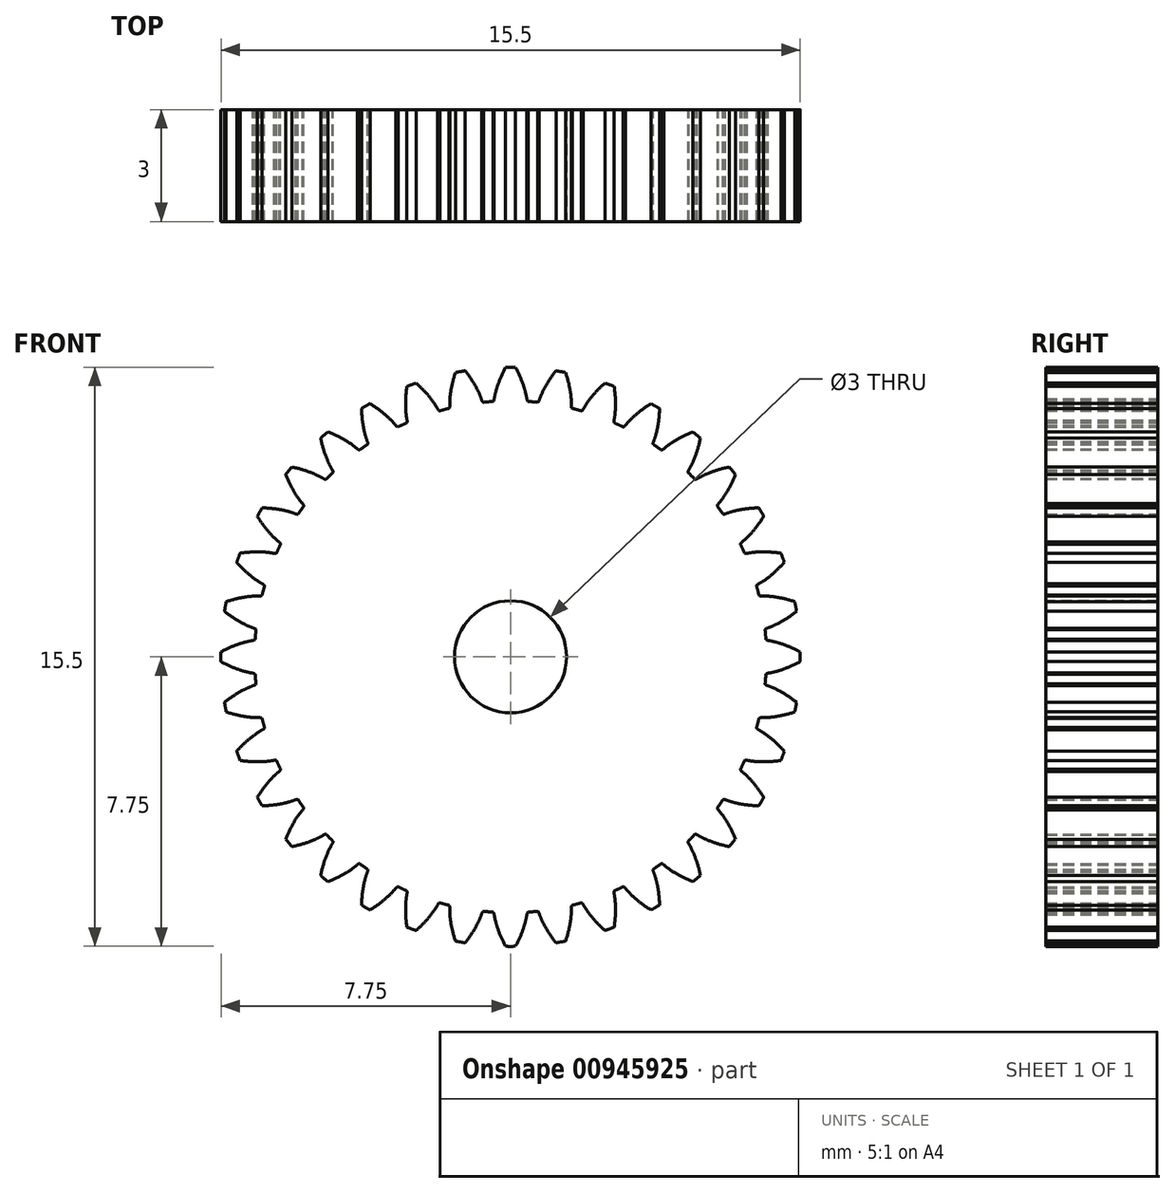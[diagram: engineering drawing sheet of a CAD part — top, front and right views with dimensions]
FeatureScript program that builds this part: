
annotation { "Feature Type Name" : "Feature", "Feature Type Description" : "" }
export const myFeature = defineFeature(function(context is Context, id is Id, definition is map)
    precondition{}
    {
        {
            var Q0;
            Q0=qCreatedBy(makeId("Front.planeOp"),FACE);
            var sketch = newSketch(context, id + "F0", { "sketchPlane" : qUnion([Q0])});
            skLineSegment(sketch, "E0", {"start": v(-0.47, 6.84) * mm, "end": v(-0.47, 6.84) * mm});
            skLineSegment(sketch, "E1", {"start": v(-0.47, 6.84) * mm, "end": v(-0.46, 6.84) * mm});
            skLineSegment(sketch, "E2", {"start": v(-0.46, 6.84) * mm, "end": v(-0.45, 6.85) * mm});
            skLineSegment(sketch, "E3", {"start": v(-0.45, 6.85) * mm, "end": v(-0.45, 6.86) * mm});
            skLineSegment(sketch, "E4", {"start": v(-0.45, 6.86) * mm, "end": v(-0.45, 6.87) * mm});
            skLineSegment(sketch, "E5", {"start": v(-0.45, 6.87) * mm, "end": v(-0.44, 6.88) * mm});
            skLineSegment(sketch, "E6", {"start": v(-0.44, 6.88) * mm, "end": v(-0.44, 6.9) * mm});
            skLineSegment(sketch, "E7", {"start": v(-0.44, 6.9) * mm, "end": v(-0.44, 6.9) * mm});
            skLineSegment(sketch, "E8", {"start": v(-0.44, 6.9) * mm, "end": v(-0.43, 6.92) * mm});
            skLineSegment(sketch, "E9", {"start": v(-0.43, 6.92) * mm, "end": v(-0.43, 6.93) * mm});
            skLineSegment(sketch, "E10", {"start": v(-0.43, 6.93) * mm, "end": v(-0.43, 6.94) * mm});
            skLineSegment(sketch, "E11", {"start": v(-0.43, 6.94) * mm, "end": v(-0.43, 6.96) * mm});
            skLineSegment(sketch, "E12", {"start": v(-0.43, 6.96) * mm, "end": v(-0.42, 6.97) * mm});
            skLineSegment(sketch, "E13", {"start": v(-0.42, 6.97) * mm, "end": v(-0.42, 6.99) * mm});
            skLineSegment(sketch, "E14", {"start": v(-0.42, 6.99) * mm, "end": v(-0.42, 7) * mm});
            skLineSegment(sketch, "E15", {"start": v(-0.42, 7) * mm, "end": v(-0.41, 7.02) * mm});
            skLineSegment(sketch, "E16", {"start": v(-0.41, 7.02) * mm, "end": v(-0.41, 7.04) * mm});
            skLineSegment(sketch, "E17", {"start": v(-0.41, 7.04) * mm, "end": v(-0.4, 7.06) * mm});
            skLineSegment(sketch, "E18", {"start": v(-0.4, 7.06) * mm, "end": v(-0.4, 7.07) * mm});
            skLineSegment(sketch, "E19", {"start": v(-0.4, 7.07) * mm, "end": v(-0.4, 7.1) * mm});
            skLineSegment(sketch, "E20", {"start": v(-0.4, 7.1) * mm, "end": v(-0.4, 7.11) * mm});
            skLineSegment(sketch, "E21", {"start": v(-0.4, 7.11) * mm, "end": v(-0.39, 7.13) * mm});
            skLineSegment(sketch, "E22", {"start": v(-0.39, 7.13) * mm, "end": v(-0.38, 7.15) * mm});
            skLineSegment(sketch, "E23", {"start": v(-0.38, 7.15) * mm, "end": v(-0.38, 7.17) * mm});
            skLineSegment(sketch, "E24", {"start": v(-0.38, 7.17) * mm, "end": v(-0.37, 7.2) * mm});
            skLineSegment(sketch, "E25", {"start": v(-0.37, 7.2) * mm, "end": v(-0.36, 7.21) * mm});
            skLineSegment(sketch, "E26", {"start": v(-0.36, 7.21) * mm, "end": v(-0.36, 7.23) * mm});
            skLineSegment(sketch, "E27", {"start": v(-0.36, 7.23) * mm, "end": v(-0.35, 7.26) * mm});
            skLineSegment(sketch, "E28", {"start": v(-0.35, 7.26) * mm, "end": v(-0.34, 7.28) * mm});
            skLineSegment(sketch, "E29", {"start": v(-0.34, 7.28) * mm, "end": v(-0.33, 7.3) * mm});
            skLineSegment(sketch, "E30", {"start": v(-0.33, 7.3) * mm, "end": v(-0.32, 7.32) * mm});
            skLineSegment(sketch, "E31", {"start": v(-0.32, 7.32) * mm, "end": v(-0.32, 7.35) * mm});
            skLineSegment(sketch, "E32", {"start": v(-0.32, 7.35) * mm, "end": v(-0.3, 7.37) * mm});
            skLineSegment(sketch, "E33", {"start": v(-0.3, 7.37) * mm, "end": v(-0.3, 7.4) * mm});
            skLineSegment(sketch, "E34", {"start": v(-0.3, 7.4) * mm, "end": v(-0.29, 7.42) * mm});
            skLineSegment(sketch, "E35", {"start": v(-0.29, 7.42) * mm, "end": v(-0.28, 7.45) * mm});
            skLineSegment(sketch, "E36", {"start": v(-0.28, 7.45) * mm, "end": v(-0.27, 7.47) * mm});
            skLineSegment(sketch, "E37", {"start": v(-0.27, 7.47) * mm, "end": v(-0.25, 7.5) * mm});
            skLineSegment(sketch, "E38", {"start": v(-0.25, 7.5) * mm, "end": v(-0.24, 7.53) * mm});
            skLineSegment(sketch, "E39", {"start": v(-0.24, 7.53) * mm, "end": v(-0.23, 7.55) * mm});
            skLineSegment(sketch, "E40", {"start": v(-0.23, 7.55) * mm, "end": v(-0.22, 7.58) * mm});
            skLineSegment(sketch, "E41", {"start": v(-0.22, 7.58) * mm, "end": v(-0.2, 7.6) * mm});
            skLineSegment(sketch, "E42", {"start": v(-0.2, 7.6) * mm, "end": v(-0.2, 7.64) * mm});
            skLineSegment(sketch, "E43", {"start": v(-0.2, 7.64) * mm, "end": v(-0.18, 7.66) * mm});
            skLineSegment(sketch, "E44", {"start": v(-0.18, 7.66) * mm, "end": v(-0.16, 7.7) * mm});
            skLineSegment(sketch, "E45", {"start": v(-0.16, 7.7) * mm, "end": v(-0.15, 7.72) * mm});
            skLineSegment(sketch, "E46", {"start": v(-0.15, 7.72) * mm, "end": v(-0.13, 7.75) * mm});
            skLineSegment(sketch, "E47", {"start": v(0.47, 6.84) * mm, "end": v(0.47, 6.84) * mm});
            skLineSegment(sketch, "E48", {"start": v(0.47, 6.84) * mm, "end": v(0.46, 6.84) * mm});
            skLineSegment(sketch, "E49", {"start": v(0.46, 6.84) * mm, "end": v(0.45, 6.85) * mm});
            skLineSegment(sketch, "E50", {"start": v(0.45, 6.85) * mm, "end": v(0.45, 6.86) * mm});
            skLineSegment(sketch, "E51", {"start": v(0.45, 6.86) * mm, "end": v(0.45, 6.87) * mm});
            skLineSegment(sketch, "E52", {"start": v(0.45, 6.87) * mm, "end": v(0.44, 6.88) * mm});
            skLineSegment(sketch, "E53", {"start": v(0.44, 6.88) * mm, "end": v(0.44, 6.9) * mm});
            skLineSegment(sketch, "E54", {"start": v(0.44, 6.9) * mm, "end": v(0.44, 6.9) * mm});
            skLineSegment(sketch, "E55", {"start": v(0.44, 6.9) * mm, "end": v(0.43, 6.92) * mm});
            skLineSegment(sketch, "E56", {"start": v(0.43, 6.92) * mm, "end": v(0.43, 6.93) * mm});
            skLineSegment(sketch, "E57", {"start": v(0.43, 6.93) * mm, "end": v(0.43, 6.94) * mm});
            skLineSegment(sketch, "E58", {"start": v(0.43, 6.94) * mm, "end": v(0.43, 6.96) * mm});
            skLineSegment(sketch, "E59", {"start": v(0.43, 6.96) * mm, "end": v(0.42, 6.97) * mm});
            skLineSegment(sketch, "E60", {"start": v(0.42, 6.97) * mm, "end": v(0.42, 6.99) * mm});
            skLineSegment(sketch, "E61", {"start": v(0.42, 6.99) * mm, "end": v(0.42, 7) * mm});
            skLineSegment(sketch, "E62", {"start": v(0.42, 7) * mm, "end": v(0.41, 7.02) * mm});
            skLineSegment(sketch, "E63", {"start": v(0.41, 7.02) * mm, "end": v(0.41, 7.04) * mm});
            skLineSegment(sketch, "E64", {"start": v(0.41, 7.04) * mm, "end": v(0.4, 7.06) * mm});
            skLineSegment(sketch, "E65", {"start": v(0.4, 7.06) * mm, "end": v(0.4, 7.07) * mm});
            skLineSegment(sketch, "E66", {"start": v(0.4, 7.07) * mm, "end": v(0.4, 7.1) * mm});
            skLineSegment(sketch, "E67", {"start": v(0.4, 7.1) * mm, "end": v(0.4, 7.11) * mm});
            skLineSegment(sketch, "E68", {"start": v(0.4, 7.11) * mm, "end": v(0.39, 7.13) * mm});
            skLineSegment(sketch, "E69", {"start": v(0.39, 7.13) * mm, "end": v(0.38, 7.15) * mm});
            skLineSegment(sketch, "E70", {"start": v(0.38, 7.15) * mm, "end": v(0.38, 7.17) * mm});
            skLineSegment(sketch, "E71", {"start": v(0.38, 7.17) * mm, "end": v(0.37, 7.2) * mm});
            skLineSegment(sketch, "E72", {"start": v(0.37, 7.2) * mm, "end": v(0.36, 7.21) * mm});
            skLineSegment(sketch, "E73", {"start": v(0.36, 7.21) * mm, "end": v(0.36, 7.23) * mm});
            skLineSegment(sketch, "E74", {"start": v(0.36, 7.23) * mm, "end": v(0.35, 7.26) * mm});
            skLineSegment(sketch, "E75", {"start": v(0.35, 7.26) * mm, "end": v(0.34, 7.28) * mm});
            skLineSegment(sketch, "E76", {"start": v(0.34, 7.28) * mm, "end": v(0.33, 7.3) * mm});
            skLineSegment(sketch, "E77", {"start": v(0.33, 7.3) * mm, "end": v(0.32, 7.32) * mm});
            skLineSegment(sketch, "E78", {"start": v(0.32, 7.32) * mm, "end": v(0.32, 7.35) * mm});
            skLineSegment(sketch, "E79", {"start": v(0.32, 7.35) * mm, "end": v(0.3, 7.37) * mm});
            skLineSegment(sketch, "E80", {"start": v(0.3, 7.37) * mm, "end": v(0.3, 7.4) * mm});
            skLineSegment(sketch, "E81", {"start": v(0.3, 7.4) * mm, "end": v(0.29, 7.42) * mm});
            skLineSegment(sketch, "E82", {"start": v(0.29, 7.42) * mm, "end": v(0.28, 7.45) * mm});
            skLineSegment(sketch, "E83", {"start": v(0.28, 7.45) * mm, "end": v(0.27, 7.47) * mm});
            skLineSegment(sketch, "E84", {"start": v(0.27, 7.47) * mm, "end": v(0.25, 7.5) * mm});
            skLineSegment(sketch, "E85", {"start": v(0.25, 7.5) * mm, "end": v(0.24, 7.53) * mm});
            skLineSegment(sketch, "E86", {"start": v(0.24, 7.53) * mm, "end": v(0.23, 7.55) * mm});
            skLineSegment(sketch, "E87", {"start": v(0.23, 7.55) * mm, "end": v(0.22, 7.58) * mm});
            skLineSegment(sketch, "E88", {"start": v(0.22, 7.58) * mm, "end": v(0.2, 7.6) * mm});
            skLineSegment(sketch, "E89", {"start": v(0.2, 7.6) * mm, "end": v(0.2, 7.64) * mm});
            skLineSegment(sketch, "E90", {"start": v(0.2, 7.64) * mm, "end": v(0.18, 7.66) * mm});
            skLineSegment(sketch, "E91", {"start": v(0.18, 7.66) * mm, "end": v(0.16, 7.7) * mm});
            skLineSegment(sketch, "E92", {"start": v(0.16, 7.7) * mm, "end": v(0.15, 7.72) * mm});
            skLineSegment(sketch, "E93", {"start": v(0.15, 7.72) * mm, "end": v(0.13, 7.75) * mm});
            skArc(sketch, "E94", {"start": v(0.13, 7.75) * mm, "mid": v(0, 7.75) * mm, "end": v(-0.13, 7.75) * mm});
            skLineSegment(sketch, "E95", {"start": v(0.72, 6.81) * mm, "end": v(0.73, 6.81) * mm});
            skLineSegment(sketch, "E96", {"start": v(0.73, 6.81) * mm, "end": v(0.73, 6.82) * mm});
            skLineSegment(sketch, "E97", {"start": v(0.73, 6.82) * mm, "end": v(0.74, 6.82) * mm});
            skLineSegment(sketch, "E98", {"start": v(0.74, 6.82) * mm, "end": v(0.75, 6.83) * mm});
            skLineSegment(sketch, "E99", {"start": v(0.75, 6.83) * mm, "end": v(0.75, 6.84) * mm});
            skLineSegment(sketch, "E100", {"start": v(0.75, 6.84) * mm, "end": v(0.76, 6.85) * mm});
            skLineSegment(sketch, "E101", {"start": v(0.76, 6.85) * mm, "end": v(0.77, 6.87) * mm});
            skLineSegment(sketch, "E102", {"start": v(0.77, 6.87) * mm, "end": v(0.77, 6.88) * mm});
            skLineSegment(sketch, "E103", {"start": v(0.77, 6.88) * mm, "end": v(0.77, 6.89) * mm});
            skLineSegment(sketch, "E104", {"start": v(0.77, 6.89) * mm, "end": v(0.78, 6.9) * mm});
            skLineSegment(sketch, "E105", {"start": v(0.78, 6.9) * mm, "end": v(0.78, 6.91) * mm});
            skLineSegment(sketch, "E106", {"start": v(0.78, 6.91) * mm, "end": v(0.79, 6.93) * mm});
            skLineSegment(sketch, "E107", {"start": v(0.79, 6.93) * mm, "end": v(0.8, 6.94) * mm});
            skLineSegment(sketch, "E108", {"start": v(0.8, 6.94) * mm, "end": v(0.8, 6.96) * mm});
            skLineSegment(sketch, "E109", {"start": v(0.8, 6.96) * mm, "end": v(0.8, 6.97) * mm});
            skLineSegment(sketch, "E110", {"start": v(0.8, 6.97) * mm, "end": v(0.81, 6.99) * mm});
            skLineSegment(sketch, "E111", {"start": v(0.81, 6.99) * mm, "end": v(0.82, 7) * mm});
            skLineSegment(sketch, "E112", {"start": v(0.82, 7) * mm, "end": v(0.83, 7.02) * mm});
            skLineSegment(sketch, "E113", {"start": v(0.83, 7.02) * mm, "end": v(0.83, 7.04) * mm});
            skLineSegment(sketch, "E114", {"start": v(0.83, 7.04) * mm, "end": v(0.84, 7.05) * mm});
            skLineSegment(sketch, "E115", {"start": v(0.84, 7.05) * mm, "end": v(0.85, 7.07) * mm});
            skLineSegment(sketch, "E116", {"start": v(0.85, 7.07) * mm, "end": v(0.86, 7.09) * mm});
            skLineSegment(sketch, "E117", {"start": v(0.86, 7.09) * mm, "end": v(0.87, 7.1) * mm});
            skLineSegment(sketch, "E118", {"start": v(0.87, 7.1) * mm, "end": v(0.88, 7.13) * mm});
            skLineSegment(sketch, "E119", {"start": v(0.88, 7.13) * mm, "end": v(0.89, 7.15) * mm});
            skLineSegment(sketch, "E120", {"start": v(0.89, 7.15) * mm, "end": v(0.9, 7.17) * mm});
            skLineSegment(sketch, "E121", {"start": v(0.9, 7.17) * mm, "end": v(0.9, 7.19) * mm});
            skLineSegment(sketch, "E122", {"start": v(0.9, 7.19) * mm, "end": v(0.92, 7.2) * mm});
            skLineSegment(sketch, "E123", {"start": v(0.92, 7.2) * mm, "end": v(0.93, 7.23) * mm});
            skLineSegment(sketch, "E124", {"start": v(0.93, 7.23) * mm, "end": v(0.94, 7.25) * mm});
            skLineSegment(sketch, "E125", {"start": v(0.94, 7.25) * mm, "end": v(0.95, 7.27) * mm});
            skLineSegment(sketch, "E126", {"start": v(0.95, 7.27) * mm, "end": v(0.97, 7.3) * mm});
            skLineSegment(sketch, "E127", {"start": v(0.97, 7.3) * mm, "end": v(0.98, 7.31) * mm});
            skLineSegment(sketch, "E128", {"start": v(0.98, 7.31) * mm, "end": v(1, 7.34) * mm});
            skLineSegment(sketch, "E129", {"start": v(1, 7.34) * mm, "end": v(1, 7.36) * mm});
            skLineSegment(sketch, "E130", {"start": v(1, 7.36) * mm, "end": v(1.02, 7.38) * mm});
            skLineSegment(sketch, "E131", {"start": v(1.02, 7.38) * mm, "end": v(1.04, 7.4) * mm});
            skLineSegment(sketch, "E132", {"start": v(1.04, 7.4) * mm, "end": v(1.05, 7.43) * mm});
            skLineSegment(sketch, "E133", {"start": v(1.05, 7.43) * mm, "end": v(1.07, 7.45) * mm});
            skLineSegment(sketch, "E134", {"start": v(1.07, 7.45) * mm, "end": v(1.09, 7.48) * mm});
            skLineSegment(sketch, "E135", {"start": v(1.09, 7.48) * mm, "end": v(1.1, 7.5) * mm});
            skLineSegment(sketch, "E136", {"start": v(1.1, 7.5) * mm, "end": v(1.12, 7.53) * mm});
            skLineSegment(sketch, "E137", {"start": v(1.12, 7.53) * mm, "end": v(1.14, 7.55) * mm});
            skLineSegment(sketch, "E138", {"start": v(1.14, 7.55) * mm, "end": v(1.16, 7.58) * mm});
            skLineSegment(sketch, "E139", {"start": v(1.16, 7.58) * mm, "end": v(1.18, 7.6) * mm});
            skLineSegment(sketch, "E140", {"start": v(1.18, 7.6) * mm, "end": v(1.2, 7.63) * mm});
            skLineSegment(sketch, "E141", {"start": v(1.2, 7.63) * mm, "end": v(1.22, 7.66) * mm});
            skLineSegment(sketch, "E142", {"start": v(1.65, 6.65) * mm, "end": v(1.65, 6.65) * mm});
            skLineSegment(sketch, "E143", {"start": v(1.65, 6.65) * mm, "end": v(1.64, 6.66) * mm});
            skLineSegment(sketch, "E144", {"start": v(1.64, 6.66) * mm, "end": v(1.64, 6.66) * mm});
            skLineSegment(sketch, "E145", {"start": v(1.64, 6.66) * mm, "end": v(1.63, 6.67) * mm});
            skLineSegment(sketch, "E146", {"start": v(1.63, 6.67) * mm, "end": v(1.63, 6.68) * mm});
            skLineSegment(sketch, "E147", {"start": v(1.63, 6.68) * mm, "end": v(1.63, 6.7) * mm});
            skLineSegment(sketch, "E148", {"start": v(1.63, 6.7) * mm, "end": v(1.63, 6.71) * mm});
            skLineSegment(sketch, "E149", {"start": v(1.63, 6.71) * mm, "end": v(1.63, 6.72) * mm});
            skLineSegment(sketch, "E150", {"start": v(1.63, 6.72) * mm, "end": v(1.63, 6.74) * mm});
            skLineSegment(sketch, "E151", {"start": v(1.63, 6.74) * mm, "end": v(1.63, 6.75) * mm});
            skLineSegment(sketch, "E152", {"start": v(1.63, 6.75) * mm, "end": v(1.63, 6.76) * mm});
            skLineSegment(sketch, "E153", {"start": v(1.63, 6.76) * mm, "end": v(1.63, 6.78) * mm});
            skLineSegment(sketch, "E154", {"start": v(1.63, 6.78) * mm, "end": v(1.63, 6.8) * mm});
            skLineSegment(sketch, "E155", {"start": v(1.63, 6.8) * mm, "end": v(1.63, 6.81) * mm});
            skLineSegment(sketch, "E156", {"start": v(1.63, 6.81) * mm, "end": v(1.63, 6.83) * mm});
            skLineSegment(sketch, "E157", {"start": v(1.63, 6.83) * mm, "end": v(1.63, 6.84) * mm});
            skLineSegment(sketch, "E158", {"start": v(1.63, 6.84) * mm, "end": v(1.63, 6.86) * mm});
            skLineSegment(sketch, "E159", {"start": v(1.63, 6.86) * mm, "end": v(1.63, 6.88) * mm});
            skLineSegment(sketch, "E160", {"start": v(1.63, 6.88) * mm, "end": v(1.62, 6.9) * mm});
            skLineSegment(sketch, "E161", {"start": v(1.62, 6.9) * mm, "end": v(1.62, 6.92) * mm});
            skLineSegment(sketch, "E162", {"start": v(1.62, 6.92) * mm, "end": v(1.62, 6.94) * mm});
            skLineSegment(sketch, "E163", {"start": v(1.62, 6.94) * mm, "end": v(1.62, 6.96) * mm});
            skLineSegment(sketch, "E164", {"start": v(1.62, 6.96) * mm, "end": v(1.62, 6.98) * mm});
            skLineSegment(sketch, "E165", {"start": v(1.62, 6.98) * mm, "end": v(1.61, 7) * mm});
            skLineSegment(sketch, "E166", {"start": v(1.61, 7) * mm, "end": v(1.61, 7.02) * mm});
            skLineSegment(sketch, "E167", {"start": v(1.61, 7.02) * mm, "end": v(1.6, 7.04) * mm});
            skLineSegment(sketch, "E168", {"start": v(1.6, 7.04) * mm, "end": v(1.6, 7.06) * mm});
            skLineSegment(sketch, "E169", {"start": v(1.6, 7.06) * mm, "end": v(1.6, 7.09) * mm});
            skLineSegment(sketch, "E170", {"start": v(1.6, 7.09) * mm, "end": v(1.6, 7.1) * mm});
            skLineSegment(sketch, "E171", {"start": v(1.6, 7.1) * mm, "end": v(1.6, 7.13) * mm});
            skLineSegment(sketch, "E172", {"start": v(1.6, 7.13) * mm, "end": v(1.6, 7.16) * mm});
            skLineSegment(sketch, "E173", {"start": v(1.6, 7.16) * mm, "end": v(1.59, 7.18) * mm});
            skLineSegment(sketch, "E174", {"start": v(1.59, 7.18) * mm, "end": v(1.58, 7.2) * mm});
            skLineSegment(sketch, "E175", {"start": v(1.58, 7.2) * mm, "end": v(1.58, 7.23) * mm});
            skLineSegment(sketch, "E176", {"start": v(1.58, 7.23) * mm, "end": v(1.57, 7.26) * mm});
            skLineSegment(sketch, "E177", {"start": v(1.57, 7.26) * mm, "end": v(1.57, 7.29) * mm});
            skLineSegment(sketch, "E178", {"start": v(1.57, 7.29) * mm, "end": v(1.56, 7.31) * mm});
            skLineSegment(sketch, "E179", {"start": v(1.56, 7.31) * mm, "end": v(1.55, 7.34) * mm});
            skLineSegment(sketch, "E180", {"start": v(1.55, 7.34) * mm, "end": v(1.55, 7.37) * mm});
            skLineSegment(sketch, "E181", {"start": v(1.55, 7.37) * mm, "end": v(1.54, 7.4) * mm});
            skLineSegment(sketch, "E182", {"start": v(1.54, 7.4) * mm, "end": v(1.53, 7.43) * mm});
            skLineSegment(sketch, "E183", {"start": v(1.53, 7.43) * mm, "end": v(1.52, 7.46) * mm});
            skLineSegment(sketch, "E184", {"start": v(1.52, 7.46) * mm, "end": v(1.51, 7.49) * mm});
            skLineSegment(sketch, "E185", {"start": v(1.51, 7.49) * mm, "end": v(1.5, 7.52) * mm});
            skLineSegment(sketch, "E186", {"start": v(1.5, 7.52) * mm, "end": v(1.5, 7.55) * mm});
            skLineSegment(sketch, "E187", {"start": v(1.5, 7.55) * mm, "end": v(1.49, 7.58) * mm});
            skLineSegment(sketch, "E188", {"start": v(1.49, 7.58) * mm, "end": v(1.47, 7.61) * mm});
            skArc(sketch, "E189", {"start": v(1.47, 7.61) * mm, "mid": v(1.35, 7.63) * mm, "end": v(1.22, 7.66) * mm});
            skLineSegment(sketch, "E190", {"start": v(1.9, 6.58) * mm, "end": v(1.9, 6.58) * mm});
            skLineSegment(sketch, "E191", {"start": v(1.9, 6.58) * mm, "end": v(1.9, 6.59) * mm});
            skLineSegment(sketch, "E192", {"start": v(1.9, 6.59) * mm, "end": v(1.91, 6.59) * mm});
            skLineSegment(sketch, "E193", {"start": v(1.91, 6.59) * mm, "end": v(1.92, 6.6) * mm});
            skLineSegment(sketch, "E194", {"start": v(1.92, 6.6) * mm, "end": v(1.93, 6.6) * mm});
            skLineSegment(sketch, "E195", {"start": v(1.93, 6.6) * mm, "end": v(1.94, 6.62) * mm});
            skLineSegment(sketch, "E196", {"start": v(1.94, 6.62) * mm, "end": v(1.95, 6.63) * mm});
            skLineSegment(sketch, "E197", {"start": v(1.95, 6.63) * mm, "end": v(1.95, 6.64) * mm});
            skLineSegment(sketch, "E198", {"start": v(1.95, 6.64) * mm, "end": v(1.96, 6.65) * mm});
            skLineSegment(sketch, "E199", {"start": v(1.96, 6.65) * mm, "end": v(1.96, 6.66) * mm});
            skLineSegment(sketch, "E200", {"start": v(1.96, 6.66) * mm, "end": v(1.97, 6.67) * mm});
            skLineSegment(sketch, "E201", {"start": v(1.97, 6.67) * mm, "end": v(1.98, 6.69) * mm});
            skLineSegment(sketch, "E202", {"start": v(1.98, 6.69) * mm, "end": v(1.99, 6.7) * mm});
            skLineSegment(sketch, "E203", {"start": v(1.99, 6.7) * mm, "end": v(2, 6.71) * mm});
            skLineSegment(sketch, "E204", {"start": v(2, 6.71) * mm, "end": v(2, 6.73) * mm});
            skLineSegment(sketch, "E205", {"start": v(2, 6.73) * mm, "end": v(2.01, 6.74) * mm});
            skLineSegment(sketch, "E206", {"start": v(2.01, 6.74) * mm, "end": v(2.02, 6.75) * mm});
            skLineSegment(sketch, "E207", {"start": v(2.02, 6.75) * mm, "end": v(2.03, 6.77) * mm});
            skLineSegment(sketch, "E208", {"start": v(2.03, 6.77) * mm, "end": v(2.04, 6.78) * mm});
            skLineSegment(sketch, "E209", {"start": v(2.04, 6.78) * mm, "end": v(2.05, 6.8) * mm});
            skLineSegment(sketch, "E210", {"start": v(2.05, 6.8) * mm, "end": v(2.06, 6.82) * mm});
            skLineSegment(sketch, "E211", {"start": v(2.06, 6.82) * mm, "end": v(2.08, 6.83) * mm});
            skLineSegment(sketch, "E212", {"start": v(2.08, 6.83) * mm, "end": v(2.09, 6.85) * mm});
            skLineSegment(sketch, "E213", {"start": v(2.09, 6.85) * mm, "end": v(2.1, 6.87) * mm});
            skLineSegment(sketch, "E214", {"start": v(2.1, 6.87) * mm, "end": v(2.11, 6.88) * mm});
            skLineSegment(sketch, "E215", {"start": v(2.11, 6.88) * mm, "end": v(2.13, 6.9) * mm});
            skLineSegment(sketch, "E216", {"start": v(2.13, 6.9) * mm, "end": v(2.14, 6.92) * mm});
            skLineSegment(sketch, "E217", {"start": v(2.14, 6.92) * mm, "end": v(2.15, 6.94) * mm});
            skLineSegment(sketch, "E218", {"start": v(2.15, 6.94) * mm, "end": v(2.17, 6.96) * mm});
            skLineSegment(sketch, "E219", {"start": v(2.17, 6.96) * mm, "end": v(2.18, 6.97) * mm});
            skLineSegment(sketch, "E220", {"start": v(2.18, 6.97) * mm, "end": v(2.2, 7) * mm});
            skLineSegment(sketch, "E221", {"start": v(2.2, 7) * mm, "end": v(2.22, 7.01) * mm});
            skLineSegment(sketch, "E222", {"start": v(2.22, 7.01) * mm, "end": v(2.23, 7.03) * mm});
            skLineSegment(sketch, "E223", {"start": v(2.23, 7.03) * mm, "end": v(2.25, 7.05) * mm});
            skLineSegment(sketch, "E224", {"start": v(2.25, 7.05) * mm, "end": v(2.27, 7.07) * mm});
            skLineSegment(sketch, "E225", {"start": v(2.27, 7.07) * mm, "end": v(2.29, 7.1) * mm});
            skLineSegment(sketch, "E226", {"start": v(2.29, 7.1) * mm, "end": v(2.3, 7.11) * mm});
            skLineSegment(sketch, "E227", {"start": v(2.3, 7.11) * mm, "end": v(2.33, 7.13) * mm});
            skLineSegment(sketch, "E228", {"start": v(2.33, 7.13) * mm, "end": v(2.35, 7.15) * mm});
            skLineSegment(sketch, "E229", {"start": v(2.35, 7.15) * mm, "end": v(2.37, 7.18) * mm});
            skLineSegment(sketch, "E230", {"start": v(2.37, 7.18) * mm, "end": v(2.39, 7.2) * mm});
            skLineSegment(sketch, "E231", {"start": v(2.39, 7.2) * mm, "end": v(2.41, 7.22) * mm});
            skLineSegment(sketch, "E232", {"start": v(2.41, 7.22) * mm, "end": v(2.43, 7.24) * mm});
            skLineSegment(sketch, "E233", {"start": v(2.43, 7.24) * mm, "end": v(2.46, 7.26) * mm});
            skLineSegment(sketch, "E234", {"start": v(2.46, 7.26) * mm, "end": v(2.48, 7.28) * mm});
            skLineSegment(sketch, "E235", {"start": v(2.48, 7.28) * mm, "end": v(2.5, 7.3) * mm});
            skLineSegment(sketch, "E236", {"start": v(2.5, 7.3) * mm, "end": v(2.53, 7.33) * mm});
            skLineSegment(sketch, "E237", {"start": v(2.78, 6.26) * mm, "end": v(2.78, 6.27) * mm});
            skLineSegment(sketch, "E238", {"start": v(2.78, 6.27) * mm, "end": v(2.77, 6.27) * mm});
            skLineSegment(sketch, "E239", {"start": v(2.77, 6.27) * mm, "end": v(2.77, 6.28) * mm});
            skLineSegment(sketch, "E240", {"start": v(2.77, 6.28) * mm, "end": v(2.77, 6.29) * mm});
            skLineSegment(sketch, "E241", {"start": v(2.77, 6.29) * mm, "end": v(2.77, 6.3) * mm});
            skLineSegment(sketch, "E242", {"start": v(2.77, 6.3) * mm, "end": v(2.77, 6.31) * mm});
            skLineSegment(sketch, "E243", {"start": v(2.77, 6.31) * mm, "end": v(2.77, 6.33) * mm});
            skLineSegment(sketch, "E244", {"start": v(2.77, 6.33) * mm, "end": v(2.77, 6.34) * mm});
            skLineSegment(sketch, "E245", {"start": v(2.77, 6.34) * mm, "end": v(2.77, 6.35) * mm});
            skLineSegment(sketch, "E246", {"start": v(2.77, 6.35) * mm, "end": v(2.78, 6.37) * mm});
            skLineSegment(sketch, "E247", {"start": v(2.78, 6.37) * mm, "end": v(2.78, 6.38) * mm});
            skLineSegment(sketch, "E248", {"start": v(2.78, 6.38) * mm, "end": v(2.78, 6.4) * mm});
            skLineSegment(sketch, "E249", {"start": v(2.78, 6.4) * mm, "end": v(2.78, 6.4) * mm});
            skLineSegment(sketch, "E250", {"start": v(2.78, 6.4) * mm, "end": v(2.79, 6.42) * mm});
            skLineSegment(sketch, "E251", {"start": v(2.79, 6.42) * mm, "end": v(2.79, 6.44) * mm});
            skLineSegment(sketch, "E252", {"start": v(2.79, 6.44) * mm, "end": v(2.8, 6.46) * mm});
            skLineSegment(sketch, "E253", {"start": v(2.8, 6.46) * mm, "end": v(2.8, 6.47) * mm});
            skLineSegment(sketch, "E254", {"start": v(2.8, 6.47) * mm, "end": v(2.8, 6.5) * mm});
            skLineSegment(sketch, "E255", {"start": v(2.8, 6.5) * mm, "end": v(2.8, 6.51) * mm});
            skLineSegment(sketch, "E256", {"start": v(2.8, 6.51) * mm, "end": v(2.8, 6.53) * mm});
            skLineSegment(sketch, "E257", {"start": v(2.8, 6.53) * mm, "end": v(2.8, 6.55) * mm});
            skLineSegment(sketch, "E258", {"start": v(2.8, 6.55) * mm, "end": v(2.8, 6.57) * mm});
            skLineSegment(sketch, "E259", {"start": v(2.8, 6.57) * mm, "end": v(2.8, 6.59) * mm});
            skLineSegment(sketch, "E260", {"start": v(2.8, 6.59) * mm, "end": v(2.8, 6.6) * mm});
            skLineSegment(sketch, "E261", {"start": v(2.8, 6.6) * mm, "end": v(2.8, 6.63) * mm});
            skLineSegment(sketch, "E262", {"start": v(2.8, 6.63) * mm, "end": v(2.8, 6.65) * mm});
            skLineSegment(sketch, "E263", {"start": v(2.8, 6.65) * mm, "end": v(2.8, 6.68) * mm});
            skLineSegment(sketch, "E264", {"start": v(2.8, 6.68) * mm, "end": v(2.8, 6.7) * mm});
            skLineSegment(sketch, "E265", {"start": v(2.8, 6.7) * mm, "end": v(2.8, 6.72) * mm});
            skLineSegment(sketch, "E266", {"start": v(2.8, 6.72) * mm, "end": v(2.8, 6.75) * mm});
            skLineSegment(sketch, "E267", {"start": v(2.8, 6.75) * mm, "end": v(2.8, 6.77) * mm});
            skLineSegment(sketch, "E268", {"start": v(2.8, 6.77) * mm, "end": v(2.8, 6.8) * mm});
            skLineSegment(sketch, "E269", {"start": v(2.8, 6.8) * mm, "end": v(2.8, 6.82) * mm});
            skLineSegment(sketch, "E270", {"start": v(2.8, 6.82) * mm, "end": v(2.8, 6.85) * mm});
            skLineSegment(sketch, "E271", {"start": v(2.8, 6.85) * mm, "end": v(2.8, 6.88) * mm});
            skLineSegment(sketch, "E272", {"start": v(2.8, 6.88) * mm, "end": v(2.8, 6.9) * mm});
            skLineSegment(sketch, "E273", {"start": v(2.8, 6.9) * mm, "end": v(2.8, 6.93) * mm});
            skLineSegment(sketch, "E274", {"start": v(2.8, 6.93) * mm, "end": v(2.8, 6.96) * mm});
            skLineSegment(sketch, "E275", {"start": v(2.8, 6.96) * mm, "end": v(2.8, 6.99) * mm});
            skLineSegment(sketch, "E276", {"start": v(2.8, 6.99) * mm, "end": v(2.8, 7.02) * mm});
            skLineSegment(sketch, "E277", {"start": v(2.8, 7.02) * mm, "end": v(2.8, 7.05) * mm});
            skLineSegment(sketch, "E278", {"start": v(2.8, 7.05) * mm, "end": v(2.8, 7.08) * mm});
            skLineSegment(sketch, "E279", {"start": v(2.8, 7.08) * mm, "end": v(2.8, 7.1) * mm});
            skLineSegment(sketch, "E280", {"start": v(2.8, 7.1) * mm, "end": v(2.79, 7.14) * mm});
            skLineSegment(sketch, "E281", {"start": v(2.79, 7.14) * mm, "end": v(2.78, 7.17) * mm});
            skLineSegment(sketch, "E282", {"start": v(2.78, 7.17) * mm, "end": v(2.78, 7.2) * mm});
            skLineSegment(sketch, "E283", {"start": v(2.78, 7.2) * mm, "end": v(2.77, 7.24) * mm});
            skArc(sketch, "E284", {"start": v(2.77, 7.24) * mm, "mid": v(2.65, 7.28) * mm, "end": v(2.53, 7.33) * mm});
            skLineSegment(sketch, "E285", {"start": v(3, 6.16) * mm, "end": v(3.02, 6.15) * mm});
            skLineSegment(sketch, "E286", {"start": v(3.02, 6.15) * mm, "end": v(3.02, 6.15) * mm});
            skLineSegment(sketch, "E287", {"start": v(3.02, 6.15) * mm, "end": v(3.03, 6.16) * mm});
            skLineSegment(sketch, "E288", {"start": v(3.03, 6.16) * mm, "end": v(3.04, 6.16) * mm});
            skLineSegment(sketch, "E289", {"start": v(3.04, 6.16) * mm, "end": v(3.05, 6.17) * mm});
            skLineSegment(sketch, "E290", {"start": v(3.05, 6.17) * mm, "end": v(3.06, 6.18) * mm});
            skLineSegment(sketch, "E291", {"start": v(3.06, 6.18) * mm, "end": v(3.07, 6.19) * mm});
            skLineSegment(sketch, "E292", {"start": v(3.07, 6.19) * mm, "end": v(3.07, 6.2) * mm});
            skLineSegment(sketch, "E293", {"start": v(3.07, 6.2) * mm, "end": v(3.08, 6.2) * mm});
            skLineSegment(sketch, "E294", {"start": v(3.08, 6.2) * mm, "end": v(3.1, 6.22) * mm});
            skLineSegment(sketch, "E295", {"start": v(3.1, 6.22) * mm, "end": v(3.1, 6.23) * mm});
            skLineSegment(sketch, "E296", {"start": v(3.1, 6.23) * mm, "end": v(3.11, 6.24) * mm});
            skLineSegment(sketch, "E297", {"start": v(3.11, 6.24) * mm, "end": v(3.12, 6.25) * mm});
            skLineSegment(sketch, "E298", {"start": v(3.12, 6.25) * mm, "end": v(3.13, 6.26) * mm});
            skLineSegment(sketch, "E299", {"start": v(3.13, 6.26) * mm, "end": v(3.14, 6.28) * mm});
            skLineSegment(sketch, "E300", {"start": v(3.14, 6.28) * mm, "end": v(3.15, 6.29) * mm});
            skLineSegment(sketch, "E301", {"start": v(3.15, 6.29) * mm, "end": v(3.16, 6.3) * mm});
            skLineSegment(sketch, "E302", {"start": v(3.16, 6.3) * mm, "end": v(3.18, 6.31) * mm});
            skLineSegment(sketch, "E303", {"start": v(3.18, 6.31) * mm, "end": v(3.19, 6.33) * mm});
            skLineSegment(sketch, "E304", {"start": v(3.19, 6.33) * mm, "end": v(3.2, 6.34) * mm});
            skLineSegment(sketch, "E305", {"start": v(3.2, 6.34) * mm, "end": v(3.22, 6.35) * mm});
            skLineSegment(sketch, "E306", {"start": v(3.22, 6.35) * mm, "end": v(3.23, 6.37) * mm});
            skLineSegment(sketch, "E307", {"start": v(3.23, 6.37) * mm, "end": v(3.24, 6.38) * mm});
            skLineSegment(sketch, "E308", {"start": v(3.24, 6.38) * mm, "end": v(3.26, 6.4) * mm});
            skLineSegment(sketch, "E309", {"start": v(3.26, 6.4) * mm, "end": v(3.28, 6.41) * mm});
            skLineSegment(sketch, "E310", {"start": v(3.28, 6.41) * mm, "end": v(3.3, 6.43) * mm});
            skLineSegment(sketch, "E311", {"start": v(3.3, 6.43) * mm, "end": v(3.3, 6.44) * mm});
            skLineSegment(sketch, "E312", {"start": v(3.3, 6.44) * mm, "end": v(3.33, 6.46) * mm});
            skLineSegment(sketch, "E313", {"start": v(3.33, 6.46) * mm, "end": v(3.34, 6.47) * mm});
            skLineSegment(sketch, "E314", {"start": v(3.34, 6.47) * mm, "end": v(3.36, 6.49) * mm});
            skLineSegment(sketch, "E315", {"start": v(3.36, 6.49) * mm, "end": v(3.38, 6.5) * mm});
            skLineSegment(sketch, "E316", {"start": v(3.38, 6.5) * mm, "end": v(3.4, 6.52) * mm});
            skLineSegment(sketch, "E317", {"start": v(3.4, 6.52) * mm, "end": v(3.42, 6.54) * mm});
            skLineSegment(sketch, "E318", {"start": v(3.42, 6.54) * mm, "end": v(3.44, 6.55) * mm});
            skLineSegment(sketch, "E319", {"start": v(3.44, 6.55) * mm, "end": v(3.46, 6.57) * mm});
            skLineSegment(sketch, "E320", {"start": v(3.46, 6.57) * mm, "end": v(3.48, 6.59) * mm});
            skLineSegment(sketch, "E321", {"start": v(3.48, 6.59) * mm, "end": v(3.5, 6.6) * mm});
            skLineSegment(sketch, "E322", {"start": v(3.5, 6.6) * mm, "end": v(3.53, 6.62) * mm});
            skLineSegment(sketch, "E323", {"start": v(3.53, 6.62) * mm, "end": v(3.55, 6.64) * mm});
            skLineSegment(sketch, "E324", {"start": v(3.55, 6.64) * mm, "end": v(3.58, 6.66) * mm});
            skLineSegment(sketch, "E325", {"start": v(3.58, 6.66) * mm, "end": v(3.6, 6.67) * mm});
            skLineSegment(sketch, "E326", {"start": v(3.6, 6.67) * mm, "end": v(3.63, 6.7) * mm});
            skLineSegment(sketch, "E327", {"start": v(3.63, 6.7) * mm, "end": v(3.65, 6.7) * mm});
            skLineSegment(sketch, "E328", {"start": v(3.65, 6.7) * mm, "end": v(3.68, 6.73) * mm});
            skLineSegment(sketch, "E329", {"start": v(3.68, 6.73) * mm, "end": v(3.7, 6.74) * mm});
            skLineSegment(sketch, "E330", {"start": v(3.7, 6.74) * mm, "end": v(3.73, 6.76) * mm});
            skLineSegment(sketch, "E331", {"start": v(3.73, 6.76) * mm, "end": v(3.76, 6.78) * mm});
            skLineSegment(sketch, "E332", {"start": v(3.83, 5.68) * mm, "end": v(3.82, 5.69) * mm});
            skLineSegment(sketch, "E333", {"start": v(3.82, 5.69) * mm, "end": v(3.82, 5.7) * mm});
            skLineSegment(sketch, "E334", {"start": v(3.82, 5.7) * mm, "end": v(3.82, 5.7) * mm});
            skLineSegment(sketch, "E335", {"start": v(3.82, 5.7) * mm, "end": v(3.82, 5.71) * mm});
            skLineSegment(sketch, "E336", {"start": v(3.82, 5.71) * mm, "end": v(3.82, 5.72) * mm});
            skLineSegment(sketch, "E337", {"start": v(3.82, 5.72) * mm, "end": v(3.82, 5.74) * mm});
            skLineSegment(sketch, "E338", {"start": v(3.82, 5.74) * mm, "end": v(3.83, 5.75) * mm});
            skLineSegment(sketch, "E339", {"start": v(3.83, 5.75) * mm, "end": v(3.83, 5.76) * mm});
            skLineSegment(sketch, "E340", {"start": v(3.83, 5.76) * mm, "end": v(3.83, 5.77) * mm});
            skLineSegment(sketch, "E341", {"start": v(3.83, 5.77) * mm, "end": v(3.84, 5.79) * mm});
            skLineSegment(sketch, "E342", {"start": v(3.84, 5.79) * mm, "end": v(3.84, 5.8) * mm});
            skLineSegment(sketch, "E343", {"start": v(3.84, 5.8) * mm, "end": v(3.85, 5.81) * mm});
            skLineSegment(sketch, "E344", {"start": v(3.85, 5.81) * mm, "end": v(3.85, 5.83) * mm});
            skLineSegment(sketch, "E345", {"start": v(3.85, 5.83) * mm, "end": v(3.86, 5.84) * mm});
            skLineSegment(sketch, "E346", {"start": v(3.86, 5.84) * mm, "end": v(3.86, 5.86) * mm});
            skLineSegment(sketch, "E347", {"start": v(3.86, 5.86) * mm, "end": v(3.87, 5.87) * mm});
            skLineSegment(sketch, "E348", {"start": v(3.87, 5.87) * mm, "end": v(3.87, 5.9) * mm});
            skLineSegment(sketch, "E349", {"start": v(3.87, 5.9) * mm, "end": v(3.88, 5.9) * mm});
            skLineSegment(sketch, "E350", {"start": v(3.88, 5.9) * mm, "end": v(3.89, 5.93) * mm});
            skLineSegment(sketch, "E351", {"start": v(3.89, 5.93) * mm, "end": v(3.9, 5.94) * mm});
            skLineSegment(sketch, "E352", {"start": v(3.9, 5.94) * mm, "end": v(3.9, 5.96) * mm});
            skLineSegment(sketch, "E353", {"start": v(3.9, 5.96) * mm, "end": v(3.9, 5.98) * mm});
            skLineSegment(sketch, "E354", {"start": v(3.9, 5.98) * mm, "end": v(3.9, 6) * mm});
            skLineSegment(sketch, "E355", {"start": v(3.9, 6) * mm, "end": v(3.91, 6.02) * mm});
            skLineSegment(sketch, "E356", {"start": v(3.91, 6.02) * mm, "end": v(3.92, 6.04) * mm});
            skLineSegment(sketch, "E357", {"start": v(3.92, 6.04) * mm, "end": v(3.92, 6.06) * mm});
            skLineSegment(sketch, "E358", {"start": v(3.92, 6.06) * mm, "end": v(3.92, 6.09) * mm});
            skLineSegment(sketch, "E359", {"start": v(3.92, 6.09) * mm, "end": v(3.93, 6.1) * mm});
            skLineSegment(sketch, "E360", {"start": v(3.93, 6.1) * mm, "end": v(3.93, 6.13) * mm});
            skLineSegment(sketch, "E361", {"start": v(3.93, 6.13) * mm, "end": v(3.94, 6.16) * mm});
            skLineSegment(sketch, "E362", {"start": v(3.94, 6.16) * mm, "end": v(3.94, 6.18) * mm});
            skLineSegment(sketch, "E363", {"start": v(3.94, 6.18) * mm, "end": v(3.95, 6.2) * mm});
            skLineSegment(sketch, "E364", {"start": v(3.95, 6.2) * mm, "end": v(3.95, 6.23) * mm});
            skLineSegment(sketch, "E365", {"start": v(3.95, 6.23) * mm, "end": v(3.96, 6.26) * mm});
            skLineSegment(sketch, "E366", {"start": v(3.96, 6.26) * mm, "end": v(3.96, 6.28) * mm});
            skLineSegment(sketch, "E367", {"start": v(3.96, 6.28) * mm, "end": v(3.96, 6.31) * mm});
            skLineSegment(sketch, "E368", {"start": v(3.96, 6.31) * mm, "end": v(3.97, 6.34) * mm});
            skLineSegment(sketch, "E369", {"start": v(3.97, 6.34) * mm, "end": v(3.97, 6.37) * mm});
            skLineSegment(sketch, "E370", {"start": v(3.97, 6.37) * mm, "end": v(3.97, 6.4) * mm});
            skLineSegment(sketch, "E371", {"start": v(3.97, 6.4) * mm, "end": v(3.98, 6.43) * mm});
            skLineSegment(sketch, "E372", {"start": v(3.98, 6.43) * mm, "end": v(3.98, 6.46) * mm});
            skLineSegment(sketch, "E373", {"start": v(3.98, 6.46) * mm, "end": v(3.98, 6.49) * mm});
            skLineSegment(sketch, "E374", {"start": v(3.98, 6.49) * mm, "end": v(3.98, 6.52) * mm});
            skLineSegment(sketch, "E375", {"start": v(3.98, 6.52) * mm, "end": v(3.98, 6.55) * mm});
            skLineSegment(sketch, "E376", {"start": v(3.98, 6.55) * mm, "end": v(3.99, 6.58) * mm});
            skLineSegment(sketch, "E377", {"start": v(3.99, 6.58) * mm, "end": v(3.99, 6.61) * mm});
            skLineSegment(sketch, "E378", {"start": v(3.99, 6.61) * mm, "end": v(3.99, 6.65) * mm});
            skArc(sketch, "E379", {"start": v(3.99, 6.65) * mm, "mid": v(3.88, 6.71) * mm, "end": v(3.76, 6.78) * mm});
            skLineSegment(sketch, "E380", {"start": v(4.03, 5.54) * mm, "end": v(4.04, 5.54) * mm});
            skLineSegment(sketch, "E381", {"start": v(4.04, 5.54) * mm, "end": v(4.04, 5.54) * mm});
            skLineSegment(sketch, "E382", {"start": v(4.04, 5.54) * mm, "end": v(4.05, 5.54) * mm});
            skLineSegment(sketch, "E383", {"start": v(4.05, 5.54) * mm, "end": v(4.06, 5.54) * mm});
            skLineSegment(sketch, "E384", {"start": v(4.06, 5.54) * mm, "end": v(4.07, 5.55) * mm});
            skLineSegment(sketch, "E385", {"start": v(4.07, 5.55) * mm, "end": v(4.08, 5.55) * mm});
            skLineSegment(sketch, "E386", {"start": v(4.08, 5.55) * mm, "end": v(4.1, 5.56) * mm});
            skLineSegment(sketch, "E387", {"start": v(4.1, 5.56) * mm, "end": v(4.1, 5.57) * mm});
            skLineSegment(sketch, "E388", {"start": v(4.1, 5.57) * mm, "end": v(4.11, 5.58) * mm});
            skLineSegment(sketch, "E389", {"start": v(4.11, 5.58) * mm, "end": v(4.12, 5.59) * mm});
            skLineSegment(sketch, "E390", {"start": v(4.12, 5.59) * mm, "end": v(4.14, 5.6) * mm});
            skLineSegment(sketch, "E391", {"start": v(4.14, 5.6) * mm, "end": v(4.15, 5.6) * mm});
            skLineSegment(sketch, "E392", {"start": v(4.15, 5.6) * mm, "end": v(4.16, 5.62) * mm});
            skLineSegment(sketch, "E393", {"start": v(4.16, 5.62) * mm, "end": v(4.17, 5.63) * mm});
            skLineSegment(sketch, "E394", {"start": v(4.17, 5.63) * mm, "end": v(4.18, 5.64) * mm});
            skLineSegment(sketch, "E395", {"start": v(4.18, 5.64) * mm, "end": v(4.2, 5.65) * mm});
            skLineSegment(sketch, "E396", {"start": v(4.2, 5.65) * mm, "end": v(4.21, 5.66) * mm});
            skLineSegment(sketch, "E397", {"start": v(4.21, 5.66) * mm, "end": v(4.22, 5.67) * mm});
            skLineSegment(sketch, "E398", {"start": v(4.22, 5.67) * mm, "end": v(4.24, 5.68) * mm});
            skLineSegment(sketch, "E399", {"start": v(4.24, 5.68) * mm, "end": v(4.25, 5.69) * mm});
            skLineSegment(sketch, "E400", {"start": v(4.25, 5.69) * mm, "end": v(4.27, 5.7) * mm});
            skLineSegment(sketch, "E401", {"start": v(4.27, 5.7) * mm, "end": v(4.29, 5.71) * mm});
            skLineSegment(sketch, "E402", {"start": v(4.29, 5.71) * mm, "end": v(4.3, 5.72) * mm});
            skLineSegment(sketch, "E403", {"start": v(4.3, 5.72) * mm, "end": v(4.32, 5.73) * mm});
            skLineSegment(sketch, "E404", {"start": v(4.32, 5.73) * mm, "end": v(4.34, 5.75) * mm});
            skLineSegment(sketch, "E405", {"start": v(4.34, 5.75) * mm, "end": v(4.36, 5.76) * mm});
            skLineSegment(sketch, "E406", {"start": v(4.36, 5.76) * mm, "end": v(4.38, 5.77) * mm});
            skLineSegment(sketch, "E407", {"start": v(4.38, 5.77) * mm, "end": v(4.4, 5.78) * mm});
            skLineSegment(sketch, "E408", {"start": v(4.4, 5.78) * mm, "end": v(4.42, 5.8) * mm});
            skLineSegment(sketch, "E409", {"start": v(4.42, 5.8) * mm, "end": v(4.44, 5.8) * mm});
            skLineSegment(sketch, "E410", {"start": v(4.44, 5.8) * mm, "end": v(4.46, 5.82) * mm});
            skLineSegment(sketch, "E411", {"start": v(4.46, 5.82) * mm, "end": v(4.48, 5.83) * mm});
            skLineSegment(sketch, "E412", {"start": v(4.48, 5.83) * mm, "end": v(4.5, 5.84) * mm});
            skLineSegment(sketch, "E413", {"start": v(4.5, 5.84) * mm, "end": v(4.53, 5.86) * mm});
            skLineSegment(sketch, "E414", {"start": v(4.53, 5.86) * mm, "end": v(4.55, 5.87) * mm});
            skLineSegment(sketch, "E415", {"start": v(4.55, 5.87) * mm, "end": v(4.58, 5.88) * mm});
            skLineSegment(sketch, "E416", {"start": v(4.58, 5.88) * mm, "end": v(4.6, 5.9) * mm});
            skLineSegment(sketch, "E417", {"start": v(4.6, 5.9) * mm, "end": v(4.63, 5.9) * mm});
            skLineSegment(sketch, "E418", {"start": v(4.63, 5.9) * mm, "end": v(4.65, 5.92) * mm});
            skLineSegment(sketch, "E419", {"start": v(4.65, 5.92) * mm, "end": v(4.68, 5.93) * mm});
            skLineSegment(sketch, "E420", {"start": v(4.68, 5.93) * mm, "end": v(4.7, 5.95) * mm});
            skLineSegment(sketch, "E421", {"start": v(4.7, 5.95) * mm, "end": v(4.73, 5.96) * mm});
            skLineSegment(sketch, "E422", {"start": v(4.73, 5.96) * mm, "end": v(4.76, 5.97) * mm});
            skLineSegment(sketch, "E423", {"start": v(4.76, 5.97) * mm, "end": v(4.8, 5.98) * mm});
            skLineSegment(sketch, "E424", {"start": v(4.8, 5.98) * mm, "end": v(4.82, 6) * mm});
            skLineSegment(sketch, "E425", {"start": v(4.82, 6) * mm, "end": v(4.85, 6) * mm});
            skLineSegment(sketch, "E426", {"start": v(4.85, 6) * mm, "end": v(4.88, 6.02) * mm});
            skLineSegment(sketch, "E427", {"start": v(4.76, 4.93) * mm, "end": v(4.75, 4.94) * mm});
            skLineSegment(sketch, "E428", {"start": v(4.75, 4.94) * mm, "end": v(4.75, 4.94) * mm});
            skLineSegment(sketch, "E429", {"start": v(4.75, 4.94) * mm, "end": v(4.75, 4.95) * mm});
            skLineSegment(sketch, "E430", {"start": v(4.75, 4.95) * mm, "end": v(4.75, 4.96) * mm});
            skLineSegment(sketch, "E431", {"start": v(4.75, 4.96) * mm, "end": v(4.75, 4.97) * mm});
            skLineSegment(sketch, "E432", {"start": v(4.75, 4.97) * mm, "end": v(4.76, 4.99) * mm});
            skLineSegment(sketch, "E433", {"start": v(4.76, 4.99) * mm, "end": v(4.77, 5) * mm});
            skLineSegment(sketch, "E434", {"start": v(4.77, 5) * mm, "end": v(4.77, 5) * mm});
            skLineSegment(sketch, "E435", {"start": v(4.77, 5) * mm, "end": v(4.78, 5.02) * mm});
            skLineSegment(sketch, "E436", {"start": v(4.78, 5.02) * mm, "end": v(4.79, 5.03) * mm});
            skLineSegment(sketch, "E437", {"start": v(4.79, 5.03) * mm, "end": v(4.8, 5.04) * mm});
            skLineSegment(sketch, "E438", {"start": v(4.8, 5.04) * mm, "end": v(4.8, 5.06) * mm});
            skLineSegment(sketch, "E439", {"start": v(4.8, 5.06) * mm, "end": v(4.8, 5.07) * mm});
            skLineSegment(sketch, "E440", {"start": v(4.8, 5.07) * mm, "end": v(4.82, 5.08) * mm});
            skLineSegment(sketch, "E441", {"start": v(4.82, 5.08) * mm, "end": v(4.82, 5.1) * mm});
            skLineSegment(sketch, "E442", {"start": v(4.82, 5.1) * mm, "end": v(4.83, 5.11) * mm});
            skLineSegment(sketch, "E443", {"start": v(4.83, 5.11) * mm, "end": v(4.84, 5.13) * mm});
            skLineSegment(sketch, "E444", {"start": v(4.84, 5.13) * mm, "end": v(4.85, 5.14) * mm});
            skLineSegment(sketch, "E445", {"start": v(4.85, 5.14) * mm, "end": v(4.85, 5.16) * mm});
            skLineSegment(sketch, "E446", {"start": v(4.85, 5.16) * mm, "end": v(4.86, 5.18) * mm});
            skLineSegment(sketch, "E447", {"start": v(4.86, 5.18) * mm, "end": v(4.87, 5.2) * mm});
            skLineSegment(sketch, "E448", {"start": v(4.87, 5.2) * mm, "end": v(4.88, 5.21) * mm});
            skLineSegment(sketch, "E449", {"start": v(4.88, 5.21) * mm, "end": v(4.89, 5.23) * mm});
            skLineSegment(sketch, "E450", {"start": v(4.89, 5.23) * mm, "end": v(4.9, 5.25) * mm});
            skLineSegment(sketch, "E451", {"start": v(4.9, 5.25) * mm, "end": v(4.9, 5.27) * mm});
            skLineSegment(sketch, "E452", {"start": v(4.9, 5.27) * mm, "end": v(4.91, 5.3) * mm});
            skLineSegment(sketch, "E453", {"start": v(4.91, 5.3) * mm, "end": v(4.92, 5.31) * mm});
            skLineSegment(sketch, "E454", {"start": v(4.92, 5.31) * mm, "end": v(4.93, 5.33) * mm});
            skLineSegment(sketch, "E455", {"start": v(4.93, 5.33) * mm, "end": v(4.94, 5.36) * mm});
            skLineSegment(sketch, "E456", {"start": v(4.94, 5.36) * mm, "end": v(4.95, 5.38) * mm});
            skLineSegment(sketch, "E457", {"start": v(4.95, 5.38) * mm, "end": v(4.96, 5.4) * mm});
            skLineSegment(sketch, "E458", {"start": v(4.96, 5.4) * mm, "end": v(4.96, 5.43) * mm});
            skLineSegment(sketch, "E459", {"start": v(4.96, 5.43) * mm, "end": v(4.97, 5.45) * mm});
            skLineSegment(sketch, "E460", {"start": v(4.97, 5.45) * mm, "end": v(4.98, 5.48) * mm});
            skLineSegment(sketch, "E461", {"start": v(4.98, 5.48) * mm, "end": v(5, 5.5) * mm});
            skLineSegment(sketch, "E462", {"start": v(5, 5.5) * mm, "end": v(5, 5.53) * mm});
            skLineSegment(sketch, "E463", {"start": v(5, 5.53) * mm, "end": v(5, 5.55) * mm});
            skLineSegment(sketch, "E464", {"start": v(5, 5.55) * mm, "end": v(5.01, 5.58) * mm});
            skLineSegment(sketch, "E465", {"start": v(5.01, 5.58) * mm, "end": v(5.02, 5.6) * mm});
            skLineSegment(sketch, "E466", {"start": v(5.02, 5.6) * mm, "end": v(5.03, 5.64) * mm});
            skLineSegment(sketch, "E467", {"start": v(5.03, 5.64) * mm, "end": v(5.04, 5.67) * mm});
            skLineSegment(sketch, "E468", {"start": v(5.04, 5.67) * mm, "end": v(5.05, 5.7) * mm});
            skLineSegment(sketch, "E469", {"start": v(5.05, 5.7) * mm, "end": v(5.05, 5.73) * mm});
            skLineSegment(sketch, "E470", {"start": v(5.05, 5.73) * mm, "end": v(5.06, 5.76) * mm});
            skLineSegment(sketch, "E471", {"start": v(5.06, 5.76) * mm, "end": v(5.07, 5.79) * mm});
            skLineSegment(sketch, "E472", {"start": v(5.07, 5.79) * mm, "end": v(5.08, 5.82) * mm});
            skLineSegment(sketch, "E473", {"start": v(5.08, 5.82) * mm, "end": v(5.08, 5.85) * mm});
            skArc(sketch, "E474", {"start": v(5.08, 5.85) * mm, "mid": v(4.98, 5.94) * mm, "end": v(4.88, 6.02) * mm});
            skLineSegment(sketch, "E475", {"start": v(4.93, 4.76) * mm, "end": v(4.94, 4.75) * mm});
            skLineSegment(sketch, "E476", {"start": v(4.94, 4.75) * mm, "end": v(4.94, 4.75) * mm});
            skLineSegment(sketch, "E477", {"start": v(4.94, 4.75) * mm, "end": v(4.95, 4.75) * mm});
            skLineSegment(sketch, "E478", {"start": v(4.95, 4.75) * mm, "end": v(4.96, 4.75) * mm});
            skLineSegment(sketch, "E479", {"start": v(4.96, 4.75) * mm, "end": v(4.97, 4.75) * mm});
            skLineSegment(sketch, "E480", {"start": v(4.97, 4.75) * mm, "end": v(4.99, 4.76) * mm});
            skLineSegment(sketch, "E481", {"start": v(4.99, 4.76) * mm, "end": v(5, 4.77) * mm});
            skLineSegment(sketch, "E482", {"start": v(5, 4.77) * mm, "end": v(5, 4.77) * mm});
            skLineSegment(sketch, "E483", {"start": v(5, 4.77) * mm, "end": v(5.02, 4.78) * mm});
            skLineSegment(sketch, "E484", {"start": v(5.02, 4.78) * mm, "end": v(5.03, 4.79) * mm});
            skLineSegment(sketch, "E485", {"start": v(5.03, 4.79) * mm, "end": v(5.04, 4.8) * mm});
            skLineSegment(sketch, "E486", {"start": v(5.04, 4.8) * mm, "end": v(5.06, 4.8) * mm});
            skLineSegment(sketch, "E487", {"start": v(5.06, 4.8) * mm, "end": v(5.07, 4.8) * mm});
            skLineSegment(sketch, "E488", {"start": v(5.07, 4.8) * mm, "end": v(5.08, 4.82) * mm});
            skLineSegment(sketch, "E489", {"start": v(5.08, 4.82) * mm, "end": v(5.1, 4.82) * mm});
            skLineSegment(sketch, "E490", {"start": v(5.1, 4.82) * mm, "end": v(5.11, 4.83) * mm});
            skLineSegment(sketch, "E491", {"start": v(5.11, 4.83) * mm, "end": v(5.13, 4.84) * mm});
            skLineSegment(sketch, "E492", {"start": v(5.13, 4.84) * mm, "end": v(5.14, 4.85) * mm});
            skLineSegment(sketch, "E493", {"start": v(5.14, 4.85) * mm, "end": v(5.16, 4.85) * mm});
            skLineSegment(sketch, "E494", {"start": v(5.16, 4.85) * mm, "end": v(5.18, 4.86) * mm});
            skLineSegment(sketch, "E495", {"start": v(5.18, 4.86) * mm, "end": v(5.2, 4.87) * mm});
            skLineSegment(sketch, "E496", {"start": v(5.2, 4.87) * mm, "end": v(5.21, 4.88) * mm});
            skLineSegment(sketch, "E497", {"start": v(5.21, 4.88) * mm, "end": v(5.23, 4.89) * mm});
            skLineSegment(sketch, "E498", {"start": v(5.23, 4.89) * mm, "end": v(5.25, 4.9) * mm});
            skLineSegment(sketch, "E499", {"start": v(5.25, 4.9) * mm, "end": v(5.27, 4.9) * mm});
            skLineSegment(sketch, "E500", {"start": v(5.27, 4.9) * mm, "end": v(5.3, 4.91) * mm});
            skLineSegment(sketch, "E501", {"start": v(5.3, 4.91) * mm, "end": v(5.31, 4.92) * mm});
            skLineSegment(sketch, "E502", {"start": v(5.31, 4.92) * mm, "end": v(5.33, 4.93) * mm});
            skLineSegment(sketch, "E503", {"start": v(5.33, 4.93) * mm, "end": v(5.36, 4.94) * mm});
            skLineSegment(sketch, "E504", {"start": v(5.36, 4.94) * mm, "end": v(5.38, 4.95) * mm});
            skLineSegment(sketch, "E505", {"start": v(5.38, 4.95) * mm, "end": v(5.4, 4.96) * mm});
            skLineSegment(sketch, "E506", {"start": v(5.4, 4.96) * mm, "end": v(5.43, 4.96) * mm});
            skLineSegment(sketch, "E507", {"start": v(5.43, 4.96) * mm, "end": v(5.45, 4.97) * mm});
            skLineSegment(sketch, "E508", {"start": v(5.45, 4.97) * mm, "end": v(5.48, 4.98) * mm});
            skLineSegment(sketch, "E509", {"start": v(5.48, 4.98) * mm, "end": v(5.5, 5) * mm});
            skLineSegment(sketch, "E510", {"start": v(5.5, 5) * mm, "end": v(5.53, 5) * mm});
            skLineSegment(sketch, "E511", {"start": v(5.53, 5) * mm, "end": v(5.55, 5) * mm});
            skLineSegment(sketch, "E512", {"start": v(5.55, 5) * mm, "end": v(5.58, 5.01) * mm});
            skLineSegment(sketch, "E513", {"start": v(5.58, 5.01) * mm, "end": v(5.6, 5.02) * mm});
            skLineSegment(sketch, "E514", {"start": v(5.6, 5.02) * mm, "end": v(5.64, 5.03) * mm});
            skLineSegment(sketch, "E515", {"start": v(5.64, 5.03) * mm, "end": v(5.67, 5.04) * mm});
            skLineSegment(sketch, "E516", {"start": v(5.67, 5.04) * mm, "end": v(5.7, 5.05) * mm});
            skLineSegment(sketch, "E517", {"start": v(5.7, 5.05) * mm, "end": v(5.73, 5.05) * mm});
            skLineSegment(sketch, "E518", {"start": v(5.73, 5.05) * mm, "end": v(5.76, 5.06) * mm});
            skLineSegment(sketch, "E519", {"start": v(5.76, 5.06) * mm, "end": v(5.79, 5.07) * mm});
            skLineSegment(sketch, "E520", {"start": v(5.79, 5.07) * mm, "end": v(5.82, 5.08) * mm});
            skLineSegment(sketch, "E521", {"start": v(5.82, 5.08) * mm, "end": v(5.85, 5.08) * mm});
            skLineSegment(sketch, "E522", {"start": v(5.54, 4.03) * mm, "end": v(5.54, 4.04) * mm});
            skLineSegment(sketch, "E523", {"start": v(5.54, 4.04) * mm, "end": v(5.54, 4.04) * mm});
            skLineSegment(sketch, "E524", {"start": v(5.54, 4.04) * mm, "end": v(5.54, 4.05) * mm});
            skLineSegment(sketch, "E525", {"start": v(5.54, 4.05) * mm, "end": v(5.54, 4.06) * mm});
            skLineSegment(sketch, "E526", {"start": v(5.54, 4.06) * mm, "end": v(5.55, 4.07) * mm});
            skLineSegment(sketch, "E527", {"start": v(5.55, 4.07) * mm, "end": v(5.55, 4.08) * mm});
            skLineSegment(sketch, "E528", {"start": v(5.55, 4.08) * mm, "end": v(5.56, 4.1) * mm});
            skLineSegment(sketch, "E529", {"start": v(5.56, 4.1) * mm, "end": v(5.57, 4.1) * mm});
            skLineSegment(sketch, "E530", {"start": v(5.57, 4.1) * mm, "end": v(5.58, 4.11) * mm});
            skLineSegment(sketch, "E531", {"start": v(5.58, 4.11) * mm, "end": v(5.59, 4.12) * mm});
            skLineSegment(sketch, "E532", {"start": v(5.59, 4.12) * mm, "end": v(5.6, 4.14) * mm});
            skLineSegment(sketch, "E533", {"start": v(5.6, 4.14) * mm, "end": v(5.6, 4.15) * mm});
            skLineSegment(sketch, "E534", {"start": v(5.6, 4.15) * mm, "end": v(5.62, 4.16) * mm});
            skLineSegment(sketch, "E535", {"start": v(5.62, 4.16) * mm, "end": v(5.63, 4.17) * mm});
            skLineSegment(sketch, "E536", {"start": v(5.63, 4.17) * mm, "end": v(5.64, 4.18) * mm});
            skLineSegment(sketch, "E537", {"start": v(5.64, 4.18) * mm, "end": v(5.65, 4.2) * mm});
            skLineSegment(sketch, "E538", {"start": v(5.65, 4.2) * mm, "end": v(5.66, 4.21) * mm});
            skLineSegment(sketch, "E539", {"start": v(5.66, 4.21) * mm, "end": v(5.67, 4.22) * mm});
            skLineSegment(sketch, "E540", {"start": v(5.67, 4.22) * mm, "end": v(5.68, 4.24) * mm});
            skLineSegment(sketch, "E541", {"start": v(5.68, 4.24) * mm, "end": v(5.69, 4.25) * mm});
            skLineSegment(sketch, "E542", {"start": v(5.69, 4.25) * mm, "end": v(5.7, 4.27) * mm});
            skLineSegment(sketch, "E543", {"start": v(5.7, 4.27) * mm, "end": v(5.71, 4.29) * mm});
            skLineSegment(sketch, "E544", {"start": v(5.71, 4.29) * mm, "end": v(5.72, 4.3) * mm});
            skLineSegment(sketch, "E545", {"start": v(5.72, 4.3) * mm, "end": v(5.73, 4.32) * mm});
            skLineSegment(sketch, "E546", {"start": v(5.73, 4.32) * mm, "end": v(5.75, 4.34) * mm});
            skLineSegment(sketch, "E547", {"start": v(5.75, 4.34) * mm, "end": v(5.76, 4.36) * mm});
            skLineSegment(sketch, "E548", {"start": v(5.76, 4.36) * mm, "end": v(5.77, 4.38) * mm});
            skLineSegment(sketch, "E549", {"start": v(5.77, 4.38) * mm, "end": v(5.78, 4.4) * mm});
            skLineSegment(sketch, "E550", {"start": v(5.78, 4.4) * mm, "end": v(5.8, 4.42) * mm});
            skLineSegment(sketch, "E551", {"start": v(5.8, 4.42) * mm, "end": v(5.8, 4.44) * mm});
            skLineSegment(sketch, "E552", {"start": v(5.8, 4.44) * mm, "end": v(5.82, 4.46) * mm});
            skLineSegment(sketch, "E553", {"start": v(5.82, 4.46) * mm, "end": v(5.83, 4.48) * mm});
            skLineSegment(sketch, "E554", {"start": v(5.83, 4.48) * mm, "end": v(5.84, 4.5) * mm});
            skLineSegment(sketch, "E555", {"start": v(5.84, 4.5) * mm, "end": v(5.86, 4.53) * mm});
            skLineSegment(sketch, "E556", {"start": v(5.86, 4.53) * mm, "end": v(5.87, 4.55) * mm});
            skLineSegment(sketch, "E557", {"start": v(5.87, 4.55) * mm, "end": v(5.88, 4.58) * mm});
            skLineSegment(sketch, "E558", {"start": v(5.88, 4.58) * mm, "end": v(5.9, 4.6) * mm});
            skLineSegment(sketch, "E559", {"start": v(5.9, 4.6) * mm, "end": v(5.9, 4.63) * mm});
            skLineSegment(sketch, "E560", {"start": v(5.9, 4.63) * mm, "end": v(5.92, 4.65) * mm});
            skLineSegment(sketch, "E561", {"start": v(5.92, 4.65) * mm, "end": v(5.93, 4.68) * mm});
            skLineSegment(sketch, "E562", {"start": v(5.93, 4.68) * mm, "end": v(5.95, 4.7) * mm});
            skLineSegment(sketch, "E563", {"start": v(5.95, 4.7) * mm, "end": v(5.96, 4.73) * mm});
            skLineSegment(sketch, "E564", {"start": v(5.96, 4.73) * mm, "end": v(5.97, 4.76) * mm});
            skLineSegment(sketch, "E565", {"start": v(5.97, 4.76) * mm, "end": v(5.98, 4.8) * mm});
            skLineSegment(sketch, "E566", {"start": v(5.98, 4.8) * mm, "end": v(6, 4.82) * mm});
            skLineSegment(sketch, "E567", {"start": v(6, 4.82) * mm, "end": v(6, 4.85) * mm});
            skLineSegment(sketch, "E568", {"start": v(6, 4.85) * mm, "end": v(6.02, 4.88) * mm});
            skArc(sketch, "E569", {"start": v(6.02, 4.88) * mm, "mid": v(5.94, 4.98) * mm, "end": v(5.85, 5.08) * mm});
            skLineSegment(sketch, "E570", {"start": v(5.68, 3.83) * mm, "end": v(5.69, 3.82) * mm});
            skLineSegment(sketch, "E571", {"start": v(5.69, 3.82) * mm, "end": v(5.7, 3.82) * mm});
            skLineSegment(sketch, "E572", {"start": v(5.7, 3.82) * mm, "end": v(5.7, 3.82) * mm});
            skLineSegment(sketch, "E573", {"start": v(5.7, 3.82) * mm, "end": v(5.71, 3.82) * mm});
            skLineSegment(sketch, "E574", {"start": v(5.71, 3.82) * mm, "end": v(5.72, 3.82) * mm});
            skLineSegment(sketch, "E575", {"start": v(5.72, 3.82) * mm, "end": v(5.74, 3.82) * mm});
            skLineSegment(sketch, "E576", {"start": v(5.74, 3.82) * mm, "end": v(5.75, 3.83) * mm});
            skLineSegment(sketch, "E577", {"start": v(5.75, 3.83) * mm, "end": v(5.76, 3.83) * mm});
            skLineSegment(sketch, "E578", {"start": v(5.76, 3.83) * mm, "end": v(5.77, 3.83) * mm});
            skLineSegment(sketch, "E579", {"start": v(5.77, 3.83) * mm, "end": v(5.79, 3.84) * mm});
            skLineSegment(sketch, "E580", {"start": v(5.79, 3.84) * mm, "end": v(5.8, 3.84) * mm});
            skLineSegment(sketch, "E581", {"start": v(5.8, 3.84) * mm, "end": v(5.81, 3.85) * mm});
            skLineSegment(sketch, "E582", {"start": v(5.81, 3.85) * mm, "end": v(5.83, 3.85) * mm});
            skLineSegment(sketch, "E583", {"start": v(5.83, 3.85) * mm, "end": v(5.84, 3.86) * mm});
            skLineSegment(sketch, "E584", {"start": v(5.84, 3.86) * mm, "end": v(5.86, 3.86) * mm});
            skLineSegment(sketch, "E585", {"start": v(5.86, 3.86) * mm, "end": v(5.87, 3.87) * mm});
            skLineSegment(sketch, "E586", {"start": v(5.87, 3.87) * mm, "end": v(5.9, 3.87) * mm});
            skLineSegment(sketch, "E587", {"start": v(5.9, 3.87) * mm, "end": v(5.9, 3.88) * mm});
            skLineSegment(sketch, "E588", {"start": v(5.9, 3.88) * mm, "end": v(5.93, 3.89) * mm});
            skLineSegment(sketch, "E589", {"start": v(5.93, 3.89) * mm, "end": v(5.94, 3.9) * mm});
            skLineSegment(sketch, "E590", {"start": v(5.94, 3.9) * mm, "end": v(5.96, 3.9) * mm});
            skLineSegment(sketch, "E591", {"start": v(5.96, 3.9) * mm, "end": v(5.98, 3.9) * mm});
            skLineSegment(sketch, "E592", {"start": v(5.98, 3.9) * mm, "end": v(6, 3.9) * mm});
            skLineSegment(sketch, "E593", {"start": v(6, 3.9) * mm, "end": v(6.02, 3.91) * mm});
            skLineSegment(sketch, "E594", {"start": v(6.02, 3.91) * mm, "end": v(6.04, 3.92) * mm});
            skLineSegment(sketch, "E595", {"start": v(6.04, 3.92) * mm, "end": v(6.06, 3.92) * mm});
            skLineSegment(sketch, "E596", {"start": v(6.06, 3.92) * mm, "end": v(6.09, 3.92) * mm});
            skLineSegment(sketch, "E597", {"start": v(6.09, 3.92) * mm, "end": v(6.1, 3.93) * mm});
            skLineSegment(sketch, "E598", {"start": v(6.1, 3.93) * mm, "end": v(6.13, 3.93) * mm});
            skLineSegment(sketch, "E599", {"start": v(6.13, 3.93) * mm, "end": v(6.16, 3.94) * mm});
            skLineSegment(sketch, "E600", {"start": v(6.16, 3.94) * mm, "end": v(6.18, 3.94) * mm});
            skLineSegment(sketch, "E601", {"start": v(6.18, 3.94) * mm, "end": v(6.2, 3.95) * mm});
            skLineSegment(sketch, "E602", {"start": v(6.2, 3.95) * mm, "end": v(6.23, 3.95) * mm});
            skLineSegment(sketch, "E603", {"start": v(6.23, 3.95) * mm, "end": v(6.26, 3.96) * mm});
            skLineSegment(sketch, "E604", {"start": v(6.26, 3.96) * mm, "end": v(6.28, 3.96) * mm});
            skLineSegment(sketch, "E605", {"start": v(6.28, 3.96) * mm, "end": v(6.31, 3.96) * mm});
            skLineSegment(sketch, "E606", {"start": v(6.31, 3.96) * mm, "end": v(6.34, 3.97) * mm});
            skLineSegment(sketch, "E607", {"start": v(6.34, 3.97) * mm, "end": v(6.37, 3.97) * mm});
            skLineSegment(sketch, "E608", {"start": v(6.37, 3.97) * mm, "end": v(6.4, 3.97) * mm});
            skLineSegment(sketch, "E609", {"start": v(6.4, 3.97) * mm, "end": v(6.43, 3.98) * mm});
            skLineSegment(sketch, "E610", {"start": v(6.43, 3.98) * mm, "end": v(6.46, 3.98) * mm});
            skLineSegment(sketch, "E611", {"start": v(6.46, 3.98) * mm, "end": v(6.49, 3.98) * mm});
            skLineSegment(sketch, "E612", {"start": v(6.49, 3.98) * mm, "end": v(6.52, 3.98) * mm});
            skLineSegment(sketch, "E613", {"start": v(6.52, 3.98) * mm, "end": v(6.55, 3.98) * mm});
            skLineSegment(sketch, "E614", {"start": v(6.55, 3.98) * mm, "end": v(6.58, 3.99) * mm});
            skLineSegment(sketch, "E615", {"start": v(6.58, 3.99) * mm, "end": v(6.61, 3.99) * mm});
            skLineSegment(sketch, "E616", {"start": v(6.61, 3.99) * mm, "end": v(6.65, 3.99) * mm});
            skLineSegment(sketch, "E617", {"start": v(6.16, 3) * mm, "end": v(6.15, 3.02) * mm});
            skLineSegment(sketch, "E618", {"start": v(6.15, 3.02) * mm, "end": v(6.15, 3.02) * mm});
            skLineSegment(sketch, "E619", {"start": v(6.15, 3.02) * mm, "end": v(6.16, 3.03) * mm});
            skLineSegment(sketch, "E620", {"start": v(6.16, 3.03) * mm, "end": v(6.16, 3.04) * mm});
            skLineSegment(sketch, "E621", {"start": v(6.16, 3.04) * mm, "end": v(6.17, 3.05) * mm});
            skLineSegment(sketch, "E622", {"start": v(6.17, 3.05) * mm, "end": v(6.18, 3.06) * mm});
            skLineSegment(sketch, "E623", {"start": v(6.18, 3.06) * mm, "end": v(6.19, 3.07) * mm});
            skLineSegment(sketch, "E624", {"start": v(6.19, 3.07) * mm, "end": v(6.2, 3.07) * mm});
            skLineSegment(sketch, "E625", {"start": v(6.2, 3.07) * mm, "end": v(6.2, 3.08) * mm});
            skLineSegment(sketch, "E626", {"start": v(6.2, 3.08) * mm, "end": v(6.22, 3.1) * mm});
            skLineSegment(sketch, "E627", {"start": v(6.22, 3.1) * mm, "end": v(6.23, 3.1) * mm});
            skLineSegment(sketch, "E628", {"start": v(6.23, 3.1) * mm, "end": v(6.24, 3.11) * mm});
            skLineSegment(sketch, "E629", {"start": v(6.24, 3.11) * mm, "end": v(6.25, 3.12) * mm});
            skLineSegment(sketch, "E630", {"start": v(6.25, 3.12) * mm, "end": v(6.26, 3.13) * mm});
            skLineSegment(sketch, "E631", {"start": v(6.26, 3.13) * mm, "end": v(6.28, 3.14) * mm});
            skLineSegment(sketch, "E632", {"start": v(6.28, 3.14) * mm, "end": v(6.29, 3.15) * mm});
            skLineSegment(sketch, "E633", {"start": v(6.29, 3.15) * mm, "end": v(6.3, 3.16) * mm});
            skLineSegment(sketch, "E634", {"start": v(6.3, 3.16) * mm, "end": v(6.31, 3.18) * mm});
            skLineSegment(sketch, "E635", {"start": v(6.31, 3.18) * mm, "end": v(6.33, 3.19) * mm});
            skLineSegment(sketch, "E636", {"start": v(6.33, 3.19) * mm, "end": v(6.34, 3.2) * mm});
            skLineSegment(sketch, "E637", {"start": v(6.34, 3.2) * mm, "end": v(6.35, 3.22) * mm});
            skLineSegment(sketch, "E638", {"start": v(6.35, 3.22) * mm, "end": v(6.37, 3.23) * mm});
            skLineSegment(sketch, "E639", {"start": v(6.37, 3.23) * mm, "end": v(6.38, 3.24) * mm});
            skLineSegment(sketch, "E640", {"start": v(6.38, 3.24) * mm, "end": v(6.4, 3.26) * mm});
            skLineSegment(sketch, "E641", {"start": v(6.4, 3.26) * mm, "end": v(6.41, 3.28) * mm});
            skLineSegment(sketch, "E642", {"start": v(6.41, 3.28) * mm, "end": v(6.43, 3.3) * mm});
            skLineSegment(sketch, "E643", {"start": v(6.43, 3.3) * mm, "end": v(6.44, 3.3) * mm});
            skLineSegment(sketch, "E644", {"start": v(6.44, 3.3) * mm, "end": v(6.46, 3.33) * mm});
            skLineSegment(sketch, "E645", {"start": v(6.46, 3.33) * mm, "end": v(6.47, 3.34) * mm});
            skLineSegment(sketch, "E646", {"start": v(6.47, 3.34) * mm, "end": v(6.49, 3.36) * mm});
            skLineSegment(sketch, "E647", {"start": v(6.49, 3.36) * mm, "end": v(6.5, 3.38) * mm});
            skLineSegment(sketch, "E648", {"start": v(6.5, 3.38) * mm, "end": v(6.52, 3.4) * mm});
            skLineSegment(sketch, "E649", {"start": v(6.52, 3.4) * mm, "end": v(6.54, 3.42) * mm});
            skLineSegment(sketch, "E650", {"start": v(6.54, 3.42) * mm, "end": v(6.55, 3.44) * mm});
            skLineSegment(sketch, "E651", {"start": v(6.55, 3.44) * mm, "end": v(6.57, 3.46) * mm});
            skLineSegment(sketch, "E652", {"start": v(6.57, 3.46) * mm, "end": v(6.59, 3.48) * mm});
            skLineSegment(sketch, "E653", {"start": v(6.59, 3.48) * mm, "end": v(6.6, 3.5) * mm});
            skLineSegment(sketch, "E654", {"start": v(6.6, 3.5) * mm, "end": v(6.62, 3.53) * mm});
            skLineSegment(sketch, "E655", {"start": v(6.62, 3.53) * mm, "end": v(6.64, 3.55) * mm});
            skLineSegment(sketch, "E656", {"start": v(6.64, 3.55) * mm, "end": v(6.66, 3.58) * mm});
            skLineSegment(sketch, "E657", {"start": v(6.66, 3.58) * mm, "end": v(6.67, 3.6) * mm});
            skLineSegment(sketch, "E658", {"start": v(6.67, 3.6) * mm, "end": v(6.7, 3.63) * mm});
            skLineSegment(sketch, "E659", {"start": v(6.7, 3.63) * mm, "end": v(6.7, 3.65) * mm});
            skLineSegment(sketch, "E660", {"start": v(6.7, 3.65) * mm, "end": v(6.73, 3.68) * mm});
            skLineSegment(sketch, "E661", {"start": v(6.73, 3.68) * mm, "end": v(6.74, 3.7) * mm});
            skLineSegment(sketch, "E662", {"start": v(6.74, 3.7) * mm, "end": v(6.76, 3.73) * mm});
            skLineSegment(sketch, "E663", {"start": v(6.76, 3.73) * mm, "end": v(6.78, 3.76) * mm});
            skArc(sketch, "E664", {"start": v(6.78, 3.76) * mm, "mid": v(6.71, 3.88) * mm, "end": v(6.65, 3.99) * mm});
            skLineSegment(sketch, "E665", {"start": v(6.26, 2.78) * mm, "end": v(6.27, 2.78) * mm});
            skLineSegment(sketch, "E666", {"start": v(6.27, 2.78) * mm, "end": v(6.27, 2.77) * mm});
            skLineSegment(sketch, "E667", {"start": v(6.27, 2.77) * mm, "end": v(6.28, 2.77) * mm});
            skLineSegment(sketch, "E668", {"start": v(6.28, 2.77) * mm, "end": v(6.29, 2.77) * mm});
            skLineSegment(sketch, "E669", {"start": v(6.29, 2.77) * mm, "end": v(6.3, 2.77) * mm});
            skLineSegment(sketch, "E670", {"start": v(6.3, 2.77) * mm, "end": v(6.31, 2.77) * mm});
            skLineSegment(sketch, "E671", {"start": v(6.31, 2.77) * mm, "end": v(6.33, 2.77) * mm});
            skLineSegment(sketch, "E672", {"start": v(6.33, 2.77) * mm, "end": v(6.34, 2.77) * mm});
            skLineSegment(sketch, "E673", {"start": v(6.34, 2.77) * mm, "end": v(6.35, 2.77) * mm});
            skLineSegment(sketch, "E674", {"start": v(6.35, 2.77) * mm, "end": v(6.37, 2.78) * mm});
            skLineSegment(sketch, "E675", {"start": v(6.37, 2.78) * mm, "end": v(6.38, 2.78) * mm});
            skLineSegment(sketch, "E676", {"start": v(6.38, 2.78) * mm, "end": v(6.4, 2.78) * mm});
            skLineSegment(sketch, "E677", {"start": v(6.4, 2.78) * mm, "end": v(6.4, 2.78) * mm});
            skLineSegment(sketch, "E678", {"start": v(6.4, 2.78) * mm, "end": v(6.42, 2.79) * mm});
            skLineSegment(sketch, "E679", {"start": v(6.42, 2.79) * mm, "end": v(6.44, 2.79) * mm});
            skLineSegment(sketch, "E680", {"start": v(6.44, 2.79) * mm, "end": v(6.46, 2.8) * mm});
            skLineSegment(sketch, "E681", {"start": v(6.46, 2.8) * mm, "end": v(6.47, 2.8) * mm});
            skLineSegment(sketch, "E682", {"start": v(6.47, 2.8) * mm, "end": v(6.5, 2.8) * mm});
            skLineSegment(sketch, "E683", {"start": v(6.5, 2.8) * mm, "end": v(6.51, 2.8) * mm});
            skLineSegment(sketch, "E684", {"start": v(6.51, 2.8) * mm, "end": v(6.53, 2.8) * mm});
            skLineSegment(sketch, "E685", {"start": v(6.53, 2.8) * mm, "end": v(6.55, 2.8) * mm});
            skLineSegment(sketch, "E686", {"start": v(6.55, 2.8) * mm, "end": v(6.57, 2.8) * mm});
            skLineSegment(sketch, "E687", {"start": v(6.57, 2.8) * mm, "end": v(6.59, 2.8) * mm});
            skLineSegment(sketch, "E688", {"start": v(6.59, 2.8) * mm, "end": v(6.6, 2.8) * mm});
            skLineSegment(sketch, "E689", {"start": v(6.6, 2.8) * mm, "end": v(6.63, 2.8) * mm});
            skLineSegment(sketch, "E690", {"start": v(6.63, 2.8) * mm, "end": v(6.65, 2.8) * mm});
            skLineSegment(sketch, "E691", {"start": v(6.65, 2.8) * mm, "end": v(6.68, 2.8) * mm});
            skLineSegment(sketch, "E692", {"start": v(6.68, 2.8) * mm, "end": v(6.7, 2.8) * mm});
            skLineSegment(sketch, "E693", {"start": v(6.7, 2.8) * mm, "end": v(6.72, 2.8) * mm});
            skLineSegment(sketch, "E694", {"start": v(6.72, 2.8) * mm, "end": v(6.75, 2.8) * mm});
            skLineSegment(sketch, "E695", {"start": v(6.75, 2.8) * mm, "end": v(6.77, 2.8) * mm});
            skLineSegment(sketch, "E696", {"start": v(6.77, 2.8) * mm, "end": v(6.8, 2.8) * mm});
            skLineSegment(sketch, "E697", {"start": v(6.8, 2.8) * mm, "end": v(6.82, 2.8) * mm});
            skLineSegment(sketch, "E698", {"start": v(6.82, 2.8) * mm, "end": v(6.85, 2.8) * mm});
            skLineSegment(sketch, "E699", {"start": v(6.85, 2.8) * mm, "end": v(6.88, 2.8) * mm});
            skLineSegment(sketch, "E700", {"start": v(6.88, 2.8) * mm, "end": v(6.9, 2.8) * mm});
            skLineSegment(sketch, "E701", {"start": v(6.9, 2.8) * mm, "end": v(6.93, 2.8) * mm});
            skLineSegment(sketch, "E702", {"start": v(6.93, 2.8) * mm, "end": v(6.96, 2.8) * mm});
            skLineSegment(sketch, "E703", {"start": v(6.96, 2.8) * mm, "end": v(6.99, 2.8) * mm});
            skLineSegment(sketch, "E704", {"start": v(6.99, 2.8) * mm, "end": v(7.02, 2.8) * mm});
            skLineSegment(sketch, "E705", {"start": v(7.02, 2.8) * mm, "end": v(7.05, 2.8) * mm});
            skLineSegment(sketch, "E706", {"start": v(7.05, 2.8) * mm, "end": v(7.08, 2.8) * mm});
            skLineSegment(sketch, "E707", {"start": v(7.08, 2.8) * mm, "end": v(7.1, 2.8) * mm});
            skLineSegment(sketch, "E708", {"start": v(7.1, 2.8) * mm, "end": v(7.14, 2.79) * mm});
            skLineSegment(sketch, "E709", {"start": v(7.14, 2.79) * mm, "end": v(7.17, 2.78) * mm});
            skLineSegment(sketch, "E710", {"start": v(7.17, 2.78) * mm, "end": v(7.2, 2.78) * mm});
            skLineSegment(sketch, "E711", {"start": v(7.2, 2.78) * mm, "end": v(7.24, 2.77) * mm});
            skLineSegment(sketch, "E712", {"start": v(6.58, 1.9) * mm, "end": v(6.58, 1.9) * mm});
            skLineSegment(sketch, "E713", {"start": v(6.58, 1.9) * mm, "end": v(6.59, 1.9) * mm});
            skLineSegment(sketch, "E714", {"start": v(6.59, 1.9) * mm, "end": v(6.59, 1.91) * mm});
            skLineSegment(sketch, "E715", {"start": v(6.59, 1.91) * mm, "end": v(6.6, 1.92) * mm});
            skLineSegment(sketch, "E716", {"start": v(6.6, 1.92) * mm, "end": v(6.6, 1.93) * mm});
            skLineSegment(sketch, "E717", {"start": v(6.6, 1.93) * mm, "end": v(6.62, 1.94) * mm});
            skLineSegment(sketch, "E718", {"start": v(6.62, 1.94) * mm, "end": v(6.63, 1.95) * mm});
            skLineSegment(sketch, "E719", {"start": v(6.63, 1.95) * mm, "end": v(6.64, 1.95) * mm});
            skLineSegment(sketch, "E720", {"start": v(6.64, 1.95) * mm, "end": v(6.65, 1.96) * mm});
            skLineSegment(sketch, "E721", {"start": v(6.65, 1.96) * mm, "end": v(6.66, 1.96) * mm});
            skLineSegment(sketch, "E722", {"start": v(6.66, 1.96) * mm, "end": v(6.67, 1.97) * mm});
            skLineSegment(sketch, "E723", {"start": v(6.67, 1.97) * mm, "end": v(6.69, 1.98) * mm});
            skLineSegment(sketch, "E724", {"start": v(6.69, 1.98) * mm, "end": v(6.7, 1.99) * mm});
            skLineSegment(sketch, "E725", {"start": v(6.7, 1.99) * mm, "end": v(6.71, 2) * mm});
            skLineSegment(sketch, "E726", {"start": v(6.71, 2) * mm, "end": v(6.73, 2) * mm});
            skLineSegment(sketch, "E727", {"start": v(6.73, 2) * mm, "end": v(6.74, 2.01) * mm});
            skLineSegment(sketch, "E728", {"start": v(6.74, 2.01) * mm, "end": v(6.75, 2.02) * mm});
            skLineSegment(sketch, "E729", {"start": v(6.75, 2.02) * mm, "end": v(6.77, 2.03) * mm});
            skLineSegment(sketch, "E730", {"start": v(6.77, 2.03) * mm, "end": v(6.78, 2.04) * mm});
            skLineSegment(sketch, "E731", {"start": v(6.78, 2.04) * mm, "end": v(6.8, 2.05) * mm});
            skLineSegment(sketch, "E732", {"start": v(6.8, 2.05) * mm, "end": v(6.82, 2.06) * mm});
            skLineSegment(sketch, "E733", {"start": v(6.82, 2.06) * mm, "end": v(6.83, 2.08) * mm});
            skLineSegment(sketch, "E734", {"start": v(6.83, 2.08) * mm, "end": v(6.85, 2.09) * mm});
            skLineSegment(sketch, "E735", {"start": v(6.85, 2.09) * mm, "end": v(6.87, 2.1) * mm});
            skLineSegment(sketch, "E736", {"start": v(6.87, 2.1) * mm, "end": v(6.88, 2.11) * mm});
            skLineSegment(sketch, "E737", {"start": v(6.88, 2.11) * mm, "end": v(6.9, 2.13) * mm});
            skLineSegment(sketch, "E738", {"start": v(6.9, 2.13) * mm, "end": v(6.92, 2.14) * mm});
            skLineSegment(sketch, "E739", {"start": v(6.92, 2.14) * mm, "end": v(6.94, 2.15) * mm});
            skLineSegment(sketch, "E740", {"start": v(6.94, 2.15) * mm, "end": v(6.96, 2.17) * mm});
            skLineSegment(sketch, "E741", {"start": v(6.96, 2.17) * mm, "end": v(6.97, 2.18) * mm});
            skLineSegment(sketch, "E742", {"start": v(6.97, 2.18) * mm, "end": v(7, 2.2) * mm});
            skLineSegment(sketch, "E743", {"start": v(7, 2.2) * mm, "end": v(7.01, 2.22) * mm});
            skLineSegment(sketch, "E744", {"start": v(7.01, 2.22) * mm, "end": v(7.03, 2.23) * mm});
            skLineSegment(sketch, "E745", {"start": v(7.03, 2.23) * mm, "end": v(7.05, 2.25) * mm});
            skLineSegment(sketch, "E746", {"start": v(7.05, 2.25) * mm, "end": v(7.07, 2.27) * mm});
            skLineSegment(sketch, "E747", {"start": v(7.07, 2.27) * mm, "end": v(7.1, 2.29) * mm});
            skLineSegment(sketch, "E748", {"start": v(7.1, 2.29) * mm, "end": v(7.11, 2.3) * mm});
            skLineSegment(sketch, "E749", {"start": v(7.11, 2.3) * mm, "end": v(7.13, 2.33) * mm});
            skLineSegment(sketch, "E750", {"start": v(7.13, 2.33) * mm, "end": v(7.15, 2.35) * mm});
            skLineSegment(sketch, "E751", {"start": v(7.15, 2.35) * mm, "end": v(7.18, 2.37) * mm});
            skLineSegment(sketch, "E752", {"start": v(7.18, 2.37) * mm, "end": v(7.2, 2.39) * mm});
            skLineSegment(sketch, "E753", {"start": v(7.2, 2.39) * mm, "end": v(7.22, 2.41) * mm});
            skLineSegment(sketch, "E754", {"start": v(7.22, 2.41) * mm, "end": v(7.24, 2.43) * mm});
            skLineSegment(sketch, "E755", {"start": v(7.24, 2.43) * mm, "end": v(7.26, 2.46) * mm});
            skLineSegment(sketch, "E756", {"start": v(7.26, 2.46) * mm, "end": v(7.28, 2.48) * mm});
            skLineSegment(sketch, "E757", {"start": v(7.28, 2.48) * mm, "end": v(7.3, 2.5) * mm});
            skLineSegment(sketch, "E758", {"start": v(7.3, 2.5) * mm, "end": v(7.33, 2.53) * mm});
            skArc(sketch, "E759", {"start": v(7.33, 2.53) * mm, "mid": v(7.28, 2.65) * mm, "end": v(7.24, 2.77) * mm});
            skLineSegment(sketch, "E760", {"start": v(6.65, 1.65) * mm, "end": v(6.65, 1.65) * mm});
            skLineSegment(sketch, "E761", {"start": v(6.65, 1.65) * mm, "end": v(6.66, 1.64) * mm});
            skLineSegment(sketch, "E762", {"start": v(6.66, 1.64) * mm, "end": v(6.66, 1.64) * mm});
            skLineSegment(sketch, "E763", {"start": v(6.66, 1.64) * mm, "end": v(6.67, 1.63) * mm});
            skLineSegment(sketch, "E764", {"start": v(6.67, 1.63) * mm, "end": v(6.68, 1.63) * mm});
            skLineSegment(sketch, "E765", {"start": v(6.68, 1.63) * mm, "end": v(6.7, 1.63) * mm});
            skLineSegment(sketch, "E766", {"start": v(6.7, 1.63) * mm, "end": v(6.71, 1.63) * mm});
            skLineSegment(sketch, "E767", {"start": v(6.71, 1.63) * mm, "end": v(6.72, 1.63) * mm});
            skLineSegment(sketch, "E768", {"start": v(6.72, 1.63) * mm, "end": v(6.74, 1.63) * mm});
            skLineSegment(sketch, "E769", {"start": v(6.74, 1.63) * mm, "end": v(6.75, 1.63) * mm});
            skLineSegment(sketch, "E770", {"start": v(6.75, 1.63) * mm, "end": v(6.76, 1.63) * mm});
            skLineSegment(sketch, "E771", {"start": v(6.76, 1.63) * mm, "end": v(6.78, 1.63) * mm});
            skLineSegment(sketch, "E772", {"start": v(6.78, 1.63) * mm, "end": v(6.8, 1.63) * mm});
            skLineSegment(sketch, "E773", {"start": v(6.8, 1.63) * mm, "end": v(6.81, 1.63) * mm});
            skLineSegment(sketch, "E774", {"start": v(6.81, 1.63) * mm, "end": v(6.83, 1.63) * mm});
            skLineSegment(sketch, "E775", {"start": v(6.83, 1.63) * mm, "end": v(6.84, 1.63) * mm});
            skLineSegment(sketch, "E776", {"start": v(6.84, 1.63) * mm, "end": v(6.86, 1.63) * mm});
            skLineSegment(sketch, "E777", {"start": v(6.86, 1.63) * mm, "end": v(6.88, 1.63) * mm});
            skLineSegment(sketch, "E778", {"start": v(6.88, 1.63) * mm, "end": v(6.9, 1.62) * mm});
            skLineSegment(sketch, "E779", {"start": v(6.9, 1.62) * mm, "end": v(6.92, 1.62) * mm});
            skLineSegment(sketch, "E780", {"start": v(6.92, 1.62) * mm, "end": v(6.94, 1.62) * mm});
            skLineSegment(sketch, "E781", {"start": v(6.94, 1.62) * mm, "end": v(6.96, 1.62) * mm});
            skLineSegment(sketch, "E782", {"start": v(6.96, 1.62) * mm, "end": v(6.98, 1.62) * mm});
            skLineSegment(sketch, "E783", {"start": v(6.98, 1.62) * mm, "end": v(7, 1.61) * mm});
            skLineSegment(sketch, "E784", {"start": v(7, 1.61) * mm, "end": v(7.02, 1.61) * mm});
            skLineSegment(sketch, "E785", {"start": v(7.02, 1.61) * mm, "end": v(7.04, 1.6) * mm});
            skLineSegment(sketch, "E786", {"start": v(7.04, 1.6) * mm, "end": v(7.06, 1.6) * mm});
            skLineSegment(sketch, "E787", {"start": v(7.06, 1.6) * mm, "end": v(7.09, 1.6) * mm});
            skLineSegment(sketch, "E788", {"start": v(7.09, 1.6) * mm, "end": v(7.1, 1.6) * mm});
            skLineSegment(sketch, "E789", {"start": v(7.1, 1.6) * mm, "end": v(7.13, 1.6) * mm});
            skLineSegment(sketch, "E790", {"start": v(7.13, 1.6) * mm, "end": v(7.16, 1.6) * mm});
            skLineSegment(sketch, "E791", {"start": v(7.16, 1.6) * mm, "end": v(7.18, 1.59) * mm});
            skLineSegment(sketch, "E792", {"start": v(7.18, 1.59) * mm, "end": v(7.2, 1.58) * mm});
            skLineSegment(sketch, "E793", {"start": v(7.2, 1.58) * mm, "end": v(7.23, 1.58) * mm});
            skLineSegment(sketch, "E794", {"start": v(7.23, 1.58) * mm, "end": v(7.26, 1.57) * mm});
            skLineSegment(sketch, "E795", {"start": v(7.26, 1.57) * mm, "end": v(7.29, 1.57) * mm});
            skLineSegment(sketch, "E796", {"start": v(7.29, 1.57) * mm, "end": v(7.31, 1.56) * mm});
            skLineSegment(sketch, "E797", {"start": v(7.31, 1.56) * mm, "end": v(7.34, 1.55) * mm});
            skLineSegment(sketch, "E798", {"start": v(7.34, 1.55) * mm, "end": v(7.37, 1.55) * mm});
            skLineSegment(sketch, "E799", {"start": v(7.37, 1.55) * mm, "end": v(7.4, 1.54) * mm});
            skLineSegment(sketch, "E800", {"start": v(7.4, 1.54) * mm, "end": v(7.43, 1.53) * mm});
            skLineSegment(sketch, "E801", {"start": v(7.43, 1.53) * mm, "end": v(7.46, 1.52) * mm});
            skLineSegment(sketch, "E802", {"start": v(7.46, 1.52) * mm, "end": v(7.49, 1.51) * mm});
            skLineSegment(sketch, "E803", {"start": v(7.49, 1.51) * mm, "end": v(7.52, 1.5) * mm});
            skLineSegment(sketch, "E804", {"start": v(7.52, 1.5) * mm, "end": v(7.55, 1.5) * mm});
            skLineSegment(sketch, "E805", {"start": v(7.55, 1.5) * mm, "end": v(7.58, 1.49) * mm});
            skLineSegment(sketch, "E806", {"start": v(7.58, 1.49) * mm, "end": v(7.61, 1.47) * mm});
            skLineSegment(sketch, "E807", {"start": v(6.81, 0.72) * mm, "end": v(6.81, 0.73) * mm});
            skLineSegment(sketch, "E808", {"start": v(6.81, 0.73) * mm, "end": v(6.82, 0.73) * mm});
            skLineSegment(sketch, "E809", {"start": v(6.82, 0.73) * mm, "end": v(6.82, 0.74) * mm});
            skLineSegment(sketch, "E810", {"start": v(6.82, 0.74) * mm, "end": v(6.83, 0.75) * mm});
            skLineSegment(sketch, "E811", {"start": v(6.83, 0.75) * mm, "end": v(6.84, 0.75) * mm});
            skLineSegment(sketch, "E812", {"start": v(6.84, 0.75) * mm, "end": v(6.85, 0.76) * mm});
            skLineSegment(sketch, "E813", {"start": v(6.85, 0.76) * mm, "end": v(6.87, 0.77) * mm});
            skLineSegment(sketch, "E814", {"start": v(6.87, 0.77) * mm, "end": v(6.88, 0.77) * mm});
            skLineSegment(sketch, "E815", {"start": v(6.88, 0.77) * mm, "end": v(6.89, 0.77) * mm});
            skLineSegment(sketch, "E816", {"start": v(6.89, 0.77) * mm, "end": v(6.9, 0.78) * mm});
            skLineSegment(sketch, "E817", {"start": v(6.9, 0.78) * mm, "end": v(6.91, 0.78) * mm});
            skLineSegment(sketch, "E818", {"start": v(6.91, 0.78) * mm, "end": v(6.93, 0.79) * mm});
            skLineSegment(sketch, "E819", {"start": v(6.93, 0.79) * mm, "end": v(6.94, 0.8) * mm});
            skLineSegment(sketch, "E820", {"start": v(6.94, 0.8) * mm, "end": v(6.96, 0.8) * mm});
            skLineSegment(sketch, "E821", {"start": v(6.96, 0.8) * mm, "end": v(6.97, 0.8) * mm});
            skLineSegment(sketch, "E822", {"start": v(6.97, 0.8) * mm, "end": v(6.99, 0.81) * mm});
            skLineSegment(sketch, "E823", {"start": v(6.99, 0.81) * mm, "end": v(7, 0.82) * mm});
            skLineSegment(sketch, "E824", {"start": v(7, 0.82) * mm, "end": v(7.02, 0.83) * mm});
            skLineSegment(sketch, "E825", {"start": v(7.02, 0.83) * mm, "end": v(7.04, 0.83) * mm});
            skLineSegment(sketch, "E826", {"start": v(7.04, 0.83) * mm, "end": v(7.05, 0.84) * mm});
            skLineSegment(sketch, "E827", {"start": v(7.05, 0.84) * mm, "end": v(7.07, 0.85) * mm});
            skLineSegment(sketch, "E828", {"start": v(7.07, 0.85) * mm, "end": v(7.09, 0.86) * mm});
            skLineSegment(sketch, "E829", {"start": v(7.09, 0.86) * mm, "end": v(7.1, 0.87) * mm});
            skLineSegment(sketch, "E830", {"start": v(7.1, 0.87) * mm, "end": v(7.13, 0.88) * mm});
            skLineSegment(sketch, "E831", {"start": v(7.13, 0.88) * mm, "end": v(7.15, 0.89) * mm});
            skLineSegment(sketch, "E832", {"start": v(7.15, 0.89) * mm, "end": v(7.17, 0.9) * mm});
            skLineSegment(sketch, "E833", {"start": v(7.17, 0.9) * mm, "end": v(7.19, 0.9) * mm});
            skLineSegment(sketch, "E834", {"start": v(7.19, 0.9) * mm, "end": v(7.2, 0.92) * mm});
            skLineSegment(sketch, "E835", {"start": v(7.2, 0.92) * mm, "end": v(7.23, 0.93) * mm});
            skLineSegment(sketch, "E836", {"start": v(7.23, 0.93) * mm, "end": v(7.25, 0.94) * mm});
            skLineSegment(sketch, "E837", {"start": v(7.25, 0.94) * mm, "end": v(7.27, 0.95) * mm});
            skLineSegment(sketch, "E838", {"start": v(7.27, 0.95) * mm, "end": v(7.3, 0.97) * mm});
            skLineSegment(sketch, "E839", {"start": v(7.3, 0.97) * mm, "end": v(7.31, 0.98) * mm});
            skLineSegment(sketch, "E840", {"start": v(7.31, 0.98) * mm, "end": v(7.34, 1) * mm});
            skLineSegment(sketch, "E841", {"start": v(7.34, 1) * mm, "end": v(7.36, 1) * mm});
            skLineSegment(sketch, "E842", {"start": v(7.36, 1) * mm, "end": v(7.38, 1.02) * mm});
            skLineSegment(sketch, "E843", {"start": v(7.38, 1.02) * mm, "end": v(7.4, 1.04) * mm});
            skLineSegment(sketch, "E844", {"start": v(7.4, 1.04) * mm, "end": v(7.43, 1.05) * mm});
            skLineSegment(sketch, "E845", {"start": v(7.43, 1.05) * mm, "end": v(7.45, 1.07) * mm});
            skLineSegment(sketch, "E846", {"start": v(7.45, 1.07) * mm, "end": v(7.48, 1.09) * mm});
            skLineSegment(sketch, "E847", {"start": v(7.48, 1.09) * mm, "end": v(7.5, 1.1) * mm});
            skLineSegment(sketch, "E848", {"start": v(7.5, 1.1) * mm, "end": v(7.53, 1.12) * mm});
            skLineSegment(sketch, "E849", {"start": v(7.53, 1.12) * mm, "end": v(7.55, 1.14) * mm});
            skLineSegment(sketch, "E850", {"start": v(7.55, 1.14) * mm, "end": v(7.58, 1.16) * mm});
            skLineSegment(sketch, "E851", {"start": v(7.58, 1.16) * mm, "end": v(7.6, 1.18) * mm});
            skLineSegment(sketch, "E852", {"start": v(7.6, 1.18) * mm, "end": v(7.63, 1.2) * mm});
            skLineSegment(sketch, "E853", {"start": v(7.63, 1.2) * mm, "end": v(7.66, 1.22) * mm});
            skArc(sketch, "E854", {"start": v(7.66, 1.22) * mm, "mid": v(7.63, 1.35) * mm, "end": v(7.61, 1.47) * mm});
            skLineSegment(sketch, "E855", {"start": v(6.84, 0.47) * mm, "end": v(6.84, 0.47) * mm});
            skLineSegment(sketch, "E856", {"start": v(6.84, 0.47) * mm, "end": v(6.84, 0.46) * mm});
            skLineSegment(sketch, "E857", {"start": v(6.84, 0.46) * mm, "end": v(6.85, 0.45) * mm});
            skLineSegment(sketch, "E858", {"start": v(6.85, 0.45) * mm, "end": v(6.86, 0.45) * mm});
            skLineSegment(sketch, "E859", {"start": v(6.86, 0.45) * mm, "end": v(6.87, 0.45) * mm});
            skLineSegment(sketch, "E860", {"start": v(6.87, 0.45) * mm, "end": v(6.88, 0.44) * mm});
            skLineSegment(sketch, "E861", {"start": v(6.88, 0.44) * mm, "end": v(6.9, 0.44) * mm});
            skLineSegment(sketch, "E862", {"start": v(6.9, 0.44) * mm, "end": v(6.9, 0.44) * mm});
            skLineSegment(sketch, "E863", {"start": v(6.9, 0.44) * mm, "end": v(6.92, 0.43) * mm});
            skLineSegment(sketch, "E864", {"start": v(6.92, 0.43) * mm, "end": v(6.93, 0.43) * mm});
            skLineSegment(sketch, "E865", {"start": v(6.93, 0.43) * mm, "end": v(6.94, 0.43) * mm});
            skLineSegment(sketch, "E866", {"start": v(6.94, 0.43) * mm, "end": v(6.96, 0.43) * mm});
            skLineSegment(sketch, "E867", {"start": v(6.96, 0.43) * mm, "end": v(6.97, 0.42) * mm});
            skLineSegment(sketch, "E868", {"start": v(6.97, 0.42) * mm, "end": v(6.99, 0.42) * mm});
            skLineSegment(sketch, "E869", {"start": v(6.99, 0.42) * mm, "end": v(7, 0.42) * mm});
            skLineSegment(sketch, "E870", {"start": v(7, 0.42) * mm, "end": v(7.02, 0.41) * mm});
            skLineSegment(sketch, "E871", {"start": v(7.02, 0.41) * mm, "end": v(7.04, 0.41) * mm});
            skLineSegment(sketch, "E872", {"start": v(7.04, 0.41) * mm, "end": v(7.06, 0.4) * mm});
            skLineSegment(sketch, "E873", {"start": v(7.06, 0.4) * mm, "end": v(7.07, 0.4) * mm});
            skLineSegment(sketch, "E874", {"start": v(7.07, 0.4) * mm, "end": v(7.1, 0.4) * mm});
            skLineSegment(sketch, "E875", {"start": v(7.1, 0.4) * mm, "end": v(7.11, 0.4) * mm});
            skLineSegment(sketch, "E876", {"start": v(7.11, 0.4) * mm, "end": v(7.13, 0.39) * mm});
            skLineSegment(sketch, "E877", {"start": v(7.13, 0.39) * mm, "end": v(7.15, 0.38) * mm});
            skLineSegment(sketch, "E878", {"start": v(7.15, 0.38) * mm, "end": v(7.17, 0.38) * mm});
            skLineSegment(sketch, "E879", {"start": v(7.17, 0.38) * mm, "end": v(7.2, 0.37) * mm});
            skLineSegment(sketch, "E880", {"start": v(7.2, 0.37) * mm, "end": v(7.21, 0.36) * mm});
            skLineSegment(sketch, "E881", {"start": v(7.21, 0.36) * mm, "end": v(7.23, 0.36) * mm});
            skLineSegment(sketch, "E882", {"start": v(7.23, 0.36) * mm, "end": v(7.26, 0.35) * mm});
            skLineSegment(sketch, "E883", {"start": v(7.26, 0.35) * mm, "end": v(7.28, 0.34) * mm});
            skLineSegment(sketch, "E884", {"start": v(7.28, 0.34) * mm, "end": v(7.3, 0.33) * mm});
            skLineSegment(sketch, "E885", {"start": v(7.3, 0.33) * mm, "end": v(7.32, 0.32) * mm});
            skLineSegment(sketch, "E886", {"start": v(7.32, 0.32) * mm, "end": v(7.35, 0.32) * mm});
            skLineSegment(sketch, "E887", {"start": v(7.35, 0.32) * mm, "end": v(7.37, 0.3) * mm});
            skLineSegment(sketch, "E888", {"start": v(7.37, 0.3) * mm, "end": v(7.4, 0.3) * mm});
            skLineSegment(sketch, "E889", {"start": v(7.4, 0.3) * mm, "end": v(7.42, 0.29) * mm});
            skLineSegment(sketch, "E890", {"start": v(7.42, 0.29) * mm, "end": v(7.45, 0.28) * mm});
            skLineSegment(sketch, "E891", {"start": v(7.45, 0.28) * mm, "end": v(7.47, 0.27) * mm});
            skLineSegment(sketch, "E892", {"start": v(7.47, 0.27) * mm, "end": v(7.5, 0.25) * mm});
            skLineSegment(sketch, "E893", {"start": v(7.5, 0.25) * mm, "end": v(7.53, 0.24) * mm});
            skLineSegment(sketch, "E894", {"start": v(7.53, 0.24) * mm, "end": v(7.55, 0.23) * mm});
            skLineSegment(sketch, "E895", {"start": v(7.55, 0.23) * mm, "end": v(7.58, 0.22) * mm});
            skLineSegment(sketch, "E896", {"start": v(7.58, 0.22) * mm, "end": v(7.6, 0.2) * mm});
            skLineSegment(sketch, "E897", {"start": v(7.6, 0.2) * mm, "end": v(7.64, 0.2) * mm});
            skLineSegment(sketch, "E898", {"start": v(7.64, 0.2) * mm, "end": v(7.66, 0.18) * mm});
            skLineSegment(sketch, "E899", {"start": v(7.66, 0.18) * mm, "end": v(7.7, 0.16) * mm});
            skLineSegment(sketch, "E900", {"start": v(7.7, 0.16) * mm, "end": v(7.72, 0.15) * mm});
            skLineSegment(sketch, "E901", {"start": v(7.72, 0.15) * mm, "end": v(7.75, 0.13) * mm});
            skLineSegment(sketch, "E902", {"start": v(6.84, -0.47) * mm, "end": v(6.84, -0.47) * mm});
            skLineSegment(sketch, "E903", {"start": v(6.84, -0.47) * mm, "end": v(6.84, -0.46) * mm});
            skLineSegment(sketch, "E904", {"start": v(6.84, -0.46) * mm, "end": v(6.85, -0.45) * mm});
            skLineSegment(sketch, "E905", {"start": v(6.85, -0.45) * mm, "end": v(6.86, -0.45) * mm});
            skLineSegment(sketch, "E906", {"start": v(6.86, -0.45) * mm, "end": v(6.87, -0.45) * mm});
            skLineSegment(sketch, "E907", {"start": v(6.87, -0.45) * mm, "end": v(6.88, -0.44) * mm});
            skLineSegment(sketch, "E908", {"start": v(6.88, -0.44) * mm, "end": v(6.9, -0.44) * mm});
            skLineSegment(sketch, "E909", {"start": v(6.9, -0.44) * mm, "end": v(6.9, -0.44) * mm});
            skLineSegment(sketch, "E910", {"start": v(6.9, -0.44) * mm, "end": v(6.92, -0.43) * mm});
            skLineSegment(sketch, "E911", {"start": v(6.92, -0.43) * mm, "end": v(6.93, -0.43) * mm});
            skLineSegment(sketch, "E912", {"start": v(6.93, -0.43) * mm, "end": v(6.94, -0.43) * mm});
            skLineSegment(sketch, "E913", {"start": v(6.94, -0.43) * mm, "end": v(6.96, -0.43) * mm});
            skLineSegment(sketch, "E914", {"start": v(6.96, -0.43) * mm, "end": v(6.97, -0.42) * mm});
            skLineSegment(sketch, "E915", {"start": v(6.97, -0.42) * mm, "end": v(6.99, -0.42) * mm});
            skLineSegment(sketch, "E916", {"start": v(6.99, -0.42) * mm, "end": v(7, -0.42) * mm});
            skLineSegment(sketch, "E917", {"start": v(7, -0.42) * mm, "end": v(7.02, -0.41) * mm});
            skLineSegment(sketch, "E918", {"start": v(7.02, -0.41) * mm, "end": v(7.04, -0.41) * mm});
            skLineSegment(sketch, "E919", {"start": v(7.04, -0.41) * mm, "end": v(7.06, -0.4) * mm});
            skLineSegment(sketch, "E920", {"start": v(7.06, -0.4) * mm, "end": v(7.07, -0.4) * mm});
            skLineSegment(sketch, "E921", {"start": v(7.07, -0.4) * mm, "end": v(7.1, -0.4) * mm});
            skLineSegment(sketch, "E922", {"start": v(7.1, -0.4) * mm, "end": v(7.11, -0.4) * mm});
            skLineSegment(sketch, "E923", {"start": v(7.11, -0.4) * mm, "end": v(7.13, -0.39) * mm});
            skLineSegment(sketch, "E924", {"start": v(7.13, -0.39) * mm, "end": v(7.15, -0.38) * mm});
            skLineSegment(sketch, "E925", {"start": v(7.15, -0.38) * mm, "end": v(7.17, -0.38) * mm});
            skLineSegment(sketch, "E926", {"start": v(7.17, -0.38) * mm, "end": v(7.2, -0.37) * mm});
            skLineSegment(sketch, "E927", {"start": v(7.2, -0.37) * mm, "end": v(7.21, -0.36) * mm});
            skLineSegment(sketch, "E928", {"start": v(7.21, -0.36) * mm, "end": v(7.23, -0.36) * mm});
            skLineSegment(sketch, "E929", {"start": v(7.23, -0.36) * mm, "end": v(7.26, -0.35) * mm});
            skLineSegment(sketch, "E930", {"start": v(7.26, -0.35) * mm, "end": v(7.28, -0.34) * mm});
            skLineSegment(sketch, "E931", {"start": v(7.28, -0.34) * mm, "end": v(7.3, -0.33) * mm});
            skLineSegment(sketch, "E932", {"start": v(7.3, -0.33) * mm, "end": v(7.32, -0.32) * mm});
            skLineSegment(sketch, "E933", {"start": v(7.32, -0.32) * mm, "end": v(7.35, -0.32) * mm});
            skLineSegment(sketch, "E934", {"start": v(7.35, -0.32) * mm, "end": v(7.37, -0.3) * mm});
            skLineSegment(sketch, "E935", {"start": v(7.37, -0.3) * mm, "end": v(7.4, -0.3) * mm});
            skLineSegment(sketch, "E936", {"start": v(7.4, -0.3) * mm, "end": v(7.42, -0.29) * mm});
            skLineSegment(sketch, "E937", {"start": v(7.42, -0.29) * mm, "end": v(7.45, -0.28) * mm});
            skLineSegment(sketch, "E938", {"start": v(7.45, -0.28) * mm, "end": v(7.47, -0.27) * mm});
            skLineSegment(sketch, "E939", {"start": v(7.47, -0.27) * mm, "end": v(7.5, -0.25) * mm});
            skLineSegment(sketch, "E940", {"start": v(7.5, -0.25) * mm, "end": v(7.53, -0.24) * mm});
            skLineSegment(sketch, "E941", {"start": v(7.53, -0.24) * mm, "end": v(7.55, -0.23) * mm});
            skLineSegment(sketch, "E942", {"start": v(7.55, -0.23) * mm, "end": v(7.58, -0.22) * mm});
            skLineSegment(sketch, "E943", {"start": v(7.58, -0.22) * mm, "end": v(7.6, -0.2) * mm});
            skLineSegment(sketch, "E944", {"start": v(7.6, -0.2) * mm, "end": v(7.64, -0.2) * mm});
            skLineSegment(sketch, "E945", {"start": v(7.64, -0.2) * mm, "end": v(7.66, -0.18) * mm});
            skLineSegment(sketch, "E946", {"start": v(7.66, -0.18) * mm, "end": v(7.7, -0.16) * mm});
            skLineSegment(sketch, "E947", {"start": v(7.7, -0.16) * mm, "end": v(7.72, -0.15) * mm});
            skLineSegment(sketch, "E948", {"start": v(7.72, -0.15) * mm, "end": v(7.75, -0.13) * mm});
            skArc(sketch, "E949", {"start": v(7.75, -0.13) * mm, "mid": v(7.75, 0) * mm, "end": v(7.75, 0.13) * mm});
            skLineSegment(sketch, "E950", {"start": v(6.81, -0.72) * mm, "end": v(6.81, -0.73) * mm});
            skLineSegment(sketch, "E951", {"start": v(6.81, -0.73) * mm, "end": v(6.82, -0.73) * mm});
            skLineSegment(sketch, "E952", {"start": v(6.82, -0.73) * mm, "end": v(6.82, -0.74) * mm});
            skLineSegment(sketch, "E953", {"start": v(6.82, -0.74) * mm, "end": v(6.83, -0.75) * mm});
            skLineSegment(sketch, "E954", {"start": v(6.83, -0.75) * mm, "end": v(6.84, -0.75) * mm});
            skLineSegment(sketch, "E955", {"start": v(6.84, -0.75) * mm, "end": v(6.85, -0.76) * mm});
            skLineSegment(sketch, "E956", {"start": v(6.85, -0.76) * mm, "end": v(6.87, -0.77) * mm});
            skLineSegment(sketch, "E957", {"start": v(6.87, -0.77) * mm, "end": v(6.88, -0.77) * mm});
            skLineSegment(sketch, "E958", {"start": v(6.88, -0.77) * mm, "end": v(6.89, -0.77) * mm});
            skLineSegment(sketch, "E959", {"start": v(6.89, -0.77) * mm, "end": v(6.9, -0.78) * mm});
            skLineSegment(sketch, "E960", {"start": v(6.9, -0.78) * mm, "end": v(6.91, -0.78) * mm});
            skLineSegment(sketch, "E961", {"start": v(6.91, -0.78) * mm, "end": v(6.93, -0.79) * mm});
            skLineSegment(sketch, "E962", {"start": v(6.93, -0.79) * mm, "end": v(6.94, -0.8) * mm});
            skLineSegment(sketch, "E963", {"start": v(6.94, -0.8) * mm, "end": v(6.96, -0.8) * mm});
            skLineSegment(sketch, "E964", {"start": v(6.96, -0.8) * mm, "end": v(6.97, -0.8) * mm});
            skLineSegment(sketch, "E965", {"start": v(6.97, -0.8) * mm, "end": v(6.99, -0.81) * mm});
            skLineSegment(sketch, "E966", {"start": v(6.99, -0.81) * mm, "end": v(7, -0.82) * mm});
            skLineSegment(sketch, "E967", {"start": v(7, -0.82) * mm, "end": v(7.02, -0.83) * mm});
            skLineSegment(sketch, "E968", {"start": v(7.02, -0.83) * mm, "end": v(7.04, -0.83) * mm});
            skLineSegment(sketch, "E969", {"start": v(7.04, -0.83) * mm, "end": v(7.05, -0.84) * mm});
            skLineSegment(sketch, "E970", {"start": v(7.05, -0.84) * mm, "end": v(7.07, -0.85) * mm});
            skLineSegment(sketch, "E971", {"start": v(7.07, -0.85) * mm, "end": v(7.09, -0.86) * mm});
            skLineSegment(sketch, "E972", {"start": v(7.09, -0.86) * mm, "end": v(7.1, -0.87) * mm});
            skLineSegment(sketch, "E973", {"start": v(7.1, -0.87) * mm, "end": v(7.13, -0.88) * mm});
            skLineSegment(sketch, "E974", {"start": v(7.13, -0.88) * mm, "end": v(7.15, -0.89) * mm});
            skLineSegment(sketch, "E975", {"start": v(7.15, -0.89) * mm, "end": v(7.17, -0.9) * mm});
            skLineSegment(sketch, "E976", {"start": v(7.17, -0.9) * mm, "end": v(7.19, -0.9) * mm});
            skLineSegment(sketch, "E977", {"start": v(7.19, -0.9) * mm, "end": v(7.2, -0.92) * mm});
            skLineSegment(sketch, "E978", {"start": v(7.2, -0.92) * mm, "end": v(7.23, -0.93) * mm});
            skLineSegment(sketch, "E979", {"start": v(7.23, -0.93) * mm, "end": v(7.25, -0.94) * mm});
            skLineSegment(sketch, "E980", {"start": v(7.25, -0.94) * mm, "end": v(7.27, -0.95) * mm});
            skLineSegment(sketch, "E981", {"start": v(7.27, -0.95) * mm, "end": v(7.3, -0.97) * mm});
            skLineSegment(sketch, "E982", {"start": v(7.3, -0.97) * mm, "end": v(7.31, -0.98) * mm});
            skLineSegment(sketch, "E983", {"start": v(7.31, -0.98) * mm, "end": v(7.34, -1) * mm});
            skLineSegment(sketch, "E984", {"start": v(7.34, -1) * mm, "end": v(7.36, -1) * mm});
            skLineSegment(sketch, "E985", {"start": v(7.36, -1) * mm, "end": v(7.38, -1.02) * mm});
            skLineSegment(sketch, "E986", {"start": v(7.38, -1.02) * mm, "end": v(7.4, -1.04) * mm});
            skLineSegment(sketch, "E987", {"start": v(7.4, -1.04) * mm, "end": v(7.43, -1.05) * mm});
            skLineSegment(sketch, "E988", {"start": v(7.43, -1.05) * mm, "end": v(7.45, -1.07) * mm});
            skLineSegment(sketch, "E989", {"start": v(7.45, -1.07) * mm, "end": v(7.48, -1.09) * mm});
            skLineSegment(sketch, "E990", {"start": v(7.48, -1.09) * mm, "end": v(7.5, -1.1) * mm});
            skLineSegment(sketch, "E991", {"start": v(7.5, -1.1) * mm, "end": v(7.53, -1.12) * mm});
            skLineSegment(sketch, "E992", {"start": v(7.53, -1.12) * mm, "end": v(7.55, -1.14) * mm});
            skLineSegment(sketch, "E993", {"start": v(7.55, -1.14) * mm, "end": v(7.58, -1.16) * mm});
            skLineSegment(sketch, "E994", {"start": v(7.58, -1.16) * mm, "end": v(7.6, -1.18) * mm});
            skLineSegment(sketch, "E995", {"start": v(7.6, -1.18) * mm, "end": v(7.63, -1.2) * mm});
            skLineSegment(sketch, "E996", {"start": v(7.63, -1.2) * mm, "end": v(7.66, -1.22) * mm});
            skLineSegment(sketch, "E997", {"start": v(6.65, -1.65) * mm, "end": v(6.65, -1.65) * mm});
            skLineSegment(sketch, "E998", {"start": v(6.65, -1.65) * mm, "end": v(6.66, -1.64) * mm});
            skLineSegment(sketch, "E999", {"start": v(6.66, -1.64) * mm, "end": v(6.66, -1.64) * mm});
            skLineSegment(sketch, "E1000", {"start": v(6.66, -1.64) * mm, "end": v(6.67, -1.63) * mm});
            skLineSegment(sketch, "E1001", {"start": v(6.67, -1.63) * mm, "end": v(6.68, -1.63) * mm});
            skLineSegment(sketch, "E1002", {"start": v(6.68, -1.63) * mm, "end": v(6.7, -1.63) * mm});
            skLineSegment(sketch, "E1003", {"start": v(6.7, -1.63) * mm, "end": v(6.71, -1.63) * mm});
            skLineSegment(sketch, "E1004", {"start": v(6.71, -1.63) * mm, "end": v(6.72, -1.63) * mm});
            skLineSegment(sketch, "E1005", {"start": v(6.72, -1.63) * mm, "end": v(6.74, -1.63) * mm});
            skLineSegment(sketch, "E1006", {"start": v(6.74, -1.63) * mm, "end": v(6.75, -1.63) * mm});
            skLineSegment(sketch, "E1007", {"start": v(6.75, -1.63) * mm, "end": v(6.76, -1.63) * mm});
            skLineSegment(sketch, "E1008", {"start": v(6.76, -1.63) * mm, "end": v(6.78, -1.63) * mm});
            skLineSegment(sketch, "E1009", {"start": v(6.78, -1.63) * mm, "end": v(6.8, -1.63) * mm});
            skLineSegment(sketch, "E1010", {"start": v(6.8, -1.63) * mm, "end": v(6.81, -1.63) * mm});
            skLineSegment(sketch, "E1011", {"start": v(6.81, -1.63) * mm, "end": v(6.83, -1.63) * mm});
            skLineSegment(sketch, "E1012", {"start": v(6.83, -1.63) * mm, "end": v(6.84, -1.63) * mm});
            skLineSegment(sketch, "E1013", {"start": v(6.84, -1.63) * mm, "end": v(6.86, -1.63) * mm});
            skLineSegment(sketch, "E1014", {"start": v(6.86, -1.63) * mm, "end": v(6.88, -1.63) * mm});
            skLineSegment(sketch, "E1015", {"start": v(6.88, -1.63) * mm, "end": v(6.9, -1.62) * mm});
            skLineSegment(sketch, "E1016", {"start": v(6.9, -1.62) * mm, "end": v(6.92, -1.62) * mm});
            skLineSegment(sketch, "E1017", {"start": v(6.92, -1.62) * mm, "end": v(6.94, -1.62) * mm});
            skLineSegment(sketch, "E1018", {"start": v(6.94, -1.62) * mm, "end": v(6.96, -1.62) * mm});
            skLineSegment(sketch, "E1019", {"start": v(6.96, -1.62) * mm, "end": v(6.98, -1.62) * mm});
            skLineSegment(sketch, "E1020", {"start": v(6.98, -1.62) * mm, "end": v(7, -1.61) * mm});
            skLineSegment(sketch, "E1021", {"start": v(7, -1.61) * mm, "end": v(7.02, -1.61) * mm});
            skLineSegment(sketch, "E1022", {"start": v(7.02, -1.61) * mm, "end": v(7.04, -1.6) * mm});
            skLineSegment(sketch, "E1023", {"start": v(7.04, -1.6) * mm, "end": v(7.06, -1.6) * mm});
            skLineSegment(sketch, "E1024", {"start": v(7.06, -1.6) * mm, "end": v(7.09, -1.6) * mm});
            skLineSegment(sketch, "E1025", {"start": v(7.09, -1.6) * mm, "end": v(7.1, -1.6) * mm});
            skLineSegment(sketch, "E1026", {"start": v(7.1, -1.6) * mm, "end": v(7.13, -1.6) * mm});
            skLineSegment(sketch, "E1027", {"start": v(7.13, -1.6) * mm, "end": v(7.16, -1.6) * mm});
            skLineSegment(sketch, "E1028", {"start": v(7.16, -1.6) * mm, "end": v(7.18, -1.59) * mm});
            skLineSegment(sketch, "E1029", {"start": v(7.18, -1.59) * mm, "end": v(7.2, -1.58) * mm});
            skLineSegment(sketch, "E1030", {"start": v(7.2, -1.58) * mm, "end": v(7.23, -1.58) * mm});
            skLineSegment(sketch, "E1031", {"start": v(7.23, -1.58) * mm, "end": v(7.26, -1.57) * mm});
            skLineSegment(sketch, "E1032", {"start": v(7.26, -1.57) * mm, "end": v(7.29, -1.57) * mm});
            skLineSegment(sketch, "E1033", {"start": v(7.29, -1.57) * mm, "end": v(7.31, -1.56) * mm});
            skLineSegment(sketch, "E1034", {"start": v(7.31, -1.56) * mm, "end": v(7.34, -1.55) * mm});
            skLineSegment(sketch, "E1035", {"start": v(7.34, -1.55) * mm, "end": v(7.37, -1.55) * mm});
            skLineSegment(sketch, "E1036", {"start": v(7.37, -1.55) * mm, "end": v(7.4, -1.54) * mm});
            skLineSegment(sketch, "E1037", {"start": v(7.4, -1.54) * mm, "end": v(7.43, -1.53) * mm});
            skLineSegment(sketch, "E1038", {"start": v(7.43, -1.53) * mm, "end": v(7.46, -1.52) * mm});
            skLineSegment(sketch, "E1039", {"start": v(7.46, -1.52) * mm, "end": v(7.49, -1.51) * mm});
            skLineSegment(sketch, "E1040", {"start": v(7.49, -1.51) * mm, "end": v(7.52, -1.5) * mm});
            skLineSegment(sketch, "E1041", {"start": v(7.52, -1.5) * mm, "end": v(7.55, -1.5) * mm});
            skLineSegment(sketch, "E1042", {"start": v(7.55, -1.5) * mm, "end": v(7.58, -1.49) * mm});
            skLineSegment(sketch, "E1043", {"start": v(7.58, -1.49) * mm, "end": v(7.61, -1.47) * mm});
            skArc(sketch, "E1044", {"start": v(7.61, -1.47) * mm, "mid": v(7.63, -1.35) * mm, "end": v(7.66, -1.22) * mm});
            skLineSegment(sketch, "E1045", {"start": v(6.58, -1.9) * mm, "end": v(6.58, -1.9) * mm});
            skLineSegment(sketch, "E1046", {"start": v(6.58, -1.9) * mm, "end": v(6.59, -1.9) * mm});
            skLineSegment(sketch, "E1047", {"start": v(6.59, -1.9) * mm, "end": v(6.59, -1.91) * mm});
            skLineSegment(sketch, "E1048", {"start": v(6.59, -1.91) * mm, "end": v(6.6, -1.92) * mm});
            skLineSegment(sketch, "E1049", {"start": v(6.6, -1.92) * mm, "end": v(6.6, -1.93) * mm});
            skLineSegment(sketch, "E1050", {"start": v(6.6, -1.93) * mm, "end": v(6.62, -1.94) * mm});
            skLineSegment(sketch, "E1051", {"start": v(6.62, -1.94) * mm, "end": v(6.63, -1.95) * mm});
            skLineSegment(sketch, "E1052", {"start": v(6.63, -1.95) * mm, "end": v(6.64, -1.95) * mm});
            skLineSegment(sketch, "E1053", {"start": v(6.64, -1.95) * mm, "end": v(6.65, -1.96) * mm});
            skLineSegment(sketch, "E1054", {"start": v(6.65, -1.96) * mm, "end": v(6.66, -1.96) * mm});
            skLineSegment(sketch, "E1055", {"start": v(6.66, -1.96) * mm, "end": v(6.67, -1.97) * mm});
            skLineSegment(sketch, "E1056", {"start": v(6.67, -1.97) * mm, "end": v(6.69, -1.98) * mm});
            skLineSegment(sketch, "E1057", {"start": v(6.69, -1.98) * mm, "end": v(6.7, -1.99) * mm});
            skLineSegment(sketch, "E1058", {"start": v(6.7, -1.99) * mm, "end": v(6.71, -2) * mm});
            skLineSegment(sketch, "E1059", {"start": v(6.71, -2) * mm, "end": v(6.73, -2) * mm});
            skLineSegment(sketch, "E1060", {"start": v(6.73, -2) * mm, "end": v(6.74, -2.01) * mm});
            skLineSegment(sketch, "E1061", {"start": v(6.74, -2.01) * mm, "end": v(6.75, -2.02) * mm});
            skLineSegment(sketch, "E1062", {"start": v(6.75, -2.02) * mm, "end": v(6.77, -2.03) * mm});
            skLineSegment(sketch, "E1063", {"start": v(6.77, -2.03) * mm, "end": v(6.78, -2.04) * mm});
            skLineSegment(sketch, "E1064", {"start": v(6.78, -2.04) * mm, "end": v(6.8, -2.05) * mm});
            skLineSegment(sketch, "E1065", {"start": v(6.8, -2.05) * mm, "end": v(6.82, -2.06) * mm});
            skLineSegment(sketch, "E1066", {"start": v(6.82, -2.06) * mm, "end": v(6.83, -2.08) * mm});
            skLineSegment(sketch, "E1067", {"start": v(6.83, -2.08) * mm, "end": v(6.85, -2.09) * mm});
            skLineSegment(sketch, "E1068", {"start": v(6.85, -2.09) * mm, "end": v(6.87, -2.1) * mm});
            skLineSegment(sketch, "E1069", {"start": v(6.87, -2.1) * mm, "end": v(6.88, -2.11) * mm});
            skLineSegment(sketch, "E1070", {"start": v(6.88, -2.11) * mm, "end": v(6.9, -2.13) * mm});
            skLineSegment(sketch, "E1071", {"start": v(6.9, -2.13) * mm, "end": v(6.92, -2.14) * mm});
            skLineSegment(sketch, "E1072", {"start": v(6.92, -2.14) * mm, "end": v(6.94, -2.15) * mm});
            skLineSegment(sketch, "E1073", {"start": v(6.94, -2.15) * mm, "end": v(6.96, -2.17) * mm});
            skLineSegment(sketch, "E1074", {"start": v(6.96, -2.17) * mm, "end": v(6.97, -2.18) * mm});
            skLineSegment(sketch, "E1075", {"start": v(6.97, -2.18) * mm, "end": v(7, -2.2) * mm});
            skLineSegment(sketch, "E1076", {"start": v(7, -2.2) * mm, "end": v(7.01, -2.22) * mm});
            skLineSegment(sketch, "E1077", {"start": v(7.01, -2.22) * mm, "end": v(7.03, -2.23) * mm});
            skLineSegment(sketch, "E1078", {"start": v(7.03, -2.23) * mm, "end": v(7.05, -2.25) * mm});
            skLineSegment(sketch, "E1079", {"start": v(7.05, -2.25) * mm, "end": v(7.07, -2.27) * mm});
            skLineSegment(sketch, "E1080", {"start": v(7.07, -2.27) * mm, "end": v(7.1, -2.29) * mm});
            skLineSegment(sketch, "E1081", {"start": v(7.1, -2.29) * mm, "end": v(7.11, -2.3) * mm});
            skLineSegment(sketch, "E1082", {"start": v(7.11, -2.3) * mm, "end": v(7.13, -2.33) * mm});
            skLineSegment(sketch, "E1083", {"start": v(7.13, -2.33) * mm, "end": v(7.15, -2.35) * mm});
            skLineSegment(sketch, "E1084", {"start": v(7.15, -2.35) * mm, "end": v(7.18, -2.37) * mm});
            skLineSegment(sketch, "E1085", {"start": v(7.18, -2.37) * mm, "end": v(7.2, -2.39) * mm});
            skLineSegment(sketch, "E1086", {"start": v(7.2, -2.39) * mm, "end": v(7.22, -2.41) * mm});
            skLineSegment(sketch, "E1087", {"start": v(7.22, -2.41) * mm, "end": v(7.24, -2.43) * mm});
            skLineSegment(sketch, "E1088", {"start": v(7.24, -2.43) * mm, "end": v(7.26, -2.46) * mm});
            skLineSegment(sketch, "E1089", {"start": v(7.26, -2.46) * mm, "end": v(7.28, -2.48) * mm});
            skLineSegment(sketch, "E1090", {"start": v(7.28, -2.48) * mm, "end": v(7.3, -2.5) * mm});
            skLineSegment(sketch, "E1091", {"start": v(7.3, -2.5) * mm, "end": v(7.33, -2.53) * mm});
            skLineSegment(sketch, "E1092", {"start": v(6.26, -2.78) * mm, "end": v(6.27, -2.78) * mm});
            skLineSegment(sketch, "E1093", {"start": v(6.27, -2.78) * mm, "end": v(6.27, -2.77) * mm});
            skLineSegment(sketch, "E1094", {"start": v(6.27, -2.77) * mm, "end": v(6.28, -2.77) * mm});
            skLineSegment(sketch, "E1095", {"start": v(6.28, -2.77) * mm, "end": v(6.29, -2.77) * mm});
            skLineSegment(sketch, "E1096", {"start": v(6.29, -2.77) * mm, "end": v(6.3, -2.77) * mm});
            skLineSegment(sketch, "E1097", {"start": v(6.3, -2.77) * mm, "end": v(6.31, -2.77) * mm});
            skLineSegment(sketch, "E1098", {"start": v(6.31, -2.77) * mm, "end": v(6.33, -2.77) * mm});
            skLineSegment(sketch, "E1099", {"start": v(6.33, -2.77) * mm, "end": v(6.34, -2.77) * mm});
            skLineSegment(sketch, "E1100", {"start": v(6.34, -2.77) * mm, "end": v(6.35, -2.77) * mm});
            skLineSegment(sketch, "E1101", {"start": v(6.35, -2.77) * mm, "end": v(6.37, -2.78) * mm});
            skLineSegment(sketch, "E1102", {"start": v(6.37, -2.78) * mm, "end": v(6.38, -2.78) * mm});
            skLineSegment(sketch, "E1103", {"start": v(6.38, -2.78) * mm, "end": v(6.4, -2.78) * mm});
            skLineSegment(sketch, "E1104", {"start": v(6.4, -2.78) * mm, "end": v(6.4, -2.78) * mm});
            skLineSegment(sketch, "E1105", {"start": v(6.4, -2.78) * mm, "end": v(6.42, -2.79) * mm});
            skLineSegment(sketch, "E1106", {"start": v(6.42, -2.79) * mm, "end": v(6.44, -2.79) * mm});
            skLineSegment(sketch, "E1107", {"start": v(6.44, -2.79) * mm, "end": v(6.46, -2.8) * mm});
            skLineSegment(sketch, "E1108", {"start": v(6.46, -2.8) * mm, "end": v(6.47, -2.8) * mm});
            skLineSegment(sketch, "E1109", {"start": v(6.47, -2.8) * mm, "end": v(6.5, -2.8) * mm});
            skLineSegment(sketch, "E1110", {"start": v(6.5, -2.8) * mm, "end": v(6.51, -2.8) * mm});
            skLineSegment(sketch, "E1111", {"start": v(6.51, -2.8) * mm, "end": v(6.53, -2.8) * mm});
            skLineSegment(sketch, "E1112", {"start": v(6.53, -2.8) * mm, "end": v(6.55, -2.8) * mm});
            skLineSegment(sketch, "E1113", {"start": v(6.55, -2.8) * mm, "end": v(6.57, -2.8) * mm});
            skLineSegment(sketch, "E1114", {"start": v(6.57, -2.8) * mm, "end": v(6.59, -2.8) * mm});
            skLineSegment(sketch, "E1115", {"start": v(6.59, -2.8) * mm, "end": v(6.6, -2.8) * mm});
            skLineSegment(sketch, "E1116", {"start": v(6.6, -2.8) * mm, "end": v(6.63, -2.8) * mm});
            skLineSegment(sketch, "E1117", {"start": v(6.63, -2.8) * mm, "end": v(6.65, -2.8) * mm});
            skLineSegment(sketch, "E1118", {"start": v(6.65, -2.8) * mm, "end": v(6.68, -2.8) * mm});
            skLineSegment(sketch, "E1119", {"start": v(6.68, -2.8) * mm, "end": v(6.7, -2.8) * mm});
            skLineSegment(sketch, "E1120", {"start": v(6.7, -2.8) * mm, "end": v(6.72, -2.8) * mm});
            skLineSegment(sketch, "E1121", {"start": v(6.72, -2.8) * mm, "end": v(6.75, -2.8) * mm});
            skLineSegment(sketch, "E1122", {"start": v(6.75, -2.8) * mm, "end": v(6.77, -2.8) * mm});
            skLineSegment(sketch, "E1123", {"start": v(6.77, -2.8) * mm, "end": v(6.8, -2.8) * mm});
            skLineSegment(sketch, "E1124", {"start": v(6.8, -2.8) * mm, "end": v(6.82, -2.8) * mm});
            skLineSegment(sketch, "E1125", {"start": v(6.82, -2.8) * mm, "end": v(6.85, -2.8) * mm});
            skLineSegment(sketch, "E1126", {"start": v(6.85, -2.8) * mm, "end": v(6.88, -2.8) * mm});
            skLineSegment(sketch, "E1127", {"start": v(6.88, -2.8) * mm, "end": v(6.9, -2.8) * mm});
            skLineSegment(sketch, "E1128", {"start": v(6.9, -2.8) * mm, "end": v(6.93, -2.8) * mm});
            skLineSegment(sketch, "E1129", {"start": v(6.93, -2.8) * mm, "end": v(6.96, -2.8) * mm});
            skLineSegment(sketch, "E1130", {"start": v(6.96, -2.8) * mm, "end": v(6.99, -2.8) * mm});
            skLineSegment(sketch, "E1131", {"start": v(6.99, -2.8) * mm, "end": v(7.02, -2.8) * mm});
            skLineSegment(sketch, "E1132", {"start": v(7.02, -2.8) * mm, "end": v(7.05, -2.8) * mm});
            skLineSegment(sketch, "E1133", {"start": v(7.05, -2.8) * mm, "end": v(7.08, -2.8) * mm});
            skLineSegment(sketch, "E1134", {"start": v(7.08, -2.8) * mm, "end": v(7.1, -2.8) * mm});
            skLineSegment(sketch, "E1135", {"start": v(7.1, -2.8) * mm, "end": v(7.14, -2.79) * mm});
            skLineSegment(sketch, "E1136", {"start": v(7.14, -2.79) * mm, "end": v(7.17, -2.78) * mm});
            skLineSegment(sketch, "E1137", {"start": v(7.17, -2.78) * mm, "end": v(7.2, -2.78) * mm});
            skLineSegment(sketch, "E1138", {"start": v(7.2, -2.78) * mm, "end": v(7.24, -2.77) * mm});
            skArc(sketch, "E1139", {"start": v(7.24, -2.77) * mm, "mid": v(7.28, -2.65) * mm, "end": v(7.33, -2.53) * mm});
            skLineSegment(sketch, "E1140", {"start": v(6.16, -3) * mm, "end": v(6.15, -3.02) * mm});
            skLineSegment(sketch, "E1141", {"start": v(6.15, -3.02) * mm, "end": v(6.15, -3.02) * mm});
            skLineSegment(sketch, "E1142", {"start": v(6.15, -3.02) * mm, "end": v(6.16, -3.03) * mm});
            skLineSegment(sketch, "E1143", {"start": v(6.16, -3.03) * mm, "end": v(6.16, -3.04) * mm});
            skLineSegment(sketch, "E1144", {"start": v(6.16, -3.04) * mm, "end": v(6.17, -3.05) * mm});
            skLineSegment(sketch, "E1145", {"start": v(6.17, -3.05) * mm, "end": v(6.18, -3.06) * mm});
            skLineSegment(sketch, "E1146", {"start": v(6.18, -3.06) * mm, "end": v(6.19, -3.07) * mm});
            skLineSegment(sketch, "E1147", {"start": v(6.19, -3.07) * mm, "end": v(6.2, -3.07) * mm});
            skLineSegment(sketch, "E1148", {"start": v(6.2, -3.07) * mm, "end": v(6.2, -3.08) * mm});
            skLineSegment(sketch, "E1149", {"start": v(6.2, -3.08) * mm, "end": v(6.22, -3.1) * mm});
            skLineSegment(sketch, "E1150", {"start": v(6.22, -3.1) * mm, "end": v(6.23, -3.1) * mm});
            skLineSegment(sketch, "E1151", {"start": v(6.23, -3.1) * mm, "end": v(6.24, -3.11) * mm});
            skLineSegment(sketch, "E1152", {"start": v(6.24, -3.11) * mm, "end": v(6.25, -3.12) * mm});
            skLineSegment(sketch, "E1153", {"start": v(6.25, -3.12) * mm, "end": v(6.26, -3.13) * mm});
            skLineSegment(sketch, "E1154", {"start": v(6.26, -3.13) * mm, "end": v(6.28, -3.14) * mm});
            skLineSegment(sketch, "E1155", {"start": v(6.28, -3.14) * mm, "end": v(6.29, -3.15) * mm});
            skLineSegment(sketch, "E1156", {"start": v(6.29, -3.15) * mm, "end": v(6.3, -3.16) * mm});
            skLineSegment(sketch, "E1157", {"start": v(6.3, -3.16) * mm, "end": v(6.31, -3.18) * mm});
            skLineSegment(sketch, "E1158", {"start": v(6.31, -3.18) * mm, "end": v(6.33, -3.19) * mm});
            skLineSegment(sketch, "E1159", {"start": v(6.33, -3.19) * mm, "end": v(6.34, -3.2) * mm});
            skLineSegment(sketch, "E1160", {"start": v(6.34, -3.2) * mm, "end": v(6.35, -3.22) * mm});
            skLineSegment(sketch, "E1161", {"start": v(6.35, -3.22) * mm, "end": v(6.37, -3.23) * mm});
            skLineSegment(sketch, "E1162", {"start": v(6.37, -3.23) * mm, "end": v(6.38, -3.24) * mm});
            skLineSegment(sketch, "E1163", {"start": v(6.38, -3.24) * mm, "end": v(6.4, -3.26) * mm});
            skLineSegment(sketch, "E1164", {"start": v(6.4, -3.26) * mm, "end": v(6.41, -3.28) * mm});
            skLineSegment(sketch, "E1165", {"start": v(6.41, -3.28) * mm, "end": v(6.43, -3.3) * mm});
            skLineSegment(sketch, "E1166", {"start": v(6.43, -3.3) * mm, "end": v(6.44, -3.3) * mm});
            skLineSegment(sketch, "E1167", {"start": v(6.44, -3.3) * mm, "end": v(6.46, -3.33) * mm});
            skLineSegment(sketch, "E1168", {"start": v(6.46, -3.33) * mm, "end": v(6.47, -3.34) * mm});
            skLineSegment(sketch, "E1169", {"start": v(6.47, -3.34) * mm, "end": v(6.49, -3.36) * mm});
            skLineSegment(sketch, "E1170", {"start": v(6.49, -3.36) * mm, "end": v(6.5, -3.38) * mm});
            skLineSegment(sketch, "E1171", {"start": v(6.5, -3.38) * mm, "end": v(6.52, -3.4) * mm});
            skLineSegment(sketch, "E1172", {"start": v(6.52, -3.4) * mm, "end": v(6.54, -3.42) * mm});
            skLineSegment(sketch, "E1173", {"start": v(6.54, -3.42) * mm, "end": v(6.55, -3.44) * mm});
            skLineSegment(sketch, "E1174", {"start": v(6.55, -3.44) * mm, "end": v(6.57, -3.46) * mm});
            skLineSegment(sketch, "E1175", {"start": v(6.57, -3.46) * mm, "end": v(6.59, -3.48) * mm});
            skLineSegment(sketch, "E1176", {"start": v(6.59, -3.48) * mm, "end": v(6.6, -3.5) * mm});
            skLineSegment(sketch, "E1177", {"start": v(6.6, -3.5) * mm, "end": v(6.62, -3.53) * mm});
            skLineSegment(sketch, "E1178", {"start": v(6.62, -3.53) * mm, "end": v(6.64, -3.55) * mm});
            skLineSegment(sketch, "E1179", {"start": v(6.64, -3.55) * mm, "end": v(6.66, -3.58) * mm});
            skLineSegment(sketch, "E1180", {"start": v(6.66, -3.58) * mm, "end": v(6.67, -3.6) * mm});
            skLineSegment(sketch, "E1181", {"start": v(6.67, -3.6) * mm, "end": v(6.7, -3.63) * mm});
            skLineSegment(sketch, "E1182", {"start": v(6.7, -3.63) * mm, "end": v(6.7, -3.65) * mm});
            skLineSegment(sketch, "E1183", {"start": v(6.7, -3.65) * mm, "end": v(6.73, -3.68) * mm});
            skLineSegment(sketch, "E1184", {"start": v(6.73, -3.68) * mm, "end": v(6.74, -3.7) * mm});
            skLineSegment(sketch, "E1185", {"start": v(6.74, -3.7) * mm, "end": v(6.76, -3.73) * mm});
            skLineSegment(sketch, "E1186", {"start": v(6.76, -3.73) * mm, "end": v(6.78, -3.76) * mm});
            skLineSegment(sketch, "E1187", {"start": v(5.68, -3.83) * mm, "end": v(5.69, -3.82) * mm});
            skLineSegment(sketch, "E1188", {"start": v(5.69, -3.82) * mm, "end": v(5.7, -3.82) * mm});
            skLineSegment(sketch, "E1189", {"start": v(5.7, -3.82) * mm, "end": v(5.7, -3.82) * mm});
            skLineSegment(sketch, "E1190", {"start": v(5.7, -3.82) * mm, "end": v(5.71, -3.82) * mm});
            skLineSegment(sketch, "E1191", {"start": v(5.71, -3.82) * mm, "end": v(5.72, -3.82) * mm});
            skLineSegment(sketch, "E1192", {"start": v(5.72, -3.82) * mm, "end": v(5.74, -3.82) * mm});
            skLineSegment(sketch, "E1193", {"start": v(5.74, -3.82) * mm, "end": v(5.75, -3.83) * mm});
            skLineSegment(sketch, "E1194", {"start": v(5.75, -3.83) * mm, "end": v(5.76, -3.83) * mm});
            skLineSegment(sketch, "E1195", {"start": v(5.76, -3.83) * mm, "end": v(5.77, -3.83) * mm});
            skLineSegment(sketch, "E1196", {"start": v(5.77, -3.83) * mm, "end": v(5.79, -3.84) * mm});
            skLineSegment(sketch, "E1197", {"start": v(5.79, -3.84) * mm, "end": v(5.8, -3.84) * mm});
            skLineSegment(sketch, "E1198", {"start": v(5.8, -3.84) * mm, "end": v(5.81, -3.85) * mm});
            skLineSegment(sketch, "E1199", {"start": v(5.81, -3.85) * mm, "end": v(5.83, -3.85) * mm});
            skLineSegment(sketch, "E1200", {"start": v(5.83, -3.85) * mm, "end": v(5.84, -3.86) * mm});
            skLineSegment(sketch, "E1201", {"start": v(5.84, -3.86) * mm, "end": v(5.86, -3.86) * mm});
            skLineSegment(sketch, "E1202", {"start": v(5.86, -3.86) * mm, "end": v(5.87, -3.87) * mm});
            skLineSegment(sketch, "E1203", {"start": v(5.87, -3.87) * mm, "end": v(5.9, -3.87) * mm});
            skLineSegment(sketch, "E1204", {"start": v(5.9, -3.87) * mm, "end": v(5.9, -3.88) * mm});
            skLineSegment(sketch, "E1205", {"start": v(5.9, -3.88) * mm, "end": v(5.93, -3.89) * mm});
            skLineSegment(sketch, "E1206", {"start": v(5.93, -3.89) * mm, "end": v(5.94, -3.9) * mm});
            skLineSegment(sketch, "E1207", {"start": v(5.94, -3.9) * mm, "end": v(5.96, -3.9) * mm});
            skLineSegment(sketch, "E1208", {"start": v(5.96, -3.9) * mm, "end": v(5.98, -3.9) * mm});
            skLineSegment(sketch, "E1209", {"start": v(5.98, -3.9) * mm, "end": v(6, -3.9) * mm});
            skLineSegment(sketch, "E1210", {"start": v(6, -3.9) * mm, "end": v(6.02, -3.91) * mm});
            skLineSegment(sketch, "E1211", {"start": v(6.02, -3.91) * mm, "end": v(6.04, -3.92) * mm});
            skLineSegment(sketch, "E1212", {"start": v(6.04, -3.92) * mm, "end": v(6.06, -3.92) * mm});
            skLineSegment(sketch, "E1213", {"start": v(6.06, -3.92) * mm, "end": v(6.09, -3.92) * mm});
            skLineSegment(sketch, "E1214", {"start": v(6.09, -3.92) * mm, "end": v(6.1, -3.93) * mm});
            skLineSegment(sketch, "E1215", {"start": v(6.1, -3.93) * mm, "end": v(6.13, -3.93) * mm});
            skLineSegment(sketch, "E1216", {"start": v(6.13, -3.93) * mm, "end": v(6.16, -3.94) * mm});
            skLineSegment(sketch, "E1217", {"start": v(6.16, -3.94) * mm, "end": v(6.18, -3.94) * mm});
            skLineSegment(sketch, "E1218", {"start": v(6.18, -3.94) * mm, "end": v(6.2, -3.95) * mm});
            skLineSegment(sketch, "E1219", {"start": v(6.2, -3.95) * mm, "end": v(6.23, -3.95) * mm});
            skLineSegment(sketch, "E1220", {"start": v(6.23, -3.95) * mm, "end": v(6.26, -3.96) * mm});
            skLineSegment(sketch, "E1221", {"start": v(6.26, -3.96) * mm, "end": v(6.28, -3.96) * mm});
            skLineSegment(sketch, "E1222", {"start": v(6.28, -3.96) * mm, "end": v(6.31, -3.96) * mm});
            skLineSegment(sketch, "E1223", {"start": v(6.31, -3.96) * mm, "end": v(6.34, -3.97) * mm});
            skLineSegment(sketch, "E1224", {"start": v(6.34, -3.97) * mm, "end": v(6.37, -3.97) * mm});
            skLineSegment(sketch, "E1225", {"start": v(6.37, -3.97) * mm, "end": v(6.4, -3.97) * mm});
            skLineSegment(sketch, "E1226", {"start": v(6.4, -3.97) * mm, "end": v(6.43, -3.98) * mm});
            skLineSegment(sketch, "E1227", {"start": v(6.43, -3.98) * mm, "end": v(6.46, -3.98) * mm});
            skLineSegment(sketch, "E1228", {"start": v(6.46, -3.98) * mm, "end": v(6.49, -3.98) * mm});
            skLineSegment(sketch, "E1229", {"start": v(6.49, -3.98) * mm, "end": v(6.52, -3.98) * mm});
            skLineSegment(sketch, "E1230", {"start": v(6.52, -3.98) * mm, "end": v(6.55, -3.98) * mm});
            skLineSegment(sketch, "E1231", {"start": v(6.55, -3.98) * mm, "end": v(6.58, -3.99) * mm});
            skLineSegment(sketch, "E1232", {"start": v(6.58, -3.99) * mm, "end": v(6.61, -3.99) * mm});
            skLineSegment(sketch, "E1233", {"start": v(6.61, -3.99) * mm, "end": v(6.65, -3.99) * mm});
            skArc(sketch, "E1234", {"start": v(6.65, -3.99) * mm, "mid": v(6.71, -3.88) * mm, "end": v(6.78, -3.76) * mm});
            skLineSegment(sketch, "E1235", {"start": v(5.54, -4.03) * mm, "end": v(5.54, -4.04) * mm});
            skLineSegment(sketch, "E1236", {"start": v(5.54, -4.04) * mm, "end": v(5.54, -4.04) * mm});
            skLineSegment(sketch, "E1237", {"start": v(5.54, -4.04) * mm, "end": v(5.54, -4.05) * mm});
            skLineSegment(sketch, "E1238", {"start": v(5.54, -4.05) * mm, "end": v(5.54, -4.06) * mm});
            skLineSegment(sketch, "E1239", {"start": v(5.54, -4.06) * mm, "end": v(5.55, -4.07) * mm});
            skLineSegment(sketch, "E1240", {"start": v(5.55, -4.07) * mm, "end": v(5.55, -4.08) * mm});
            skLineSegment(sketch, "E1241", {"start": v(5.55, -4.08) * mm, "end": v(5.56, -4.1) * mm});
            skLineSegment(sketch, "E1242", {"start": v(5.56, -4.1) * mm, "end": v(5.57, -4.1) * mm});
            skLineSegment(sketch, "E1243", {"start": v(5.57, -4.1) * mm, "end": v(5.58, -4.11) * mm});
            skLineSegment(sketch, "E1244", {"start": v(5.58, -4.11) * mm, "end": v(5.59, -4.12) * mm});
            skLineSegment(sketch, "E1245", {"start": v(5.59, -4.12) * mm, "end": v(5.6, -4.14) * mm});
            skLineSegment(sketch, "E1246", {"start": v(5.6, -4.14) * mm, "end": v(5.6, -4.15) * mm});
            skLineSegment(sketch, "E1247", {"start": v(5.6, -4.15) * mm, "end": v(5.62, -4.16) * mm});
            skLineSegment(sketch, "E1248", {"start": v(5.62, -4.16) * mm, "end": v(5.63, -4.17) * mm});
            skLineSegment(sketch, "E1249", {"start": v(5.63, -4.17) * mm, "end": v(5.64, -4.18) * mm});
            skLineSegment(sketch, "E1250", {"start": v(5.64, -4.18) * mm, "end": v(5.65, -4.2) * mm});
            skLineSegment(sketch, "E1251", {"start": v(5.65, -4.2) * mm, "end": v(5.66, -4.21) * mm});
            skLineSegment(sketch, "E1252", {"start": v(5.66, -4.21) * mm, "end": v(5.67, -4.22) * mm});
            skLineSegment(sketch, "E1253", {"start": v(5.67, -4.22) * mm, "end": v(5.68, -4.24) * mm});
            skLineSegment(sketch, "E1254", {"start": v(5.68, -4.24) * mm, "end": v(5.69, -4.25) * mm});
            skLineSegment(sketch, "E1255", {"start": v(5.69, -4.25) * mm, "end": v(5.7, -4.27) * mm});
            skLineSegment(sketch, "E1256", {"start": v(5.7, -4.27) * mm, "end": v(5.71, -4.29) * mm});
            skLineSegment(sketch, "E1257", {"start": v(5.71, -4.29) * mm, "end": v(5.72, -4.3) * mm});
            skLineSegment(sketch, "E1258", {"start": v(5.72, -4.3) * mm, "end": v(5.73, -4.32) * mm});
            skLineSegment(sketch, "E1259", {"start": v(5.73, -4.32) * mm, "end": v(5.75, -4.34) * mm});
            skLineSegment(sketch, "E1260", {"start": v(5.75, -4.34) * mm, "end": v(5.76, -4.36) * mm});
            skLineSegment(sketch, "E1261", {"start": v(5.76, -4.36) * mm, "end": v(5.77, -4.38) * mm});
            skLineSegment(sketch, "E1262", {"start": v(5.77, -4.38) * mm, "end": v(5.78, -4.4) * mm});
            skLineSegment(sketch, "E1263", {"start": v(5.78, -4.4) * mm, "end": v(5.8, -4.42) * mm});
            skLineSegment(sketch, "E1264", {"start": v(5.8, -4.42) * mm, "end": v(5.8, -4.44) * mm});
            skLineSegment(sketch, "E1265", {"start": v(5.8, -4.44) * mm, "end": v(5.82, -4.46) * mm});
            skLineSegment(sketch, "E1266", {"start": v(5.82, -4.46) * mm, "end": v(5.83, -4.48) * mm});
            skLineSegment(sketch, "E1267", {"start": v(5.83, -4.48) * mm, "end": v(5.84, -4.5) * mm});
            skLineSegment(sketch, "E1268", {"start": v(5.84, -4.5) * mm, "end": v(5.86, -4.53) * mm});
            skLineSegment(sketch, "E1269", {"start": v(5.86, -4.53) * mm, "end": v(5.87, -4.55) * mm});
            skLineSegment(sketch, "E1270", {"start": v(5.87, -4.55) * mm, "end": v(5.88, -4.58) * mm});
            skLineSegment(sketch, "E1271", {"start": v(5.88, -4.58) * mm, "end": v(5.9, -4.6) * mm});
            skLineSegment(sketch, "E1272", {"start": v(5.9, -4.6) * mm, "end": v(5.9, -4.63) * mm});
            skLineSegment(sketch, "E1273", {"start": v(5.9, -4.63) * mm, "end": v(5.92, -4.65) * mm});
            skLineSegment(sketch, "E1274", {"start": v(5.92, -4.65) * mm, "end": v(5.93, -4.68) * mm});
            skLineSegment(sketch, "E1275", {"start": v(5.93, -4.68) * mm, "end": v(5.95, -4.7) * mm});
            skLineSegment(sketch, "E1276", {"start": v(5.95, -4.7) * mm, "end": v(5.96, -4.73) * mm});
            skLineSegment(sketch, "E1277", {"start": v(5.96, -4.73) * mm, "end": v(5.97, -4.76) * mm});
            skLineSegment(sketch, "E1278", {"start": v(5.97, -4.76) * mm, "end": v(5.98, -4.8) * mm});
            skLineSegment(sketch, "E1279", {"start": v(5.98, -4.8) * mm, "end": v(6, -4.82) * mm});
            skLineSegment(sketch, "E1280", {"start": v(6, -4.82) * mm, "end": v(6, -4.85) * mm});
            skLineSegment(sketch, "E1281", {"start": v(6, -4.85) * mm, "end": v(6.02, -4.88) * mm});
            skLineSegment(sketch, "E1282", {"start": v(4.93, -4.76) * mm, "end": v(4.94, -4.75) * mm});
            skLineSegment(sketch, "E1283", {"start": v(4.94, -4.75) * mm, "end": v(4.94, -4.75) * mm});
            skLineSegment(sketch, "E1284", {"start": v(4.94, -4.75) * mm, "end": v(4.95, -4.75) * mm});
            skLineSegment(sketch, "E1285", {"start": v(4.95, -4.75) * mm, "end": v(4.96, -4.75) * mm});
            skLineSegment(sketch, "E1286", {"start": v(4.96, -4.75) * mm, "end": v(4.97, -4.75) * mm});
            skLineSegment(sketch, "E1287", {"start": v(4.97, -4.75) * mm, "end": v(4.99, -4.76) * mm});
            skLineSegment(sketch, "E1288", {"start": v(4.99, -4.76) * mm, "end": v(5, -4.77) * mm});
            skLineSegment(sketch, "E1289", {"start": v(5, -4.77) * mm, "end": v(5, -4.77) * mm});
            skLineSegment(sketch, "E1290", {"start": v(5, -4.77) * mm, "end": v(5.02, -4.78) * mm});
            skLineSegment(sketch, "E1291", {"start": v(5.02, -4.78) * mm, "end": v(5.03, -4.79) * mm});
            skLineSegment(sketch, "E1292", {"start": v(5.03, -4.79) * mm, "end": v(5.04, -4.8) * mm});
            skLineSegment(sketch, "E1293", {"start": v(5.04, -4.8) * mm, "end": v(5.06, -4.8) * mm});
            skLineSegment(sketch, "E1294", {"start": v(5.06, -4.8) * mm, "end": v(5.07, -4.8) * mm});
            skLineSegment(sketch, "E1295", {"start": v(5.07, -4.8) * mm, "end": v(5.08, -4.82) * mm});
            skLineSegment(sketch, "E1296", {"start": v(5.08, -4.82) * mm, "end": v(5.1, -4.82) * mm});
            skLineSegment(sketch, "E1297", {"start": v(5.1, -4.82) * mm, "end": v(5.11, -4.83) * mm});
            skLineSegment(sketch, "E1298", {"start": v(5.11, -4.83) * mm, "end": v(5.13, -4.84) * mm});
            skLineSegment(sketch, "E1299", {"start": v(5.13, -4.84) * mm, "end": v(5.14, -4.85) * mm});
            skLineSegment(sketch, "E1300", {"start": v(5.14, -4.85) * mm, "end": v(5.16, -4.85) * mm});
            skLineSegment(sketch, "E1301", {"start": v(5.16, -4.85) * mm, "end": v(5.18, -4.86) * mm});
            skLineSegment(sketch, "E1302", {"start": v(5.18, -4.86) * mm, "end": v(5.2, -4.87) * mm});
            skLineSegment(sketch, "E1303", {"start": v(5.2, -4.87) * mm, "end": v(5.21, -4.88) * mm});
            skLineSegment(sketch, "E1304", {"start": v(5.21, -4.88) * mm, "end": v(5.23, -4.89) * mm});
            skLineSegment(sketch, "E1305", {"start": v(5.23, -4.89) * mm, "end": v(5.25, -4.9) * mm});
            skLineSegment(sketch, "E1306", {"start": v(5.25, -4.9) * mm, "end": v(5.27, -4.9) * mm});
            skLineSegment(sketch, "E1307", {"start": v(5.27, -4.9) * mm, "end": v(5.3, -4.91) * mm});
            skLineSegment(sketch, "E1308", {"start": v(5.3, -4.91) * mm, "end": v(5.31, -4.92) * mm});
            skLineSegment(sketch, "E1309", {"start": v(5.31, -4.92) * mm, "end": v(5.33, -4.93) * mm});
            skLineSegment(sketch, "E1310", {"start": v(5.33, -4.93) * mm, "end": v(5.36, -4.94) * mm});
            skLineSegment(sketch, "E1311", {"start": v(5.36, -4.94) * mm, "end": v(5.38, -4.95) * mm});
            skLineSegment(sketch, "E1312", {"start": v(5.38, -4.95) * mm, "end": v(5.4, -4.96) * mm});
            skLineSegment(sketch, "E1313", {"start": v(5.4, -4.96) * mm, "end": v(5.43, -4.96) * mm});
            skLineSegment(sketch, "E1314", {"start": v(5.43, -4.96) * mm, "end": v(5.45, -4.97) * mm});
            skLineSegment(sketch, "E1315", {"start": v(5.45, -4.97) * mm, "end": v(5.48, -4.98) * mm});
            skLineSegment(sketch, "E1316", {"start": v(5.48, -4.98) * mm, "end": v(5.5, -5) * mm});
            skLineSegment(sketch, "E1317", {"start": v(5.5, -5) * mm, "end": v(5.53, -5) * mm});
            skLineSegment(sketch, "E1318", {"start": v(5.53, -5) * mm, "end": v(5.55, -5) * mm});
            skLineSegment(sketch, "E1319", {"start": v(5.55, -5) * mm, "end": v(5.58, -5.01) * mm});
            skLineSegment(sketch, "E1320", {"start": v(5.58, -5.01) * mm, "end": v(5.6, -5.02) * mm});
            skLineSegment(sketch, "E1321", {"start": v(5.6, -5.02) * mm, "end": v(5.64, -5.03) * mm});
            skLineSegment(sketch, "E1322", {"start": v(5.64, -5.03) * mm, "end": v(5.67, -5.04) * mm});
            skLineSegment(sketch, "E1323", {"start": v(5.67, -5.04) * mm, "end": v(5.7, -5.05) * mm});
            skLineSegment(sketch, "E1324", {"start": v(5.7, -5.05) * mm, "end": v(5.73, -5.05) * mm});
            skLineSegment(sketch, "E1325", {"start": v(5.73, -5.05) * mm, "end": v(5.76, -5.06) * mm});
            skLineSegment(sketch, "E1326", {"start": v(5.76, -5.06) * mm, "end": v(5.79, -5.07) * mm});
            skLineSegment(sketch, "E1327", {"start": v(5.79, -5.07) * mm, "end": v(5.82, -5.08) * mm});
            skLineSegment(sketch, "E1328", {"start": v(5.82, -5.08) * mm, "end": v(5.85, -5.08) * mm});
            skArc(sketch, "E1329", {"start": v(5.85, -5.08) * mm, "mid": v(5.94, -4.98) * mm, "end": v(6.02, -4.88) * mm});
            skLineSegment(sketch, "E1330", {"start": v(4.76, -4.93) * mm, "end": v(4.75, -4.94) * mm});
            skLineSegment(sketch, "E1331", {"start": v(4.75, -4.94) * mm, "end": v(4.75, -4.94) * mm});
            skLineSegment(sketch, "E1332", {"start": v(4.75, -4.94) * mm, "end": v(4.75, -4.95) * mm});
            skLineSegment(sketch, "E1333", {"start": v(4.75, -4.95) * mm, "end": v(4.75, -4.96) * mm});
            skLineSegment(sketch, "E1334", {"start": v(4.75, -4.96) * mm, "end": v(4.75, -4.97) * mm});
            skLineSegment(sketch, "E1335", {"start": v(4.75, -4.97) * mm, "end": v(4.76, -4.99) * mm});
            skLineSegment(sketch, "E1336", {"start": v(4.76, -4.99) * mm, "end": v(4.77, -5) * mm});
            skLineSegment(sketch, "E1337", {"start": v(4.77, -5) * mm, "end": v(4.77, -5) * mm});
            skLineSegment(sketch, "E1338", {"start": v(4.77, -5) * mm, "end": v(4.78, -5.02) * mm});
            skLineSegment(sketch, "E1339", {"start": v(4.78, -5.02) * mm, "end": v(4.79, -5.03) * mm});
            skLineSegment(sketch, "E1340", {"start": v(4.79, -5.03) * mm, "end": v(4.8, -5.04) * mm});
            skLineSegment(sketch, "E1341", {"start": v(4.8, -5.04) * mm, "end": v(4.8, -5.06) * mm});
            skLineSegment(sketch, "E1342", {"start": v(4.8, -5.06) * mm, "end": v(4.8, -5.07) * mm});
            skLineSegment(sketch, "E1343", {"start": v(4.8, -5.07) * mm, "end": v(4.82, -5.08) * mm});
            skLineSegment(sketch, "E1344", {"start": v(4.82, -5.08) * mm, "end": v(4.82, -5.1) * mm});
            skLineSegment(sketch, "E1345", {"start": v(4.82, -5.1) * mm, "end": v(4.83, -5.11) * mm});
            skLineSegment(sketch, "E1346", {"start": v(4.83, -5.11) * mm, "end": v(4.84, -5.13) * mm});
            skLineSegment(sketch, "E1347", {"start": v(4.84, -5.13) * mm, "end": v(4.85, -5.14) * mm});
            skLineSegment(sketch, "E1348", {"start": v(4.85, -5.14) * mm, "end": v(4.85, -5.16) * mm});
            skLineSegment(sketch, "E1349", {"start": v(4.85, -5.16) * mm, "end": v(4.86, -5.18) * mm});
            skLineSegment(sketch, "E1350", {"start": v(4.86, -5.18) * mm, "end": v(4.87, -5.2) * mm});
            skLineSegment(sketch, "E1351", {"start": v(4.87, -5.2) * mm, "end": v(4.88, -5.21) * mm});
            skLineSegment(sketch, "E1352", {"start": v(4.88, -5.21) * mm, "end": v(4.89, -5.23) * mm});
            skLineSegment(sketch, "E1353", {"start": v(4.89, -5.23) * mm, "end": v(4.9, -5.25) * mm});
            skLineSegment(sketch, "E1354", {"start": v(4.9, -5.25) * mm, "end": v(4.9, -5.27) * mm});
            skLineSegment(sketch, "E1355", {"start": v(4.9, -5.27) * mm, "end": v(4.91, -5.3) * mm});
            skLineSegment(sketch, "E1356", {"start": v(4.91, -5.3) * mm, "end": v(4.92, -5.31) * mm});
            skLineSegment(sketch, "E1357", {"start": v(4.92, -5.31) * mm, "end": v(4.93, -5.33) * mm});
            skLineSegment(sketch, "E1358", {"start": v(4.93, -5.33) * mm, "end": v(4.94, -5.36) * mm});
            skLineSegment(sketch, "E1359", {"start": v(4.94, -5.36) * mm, "end": v(4.95, -5.38) * mm});
            skLineSegment(sketch, "E1360", {"start": v(4.95, -5.38) * mm, "end": v(4.96, -5.4) * mm});
            skLineSegment(sketch, "E1361", {"start": v(4.96, -5.4) * mm, "end": v(4.96, -5.43) * mm});
            skLineSegment(sketch, "E1362", {"start": v(4.96, -5.43) * mm, "end": v(4.97, -5.45) * mm});
            skLineSegment(sketch, "E1363", {"start": v(4.97, -5.45) * mm, "end": v(4.98, -5.48) * mm});
            skLineSegment(sketch, "E1364", {"start": v(4.98, -5.48) * mm, "end": v(5, -5.5) * mm});
            skLineSegment(sketch, "E1365", {"start": v(5, -5.5) * mm, "end": v(5, -5.53) * mm});
            skLineSegment(sketch, "E1366", {"start": v(5, -5.53) * mm, "end": v(5, -5.55) * mm});
            skLineSegment(sketch, "E1367", {"start": v(5, -5.55) * mm, "end": v(5.01, -5.58) * mm});
            skLineSegment(sketch, "E1368", {"start": v(5.01, -5.58) * mm, "end": v(5.02, -5.6) * mm});
            skLineSegment(sketch, "E1369", {"start": v(5.02, -5.6) * mm, "end": v(5.03, -5.64) * mm});
            skLineSegment(sketch, "E1370", {"start": v(5.03, -5.64) * mm, "end": v(5.04, -5.67) * mm});
            skLineSegment(sketch, "E1371", {"start": v(5.04, -5.67) * mm, "end": v(5.05, -5.7) * mm});
            skLineSegment(sketch, "E1372", {"start": v(5.05, -5.7) * mm, "end": v(5.05, -5.73) * mm});
            skLineSegment(sketch, "E1373", {"start": v(5.05, -5.73) * mm, "end": v(5.06, -5.76) * mm});
            skLineSegment(sketch, "E1374", {"start": v(5.06, -5.76) * mm, "end": v(5.07, -5.79) * mm});
            skLineSegment(sketch, "E1375", {"start": v(5.07, -5.79) * mm, "end": v(5.08, -5.82) * mm});
            skLineSegment(sketch, "E1376", {"start": v(5.08, -5.82) * mm, "end": v(5.08, -5.85) * mm});
            skLineSegment(sketch, "E1377", {"start": v(4.03, -5.54) * mm, "end": v(4.04, -5.54) * mm});
            skLineSegment(sketch, "E1378", {"start": v(4.04, -5.54) * mm, "end": v(4.04, -5.54) * mm});
            skLineSegment(sketch, "E1379", {"start": v(4.04, -5.54) * mm, "end": v(4.05, -5.54) * mm});
            skLineSegment(sketch, "E1380", {"start": v(4.05, -5.54) * mm, "end": v(4.06, -5.54) * mm});
            skLineSegment(sketch, "E1381", {"start": v(4.06, -5.54) * mm, "end": v(4.07, -5.55) * mm});
            skLineSegment(sketch, "E1382", {"start": v(4.07, -5.55) * mm, "end": v(4.08, -5.55) * mm});
            skLineSegment(sketch, "E1383", {"start": v(4.08, -5.55) * mm, "end": v(4.1, -5.56) * mm});
            skLineSegment(sketch, "E1384", {"start": v(4.1, -5.56) * mm, "end": v(4.1, -5.57) * mm});
            skLineSegment(sketch, "E1385", {"start": v(4.1, -5.57) * mm, "end": v(4.11, -5.58) * mm});
            skLineSegment(sketch, "E1386", {"start": v(4.11, -5.58) * mm, "end": v(4.12, -5.59) * mm});
            skLineSegment(sketch, "E1387", {"start": v(4.12, -5.59) * mm, "end": v(4.14, -5.6) * mm});
            skLineSegment(sketch, "E1388", {"start": v(4.14, -5.6) * mm, "end": v(4.15, -5.6) * mm});
            skLineSegment(sketch, "E1389", {"start": v(4.15, -5.6) * mm, "end": v(4.16, -5.62) * mm});
            skLineSegment(sketch, "E1390", {"start": v(4.16, -5.62) * mm, "end": v(4.17, -5.63) * mm});
            skLineSegment(sketch, "E1391", {"start": v(4.17, -5.63) * mm, "end": v(4.18, -5.64) * mm});
            skLineSegment(sketch, "E1392", {"start": v(4.18, -5.64) * mm, "end": v(4.2, -5.65) * mm});
            skLineSegment(sketch, "E1393", {"start": v(4.2, -5.65) * mm, "end": v(4.21, -5.66) * mm});
            skLineSegment(sketch, "E1394", {"start": v(4.21, -5.66) * mm, "end": v(4.22, -5.67) * mm});
            skLineSegment(sketch, "E1395", {"start": v(4.22, -5.67) * mm, "end": v(4.24, -5.68) * mm});
            skLineSegment(sketch, "E1396", {"start": v(4.24, -5.68) * mm, "end": v(4.25, -5.69) * mm});
            skLineSegment(sketch, "E1397", {"start": v(4.25, -5.69) * mm, "end": v(4.27, -5.7) * mm});
            skLineSegment(sketch, "E1398", {"start": v(4.27, -5.7) * mm, "end": v(4.29, -5.71) * mm});
            skLineSegment(sketch, "E1399", {"start": v(4.29, -5.71) * mm, "end": v(4.3, -5.72) * mm});
            skLineSegment(sketch, "E1400", {"start": v(4.3, -5.72) * mm, "end": v(4.32, -5.73) * mm});
            skLineSegment(sketch, "E1401", {"start": v(4.32, -5.73) * mm, "end": v(4.34, -5.75) * mm});
            skLineSegment(sketch, "E1402", {"start": v(4.34, -5.75) * mm, "end": v(4.36, -5.76) * mm});
            skLineSegment(sketch, "E1403", {"start": v(4.36, -5.76) * mm, "end": v(4.38, -5.77) * mm});
            skLineSegment(sketch, "E1404", {"start": v(4.38, -5.77) * mm, "end": v(4.4, -5.78) * mm});
            skLineSegment(sketch, "E1405", {"start": v(4.4, -5.78) * mm, "end": v(4.42, -5.8) * mm});
            skLineSegment(sketch, "E1406", {"start": v(4.42, -5.8) * mm, "end": v(4.44, -5.8) * mm});
            skLineSegment(sketch, "E1407", {"start": v(4.44, -5.8) * mm, "end": v(4.46, -5.82) * mm});
            skLineSegment(sketch, "E1408", {"start": v(4.46, -5.82) * mm, "end": v(4.48, -5.83) * mm});
            skLineSegment(sketch, "E1409", {"start": v(4.48, -5.83) * mm, "end": v(4.5, -5.84) * mm});
            skLineSegment(sketch, "E1410", {"start": v(4.5, -5.84) * mm, "end": v(4.53, -5.86) * mm});
            skLineSegment(sketch, "E1411", {"start": v(4.53, -5.86) * mm, "end": v(4.55, -5.87) * mm});
            skLineSegment(sketch, "E1412", {"start": v(4.55, -5.87) * mm, "end": v(4.58, -5.88) * mm});
            skLineSegment(sketch, "E1413", {"start": v(4.58, -5.88) * mm, "end": v(4.6, -5.9) * mm});
            skLineSegment(sketch, "E1414", {"start": v(4.6, -5.9) * mm, "end": v(4.63, -5.9) * mm});
            skLineSegment(sketch, "E1415", {"start": v(4.63, -5.9) * mm, "end": v(4.65, -5.92) * mm});
            skLineSegment(sketch, "E1416", {"start": v(4.65, -5.92) * mm, "end": v(4.68, -5.93) * mm});
            skLineSegment(sketch, "E1417", {"start": v(4.68, -5.93) * mm, "end": v(4.7, -5.95) * mm});
            skLineSegment(sketch, "E1418", {"start": v(4.7, -5.95) * mm, "end": v(4.73, -5.96) * mm});
            skLineSegment(sketch, "E1419", {"start": v(4.73, -5.96) * mm, "end": v(4.76, -5.97) * mm});
            skLineSegment(sketch, "E1420", {"start": v(4.76, -5.97) * mm, "end": v(4.8, -5.98) * mm});
            skLineSegment(sketch, "E1421", {"start": v(4.8, -5.98) * mm, "end": v(4.82, -6) * mm});
            skLineSegment(sketch, "E1422", {"start": v(4.82, -6) * mm, "end": v(4.85, -6) * mm});
            skLineSegment(sketch, "E1423", {"start": v(4.85, -6) * mm, "end": v(4.88, -6.02) * mm});
            skArc(sketch, "E1424", {"start": v(4.88, -6.02) * mm, "mid": v(4.98, -5.94) * mm, "end": v(5.08, -5.85) * mm});
            skLineSegment(sketch, "E1425", {"start": v(3.83, -5.68) * mm, "end": v(3.82, -5.69) * mm});
            skLineSegment(sketch, "E1426", {"start": v(3.82, -5.69) * mm, "end": v(3.82, -5.7) * mm});
            skLineSegment(sketch, "E1427", {"start": v(3.82, -5.7) * mm, "end": v(3.82, -5.7) * mm});
            skLineSegment(sketch, "E1428", {"start": v(3.82, -5.7) * mm, "end": v(3.82, -5.71) * mm});
            skLineSegment(sketch, "E1429", {"start": v(3.82, -5.71) * mm, "end": v(3.82, -5.72) * mm});
            skLineSegment(sketch, "E1430", {"start": v(3.82, -5.72) * mm, "end": v(3.82, -5.74) * mm});
            skLineSegment(sketch, "E1431", {"start": v(3.82, -5.74) * mm, "end": v(3.83, -5.75) * mm});
            skLineSegment(sketch, "E1432", {"start": v(3.83, -5.75) * mm, "end": v(3.83, -5.76) * mm});
            skLineSegment(sketch, "E1433", {"start": v(3.83, -5.76) * mm, "end": v(3.83, -5.77) * mm});
            skLineSegment(sketch, "E1434", {"start": v(3.83, -5.77) * mm, "end": v(3.84, -5.79) * mm});
            skLineSegment(sketch, "E1435", {"start": v(3.84, -5.79) * mm, "end": v(3.84, -5.8) * mm});
            skLineSegment(sketch, "E1436", {"start": v(3.84, -5.8) * mm, "end": v(3.85, -5.81) * mm});
            skLineSegment(sketch, "E1437", {"start": v(3.85, -5.81) * mm, "end": v(3.85, -5.83) * mm});
            skLineSegment(sketch, "E1438", {"start": v(3.85, -5.83) * mm, "end": v(3.86, -5.84) * mm});
            skLineSegment(sketch, "E1439", {"start": v(3.86, -5.84) * mm, "end": v(3.86, -5.86) * mm});
            skLineSegment(sketch, "E1440", {"start": v(3.86, -5.86) * mm, "end": v(3.87, -5.87) * mm});
            skLineSegment(sketch, "E1441", {"start": v(3.87, -5.87) * mm, "end": v(3.87, -5.9) * mm});
            skLineSegment(sketch, "E1442", {"start": v(3.87, -5.9) * mm, "end": v(3.88, -5.9) * mm});
            skLineSegment(sketch, "E1443", {"start": v(3.88, -5.9) * mm, "end": v(3.89, -5.93) * mm});
            skLineSegment(sketch, "E1444", {"start": v(3.89, -5.93) * mm, "end": v(3.9, -5.94) * mm});
            skLineSegment(sketch, "E1445", {"start": v(3.9, -5.94) * mm, "end": v(3.9, -5.96) * mm});
            skLineSegment(sketch, "E1446", {"start": v(3.9, -5.96) * mm, "end": v(3.9, -5.98) * mm});
            skLineSegment(sketch, "E1447", {"start": v(3.9, -5.98) * mm, "end": v(3.9, -6) * mm});
            skLineSegment(sketch, "E1448", {"start": v(3.9, -6) * mm, "end": v(3.91, -6.02) * mm});
            skLineSegment(sketch, "E1449", {"start": v(3.91, -6.02) * mm, "end": v(3.92, -6.04) * mm});
            skLineSegment(sketch, "E1450", {"start": v(3.92, -6.04) * mm, "end": v(3.92, -6.06) * mm});
            skLineSegment(sketch, "E1451", {"start": v(3.92, -6.06) * mm, "end": v(3.92, -6.09) * mm});
            skLineSegment(sketch, "E1452", {"start": v(3.92, -6.09) * mm, "end": v(3.93, -6.1) * mm});
            skLineSegment(sketch, "E1453", {"start": v(3.93, -6.1) * mm, "end": v(3.93, -6.13) * mm});
            skLineSegment(sketch, "E1454", {"start": v(3.93, -6.13) * mm, "end": v(3.94, -6.16) * mm});
            skLineSegment(sketch, "E1455", {"start": v(3.94, -6.16) * mm, "end": v(3.94, -6.18) * mm});
            skLineSegment(sketch, "E1456", {"start": v(3.94, -6.18) * mm, "end": v(3.95, -6.2) * mm});
            skLineSegment(sketch, "E1457", {"start": v(3.95, -6.2) * mm, "end": v(3.95, -6.23) * mm});
            skLineSegment(sketch, "E1458", {"start": v(3.95, -6.23) * mm, "end": v(3.96, -6.26) * mm});
            skLineSegment(sketch, "E1459", {"start": v(3.96, -6.26) * mm, "end": v(3.96, -6.28) * mm});
            skLineSegment(sketch, "E1460", {"start": v(3.96, -6.28) * mm, "end": v(3.96, -6.31) * mm});
            skLineSegment(sketch, "E1461", {"start": v(3.96, -6.31) * mm, "end": v(3.97, -6.34) * mm});
            skLineSegment(sketch, "E1462", {"start": v(3.97, -6.34) * mm, "end": v(3.97, -6.37) * mm});
            skLineSegment(sketch, "E1463", {"start": v(3.97, -6.37) * mm, "end": v(3.97, -6.4) * mm});
            skLineSegment(sketch, "E1464", {"start": v(3.97, -6.4) * mm, "end": v(3.98, -6.43) * mm});
            skLineSegment(sketch, "E1465", {"start": v(3.98, -6.43) * mm, "end": v(3.98, -6.46) * mm});
            skLineSegment(sketch, "E1466", {"start": v(3.98, -6.46) * mm, "end": v(3.98, -6.49) * mm});
            skLineSegment(sketch, "E1467", {"start": v(3.98, -6.49) * mm, "end": v(3.98, -6.52) * mm});
            skLineSegment(sketch, "E1468", {"start": v(3.98, -6.52) * mm, "end": v(3.98, -6.55) * mm});
            skLineSegment(sketch, "E1469", {"start": v(3.98, -6.55) * mm, "end": v(3.99, -6.58) * mm});
            skLineSegment(sketch, "E1470", {"start": v(3.99, -6.58) * mm, "end": v(3.99, -6.61) * mm});
            skLineSegment(sketch, "E1471", {"start": v(3.99, -6.61) * mm, "end": v(3.99, -6.65) * mm});
            skLineSegment(sketch, "E1472", {"start": v(3, -6.16) * mm, "end": v(3.02, -6.15) * mm});
            skLineSegment(sketch, "E1473", {"start": v(3.02, -6.15) * mm, "end": v(3.02, -6.15) * mm});
            skLineSegment(sketch, "E1474", {"start": v(3.02, -6.15) * mm, "end": v(3.03, -6.16) * mm});
            skLineSegment(sketch, "E1475", {"start": v(3.03, -6.16) * mm, "end": v(3.04, -6.16) * mm});
            skLineSegment(sketch, "E1476", {"start": v(3.04, -6.16) * mm, "end": v(3.05, -6.17) * mm});
            skLineSegment(sketch, "E1477", {"start": v(3.05, -6.17) * mm, "end": v(3.06, -6.18) * mm});
            skLineSegment(sketch, "E1478", {"start": v(3.06, -6.18) * mm, "end": v(3.07, -6.19) * mm});
            skLineSegment(sketch, "E1479", {"start": v(3.07, -6.19) * mm, "end": v(3.07, -6.2) * mm});
            skLineSegment(sketch, "E1480", {"start": v(3.07, -6.2) * mm, "end": v(3.08, -6.2) * mm});
            skLineSegment(sketch, "E1481", {"start": v(3.08, -6.2) * mm, "end": v(3.1, -6.22) * mm});
            skLineSegment(sketch, "E1482", {"start": v(3.1, -6.22) * mm, "end": v(3.1, -6.23) * mm});
            skLineSegment(sketch, "E1483", {"start": v(3.1, -6.23) * mm, "end": v(3.11, -6.24) * mm});
            skLineSegment(sketch, "E1484", {"start": v(3.11, -6.24) * mm, "end": v(3.12, -6.25) * mm});
            skLineSegment(sketch, "E1485", {"start": v(3.12, -6.25) * mm, "end": v(3.13, -6.26) * mm});
            skLineSegment(sketch, "E1486", {"start": v(3.13, -6.26) * mm, "end": v(3.14, -6.28) * mm});
            skLineSegment(sketch, "E1487", {"start": v(3.14, -6.28) * mm, "end": v(3.15, -6.29) * mm});
            skLineSegment(sketch, "E1488", {"start": v(3.15, -6.29) * mm, "end": v(3.16, -6.3) * mm});
            skLineSegment(sketch, "E1489", {"start": v(3.16, -6.3) * mm, "end": v(3.18, -6.31) * mm});
            skLineSegment(sketch, "E1490", {"start": v(3.18, -6.31) * mm, "end": v(3.19, -6.33) * mm});
            skLineSegment(sketch, "E1491", {"start": v(3.19, -6.33) * mm, "end": v(3.2, -6.34) * mm});
            skLineSegment(sketch, "E1492", {"start": v(3.2, -6.34) * mm, "end": v(3.22, -6.35) * mm});
            skLineSegment(sketch, "E1493", {"start": v(3.22, -6.35) * mm, "end": v(3.23, -6.37) * mm});
            skLineSegment(sketch, "E1494", {"start": v(3.23, -6.37) * mm, "end": v(3.24, -6.38) * mm});
            skLineSegment(sketch, "E1495", {"start": v(3.24, -6.38) * mm, "end": v(3.26, -6.4) * mm});
            skLineSegment(sketch, "E1496", {"start": v(3.26, -6.4) * mm, "end": v(3.28, -6.41) * mm});
            skLineSegment(sketch, "E1497", {"start": v(3.28, -6.41) * mm, "end": v(3.3, -6.43) * mm});
            skLineSegment(sketch, "E1498", {"start": v(3.3, -6.43) * mm, "end": v(3.3, -6.44) * mm});
            skLineSegment(sketch, "E1499", {"start": v(3.3, -6.44) * mm, "end": v(3.33, -6.46) * mm});
            skLineSegment(sketch, "E1500", {"start": v(3.33, -6.46) * mm, "end": v(3.34, -6.47) * mm});
            skLineSegment(sketch, "E1501", {"start": v(3.34, -6.47) * mm, "end": v(3.36, -6.49) * mm});
            skLineSegment(sketch, "E1502", {"start": v(3.36, -6.49) * mm, "end": v(3.38, -6.5) * mm});
            skLineSegment(sketch, "E1503", {"start": v(3.38, -6.5) * mm, "end": v(3.4, -6.52) * mm});
            skLineSegment(sketch, "E1504", {"start": v(3.4, -6.52) * mm, "end": v(3.42, -6.54) * mm});
            skLineSegment(sketch, "E1505", {"start": v(3.42, -6.54) * mm, "end": v(3.44, -6.55) * mm});
            skLineSegment(sketch, "E1506", {"start": v(3.44, -6.55) * mm, "end": v(3.46, -6.57) * mm});
            skLineSegment(sketch, "E1507", {"start": v(3.46, -6.57) * mm, "end": v(3.48, -6.59) * mm});
            skLineSegment(sketch, "E1508", {"start": v(3.48, -6.59) * mm, "end": v(3.5, -6.6) * mm});
            skLineSegment(sketch, "E1509", {"start": v(3.5, -6.6) * mm, "end": v(3.53, -6.62) * mm});
            skLineSegment(sketch, "E1510", {"start": v(3.53, -6.62) * mm, "end": v(3.55, -6.64) * mm});
            skLineSegment(sketch, "E1511", {"start": v(3.55, -6.64) * mm, "end": v(3.58, -6.66) * mm});
            skLineSegment(sketch, "E1512", {"start": v(3.58, -6.66) * mm, "end": v(3.6, -6.67) * mm});
            skLineSegment(sketch, "E1513", {"start": v(3.6, -6.67) * mm, "end": v(3.63, -6.7) * mm});
            skLineSegment(sketch, "E1514", {"start": v(3.63, -6.7) * mm, "end": v(3.65, -6.7) * mm});
            skLineSegment(sketch, "E1515", {"start": v(3.65, -6.7) * mm, "end": v(3.68, -6.73) * mm});
            skLineSegment(sketch, "E1516", {"start": v(3.68, -6.73) * mm, "end": v(3.7, -6.74) * mm});
            skLineSegment(sketch, "E1517", {"start": v(3.7, -6.74) * mm, "end": v(3.73, -6.76) * mm});
            skLineSegment(sketch, "E1518", {"start": v(3.73, -6.76) * mm, "end": v(3.76, -6.78) * mm});
            skArc(sketch, "E1519", {"start": v(3.76, -6.78) * mm, "mid": v(3.88, -6.71) * mm, "end": v(3.99, -6.65) * mm});
            skLineSegment(sketch, "E1520", {"start": v(2.78, -6.26) * mm, "end": v(2.78, -6.27) * mm});
            skLineSegment(sketch, "E1521", {"start": v(2.78, -6.27) * mm, "end": v(2.77, -6.27) * mm});
            skLineSegment(sketch, "E1522", {"start": v(2.77, -6.27) * mm, "end": v(2.77, -6.28) * mm});
            skLineSegment(sketch, "E1523", {"start": v(2.77, -6.28) * mm, "end": v(2.77, -6.29) * mm});
            skLineSegment(sketch, "E1524", {"start": v(2.77, -6.29) * mm, "end": v(2.77, -6.3) * mm});
            skLineSegment(sketch, "E1525", {"start": v(2.77, -6.3) * mm, "end": v(2.77, -6.31) * mm});
            skLineSegment(sketch, "E1526", {"start": v(2.77, -6.31) * mm, "end": v(2.77, -6.33) * mm});
            skLineSegment(sketch, "E1527", {"start": v(2.77, -6.33) * mm, "end": v(2.77, -6.34) * mm});
            skLineSegment(sketch, "E1528", {"start": v(2.77, -6.34) * mm, "end": v(2.77, -6.35) * mm});
            skLineSegment(sketch, "E1529", {"start": v(2.77, -6.35) * mm, "end": v(2.78, -6.37) * mm});
            skLineSegment(sketch, "E1530", {"start": v(2.78, -6.37) * mm, "end": v(2.78, -6.38) * mm});
            skLineSegment(sketch, "E1531", {"start": v(2.78, -6.38) * mm, "end": v(2.78, -6.4) * mm});
            skLineSegment(sketch, "E1532", {"start": v(2.78, -6.4) * mm, "end": v(2.78, -6.4) * mm});
            skLineSegment(sketch, "E1533", {"start": v(2.78, -6.4) * mm, "end": v(2.79, -6.42) * mm});
            skLineSegment(sketch, "E1534", {"start": v(2.79, -6.42) * mm, "end": v(2.79, -6.44) * mm});
            skLineSegment(sketch, "E1535", {"start": v(2.79, -6.44) * mm, "end": v(2.8, -6.46) * mm});
            skLineSegment(sketch, "E1536", {"start": v(2.8, -6.46) * mm, "end": v(2.8, -6.47) * mm});
            skLineSegment(sketch, "E1537", {"start": v(2.8, -6.47) * mm, "end": v(2.8, -6.5) * mm});
            skLineSegment(sketch, "E1538", {"start": v(2.8, -6.5) * mm, "end": v(2.8, -6.51) * mm});
            skLineSegment(sketch, "E1539", {"start": v(2.8, -6.51) * mm, "end": v(2.8, -6.53) * mm});
            skLineSegment(sketch, "E1540", {"start": v(2.8, -6.53) * mm, "end": v(2.8, -6.55) * mm});
            skLineSegment(sketch, "E1541", {"start": v(2.8, -6.55) * mm, "end": v(2.8, -6.57) * mm});
            skLineSegment(sketch, "E1542", {"start": v(2.8, -6.57) * mm, "end": v(2.8, -6.59) * mm});
            skLineSegment(sketch, "E1543", {"start": v(2.8, -6.59) * mm, "end": v(2.8, -6.6) * mm});
            skLineSegment(sketch, "E1544", {"start": v(2.8, -6.6) * mm, "end": v(2.8, -6.63) * mm});
            skLineSegment(sketch, "E1545", {"start": v(2.8, -6.63) * mm, "end": v(2.8, -6.65) * mm});
            skLineSegment(sketch, "E1546", {"start": v(2.8, -6.65) * mm, "end": v(2.8, -6.68) * mm});
            skLineSegment(sketch, "E1547", {"start": v(2.8, -6.68) * mm, "end": v(2.8, -6.7) * mm});
            skLineSegment(sketch, "E1548", {"start": v(2.8, -6.7) * mm, "end": v(2.8, -6.72) * mm});
            skLineSegment(sketch, "E1549", {"start": v(2.8, -6.72) * mm, "end": v(2.8, -6.75) * mm});
            skLineSegment(sketch, "E1550", {"start": v(2.8, -6.75) * mm, "end": v(2.8, -6.77) * mm});
            skLineSegment(sketch, "E1551", {"start": v(2.8, -6.77) * mm, "end": v(2.8, -6.8) * mm});
            skLineSegment(sketch, "E1552", {"start": v(2.8, -6.8) * mm, "end": v(2.8, -6.82) * mm});
            skLineSegment(sketch, "E1553", {"start": v(2.8, -6.82) * mm, "end": v(2.8, -6.85) * mm});
            skLineSegment(sketch, "E1554", {"start": v(2.8, -6.85) * mm, "end": v(2.8, -6.88) * mm});
            skLineSegment(sketch, "E1555", {"start": v(2.8, -6.88) * mm, "end": v(2.8, -6.9) * mm});
            skLineSegment(sketch, "E1556", {"start": v(2.8, -6.9) * mm, "end": v(2.8, -6.93) * mm});
            skLineSegment(sketch, "E1557", {"start": v(2.8, -6.93) * mm, "end": v(2.8, -6.96) * mm});
            skLineSegment(sketch, "E1558", {"start": v(2.8, -6.96) * mm, "end": v(2.8, -6.99) * mm});
            skLineSegment(sketch, "E1559", {"start": v(2.8, -6.99) * mm, "end": v(2.8, -7.02) * mm});
            skLineSegment(sketch, "E1560", {"start": v(2.8, -7.02) * mm, "end": v(2.8, -7.05) * mm});
            skLineSegment(sketch, "E1561", {"start": v(2.8, -7.05) * mm, "end": v(2.8, -7.08) * mm});
            skLineSegment(sketch, "E1562", {"start": v(2.8, -7.08) * mm, "end": v(2.8, -7.1) * mm});
            skLineSegment(sketch, "E1563", {"start": v(2.8, -7.1) * mm, "end": v(2.79, -7.14) * mm});
            skLineSegment(sketch, "E1564", {"start": v(2.79, -7.14) * mm, "end": v(2.78, -7.17) * mm});
            skLineSegment(sketch, "E1565", {"start": v(2.78, -7.17) * mm, "end": v(2.78, -7.2) * mm});
            skLineSegment(sketch, "E1566", {"start": v(2.78, -7.2) * mm, "end": v(2.77, -7.24) * mm});
            skLineSegment(sketch, "E1567", {"start": v(1.9, -6.58) * mm, "end": v(1.9, -6.58) * mm});
            skLineSegment(sketch, "E1568", {"start": v(1.9, -6.58) * mm, "end": v(1.9, -6.59) * mm});
            skLineSegment(sketch, "E1569", {"start": v(1.9, -6.59) * mm, "end": v(1.91, -6.59) * mm});
            skLineSegment(sketch, "E1570", {"start": v(1.91, -6.59) * mm, "end": v(1.92, -6.6) * mm});
            skLineSegment(sketch, "E1571", {"start": v(1.92, -6.6) * mm, "end": v(1.93, -6.6) * mm});
            skLineSegment(sketch, "E1572", {"start": v(1.93, -6.6) * mm, "end": v(1.94, -6.62) * mm});
            skLineSegment(sketch, "E1573", {"start": v(1.94, -6.62) * mm, "end": v(1.95, -6.63) * mm});
            skLineSegment(sketch, "E1574", {"start": v(1.95, -6.63) * mm, "end": v(1.95, -6.64) * mm});
            skLineSegment(sketch, "E1575", {"start": v(1.95, -6.64) * mm, "end": v(1.96, -6.65) * mm});
            skLineSegment(sketch, "E1576", {"start": v(1.96, -6.65) * mm, "end": v(1.96, -6.66) * mm});
            skLineSegment(sketch, "E1577", {"start": v(1.96, -6.66) * mm, "end": v(1.97, -6.67) * mm});
            skLineSegment(sketch, "E1578", {"start": v(1.97, -6.67) * mm, "end": v(1.98, -6.69) * mm});
            skLineSegment(sketch, "E1579", {"start": v(1.98, -6.69) * mm, "end": v(1.99, -6.7) * mm});
            skLineSegment(sketch, "E1580", {"start": v(1.99, -6.7) * mm, "end": v(2, -6.71) * mm});
            skLineSegment(sketch, "E1581", {"start": v(2, -6.71) * mm, "end": v(2, -6.73) * mm});
            skLineSegment(sketch, "E1582", {"start": v(2, -6.73) * mm, "end": v(2.01, -6.74) * mm});
            skLineSegment(sketch, "E1583", {"start": v(2.01, -6.74) * mm, "end": v(2.02, -6.75) * mm});
            skLineSegment(sketch, "E1584", {"start": v(2.02, -6.75) * mm, "end": v(2.03, -6.77) * mm});
            skLineSegment(sketch, "E1585", {"start": v(2.03, -6.77) * mm, "end": v(2.04, -6.78) * mm});
            skLineSegment(sketch, "E1586", {"start": v(2.04, -6.78) * mm, "end": v(2.05, -6.8) * mm});
            skLineSegment(sketch, "E1587", {"start": v(2.05, -6.8) * mm, "end": v(2.06, -6.82) * mm});
            skLineSegment(sketch, "E1588", {"start": v(2.06, -6.82) * mm, "end": v(2.08, -6.83) * mm});
            skLineSegment(sketch, "E1589", {"start": v(2.08, -6.83) * mm, "end": v(2.09, -6.85) * mm});
            skLineSegment(sketch, "E1590", {"start": v(2.09, -6.85) * mm, "end": v(2.1, -6.87) * mm});
            skLineSegment(sketch, "E1591", {"start": v(2.1, -6.87) * mm, "end": v(2.11, -6.88) * mm});
            skLineSegment(sketch, "E1592", {"start": v(2.11, -6.88) * mm, "end": v(2.13, -6.9) * mm});
            skLineSegment(sketch, "E1593", {"start": v(2.13, -6.9) * mm, "end": v(2.14, -6.92) * mm});
            skLineSegment(sketch, "E1594", {"start": v(2.14, -6.92) * mm, "end": v(2.15, -6.94) * mm});
            skLineSegment(sketch, "E1595", {"start": v(2.15, -6.94) * mm, "end": v(2.17, -6.96) * mm});
            skLineSegment(sketch, "E1596", {"start": v(2.17, -6.96) * mm, "end": v(2.18, -6.97) * mm});
            skLineSegment(sketch, "E1597", {"start": v(2.18, -6.97) * mm, "end": v(2.2, -7) * mm});
            skLineSegment(sketch, "E1598", {"start": v(2.2, -7) * mm, "end": v(2.22, -7.01) * mm});
            skLineSegment(sketch, "E1599", {"start": v(2.22, -7.01) * mm, "end": v(2.23, -7.03) * mm});
            skLineSegment(sketch, "E1600", {"start": v(2.23, -7.03) * mm, "end": v(2.25, -7.05) * mm});
            skLineSegment(sketch, "E1601", {"start": v(2.25, -7.05) * mm, "end": v(2.27, -7.07) * mm});
            skLineSegment(sketch, "E1602", {"start": v(2.27, -7.07) * mm, "end": v(2.29, -7.1) * mm});
            skLineSegment(sketch, "E1603", {"start": v(2.29, -7.1) * mm, "end": v(2.3, -7.11) * mm});
            skLineSegment(sketch, "E1604", {"start": v(2.3, -7.11) * mm, "end": v(2.33, -7.13) * mm});
            skLineSegment(sketch, "E1605", {"start": v(2.33, -7.13) * mm, "end": v(2.35, -7.15) * mm});
            skLineSegment(sketch, "E1606", {"start": v(2.35, -7.15) * mm, "end": v(2.37, -7.18) * mm});
            skLineSegment(sketch, "E1607", {"start": v(2.37, -7.18) * mm, "end": v(2.39, -7.2) * mm});
            skLineSegment(sketch, "E1608", {"start": v(2.39, -7.2) * mm, "end": v(2.41, -7.22) * mm});
            skLineSegment(sketch, "E1609", {"start": v(2.41, -7.22) * mm, "end": v(2.43, -7.24) * mm});
            skLineSegment(sketch, "E1610", {"start": v(2.43, -7.24) * mm, "end": v(2.46, -7.26) * mm});
            skLineSegment(sketch, "E1611", {"start": v(2.46, -7.26) * mm, "end": v(2.48, -7.28) * mm});
            skLineSegment(sketch, "E1612", {"start": v(2.48, -7.28) * mm, "end": v(2.5, -7.3) * mm});
            skLineSegment(sketch, "E1613", {"start": v(2.5, -7.3) * mm, "end": v(2.53, -7.33) * mm});
            skArc(sketch, "E1614", {"start": v(2.53, -7.33) * mm, "mid": v(2.65, -7.28) * mm, "end": v(2.77, -7.24) * mm});
            skLineSegment(sketch, "E1615", {"start": v(1.65, -6.65) * mm, "end": v(1.65, -6.65) * mm});
            skLineSegment(sketch, "E1616", {"start": v(1.65, -6.65) * mm, "end": v(1.64, -6.66) * mm});
            skLineSegment(sketch, "E1617", {"start": v(1.64, -6.66) * mm, "end": v(1.64, -6.66) * mm});
            skLineSegment(sketch, "E1618", {"start": v(1.64, -6.66) * mm, "end": v(1.63, -6.67) * mm});
            skLineSegment(sketch, "E1619", {"start": v(1.63, -6.67) * mm, "end": v(1.63, -6.68) * mm});
            skLineSegment(sketch, "E1620", {"start": v(1.63, -6.68) * mm, "end": v(1.63, -6.7) * mm});
            skLineSegment(sketch, "E1621", {"start": v(1.63, -6.7) * mm, "end": v(1.63, -6.71) * mm});
            skLineSegment(sketch, "E1622", {"start": v(1.63, -6.71) * mm, "end": v(1.63, -6.72) * mm});
            skLineSegment(sketch, "E1623", {"start": v(1.63, -6.72) * mm, "end": v(1.63, -6.74) * mm});
            skLineSegment(sketch, "E1624", {"start": v(1.63, -6.74) * mm, "end": v(1.63, -6.75) * mm});
            skLineSegment(sketch, "E1625", {"start": v(1.63, -6.75) * mm, "end": v(1.63, -6.76) * mm});
            skLineSegment(sketch, "E1626", {"start": v(1.63, -6.76) * mm, "end": v(1.63, -6.78) * mm});
            skLineSegment(sketch, "E1627", {"start": v(1.63, -6.78) * mm, "end": v(1.63, -6.8) * mm});
            skLineSegment(sketch, "E1628", {"start": v(1.63, -6.8) * mm, "end": v(1.63, -6.81) * mm});
            skLineSegment(sketch, "E1629", {"start": v(1.63, -6.81) * mm, "end": v(1.63, -6.83) * mm});
            skLineSegment(sketch, "E1630", {"start": v(1.63, -6.83) * mm, "end": v(1.63, -6.84) * mm});
            skLineSegment(sketch, "E1631", {"start": v(1.63, -6.84) * mm, "end": v(1.63, -6.86) * mm});
            skLineSegment(sketch, "E1632", {"start": v(1.63, -6.86) * mm, "end": v(1.63, -6.88) * mm});
            skLineSegment(sketch, "E1633", {"start": v(1.63, -6.88) * mm, "end": v(1.62, -6.9) * mm});
            skLineSegment(sketch, "E1634", {"start": v(1.62, -6.9) * mm, "end": v(1.62, -6.92) * mm});
            skLineSegment(sketch, "E1635", {"start": v(1.62, -6.92) * mm, "end": v(1.62, -6.94) * mm});
            skLineSegment(sketch, "E1636", {"start": v(1.62, -6.94) * mm, "end": v(1.62, -6.96) * mm});
            skLineSegment(sketch, "E1637", {"start": v(1.62, -6.96) * mm, "end": v(1.62, -6.98) * mm});
            skLineSegment(sketch, "E1638", {"start": v(1.62, -6.98) * mm, "end": v(1.61, -7) * mm});
            skLineSegment(sketch, "E1639", {"start": v(1.61, -7) * mm, "end": v(1.61, -7.02) * mm});
            skLineSegment(sketch, "E1640", {"start": v(1.61, -7.02) * mm, "end": v(1.6, -7.04) * mm});
            skLineSegment(sketch, "E1641", {"start": v(1.6, -7.04) * mm, "end": v(1.6, -7.06) * mm});
            skLineSegment(sketch, "E1642", {"start": v(1.6, -7.06) * mm, "end": v(1.6, -7.09) * mm});
            skLineSegment(sketch, "E1643", {"start": v(1.6, -7.09) * mm, "end": v(1.6, -7.1) * mm});
            skLineSegment(sketch, "E1644", {"start": v(1.6, -7.1) * mm, "end": v(1.6, -7.13) * mm});
            skLineSegment(sketch, "E1645", {"start": v(1.6, -7.13) * mm, "end": v(1.6, -7.16) * mm});
            skLineSegment(sketch, "E1646", {"start": v(1.6, -7.16) * mm, "end": v(1.59, -7.18) * mm});
            skLineSegment(sketch, "E1647", {"start": v(1.59, -7.18) * mm, "end": v(1.58, -7.2) * mm});
            skLineSegment(sketch, "E1648", {"start": v(1.58, -7.2) * mm, "end": v(1.58, -7.23) * mm});
            skLineSegment(sketch, "E1649", {"start": v(1.58, -7.23) * mm, "end": v(1.57, -7.26) * mm});
            skLineSegment(sketch, "E1650", {"start": v(1.57, -7.26) * mm, "end": v(1.57, -7.29) * mm});
            skLineSegment(sketch, "E1651", {"start": v(1.57, -7.29) * mm, "end": v(1.56, -7.31) * mm});
            skLineSegment(sketch, "E1652", {"start": v(1.56, -7.31) * mm, "end": v(1.55, -7.34) * mm});
            skLineSegment(sketch, "E1653", {"start": v(1.55, -7.34) * mm, "end": v(1.55, -7.37) * mm});
            skLineSegment(sketch, "E1654", {"start": v(1.55, -7.37) * mm, "end": v(1.54, -7.4) * mm});
            skLineSegment(sketch, "E1655", {"start": v(1.54, -7.4) * mm, "end": v(1.53, -7.43) * mm});
            skLineSegment(sketch, "E1656", {"start": v(1.53, -7.43) * mm, "end": v(1.52, -7.46) * mm});
            skLineSegment(sketch, "E1657", {"start": v(1.52, -7.46) * mm, "end": v(1.51, -7.49) * mm});
            skLineSegment(sketch, "E1658", {"start": v(1.51, -7.49) * mm, "end": v(1.5, -7.52) * mm});
            skLineSegment(sketch, "E1659", {"start": v(1.5, -7.52) * mm, "end": v(1.5, -7.55) * mm});
            skLineSegment(sketch, "E1660", {"start": v(1.5, -7.55) * mm, "end": v(1.49, -7.58) * mm});
            skLineSegment(sketch, "E1661", {"start": v(1.49, -7.58) * mm, "end": v(1.47, -7.61) * mm});
            skLineSegment(sketch, "E1662", {"start": v(0.72, -6.81) * mm, "end": v(0.73, -6.81) * mm});
            skLineSegment(sketch, "E1663", {"start": v(0.73, -6.81) * mm, "end": v(0.73, -6.82) * mm});
            skLineSegment(sketch, "E1664", {"start": v(0.73, -6.82) * mm, "end": v(0.74, -6.82) * mm});
            skLineSegment(sketch, "E1665", {"start": v(0.74, -6.82) * mm, "end": v(0.75, -6.83) * mm});
            skLineSegment(sketch, "E1666", {"start": v(0.75, -6.83) * mm, "end": v(0.75, -6.84) * mm});
            skLineSegment(sketch, "E1667", {"start": v(0.75, -6.84) * mm, "end": v(0.76, -6.85) * mm});
            skLineSegment(sketch, "E1668", {"start": v(0.76, -6.85) * mm, "end": v(0.77, -6.87) * mm});
            skLineSegment(sketch, "E1669", {"start": v(0.77, -6.87) * mm, "end": v(0.77, -6.88) * mm});
            skLineSegment(sketch, "E1670", {"start": v(0.77, -6.88) * mm, "end": v(0.77, -6.89) * mm});
            skLineSegment(sketch, "E1671", {"start": v(0.77, -6.89) * mm, "end": v(0.78, -6.9) * mm});
            skLineSegment(sketch, "E1672", {"start": v(0.78, -6.9) * mm, "end": v(0.78, -6.91) * mm});
            skLineSegment(sketch, "E1673", {"start": v(0.78, -6.91) * mm, "end": v(0.79, -6.93) * mm});
            skLineSegment(sketch, "E1674", {"start": v(0.79, -6.93) * mm, "end": v(0.8, -6.94) * mm});
            skLineSegment(sketch, "E1675", {"start": v(0.8, -6.94) * mm, "end": v(0.8, -6.96) * mm});
            skLineSegment(sketch, "E1676", {"start": v(0.8, -6.96) * mm, "end": v(0.8, -6.97) * mm});
            skLineSegment(sketch, "E1677", {"start": v(0.8, -6.97) * mm, "end": v(0.81, -6.99) * mm});
            skLineSegment(sketch, "E1678", {"start": v(0.81, -6.99) * mm, "end": v(0.82, -7) * mm});
            skLineSegment(sketch, "E1679", {"start": v(0.82, -7) * mm, "end": v(0.83, -7.02) * mm});
            skLineSegment(sketch, "E1680", {"start": v(0.83, -7.02) * mm, "end": v(0.83, -7.04) * mm});
            skLineSegment(sketch, "E1681", {"start": v(0.83, -7.04) * mm, "end": v(0.84, -7.05) * mm});
            skLineSegment(sketch, "E1682", {"start": v(0.84, -7.05) * mm, "end": v(0.85, -7.07) * mm});
            skLineSegment(sketch, "E1683", {"start": v(0.85, -7.07) * mm, "end": v(0.86, -7.09) * mm});
            skLineSegment(sketch, "E1684", {"start": v(0.86, -7.09) * mm, "end": v(0.87, -7.1) * mm});
            skLineSegment(sketch, "E1685", {"start": v(0.87, -7.1) * mm, "end": v(0.88, -7.13) * mm});
            skLineSegment(sketch, "E1686", {"start": v(0.88, -7.13) * mm, "end": v(0.89, -7.15) * mm});
            skLineSegment(sketch, "E1687", {"start": v(0.89, -7.15) * mm, "end": v(0.9, -7.17) * mm});
            skLineSegment(sketch, "E1688", {"start": v(0.9, -7.17) * mm, "end": v(0.9, -7.19) * mm});
            skLineSegment(sketch, "E1689", {"start": v(0.9, -7.19) * mm, "end": v(0.92, -7.2) * mm});
            skLineSegment(sketch, "E1690", {"start": v(0.92, -7.2) * mm, "end": v(0.93, -7.23) * mm});
            skLineSegment(sketch, "E1691", {"start": v(0.93, -7.23) * mm, "end": v(0.94, -7.25) * mm});
            skLineSegment(sketch, "E1692", {"start": v(0.94, -7.25) * mm, "end": v(0.95, -7.27) * mm});
            skLineSegment(sketch, "E1693", {"start": v(0.95, -7.27) * mm, "end": v(0.97, -7.3) * mm});
            skLineSegment(sketch, "E1694", {"start": v(0.97, -7.3) * mm, "end": v(0.98, -7.31) * mm});
            skLineSegment(sketch, "E1695", {"start": v(0.98, -7.31) * mm, "end": v(1, -7.34) * mm});
            skLineSegment(sketch, "E1696", {"start": v(1, -7.34) * mm, "end": v(1, -7.36) * mm});
            skLineSegment(sketch, "E1697", {"start": v(1, -7.36) * mm, "end": v(1.02, -7.38) * mm});
            skLineSegment(sketch, "E1698", {"start": v(1.02, -7.38) * mm, "end": v(1.04, -7.4) * mm});
            skLineSegment(sketch, "E1699", {"start": v(1.04, -7.4) * mm, "end": v(1.05, -7.43) * mm});
            skLineSegment(sketch, "E1700", {"start": v(1.05, -7.43) * mm, "end": v(1.07, -7.45) * mm});
            skLineSegment(sketch, "E1701", {"start": v(1.07, -7.45) * mm, "end": v(1.09, -7.48) * mm});
            skLineSegment(sketch, "E1702", {"start": v(1.09, -7.48) * mm, "end": v(1.1, -7.5) * mm});
            skLineSegment(sketch, "E1703", {"start": v(1.1, -7.5) * mm, "end": v(1.12, -7.53) * mm});
            skLineSegment(sketch, "E1704", {"start": v(1.12, -7.53) * mm, "end": v(1.14, -7.55) * mm});
            skLineSegment(sketch, "E1705", {"start": v(1.14, -7.55) * mm, "end": v(1.16, -7.58) * mm});
            skLineSegment(sketch, "E1706", {"start": v(1.16, -7.58) * mm, "end": v(1.18, -7.6) * mm});
            skLineSegment(sketch, "E1707", {"start": v(1.18, -7.6) * mm, "end": v(1.2, -7.63) * mm});
            skLineSegment(sketch, "E1708", {"start": v(1.2, -7.63) * mm, "end": v(1.22, -7.66) * mm});
            skArc(sketch, "E1709", {"start": v(1.22, -7.66) * mm, "mid": v(1.35, -7.63) * mm, "end": v(1.47, -7.61) * mm});
            skLineSegment(sketch, "E1710", {"start": v(0.47, -6.84) * mm, "end": v(0.47, -6.84) * mm});
            skLineSegment(sketch, "E1711", {"start": v(0.47, -6.84) * mm, "end": v(0.46, -6.84) * mm});
            skLineSegment(sketch, "E1712", {"start": v(0.46, -6.84) * mm, "end": v(0.45, -6.85) * mm});
            skLineSegment(sketch, "E1713", {"start": v(0.45, -6.85) * mm, "end": v(0.45, -6.86) * mm});
            skLineSegment(sketch, "E1714", {"start": v(0.45, -6.86) * mm, "end": v(0.45, -6.87) * mm});
            skLineSegment(sketch, "E1715", {"start": v(0.45, -6.87) * mm, "end": v(0.44, -6.88) * mm});
            skLineSegment(sketch, "E1716", {"start": v(0.44, -6.88) * mm, "end": v(0.44, -6.9) * mm});
            skLineSegment(sketch, "E1717", {"start": v(0.44, -6.9) * mm, "end": v(0.44, -6.9) * mm});
            skLineSegment(sketch, "E1718", {"start": v(0.44, -6.9) * mm, "end": v(0.43, -6.92) * mm});
            skLineSegment(sketch, "E1719", {"start": v(0.43, -6.92) * mm, "end": v(0.43, -6.93) * mm});
            skLineSegment(sketch, "E1720", {"start": v(0.43, -6.93) * mm, "end": v(0.43, -6.94) * mm});
            skLineSegment(sketch, "E1721", {"start": v(0.43, -6.94) * mm, "end": v(0.43, -6.96) * mm});
            skLineSegment(sketch, "E1722", {"start": v(0.43, -6.96) * mm, "end": v(0.42, -6.97) * mm});
            skLineSegment(sketch, "E1723", {"start": v(0.42, -6.97) * mm, "end": v(0.42, -6.99) * mm});
            skLineSegment(sketch, "E1724", {"start": v(0.42, -6.99) * mm, "end": v(0.42, -7) * mm});
            skLineSegment(sketch, "E1725", {"start": v(0.42, -7) * mm, "end": v(0.41, -7.02) * mm});
            skLineSegment(sketch, "E1726", {"start": v(0.41, -7.02) * mm, "end": v(0.41, -7.04) * mm});
            skLineSegment(sketch, "E1727", {"start": v(0.41, -7.04) * mm, "end": v(0.4, -7.06) * mm});
            skLineSegment(sketch, "E1728", {"start": v(0.4, -7.06) * mm, "end": v(0.4, -7.07) * mm});
            skLineSegment(sketch, "E1729", {"start": v(0.4, -7.07) * mm, "end": v(0.4, -7.1) * mm});
            skLineSegment(sketch, "E1730", {"start": v(0.4, -7.1) * mm, "end": v(0.4, -7.11) * mm});
            skLineSegment(sketch, "E1731", {"start": v(0.4, -7.11) * mm, "end": v(0.39, -7.13) * mm});
            skLineSegment(sketch, "E1732", {"start": v(0.39, -7.13) * mm, "end": v(0.38, -7.15) * mm});
            skLineSegment(sketch, "E1733", {"start": v(0.38, -7.15) * mm, "end": v(0.38, -7.17) * mm});
            skLineSegment(sketch, "E1734", {"start": v(0.38, -7.17) * mm, "end": v(0.37, -7.2) * mm});
            skLineSegment(sketch, "E1735", {"start": v(0.37, -7.2) * mm, "end": v(0.36, -7.21) * mm});
            skLineSegment(sketch, "E1736", {"start": v(0.36, -7.21) * mm, "end": v(0.36, -7.23) * mm});
            skLineSegment(sketch, "E1737", {"start": v(0.36, -7.23) * mm, "end": v(0.35, -7.26) * mm});
            skLineSegment(sketch, "E1738", {"start": v(0.35, -7.26) * mm, "end": v(0.34, -7.28) * mm});
            skLineSegment(sketch, "E1739", {"start": v(0.34, -7.28) * mm, "end": v(0.33, -7.3) * mm});
            skLineSegment(sketch, "E1740", {"start": v(0.33, -7.3) * mm, "end": v(0.32, -7.32) * mm});
            skLineSegment(sketch, "E1741", {"start": v(0.32, -7.32) * mm, "end": v(0.32, -7.35) * mm});
            skLineSegment(sketch, "E1742", {"start": v(0.32, -7.35) * mm, "end": v(0.3, -7.37) * mm});
            skLineSegment(sketch, "E1743", {"start": v(0.3, -7.37) * mm, "end": v(0.3, -7.4) * mm});
            skLineSegment(sketch, "E1744", {"start": v(0.3, -7.4) * mm, "end": v(0.29, -7.42) * mm});
            skLineSegment(sketch, "E1745", {"start": v(0.29, -7.42) * mm, "end": v(0.28, -7.45) * mm});
            skLineSegment(sketch, "E1746", {"start": v(0.28, -7.45) * mm, "end": v(0.27, -7.47) * mm});
            skLineSegment(sketch, "E1747", {"start": v(0.27, -7.47) * mm, "end": v(0.25, -7.5) * mm});
            skLineSegment(sketch, "E1748", {"start": v(0.25, -7.5) * mm, "end": v(0.24, -7.53) * mm});
            skLineSegment(sketch, "E1749", {"start": v(0.24, -7.53) * mm, "end": v(0.23, -7.55) * mm});
            skLineSegment(sketch, "E1750", {"start": v(0.23, -7.55) * mm, "end": v(0.22, -7.58) * mm});
            skLineSegment(sketch, "E1751", {"start": v(0.22, -7.58) * mm, "end": v(0.2, -7.6) * mm});
            skLineSegment(sketch, "E1752", {"start": v(0.2, -7.6) * mm, "end": v(0.2, -7.64) * mm});
            skLineSegment(sketch, "E1753", {"start": v(0.2, -7.64) * mm, "end": v(0.18, -7.66) * mm});
            skLineSegment(sketch, "E1754", {"start": v(0.18, -7.66) * mm, "end": v(0.16, -7.7) * mm});
            skLineSegment(sketch, "E1755", {"start": v(0.16, -7.7) * mm, "end": v(0.15, -7.72) * mm});
            skLineSegment(sketch, "E1756", {"start": v(0.15, -7.72) * mm, "end": v(0.13, -7.75) * mm});
            skLineSegment(sketch, "E1757", {"start": v(-0.47, -6.84) * mm, "end": v(-0.47, -6.84) * mm});
            skLineSegment(sketch, "E1758", {"start": v(-0.47, -6.84) * mm, "end": v(-0.46, -6.84) * mm});
            skLineSegment(sketch, "E1759", {"start": v(-0.46, -6.84) * mm, "end": v(-0.45, -6.85) * mm});
            skLineSegment(sketch, "E1760", {"start": v(-0.45, -6.85) * mm, "end": v(-0.45, -6.86) * mm});
            skLineSegment(sketch, "E1761", {"start": v(-0.45, -6.86) * mm, "end": v(-0.45, -6.87) * mm});
            skLineSegment(sketch, "E1762", {"start": v(-0.45, -6.87) * mm, "end": v(-0.44, -6.88) * mm});
            skLineSegment(sketch, "E1763", {"start": v(-0.44, -6.88) * mm, "end": v(-0.44, -6.9) * mm});
            skLineSegment(sketch, "E1764", {"start": v(-0.44, -6.9) * mm, "end": v(-0.44, -6.9) * mm});
            skLineSegment(sketch, "E1765", {"start": v(-0.44, -6.9) * mm, "end": v(-0.43, -6.92) * mm});
            skLineSegment(sketch, "E1766", {"start": v(-0.43, -6.92) * mm, "end": v(-0.43, -6.93) * mm});
            skLineSegment(sketch, "E1767", {"start": v(-0.43, -6.93) * mm, "end": v(-0.43, -6.94) * mm});
            skLineSegment(sketch, "E1768", {"start": v(-0.43, -6.94) * mm, "end": v(-0.43, -6.96) * mm});
            skLineSegment(sketch, "E1769", {"start": v(-0.43, -6.96) * mm, "end": v(-0.42, -6.97) * mm});
            skLineSegment(sketch, "E1770", {"start": v(-0.42, -6.97) * mm, "end": v(-0.42, -6.99) * mm});
            skLineSegment(sketch, "E1771", {"start": v(-0.42, -6.99) * mm, "end": v(-0.42, -7) * mm});
            skLineSegment(sketch, "E1772", {"start": v(-0.42, -7) * mm, "end": v(-0.41, -7.02) * mm});
            skLineSegment(sketch, "E1773", {"start": v(-0.41, -7.02) * mm, "end": v(-0.41, -7.04) * mm});
            skLineSegment(sketch, "E1774", {"start": v(-0.41, -7.04) * mm, "end": v(-0.4, -7.06) * mm});
            skLineSegment(sketch, "E1775", {"start": v(-0.4, -7.06) * mm, "end": v(-0.4, -7.07) * mm});
            skLineSegment(sketch, "E1776", {"start": v(-0.4, -7.07) * mm, "end": v(-0.4, -7.1) * mm});
            skLineSegment(sketch, "E1777", {"start": v(-0.4, -7.1) * mm, "end": v(-0.4, -7.11) * mm});
            skLineSegment(sketch, "E1778", {"start": v(-0.4, -7.11) * mm, "end": v(-0.39, -7.13) * mm});
            skLineSegment(sketch, "E1779", {"start": v(-0.39, -7.13) * mm, "end": v(-0.38, -7.15) * mm});
            skLineSegment(sketch, "E1780", {"start": v(-0.38, -7.15) * mm, "end": v(-0.38, -7.17) * mm});
            skLineSegment(sketch, "E1781", {"start": v(-0.38, -7.17) * mm, "end": v(-0.37, -7.2) * mm});
            skLineSegment(sketch, "E1782", {"start": v(-0.37, -7.2) * mm, "end": v(-0.36, -7.21) * mm});
            skLineSegment(sketch, "E1783", {"start": v(-0.36, -7.21) * mm, "end": v(-0.36, -7.23) * mm});
            skLineSegment(sketch, "E1784", {"start": v(-0.36, -7.23) * mm, "end": v(-0.35, -7.26) * mm});
            skLineSegment(sketch, "E1785", {"start": v(-0.35, -7.26) * mm, "end": v(-0.34, -7.28) * mm});
            skLineSegment(sketch, "E1786", {"start": v(-0.34, -7.28) * mm, "end": v(-0.33, -7.3) * mm});
            skLineSegment(sketch, "E1787", {"start": v(-0.33, -7.3) * mm, "end": v(-0.32, -7.32) * mm});
            skLineSegment(sketch, "E1788", {"start": v(-0.32, -7.32) * mm, "end": v(-0.32, -7.35) * mm});
            skLineSegment(sketch, "E1789", {"start": v(-0.32, -7.35) * mm, "end": v(-0.3, -7.37) * mm});
            skLineSegment(sketch, "E1790", {"start": v(-0.3, -7.37) * mm, "end": v(-0.3, -7.4) * mm});
            skLineSegment(sketch, "E1791", {"start": v(-0.3, -7.4) * mm, "end": v(-0.29, -7.42) * mm});
            skLineSegment(sketch, "E1792", {"start": v(-0.29, -7.42) * mm, "end": v(-0.28, -7.45) * mm});
            skLineSegment(sketch, "E1793", {"start": v(-0.28, -7.45) * mm, "end": v(-0.27, -7.47) * mm});
            skLineSegment(sketch, "E1794", {"start": v(-0.27, -7.47) * mm, "end": v(-0.25, -7.5) * mm});
            skLineSegment(sketch, "E1795", {"start": v(-0.25, -7.5) * mm, "end": v(-0.24, -7.53) * mm});
            skLineSegment(sketch, "E1796", {"start": v(-0.24, -7.53) * mm, "end": v(-0.23, -7.55) * mm});
            skLineSegment(sketch, "E1797", {"start": v(-0.23, -7.55) * mm, "end": v(-0.22, -7.58) * mm});
            skLineSegment(sketch, "E1798", {"start": v(-0.22, -7.58) * mm, "end": v(-0.2, -7.6) * mm});
            skLineSegment(sketch, "E1799", {"start": v(-0.2, -7.6) * mm, "end": v(-0.2, -7.64) * mm});
            skLineSegment(sketch, "E1800", {"start": v(-0.2, -7.64) * mm, "end": v(-0.18, -7.66) * mm});
            skLineSegment(sketch, "E1801", {"start": v(-0.18, -7.66) * mm, "end": v(-0.16, -7.7) * mm});
            skLineSegment(sketch, "E1802", {"start": v(-0.16, -7.7) * mm, "end": v(-0.15, -7.72) * mm});
            skLineSegment(sketch, "E1803", {"start": v(-0.15, -7.72) * mm, "end": v(-0.13, -7.75) * mm});
            skArc(sketch, "E1804", {"start": v(-0.13, -7.75) * mm, "mid": v(0, -7.75) * mm, "end": v(0.13, -7.75) * mm});
            skLineSegment(sketch, "E1805", {"start": v(-0.72, -6.81) * mm, "end": v(-0.73, -6.81) * mm});
            skLineSegment(sketch, "E1806", {"start": v(-0.73, -6.81) * mm, "end": v(-0.73, -6.82) * mm});
            skLineSegment(sketch, "E1807", {"start": v(-0.73, -6.82) * mm, "end": v(-0.74, -6.82) * mm});
            skLineSegment(sketch, "E1808", {"start": v(-0.74, -6.82) * mm, "end": v(-0.75, -6.83) * mm});
            skLineSegment(sketch, "E1809", {"start": v(-0.75, -6.83) * mm, "end": v(-0.75, -6.84) * mm});
            skLineSegment(sketch, "E1810", {"start": v(-0.75, -6.84) * mm, "end": v(-0.76, -6.85) * mm});
            skLineSegment(sketch, "E1811", {"start": v(-0.76, -6.85) * mm, "end": v(-0.77, -6.87) * mm});
            skLineSegment(sketch, "E1812", {"start": v(-0.77, -6.87) * mm, "end": v(-0.77, -6.88) * mm});
            skLineSegment(sketch, "E1813", {"start": v(-0.77, -6.88) * mm, "end": v(-0.77, -6.89) * mm});
            skLineSegment(sketch, "E1814", {"start": v(-0.77, -6.89) * mm, "end": v(-0.78, -6.9) * mm});
            skLineSegment(sketch, "E1815", {"start": v(-0.78, -6.9) * mm, "end": v(-0.78, -6.91) * mm});
            skLineSegment(sketch, "E1816", {"start": v(-0.78, -6.91) * mm, "end": v(-0.79, -6.93) * mm});
            skLineSegment(sketch, "E1817", {"start": v(-0.79, -6.93) * mm, "end": v(-0.8, -6.94) * mm});
            skLineSegment(sketch, "E1818", {"start": v(-0.8, -6.94) * mm, "end": v(-0.8, -6.96) * mm});
            skLineSegment(sketch, "E1819", {"start": v(-0.8, -6.96) * mm, "end": v(-0.8, -6.97) * mm});
            skLineSegment(sketch, "E1820", {"start": v(-0.8, -6.97) * mm, "end": v(-0.81, -6.99) * mm});
            skLineSegment(sketch, "E1821", {"start": v(-0.81, -6.99) * mm, "end": v(-0.82, -7) * mm});
            skLineSegment(sketch, "E1822", {"start": v(-0.82, -7) * mm, "end": v(-0.83, -7.02) * mm});
            skLineSegment(sketch, "E1823", {"start": v(-0.83, -7.02) * mm, "end": v(-0.83, -7.04) * mm});
            skLineSegment(sketch, "E1824", {"start": v(-0.83, -7.04) * mm, "end": v(-0.84, -7.05) * mm});
            skLineSegment(sketch, "E1825", {"start": v(-0.84, -7.05) * mm, "end": v(-0.85, -7.07) * mm});
            skLineSegment(sketch, "E1826", {"start": v(-0.85, -7.07) * mm, "end": v(-0.86, -7.09) * mm});
            skLineSegment(sketch, "E1827", {"start": v(-0.86, -7.09) * mm, "end": v(-0.87, -7.1) * mm});
            skLineSegment(sketch, "E1828", {"start": v(-0.87, -7.1) * mm, "end": v(-0.88, -7.13) * mm});
            skLineSegment(sketch, "E1829", {"start": v(-0.88, -7.13) * mm, "end": v(-0.89, -7.15) * mm});
            skLineSegment(sketch, "E1830", {"start": v(-0.89, -7.15) * mm, "end": v(-0.9, -7.17) * mm});
            skLineSegment(sketch, "E1831", {"start": v(-0.9, -7.17) * mm, "end": v(-0.9, -7.19) * mm});
            skLineSegment(sketch, "E1832", {"start": v(-0.9, -7.19) * mm, "end": v(-0.92, -7.2) * mm});
            skLineSegment(sketch, "E1833", {"start": v(-0.92, -7.2) * mm, "end": v(-0.93, -7.23) * mm});
            skLineSegment(sketch, "E1834", {"start": v(-0.93, -7.23) * mm, "end": v(-0.94, -7.25) * mm});
            skLineSegment(sketch, "E1835", {"start": v(-0.94, -7.25) * mm, "end": v(-0.95, -7.27) * mm});
            skLineSegment(sketch, "E1836", {"start": v(-0.95, -7.27) * mm, "end": v(-0.97, -7.3) * mm});
            skLineSegment(sketch, "E1837", {"start": v(-0.97, -7.3) * mm, "end": v(-0.98, -7.31) * mm});
            skLineSegment(sketch, "E1838", {"start": v(-0.98, -7.31) * mm, "end": v(-1, -7.34) * mm});
            skLineSegment(sketch, "E1839", {"start": v(-1, -7.34) * mm, "end": v(-1, -7.36) * mm});
            skLineSegment(sketch, "E1840", {"start": v(-1, -7.36) * mm, "end": v(-1.02, -7.38) * mm});
            skLineSegment(sketch, "E1841", {"start": v(-1.02, -7.38) * mm, "end": v(-1.04, -7.4) * mm});
            skLineSegment(sketch, "E1842", {"start": v(-1.04, -7.4) * mm, "end": v(-1.05, -7.43) * mm});
            skLineSegment(sketch, "E1843", {"start": v(-1.05, -7.43) * mm, "end": v(-1.07, -7.45) * mm});
            skLineSegment(sketch, "E1844", {"start": v(-1.07, -7.45) * mm, "end": v(-1.09, -7.48) * mm});
            skLineSegment(sketch, "E1845", {"start": v(-1.09, -7.48) * mm, "end": v(-1.1, -7.5) * mm});
            skLineSegment(sketch, "E1846", {"start": v(-1.1, -7.5) * mm, "end": v(-1.12, -7.53) * mm});
            skLineSegment(sketch, "E1847", {"start": v(-1.12, -7.53) * mm, "end": v(-1.14, -7.55) * mm});
            skLineSegment(sketch, "E1848", {"start": v(-1.14, -7.55) * mm, "end": v(-1.16, -7.58) * mm});
            skLineSegment(sketch, "E1849", {"start": v(-1.16, -7.58) * mm, "end": v(-1.18, -7.6) * mm});
            skLineSegment(sketch, "E1850", {"start": v(-1.18, -7.6) * mm, "end": v(-1.2, -7.63) * mm});
            skLineSegment(sketch, "E1851", {"start": v(-1.2, -7.63) * mm, "end": v(-1.22, -7.66) * mm});
            skLineSegment(sketch, "E1852", {"start": v(-1.65, -6.65) * mm, "end": v(-1.65, -6.65) * mm});
            skLineSegment(sketch, "E1853", {"start": v(-1.65, -6.65) * mm, "end": v(-1.64, -6.66) * mm});
            skLineSegment(sketch, "E1854", {"start": v(-1.64, -6.66) * mm, "end": v(-1.64, -6.66) * mm});
            skLineSegment(sketch, "E1855", {"start": v(-1.64, -6.66) * mm, "end": v(-1.63, -6.67) * mm});
            skLineSegment(sketch, "E1856", {"start": v(-1.63, -6.67) * mm, "end": v(-1.63, -6.68) * mm});
            skLineSegment(sketch, "E1857", {"start": v(-1.63, -6.68) * mm, "end": v(-1.63, -6.7) * mm});
            skLineSegment(sketch, "E1858", {"start": v(-1.63, -6.7) * mm, "end": v(-1.63, -6.71) * mm});
            skLineSegment(sketch, "E1859", {"start": v(-1.63, -6.71) * mm, "end": v(-1.63, -6.72) * mm});
            skLineSegment(sketch, "E1860", {"start": v(-1.63, -6.72) * mm, "end": v(-1.63, -6.74) * mm});
            skLineSegment(sketch, "E1861", {"start": v(-1.63, -6.74) * mm, "end": v(-1.63, -6.75) * mm});
            skLineSegment(sketch, "E1862", {"start": v(-1.63, -6.75) * mm, "end": v(-1.63, -6.76) * mm});
            skLineSegment(sketch, "E1863", {"start": v(-1.63, -6.76) * mm, "end": v(-1.63, -6.78) * mm});
            skLineSegment(sketch, "E1864", {"start": v(-1.63, -6.78) * mm, "end": v(-1.63, -6.8) * mm});
            skLineSegment(sketch, "E1865", {"start": v(-1.63, -6.8) * mm, "end": v(-1.63, -6.81) * mm});
            skLineSegment(sketch, "E1866", {"start": v(-1.63, -6.81) * mm, "end": v(-1.63, -6.83) * mm});
            skLineSegment(sketch, "E1867", {"start": v(-1.63, -6.83) * mm, "end": v(-1.63, -6.84) * mm});
            skLineSegment(sketch, "E1868", {"start": v(-1.63, -6.84) * mm, "end": v(-1.63, -6.86) * mm});
            skLineSegment(sketch, "E1869", {"start": v(-1.63, -6.86) * mm, "end": v(-1.63, -6.88) * mm});
            skLineSegment(sketch, "E1870", {"start": v(-1.63, -6.88) * mm, "end": v(-1.62, -6.9) * mm});
            skLineSegment(sketch, "E1871", {"start": v(-1.62, -6.9) * mm, "end": v(-1.62, -6.92) * mm});
            skLineSegment(sketch, "E1872", {"start": v(-1.62, -6.92) * mm, "end": v(-1.62, -6.94) * mm});
            skLineSegment(sketch, "E1873", {"start": v(-1.62, -6.94) * mm, "end": v(-1.62, -6.96) * mm});
            skLineSegment(sketch, "E1874", {"start": v(-1.62, -6.96) * mm, "end": v(-1.62, -6.98) * mm});
            skLineSegment(sketch, "E1875", {"start": v(-1.62, -6.98) * mm, "end": v(-1.61, -7) * mm});
            skLineSegment(sketch, "E1876", {"start": v(-1.61, -7) * mm, "end": v(-1.61, -7.02) * mm});
            skLineSegment(sketch, "E1877", {"start": v(-1.61, -7.02) * mm, "end": v(-1.6, -7.04) * mm});
            skLineSegment(sketch, "E1878", {"start": v(-1.6, -7.04) * mm, "end": v(-1.6, -7.06) * mm});
            skLineSegment(sketch, "E1879", {"start": v(-1.6, -7.06) * mm, "end": v(-1.6, -7.09) * mm});
            skLineSegment(sketch, "E1880", {"start": v(-1.6, -7.09) * mm, "end": v(-1.6, -7.1) * mm});
            skLineSegment(sketch, "E1881", {"start": v(-1.6, -7.1) * mm, "end": v(-1.6, -7.13) * mm});
            skLineSegment(sketch, "E1882", {"start": v(-1.6, -7.13) * mm, "end": v(-1.6, -7.16) * mm});
            skLineSegment(sketch, "E1883", {"start": v(-1.6, -7.16) * mm, "end": v(-1.59, -7.18) * mm});
            skLineSegment(sketch, "E1884", {"start": v(-1.59, -7.18) * mm, "end": v(-1.58, -7.2) * mm});
            skLineSegment(sketch, "E1885", {"start": v(-1.58, -7.2) * mm, "end": v(-1.58, -7.23) * mm});
            skLineSegment(sketch, "E1886", {"start": v(-1.58, -7.23) * mm, "end": v(-1.57, -7.26) * mm});
            skLineSegment(sketch, "E1887", {"start": v(-1.57, -7.26) * mm, "end": v(-1.57, -7.29) * mm});
            skLineSegment(sketch, "E1888", {"start": v(-1.57, -7.29) * mm, "end": v(-1.56, -7.31) * mm});
            skLineSegment(sketch, "E1889", {"start": v(-1.56, -7.31) * mm, "end": v(-1.55, -7.34) * mm});
            skLineSegment(sketch, "E1890", {"start": v(-1.55, -7.34) * mm, "end": v(-1.55, -7.37) * mm});
            skLineSegment(sketch, "E1891", {"start": v(-1.55, -7.37) * mm, "end": v(-1.54, -7.4) * mm});
            skLineSegment(sketch, "E1892", {"start": v(-1.54, -7.4) * mm, "end": v(-1.53, -7.43) * mm});
            skLineSegment(sketch, "E1893", {"start": v(-1.53, -7.43) * mm, "end": v(-1.52, -7.46) * mm});
            skLineSegment(sketch, "E1894", {"start": v(-1.52, -7.46) * mm, "end": v(-1.51, -7.49) * mm});
            skLineSegment(sketch, "E1895", {"start": v(-1.51, -7.49) * mm, "end": v(-1.5, -7.52) * mm});
            skLineSegment(sketch, "E1896", {"start": v(-1.5, -7.52) * mm, "end": v(-1.5, -7.55) * mm});
            skLineSegment(sketch, "E1897", {"start": v(-1.5, -7.55) * mm, "end": v(-1.49, -7.58) * mm});
            skLineSegment(sketch, "E1898", {"start": v(-1.49, -7.58) * mm, "end": v(-1.47, -7.61) * mm});
            skArc(sketch, "E1899", {"start": v(-1.47, -7.61) * mm, "mid": v(-1.35, -7.63) * mm, "end": v(-1.22, -7.66) * mm});
            skLineSegment(sketch, "E1900", {"start": v(-1.9, -6.58) * mm, "end": v(-1.9, -6.58) * mm});
            skLineSegment(sketch, "E1901", {"start": v(-1.9, -6.58) * mm, "end": v(-1.9, -6.59) * mm});
            skLineSegment(sketch, "E1902", {"start": v(-1.9, -6.59) * mm, "end": v(-1.91, -6.59) * mm});
            skLineSegment(sketch, "E1903", {"start": v(-1.91, -6.59) * mm, "end": v(-1.92, -6.6) * mm});
            skLineSegment(sketch, "E1904", {"start": v(-1.92, -6.6) * mm, "end": v(-1.93, -6.6) * mm});
            skLineSegment(sketch, "E1905", {"start": v(-1.93, -6.6) * mm, "end": v(-1.94, -6.62) * mm});
            skLineSegment(sketch, "E1906", {"start": v(-1.94, -6.62) * mm, "end": v(-1.95, -6.63) * mm});
            skLineSegment(sketch, "E1907", {"start": v(-1.95, -6.63) * mm, "end": v(-1.95, -6.64) * mm});
            skLineSegment(sketch, "E1908", {"start": v(-1.95, -6.64) * mm, "end": v(-1.96, -6.65) * mm});
            skLineSegment(sketch, "E1909", {"start": v(-1.96, -6.65) * mm, "end": v(-1.96, -6.66) * mm});
            skLineSegment(sketch, "E1910", {"start": v(-1.96, -6.66) * mm, "end": v(-1.97, -6.67) * mm});
            skLineSegment(sketch, "E1911", {"start": v(-1.97, -6.67) * mm, "end": v(-1.98, -6.69) * mm});
            skLineSegment(sketch, "E1912", {"start": v(-1.98, -6.69) * mm, "end": v(-1.99, -6.7) * mm});
            skLineSegment(sketch, "E1913", {"start": v(-1.99, -6.7) * mm, "end": v(-2, -6.71) * mm});
            skLineSegment(sketch, "E1914", {"start": v(-2, -6.71) * mm, "end": v(-2, -6.73) * mm});
            skLineSegment(sketch, "E1915", {"start": v(-2, -6.73) * mm, "end": v(-2.01, -6.74) * mm});
            skLineSegment(sketch, "E1916", {"start": v(-2.01, -6.74) * mm, "end": v(-2.02, -6.75) * mm});
            skLineSegment(sketch, "E1917", {"start": v(-2.02, -6.75) * mm, "end": v(-2.03, -6.77) * mm});
            skLineSegment(sketch, "E1918", {"start": v(-2.03, -6.77) * mm, "end": v(-2.04, -6.78) * mm});
            skLineSegment(sketch, "E1919", {"start": v(-2.04, -6.78) * mm, "end": v(-2.05, -6.8) * mm});
            skLineSegment(sketch, "E1920", {"start": v(-2.05, -6.8) * mm, "end": v(-2.06, -6.82) * mm});
            skLineSegment(sketch, "E1921", {"start": v(-2.06, -6.82) * mm, "end": v(-2.08, -6.83) * mm});
            skLineSegment(sketch, "E1922", {"start": v(-2.08, -6.83) * mm, "end": v(-2.09, -6.85) * mm});
            skLineSegment(sketch, "E1923", {"start": v(-2.09, -6.85) * mm, "end": v(-2.1, -6.87) * mm});
            skLineSegment(sketch, "E1924", {"start": v(-2.1, -6.87) * mm, "end": v(-2.11, -6.88) * mm});
            skLineSegment(sketch, "E1925", {"start": v(-2.11, -6.88) * mm, "end": v(-2.13, -6.9) * mm});
            skLineSegment(sketch, "E1926", {"start": v(-2.13, -6.9) * mm, "end": v(-2.14, -6.92) * mm});
            skLineSegment(sketch, "E1927", {"start": v(-2.14, -6.92) * mm, "end": v(-2.15, -6.94) * mm});
            skLineSegment(sketch, "E1928", {"start": v(-2.15, -6.94) * mm, "end": v(-2.17, -6.96) * mm});
            skLineSegment(sketch, "E1929", {"start": v(-2.17, -6.96) * mm, "end": v(-2.18, -6.97) * mm});
            skLineSegment(sketch, "E1930", {"start": v(-2.18, -6.97) * mm, "end": v(-2.2, -7) * mm});
            skLineSegment(sketch, "E1931", {"start": v(-2.2, -7) * mm, "end": v(-2.22, -7.01) * mm});
            skLineSegment(sketch, "E1932", {"start": v(-2.22, -7.01) * mm, "end": v(-2.23, -7.03) * mm});
            skLineSegment(sketch, "E1933", {"start": v(-2.23, -7.03) * mm, "end": v(-2.25, -7.05) * mm});
            skLineSegment(sketch, "E1934", {"start": v(-2.25, -7.05) * mm, "end": v(-2.27, -7.07) * mm});
            skLineSegment(sketch, "E1935", {"start": v(-2.27, -7.07) * mm, "end": v(-2.29, -7.1) * mm});
            skLineSegment(sketch, "E1936", {"start": v(-2.29, -7.1) * mm, "end": v(-2.3, -7.11) * mm});
            skLineSegment(sketch, "E1937", {"start": v(-2.3, -7.11) * mm, "end": v(-2.33, -7.13) * mm});
            skLineSegment(sketch, "E1938", {"start": v(-2.33, -7.13) * mm, "end": v(-2.35, -7.15) * mm});
            skLineSegment(sketch, "E1939", {"start": v(-2.35, -7.15) * mm, "end": v(-2.37, -7.18) * mm});
            skLineSegment(sketch, "E1940", {"start": v(-2.37, -7.18) * mm, "end": v(-2.39, -7.2) * mm});
            skLineSegment(sketch, "E1941", {"start": v(-2.39, -7.2) * mm, "end": v(-2.41, -7.22) * mm});
            skLineSegment(sketch, "E1942", {"start": v(-2.41, -7.22) * mm, "end": v(-2.43, -7.24) * mm});
            skLineSegment(sketch, "E1943", {"start": v(-2.43, -7.24) * mm, "end": v(-2.46, -7.26) * mm});
            skLineSegment(sketch, "E1944", {"start": v(-2.46, -7.26) * mm, "end": v(-2.48, -7.28) * mm});
            skLineSegment(sketch, "E1945", {"start": v(-2.48, -7.28) * mm, "end": v(-2.5, -7.3) * mm});
            skLineSegment(sketch, "E1946", {"start": v(-2.5, -7.3) * mm, "end": v(-2.53, -7.33) * mm});
            skLineSegment(sketch, "E1947", {"start": v(-2.78, -6.26) * mm, "end": v(-2.78, -6.27) * mm});
            skLineSegment(sketch, "E1948", {"start": v(-2.78, -6.27) * mm, "end": v(-2.77, -6.27) * mm});
            skLineSegment(sketch, "E1949", {"start": v(-2.77, -6.27) * mm, "end": v(-2.77, -6.28) * mm});
            skLineSegment(sketch, "E1950", {"start": v(-2.77, -6.28) * mm, "end": v(-2.77, -6.29) * mm});
            skLineSegment(sketch, "E1951", {"start": v(-2.77, -6.29) * mm, "end": v(-2.77, -6.3) * mm});
            skLineSegment(sketch, "E1952", {"start": v(-2.77, -6.3) * mm, "end": v(-2.77, -6.31) * mm});
            skLineSegment(sketch, "E1953", {"start": v(-2.77, -6.31) * mm, "end": v(-2.77, -6.33) * mm});
            skLineSegment(sketch, "E1954", {"start": v(-2.77, -6.33) * mm, "end": v(-2.77, -6.34) * mm});
            skLineSegment(sketch, "E1955", {"start": v(-2.77, -6.34) * mm, "end": v(-2.77, -6.35) * mm});
            skLineSegment(sketch, "E1956", {"start": v(-2.77, -6.35) * mm, "end": v(-2.78, -6.37) * mm});
            skLineSegment(sketch, "E1957", {"start": v(-2.78, -6.37) * mm, "end": v(-2.78, -6.38) * mm});
            skLineSegment(sketch, "E1958", {"start": v(-2.78, -6.38) * mm, "end": v(-2.78, -6.4) * mm});
            skLineSegment(sketch, "E1959", {"start": v(-2.78, -6.4) * mm, "end": v(-2.78, -6.4) * mm});
            skLineSegment(sketch, "E1960", {"start": v(-2.78, -6.4) * mm, "end": v(-2.79, -6.42) * mm});
            skLineSegment(sketch, "E1961", {"start": v(-2.79, -6.42) * mm, "end": v(-2.79, -6.44) * mm});
            skLineSegment(sketch, "E1962", {"start": v(-2.79, -6.44) * mm, "end": v(-2.8, -6.46) * mm});
            skLineSegment(sketch, "E1963", {"start": v(-2.8, -6.46) * mm, "end": v(-2.8, -6.47) * mm});
            skLineSegment(sketch, "E1964", {"start": v(-2.8, -6.47) * mm, "end": v(-2.8, -6.5) * mm});
            skLineSegment(sketch, "E1965", {"start": v(-2.8, -6.5) * mm, "end": v(-2.8, -6.51) * mm});
            skLineSegment(sketch, "E1966", {"start": v(-2.8, -6.51) * mm, "end": v(-2.8, -6.53) * mm});
            skLineSegment(sketch, "E1967", {"start": v(-2.8, -6.53) * mm, "end": v(-2.8, -6.55) * mm});
            skLineSegment(sketch, "E1968", {"start": v(-2.8, -6.55) * mm, "end": v(-2.8, -6.57) * mm});
            skLineSegment(sketch, "E1969", {"start": v(-2.8, -6.57) * mm, "end": v(-2.8, -6.59) * mm});
            skLineSegment(sketch, "E1970", {"start": v(-2.8, -6.59) * mm, "end": v(-2.8, -6.6) * mm});
            skLineSegment(sketch, "E1971", {"start": v(-2.8, -6.6) * mm, "end": v(-2.8, -6.63) * mm});
            skLineSegment(sketch, "E1972", {"start": v(-2.8, -6.63) * mm, "end": v(-2.8, -6.65) * mm});
            skLineSegment(sketch, "E1973", {"start": v(-2.8, -6.65) * mm, "end": v(-2.8, -6.68) * mm});
            skLineSegment(sketch, "E1974", {"start": v(-2.8, -6.68) * mm, "end": v(-2.8, -6.7) * mm});
            skLineSegment(sketch, "E1975", {"start": v(-2.8, -6.7) * mm, "end": v(-2.8, -6.72) * mm});
            skLineSegment(sketch, "E1976", {"start": v(-2.8, -6.72) * mm, "end": v(-2.8, -6.75) * mm});
            skLineSegment(sketch, "E1977", {"start": v(-2.8, -6.75) * mm, "end": v(-2.8, -6.77) * mm});
            skLineSegment(sketch, "E1978", {"start": v(-2.8, -6.77) * mm, "end": v(-2.8, -6.8) * mm});
            skLineSegment(sketch, "E1979", {"start": v(-2.8, -6.8) * mm, "end": v(-2.8, -6.82) * mm});
            skLineSegment(sketch, "E1980", {"start": v(-2.8, -6.82) * mm, "end": v(-2.8, -6.85) * mm});
            skLineSegment(sketch, "E1981", {"start": v(-2.8, -6.85) * mm, "end": v(-2.8, -6.88) * mm});
            skLineSegment(sketch, "E1982", {"start": v(-2.8, -6.88) * mm, "end": v(-2.8, -6.9) * mm});
            skLineSegment(sketch, "E1983", {"start": v(-2.8, -6.9) * mm, "end": v(-2.8, -6.93) * mm});
            skLineSegment(sketch, "E1984", {"start": v(-2.8, -6.93) * mm, "end": v(-2.8, -6.96) * mm});
            skLineSegment(sketch, "E1985", {"start": v(-2.8, -6.96) * mm, "end": v(-2.8, -6.99) * mm});
            skLineSegment(sketch, "E1986", {"start": v(-2.8, -6.99) * mm, "end": v(-2.8, -7.02) * mm});
            skLineSegment(sketch, "E1987", {"start": v(-2.8, -7.02) * mm, "end": v(-2.8, -7.05) * mm});
            skLineSegment(sketch, "E1988", {"start": v(-2.8, -7.05) * mm, "end": v(-2.8, -7.08) * mm});
            skLineSegment(sketch, "E1989", {"start": v(-2.8, -7.08) * mm, "end": v(-2.8, -7.1) * mm});
            skLineSegment(sketch, "E1990", {"start": v(-2.8, -7.1) * mm, "end": v(-2.79, -7.14) * mm});
            skLineSegment(sketch, "E1991", {"start": v(-2.79, -7.14) * mm, "end": v(-2.78, -7.17) * mm});
            skLineSegment(sketch, "E1992", {"start": v(-2.78, -7.17) * mm, "end": v(-2.78, -7.2) * mm});
            skLineSegment(sketch, "E1993", {"start": v(-2.78, -7.2) * mm, "end": v(-2.77, -7.24) * mm});
            skArc(sketch, "E1994", {"start": v(-2.77, -7.24) * mm, "mid": v(-2.65, -7.28) * mm, "end": v(-2.53, -7.33) * mm});
            skLineSegment(sketch, "E1995", {"start": v(-3, -6.16) * mm, "end": v(-3.02, -6.15) * mm});
            skLineSegment(sketch, "E1996", {"start": v(-3.02, -6.15) * mm, "end": v(-3.02, -6.15) * mm});
            skLineSegment(sketch, "E1997", {"start": v(-3.02, -6.15) * mm, "end": v(-3.03, -6.16) * mm});
            skLineSegment(sketch, "E1998", {"start": v(-3.03, -6.16) * mm, "end": v(-3.04, -6.16) * mm});
            skLineSegment(sketch, "E1999", {"start": v(-3.04, -6.16) * mm, "end": v(-3.05, -6.17) * mm});
            skLineSegment(sketch, "E2000", {"start": v(-3.05, -6.17) * mm, "end": v(-3.06, -6.18) * mm});
            skLineSegment(sketch, "E2001", {"start": v(-3.06, -6.18) * mm, "end": v(-3.07, -6.19) * mm});
            skLineSegment(sketch, "E2002", {"start": v(-3.07, -6.19) * mm, "end": v(-3.07, -6.2) * mm});
            skLineSegment(sketch, "E2003", {"start": v(-3.07, -6.2) * mm, "end": v(-3.08, -6.2) * mm});
            skLineSegment(sketch, "E2004", {"start": v(-3.08, -6.2) * mm, "end": v(-3.1, -6.22) * mm});
            skLineSegment(sketch, "E2005", {"start": v(-3.1, -6.22) * mm, "end": v(-3.1, -6.23) * mm});
            skLineSegment(sketch, "E2006", {"start": v(-3.1, -6.23) * mm, "end": v(-3.11, -6.24) * mm});
            skLineSegment(sketch, "E2007", {"start": v(-3.11, -6.24) * mm, "end": v(-3.12, -6.25) * mm});
            skLineSegment(sketch, "E2008", {"start": v(-3.12, -6.25) * mm, "end": v(-3.13, -6.26) * mm});
            skLineSegment(sketch, "E2009", {"start": v(-3.13, -6.26) * mm, "end": v(-3.14, -6.28) * mm});
            skLineSegment(sketch, "E2010", {"start": v(-3.14, -6.28) * mm, "end": v(-3.15, -6.29) * mm});
            skLineSegment(sketch, "E2011", {"start": v(-3.15, -6.29) * mm, "end": v(-3.16, -6.3) * mm});
            skLineSegment(sketch, "E2012", {"start": v(-3.16, -6.3) * mm, "end": v(-3.18, -6.31) * mm});
            skLineSegment(sketch, "E2013", {"start": v(-3.18, -6.31) * mm, "end": v(-3.19, -6.33) * mm});
            skLineSegment(sketch, "E2014", {"start": v(-3.19, -6.33) * mm, "end": v(-3.2, -6.34) * mm});
            skLineSegment(sketch, "E2015", {"start": v(-3.2, -6.34) * mm, "end": v(-3.22, -6.35) * mm});
            skLineSegment(sketch, "E2016", {"start": v(-3.22, -6.35) * mm, "end": v(-3.23, -6.37) * mm});
            skLineSegment(sketch, "E2017", {"start": v(-3.23, -6.37) * mm, "end": v(-3.24, -6.38) * mm});
            skLineSegment(sketch, "E2018", {"start": v(-3.24, -6.38) * mm, "end": v(-3.26, -6.4) * mm});
            skLineSegment(sketch, "E2019", {"start": v(-3.26, -6.4) * mm, "end": v(-3.28, -6.41) * mm});
            skLineSegment(sketch, "E2020", {"start": v(-3.28, -6.41) * mm, "end": v(-3.3, -6.43) * mm});
            skLineSegment(sketch, "E2021", {"start": v(-3.3, -6.43) * mm, "end": v(-3.3, -6.44) * mm});
            skLineSegment(sketch, "E2022", {"start": v(-3.3, -6.44) * mm, "end": v(-3.33, -6.46) * mm});
            skLineSegment(sketch, "E2023", {"start": v(-3.33, -6.46) * mm, "end": v(-3.34, -6.47) * mm});
            skLineSegment(sketch, "E2024", {"start": v(-3.34, -6.47) * mm, "end": v(-3.36, -6.49) * mm});
            skLineSegment(sketch, "E2025", {"start": v(-3.36, -6.49) * mm, "end": v(-3.38, -6.5) * mm});
            skLineSegment(sketch, "E2026", {"start": v(-3.38, -6.5) * mm, "end": v(-3.4, -6.52) * mm});
            skLineSegment(sketch, "E2027", {"start": v(-3.4, -6.52) * mm, "end": v(-3.42, -6.54) * mm});
            skLineSegment(sketch, "E2028", {"start": v(-3.42, -6.54) * mm, "end": v(-3.44, -6.55) * mm});
            skLineSegment(sketch, "E2029", {"start": v(-3.44, -6.55) * mm, "end": v(-3.46, -6.57) * mm});
            skLineSegment(sketch, "E2030", {"start": v(-3.46, -6.57) * mm, "end": v(-3.48, -6.59) * mm});
            skLineSegment(sketch, "E2031", {"start": v(-3.48, -6.59) * mm, "end": v(-3.5, -6.6) * mm});
            skLineSegment(sketch, "E2032", {"start": v(-3.5, -6.6) * mm, "end": v(-3.53, -6.62) * mm});
            skLineSegment(sketch, "E2033", {"start": v(-3.53, -6.62) * mm, "end": v(-3.55, -6.64) * mm});
            skLineSegment(sketch, "E2034", {"start": v(-3.55, -6.64) * mm, "end": v(-3.58, -6.66) * mm});
            skLineSegment(sketch, "E2035", {"start": v(-3.58, -6.66) * mm, "end": v(-3.6, -6.67) * mm});
            skLineSegment(sketch, "E2036", {"start": v(-3.6, -6.67) * mm, "end": v(-3.63, -6.7) * mm});
            skLineSegment(sketch, "E2037", {"start": v(-3.63, -6.7) * mm, "end": v(-3.65, -6.7) * mm});
            skLineSegment(sketch, "E2038", {"start": v(-3.65, -6.7) * mm, "end": v(-3.68, -6.73) * mm});
            skLineSegment(sketch, "E2039", {"start": v(-3.68, -6.73) * mm, "end": v(-3.7, -6.74) * mm});
            skLineSegment(sketch, "E2040", {"start": v(-3.7, -6.74) * mm, "end": v(-3.73, -6.76) * mm});
            skLineSegment(sketch, "E2041", {"start": v(-3.73, -6.76) * mm, "end": v(-3.76, -6.78) * mm});
            skLineSegment(sketch, "E2042", {"start": v(-3.83, -5.68) * mm, "end": v(-3.82, -5.69) * mm});
            skLineSegment(sketch, "E2043", {"start": v(-3.82, -5.69) * mm, "end": v(-3.82, -5.7) * mm});
            skLineSegment(sketch, "E2044", {"start": v(-3.82, -5.7) * mm, "end": v(-3.82, -5.7) * mm});
            skLineSegment(sketch, "E2045", {"start": v(-3.82, -5.7) * mm, "end": v(-3.82, -5.71) * mm});
            skLineSegment(sketch, "E2046", {"start": v(-3.82, -5.71) * mm, "end": v(-3.82, -5.72) * mm});
            skLineSegment(sketch, "E2047", {"start": v(-3.82, -5.72) * mm, "end": v(-3.82, -5.74) * mm});
            skLineSegment(sketch, "E2048", {"start": v(-3.82, -5.74) * mm, "end": v(-3.83, -5.75) * mm});
            skLineSegment(sketch, "E2049", {"start": v(-3.83, -5.75) * mm, "end": v(-3.83, -5.76) * mm});
            skLineSegment(sketch, "E2050", {"start": v(-3.83, -5.76) * mm, "end": v(-3.83, -5.77) * mm});
            skLineSegment(sketch, "E2051", {"start": v(-3.83, -5.77) * mm, "end": v(-3.84, -5.79) * mm});
            skLineSegment(sketch, "E2052", {"start": v(-3.84, -5.79) * mm, "end": v(-3.84, -5.8) * mm});
            skLineSegment(sketch, "E2053", {"start": v(-3.84, -5.8) * mm, "end": v(-3.85, -5.81) * mm});
            skLineSegment(sketch, "E2054", {"start": v(-3.85, -5.81) * mm, "end": v(-3.85, -5.83) * mm});
            skLineSegment(sketch, "E2055", {"start": v(-3.85, -5.83) * mm, "end": v(-3.86, -5.84) * mm});
            skLineSegment(sketch, "E2056", {"start": v(-3.86, -5.84) * mm, "end": v(-3.86, -5.86) * mm});
            skLineSegment(sketch, "E2057", {"start": v(-3.86, -5.86) * mm, "end": v(-3.87, -5.87) * mm});
            skLineSegment(sketch, "E2058", {"start": v(-3.87, -5.87) * mm, "end": v(-3.87, -5.9) * mm});
            skLineSegment(sketch, "E2059", {"start": v(-3.87, -5.9) * mm, "end": v(-3.88, -5.9) * mm});
            skLineSegment(sketch, "E2060", {"start": v(-3.88, -5.9) * mm, "end": v(-3.89, -5.93) * mm});
            skLineSegment(sketch, "E2061", {"start": v(-3.89, -5.93) * mm, "end": v(-3.9, -5.94) * mm});
            skLineSegment(sketch, "E2062", {"start": v(-3.9, -5.94) * mm, "end": v(-3.9, -5.96) * mm});
            skLineSegment(sketch, "E2063", {"start": v(-3.9, -5.96) * mm, "end": v(-3.9, -5.98) * mm});
            skLineSegment(sketch, "E2064", {"start": v(-3.9, -5.98) * mm, "end": v(-3.9, -6) * mm});
            skLineSegment(sketch, "E2065", {"start": v(-3.9, -6) * mm, "end": v(-3.91, -6.02) * mm});
            skLineSegment(sketch, "E2066", {"start": v(-3.91, -6.02) * mm, "end": v(-3.92, -6.04) * mm});
            skLineSegment(sketch, "E2067", {"start": v(-3.92, -6.04) * mm, "end": v(-3.92, -6.06) * mm});
            skLineSegment(sketch, "E2068", {"start": v(-3.92, -6.06) * mm, "end": v(-3.92, -6.09) * mm});
            skLineSegment(sketch, "E2069", {"start": v(-3.92, -6.09) * mm, "end": v(-3.93, -6.1) * mm});
            skLineSegment(sketch, "E2070", {"start": v(-3.93, -6.1) * mm, "end": v(-3.93, -6.13) * mm});
            skLineSegment(sketch, "E2071", {"start": v(-3.93, -6.13) * mm, "end": v(-3.94, -6.16) * mm});
            skLineSegment(sketch, "E2072", {"start": v(-3.94, -6.16) * mm, "end": v(-3.94, -6.18) * mm});
            skLineSegment(sketch, "E2073", {"start": v(-3.94, -6.18) * mm, "end": v(-3.95, -6.2) * mm});
            skLineSegment(sketch, "E2074", {"start": v(-3.95, -6.2) * mm, "end": v(-3.95, -6.23) * mm});
            skLineSegment(sketch, "E2075", {"start": v(-3.95, -6.23) * mm, "end": v(-3.96, -6.26) * mm});
            skLineSegment(sketch, "E2076", {"start": v(-3.96, -6.26) * mm, "end": v(-3.96, -6.28) * mm});
            skLineSegment(sketch, "E2077", {"start": v(-3.96, -6.28) * mm, "end": v(-3.96, -6.31) * mm});
            skLineSegment(sketch, "E2078", {"start": v(-3.96, -6.31) * mm, "end": v(-3.97, -6.34) * mm});
            skLineSegment(sketch, "E2079", {"start": v(-3.97, -6.34) * mm, "end": v(-3.97, -6.37) * mm});
            skLineSegment(sketch, "E2080", {"start": v(-3.97, -6.37) * mm, "end": v(-3.97, -6.4) * mm});
            skLineSegment(sketch, "E2081", {"start": v(-3.97, -6.4) * mm, "end": v(-3.98, -6.43) * mm});
            skLineSegment(sketch, "E2082", {"start": v(-3.98, -6.43) * mm, "end": v(-3.98, -6.46) * mm});
            skLineSegment(sketch, "E2083", {"start": v(-3.98, -6.46) * mm, "end": v(-3.98, -6.49) * mm});
            skLineSegment(sketch, "E2084", {"start": v(-3.98, -6.49) * mm, "end": v(-3.98, -6.52) * mm});
            skLineSegment(sketch, "E2085", {"start": v(-3.98, -6.52) * mm, "end": v(-3.98, -6.55) * mm});
            skLineSegment(sketch, "E2086", {"start": v(-3.98, -6.55) * mm, "end": v(-3.99, -6.58) * mm});
            skLineSegment(sketch, "E2087", {"start": v(-3.99, -6.58) * mm, "end": v(-3.99, -6.61) * mm});
            skLineSegment(sketch, "E2088", {"start": v(-3.99, -6.61) * mm, "end": v(-3.99, -6.65) * mm});
            skArc(sketch, "E2089", {"start": v(-3.99, -6.65) * mm, "mid": v(-3.88, -6.71) * mm, "end": v(-3.76, -6.78) * mm});
            skLineSegment(sketch, "E2090", {"start": v(-4.03, -5.54) * mm, "end": v(-4.04, -5.54) * mm});
            skLineSegment(sketch, "E2091", {"start": v(-4.04, -5.54) * mm, "end": v(-4.04, -5.54) * mm});
            skLineSegment(sketch, "E2092", {"start": v(-4.04, -5.54) * mm, "end": v(-4.05, -5.54) * mm});
            skLineSegment(sketch, "E2093", {"start": v(-4.05, -5.54) * mm, "end": v(-4.06, -5.54) * mm});
            skLineSegment(sketch, "E2094", {"start": v(-4.06, -5.54) * mm, "end": v(-4.07, -5.55) * mm});
            skLineSegment(sketch, "E2095", {"start": v(-4.07, -5.55) * mm, "end": v(-4.08, -5.55) * mm});
            skLineSegment(sketch, "E2096", {"start": v(-4.08, -5.55) * mm, "end": v(-4.1, -5.56) * mm});
            skLineSegment(sketch, "E2097", {"start": v(-4.1, -5.56) * mm, "end": v(-4.1, -5.57) * mm});
            skLineSegment(sketch, "E2098", {"start": v(-4.1, -5.57) * mm, "end": v(-4.11, -5.58) * mm});
            skLineSegment(sketch, "E2099", {"start": v(-4.11, -5.58) * mm, "end": v(-4.12, -5.59) * mm});
            skLineSegment(sketch, "E2100", {"start": v(-4.12, -5.59) * mm, "end": v(-4.14, -5.6) * mm});
            skLineSegment(sketch, "E2101", {"start": v(-4.14, -5.6) * mm, "end": v(-4.15, -5.6) * mm});
            skLineSegment(sketch, "E2102", {"start": v(-4.15, -5.6) * mm, "end": v(-4.16, -5.62) * mm});
            skLineSegment(sketch, "E2103", {"start": v(-4.16, -5.62) * mm, "end": v(-4.17, -5.63) * mm});
            skLineSegment(sketch, "E2104", {"start": v(-4.17, -5.63) * mm, "end": v(-4.18, -5.64) * mm});
            skLineSegment(sketch, "E2105", {"start": v(-4.18, -5.64) * mm, "end": v(-4.2, -5.65) * mm});
            skLineSegment(sketch, "E2106", {"start": v(-4.2, -5.65) * mm, "end": v(-4.21, -5.66) * mm});
            skLineSegment(sketch, "E2107", {"start": v(-4.21, -5.66) * mm, "end": v(-4.22, -5.67) * mm});
            skLineSegment(sketch, "E2108", {"start": v(-4.22, -5.67) * mm, "end": v(-4.24, -5.68) * mm});
            skLineSegment(sketch, "E2109", {"start": v(-4.24, -5.68) * mm, "end": v(-4.25, -5.69) * mm});
            skLineSegment(sketch, "E2110", {"start": v(-4.25, -5.69) * mm, "end": v(-4.27, -5.7) * mm});
            skLineSegment(sketch, "E2111", {"start": v(-4.27, -5.7) * mm, "end": v(-4.29, -5.71) * mm});
            skLineSegment(sketch, "E2112", {"start": v(-4.29, -5.71) * mm, "end": v(-4.3, -5.72) * mm});
            skLineSegment(sketch, "E2113", {"start": v(-4.3, -5.72) * mm, "end": v(-4.32, -5.73) * mm});
            skLineSegment(sketch, "E2114", {"start": v(-4.32, -5.73) * mm, "end": v(-4.34, -5.75) * mm});
            skLineSegment(sketch, "E2115", {"start": v(-4.34, -5.75) * mm, "end": v(-4.36, -5.76) * mm});
            skLineSegment(sketch, "E2116", {"start": v(-4.36, -5.76) * mm, "end": v(-4.38, -5.77) * mm});
            skLineSegment(sketch, "E2117", {"start": v(-4.38, -5.77) * mm, "end": v(-4.4, -5.78) * mm});
            skLineSegment(sketch, "E2118", {"start": v(-4.4, -5.78) * mm, "end": v(-4.42, -5.8) * mm});
            skLineSegment(sketch, "E2119", {"start": v(-4.42, -5.8) * mm, "end": v(-4.44, -5.8) * mm});
            skLineSegment(sketch, "E2120", {"start": v(-4.44, -5.8) * mm, "end": v(-4.46, -5.82) * mm});
            skLineSegment(sketch, "E2121", {"start": v(-4.46, -5.82) * mm, "end": v(-4.48, -5.83) * mm});
            skLineSegment(sketch, "E2122", {"start": v(-4.48, -5.83) * mm, "end": v(-4.5, -5.84) * mm});
            skLineSegment(sketch, "E2123", {"start": v(-4.5, -5.84) * mm, "end": v(-4.53, -5.86) * mm});
            skLineSegment(sketch, "E2124", {"start": v(-4.53, -5.86) * mm, "end": v(-4.55, -5.87) * mm});
            skLineSegment(sketch, "E2125", {"start": v(-4.55, -5.87) * mm, "end": v(-4.58, -5.88) * mm});
            skLineSegment(sketch, "E2126", {"start": v(-4.58, -5.88) * mm, "end": v(-4.6, -5.9) * mm});
            skLineSegment(sketch, "E2127", {"start": v(-4.6, -5.9) * mm, "end": v(-4.63, -5.9) * mm});
            skLineSegment(sketch, "E2128", {"start": v(-4.63, -5.9) * mm, "end": v(-4.65, -5.92) * mm});
            skLineSegment(sketch, "E2129", {"start": v(-4.65, -5.92) * mm, "end": v(-4.68, -5.93) * mm});
            skLineSegment(sketch, "E2130", {"start": v(-4.68, -5.93) * mm, "end": v(-4.7, -5.95) * mm});
            skLineSegment(sketch, "E2131", {"start": v(-4.7, -5.95) * mm, "end": v(-4.73, -5.96) * mm});
            skLineSegment(sketch, "E2132", {"start": v(-4.73, -5.96) * mm, "end": v(-4.76, -5.97) * mm});
            skLineSegment(sketch, "E2133", {"start": v(-4.76, -5.97) * mm, "end": v(-4.8, -5.98) * mm});
            skLineSegment(sketch, "E2134", {"start": v(-4.8, -5.98) * mm, "end": v(-4.82, -6) * mm});
            skLineSegment(sketch, "E2135", {"start": v(-4.82, -6) * mm, "end": v(-4.85, -6) * mm});
            skLineSegment(sketch, "E2136", {"start": v(-4.85, -6) * mm, "end": v(-4.88, -6.02) * mm});
            skLineSegment(sketch, "E2137", {"start": v(-4.76, -4.93) * mm, "end": v(-4.75, -4.94) * mm});
            skLineSegment(sketch, "E2138", {"start": v(-4.75, -4.94) * mm, "end": v(-4.75, -4.94) * mm});
            skLineSegment(sketch, "E2139", {"start": v(-4.75, -4.94) * mm, "end": v(-4.75, -4.95) * mm});
            skLineSegment(sketch, "E2140", {"start": v(-4.75, -4.95) * mm, "end": v(-4.75, -4.96) * mm});
            skLineSegment(sketch, "E2141", {"start": v(-4.75, -4.96) * mm, "end": v(-4.75, -4.97) * mm});
            skLineSegment(sketch, "E2142", {"start": v(-4.75, -4.97) * mm, "end": v(-4.76, -4.99) * mm});
            skLineSegment(sketch, "E2143", {"start": v(-4.76, -4.99) * mm, "end": v(-4.77, -5) * mm});
            skLineSegment(sketch, "E2144", {"start": v(-4.77, -5) * mm, "end": v(-4.77, -5) * mm});
            skLineSegment(sketch, "E2145", {"start": v(-4.77, -5) * mm, "end": v(-4.78, -5.02) * mm});
            skLineSegment(sketch, "E2146", {"start": v(-4.78, -5.02) * mm, "end": v(-4.79, -5.03) * mm});
            skLineSegment(sketch, "E2147", {"start": v(-4.79, -5.03) * mm, "end": v(-4.8, -5.04) * mm});
            skLineSegment(sketch, "E2148", {"start": v(-4.8, -5.04) * mm, "end": v(-4.8, -5.06) * mm});
            skLineSegment(sketch, "E2149", {"start": v(-4.8, -5.06) * mm, "end": v(-4.8, -5.07) * mm});
            skLineSegment(sketch, "E2150", {"start": v(-4.8, -5.07) * mm, "end": v(-4.82, -5.08) * mm});
            skLineSegment(sketch, "E2151", {"start": v(-4.82, -5.08) * mm, "end": v(-4.82, -5.1) * mm});
            skLineSegment(sketch, "E2152", {"start": v(-4.82, -5.1) * mm, "end": v(-4.83, -5.11) * mm});
            skLineSegment(sketch, "E2153", {"start": v(-4.83, -5.11) * mm, "end": v(-4.84, -5.13) * mm});
            skLineSegment(sketch, "E2154", {"start": v(-4.84, -5.13) * mm, "end": v(-4.85, -5.14) * mm});
            skLineSegment(sketch, "E2155", {"start": v(-4.85, -5.14) * mm, "end": v(-4.85, -5.16) * mm});
            skLineSegment(sketch, "E2156", {"start": v(-4.85, -5.16) * mm, "end": v(-4.86, -5.18) * mm});
            skLineSegment(sketch, "E2157", {"start": v(-4.86, -5.18) * mm, "end": v(-4.87, -5.2) * mm});
            skLineSegment(sketch, "E2158", {"start": v(-4.87, -5.2) * mm, "end": v(-4.88, -5.21) * mm});
            skLineSegment(sketch, "E2159", {"start": v(-4.88, -5.21) * mm, "end": v(-4.89, -5.23) * mm});
            skLineSegment(sketch, "E2160", {"start": v(-4.89, -5.23) * mm, "end": v(-4.9, -5.25) * mm});
            skLineSegment(sketch, "E2161", {"start": v(-4.9, -5.25) * mm, "end": v(-4.9, -5.27) * mm});
            skLineSegment(sketch, "E2162", {"start": v(-4.9, -5.27) * mm, "end": v(-4.91, -5.3) * mm});
            skLineSegment(sketch, "E2163", {"start": v(-4.91, -5.3) * mm, "end": v(-4.92, -5.31) * mm});
            skLineSegment(sketch, "E2164", {"start": v(-4.92, -5.31) * mm, "end": v(-4.93, -5.33) * mm});
            skLineSegment(sketch, "E2165", {"start": v(-4.93, -5.33) * mm, "end": v(-4.94, -5.36) * mm});
            skLineSegment(sketch, "E2166", {"start": v(-4.94, -5.36) * mm, "end": v(-4.95, -5.38) * mm});
            skLineSegment(sketch, "E2167", {"start": v(-4.95, -5.38) * mm, "end": v(-4.96, -5.4) * mm});
            skLineSegment(sketch, "E2168", {"start": v(-4.96, -5.4) * mm, "end": v(-4.96, -5.43) * mm});
            skLineSegment(sketch, "E2169", {"start": v(-4.96, -5.43) * mm, "end": v(-4.97, -5.45) * mm});
            skLineSegment(sketch, "E2170", {"start": v(-4.97, -5.45) * mm, "end": v(-4.98, -5.48) * mm});
            skLineSegment(sketch, "E2171", {"start": v(-4.98, -5.48) * mm, "end": v(-5, -5.5) * mm});
            skLineSegment(sketch, "E2172", {"start": v(-5, -5.5) * mm, "end": v(-5, -5.53) * mm});
            skLineSegment(sketch, "E2173", {"start": v(-5, -5.53) * mm, "end": v(-5, -5.55) * mm});
            skLineSegment(sketch, "E2174", {"start": v(-5, -5.55) * mm, "end": v(-5.01, -5.58) * mm});
            skLineSegment(sketch, "E2175", {"start": v(-5.01, -5.58) * mm, "end": v(-5.02, -5.6) * mm});
            skLineSegment(sketch, "E2176", {"start": v(-5.02, -5.6) * mm, "end": v(-5.03, -5.64) * mm});
            skLineSegment(sketch, "E2177", {"start": v(-5.03, -5.64) * mm, "end": v(-5.04, -5.67) * mm});
            skLineSegment(sketch, "E2178", {"start": v(-5.04, -5.67) * mm, "end": v(-5.05, -5.7) * mm});
            skLineSegment(sketch, "E2179", {"start": v(-5.05, -5.7) * mm, "end": v(-5.05, -5.73) * mm});
            skLineSegment(sketch, "E2180", {"start": v(-5.05, -5.73) * mm, "end": v(-5.06, -5.76) * mm});
            skLineSegment(sketch, "E2181", {"start": v(-5.06, -5.76) * mm, "end": v(-5.07, -5.79) * mm});
            skLineSegment(sketch, "E2182", {"start": v(-5.07, -5.79) * mm, "end": v(-5.08, -5.82) * mm});
            skLineSegment(sketch, "E2183", {"start": v(-5.08, -5.82) * mm, "end": v(-5.08, -5.85) * mm});
            skArc(sketch, "E2184", {"start": v(-5.08, -5.85) * mm, "mid": v(-4.98, -5.94) * mm, "end": v(-4.88, -6.02) * mm});
            skLineSegment(sketch, "E2185", {"start": v(-4.93, -4.76) * mm, "end": v(-4.94, -4.75) * mm});
            skLineSegment(sketch, "E2186", {"start": v(-4.94, -4.75) * mm, "end": v(-4.94, -4.75) * mm});
            skLineSegment(sketch, "E2187", {"start": v(-4.94, -4.75) * mm, "end": v(-4.95, -4.75) * mm});
            skLineSegment(sketch, "E2188", {"start": v(-4.95, -4.75) * mm, "end": v(-4.96, -4.75) * mm});
            skLineSegment(sketch, "E2189", {"start": v(-4.96, -4.75) * mm, "end": v(-4.97, -4.75) * mm});
            skLineSegment(sketch, "E2190", {"start": v(-4.97, -4.75) * mm, "end": v(-4.99, -4.76) * mm});
            skLineSegment(sketch, "E2191", {"start": v(-4.99, -4.76) * mm, "end": v(-5, -4.77) * mm});
            skLineSegment(sketch, "E2192", {"start": v(-5, -4.77) * mm, "end": v(-5, -4.77) * mm});
            skLineSegment(sketch, "E2193", {"start": v(-5, -4.77) * mm, "end": v(-5.02, -4.78) * mm});
            skLineSegment(sketch, "E2194", {"start": v(-5.02, -4.78) * mm, "end": v(-5.03, -4.79) * mm});
            skLineSegment(sketch, "E2195", {"start": v(-5.03, -4.79) * mm, "end": v(-5.04, -4.8) * mm});
            skLineSegment(sketch, "E2196", {"start": v(-5.04, -4.8) * mm, "end": v(-5.06, -4.8) * mm});
            skLineSegment(sketch, "E2197", {"start": v(-5.06, -4.8) * mm, "end": v(-5.07, -4.8) * mm});
            skLineSegment(sketch, "E2198", {"start": v(-5.07, -4.8) * mm, "end": v(-5.08, -4.82) * mm});
            skLineSegment(sketch, "E2199", {"start": v(-5.08, -4.82) * mm, "end": v(-5.1, -4.82) * mm});
            skLineSegment(sketch, "E2200", {"start": v(-5.1, -4.82) * mm, "end": v(-5.11, -4.83) * mm});
            skLineSegment(sketch, "E2201", {"start": v(-5.11, -4.83) * mm, "end": v(-5.13, -4.84) * mm});
            skLineSegment(sketch, "E2202", {"start": v(-5.13, -4.84) * mm, "end": v(-5.14, -4.85) * mm});
            skLineSegment(sketch, "E2203", {"start": v(-5.14, -4.85) * mm, "end": v(-5.16, -4.85) * mm});
            skLineSegment(sketch, "E2204", {"start": v(-5.16, -4.85) * mm, "end": v(-5.18, -4.86) * mm});
            skLineSegment(sketch, "E2205", {"start": v(-5.18, -4.86) * mm, "end": v(-5.2, -4.87) * mm});
            skLineSegment(sketch, "E2206", {"start": v(-5.2, -4.87) * mm, "end": v(-5.21, -4.88) * mm});
            skLineSegment(sketch, "E2207", {"start": v(-5.21, -4.88) * mm, "end": v(-5.23, -4.89) * mm});
            skLineSegment(sketch, "E2208", {"start": v(-5.23, -4.89) * mm, "end": v(-5.25, -4.9) * mm});
            skLineSegment(sketch, "E2209", {"start": v(-5.25, -4.9) * mm, "end": v(-5.27, -4.9) * mm});
            skLineSegment(sketch, "E2210", {"start": v(-5.27, -4.9) * mm, "end": v(-5.3, -4.91) * mm});
            skLineSegment(sketch, "E2211", {"start": v(-5.3, -4.91) * mm, "end": v(-5.31, -4.92) * mm});
            skLineSegment(sketch, "E2212", {"start": v(-5.31, -4.92) * mm, "end": v(-5.33, -4.93) * mm});
            skLineSegment(sketch, "E2213", {"start": v(-5.33, -4.93) * mm, "end": v(-5.36, -4.94) * mm});
            skLineSegment(sketch, "E2214", {"start": v(-5.36, -4.94) * mm, "end": v(-5.38, -4.95) * mm});
            skLineSegment(sketch, "E2215", {"start": v(-5.38, -4.95) * mm, "end": v(-5.4, -4.96) * mm});
            skLineSegment(sketch, "E2216", {"start": v(-5.4, -4.96) * mm, "end": v(-5.43, -4.96) * mm});
            skLineSegment(sketch, "E2217", {"start": v(-5.43, -4.96) * mm, "end": v(-5.45, -4.97) * mm});
            skLineSegment(sketch, "E2218", {"start": v(-5.45, -4.97) * mm, "end": v(-5.48, -4.98) * mm});
            skLineSegment(sketch, "E2219", {"start": v(-5.48, -4.98) * mm, "end": v(-5.5, -5) * mm});
            skLineSegment(sketch, "E2220", {"start": v(-5.5, -5) * mm, "end": v(-5.53, -5) * mm});
            skLineSegment(sketch, "E2221", {"start": v(-5.53, -5) * mm, "end": v(-5.55, -5) * mm});
            skLineSegment(sketch, "E2222", {"start": v(-5.55, -5) * mm, "end": v(-5.58, -5.01) * mm});
            skLineSegment(sketch, "E2223", {"start": v(-5.58, -5.01) * mm, "end": v(-5.6, -5.02) * mm});
            skLineSegment(sketch, "E2224", {"start": v(-5.6, -5.02) * mm, "end": v(-5.64, -5.03) * mm});
            skLineSegment(sketch, "E2225", {"start": v(-5.64, -5.03) * mm, "end": v(-5.67, -5.04) * mm});
            skLineSegment(sketch, "E2226", {"start": v(-5.67, -5.04) * mm, "end": v(-5.7, -5.05) * mm});
            skLineSegment(sketch, "E2227", {"start": v(-5.7, -5.05) * mm, "end": v(-5.73, -5.05) * mm});
            skLineSegment(sketch, "E2228", {"start": v(-5.73, -5.05) * mm, "end": v(-5.76, -5.06) * mm});
            skLineSegment(sketch, "E2229", {"start": v(-5.76, -5.06) * mm, "end": v(-5.79, -5.07) * mm});
            skLineSegment(sketch, "E2230", {"start": v(-5.79, -5.07) * mm, "end": v(-5.82, -5.08) * mm});
            skLineSegment(sketch, "E2231", {"start": v(-5.82, -5.08) * mm, "end": v(-5.85, -5.08) * mm});
            skLineSegment(sketch, "E2232", {"start": v(-5.54, -4.03) * mm, "end": v(-5.54, -4.04) * mm});
            skLineSegment(sketch, "E2233", {"start": v(-5.54, -4.04) * mm, "end": v(-5.54, -4.04) * mm});
            skLineSegment(sketch, "E2234", {"start": v(-5.54, -4.04) * mm, "end": v(-5.54, -4.05) * mm});
            skLineSegment(sketch, "E2235", {"start": v(-5.54, -4.05) * mm, "end": v(-5.54, -4.06) * mm});
            skLineSegment(sketch, "E2236", {"start": v(-5.54, -4.06) * mm, "end": v(-5.55, -4.07) * mm});
            skLineSegment(sketch, "E2237", {"start": v(-5.55, -4.07) * mm, "end": v(-5.55, -4.08) * mm});
            skLineSegment(sketch, "E2238", {"start": v(-5.55, -4.08) * mm, "end": v(-5.56, -4.1) * mm});
            skLineSegment(sketch, "E2239", {"start": v(-5.56, -4.1) * mm, "end": v(-5.57, -4.1) * mm});
            skLineSegment(sketch, "E2240", {"start": v(-5.57, -4.1) * mm, "end": v(-5.58, -4.11) * mm});
            skLineSegment(sketch, "E2241", {"start": v(-5.58, -4.11) * mm, "end": v(-5.59, -4.12) * mm});
            skLineSegment(sketch, "E2242", {"start": v(-5.59, -4.12) * mm, "end": v(-5.6, -4.14) * mm});
            skLineSegment(sketch, "E2243", {"start": v(-5.6, -4.14) * mm, "end": v(-5.6, -4.15) * mm});
            skLineSegment(sketch, "E2244", {"start": v(-5.6, -4.15) * mm, "end": v(-5.62, -4.16) * mm});
            skLineSegment(sketch, "E2245", {"start": v(-5.62, -4.16) * mm, "end": v(-5.63, -4.17) * mm});
            skLineSegment(sketch, "E2246", {"start": v(-5.63, -4.17) * mm, "end": v(-5.64, -4.18) * mm});
            skLineSegment(sketch, "E2247", {"start": v(-5.64, -4.18) * mm, "end": v(-5.65, -4.2) * mm});
            skLineSegment(sketch, "E2248", {"start": v(-5.65, -4.2) * mm, "end": v(-5.66, -4.21) * mm});
            skLineSegment(sketch, "E2249", {"start": v(-5.66, -4.21) * mm, "end": v(-5.67, -4.22) * mm});
            skLineSegment(sketch, "E2250", {"start": v(-5.67, -4.22) * mm, "end": v(-5.68, -4.24) * mm});
            skLineSegment(sketch, "E2251", {"start": v(-5.68, -4.24) * mm, "end": v(-5.69, -4.25) * mm});
            skLineSegment(sketch, "E2252", {"start": v(-5.69, -4.25) * mm, "end": v(-5.7, -4.27) * mm});
            skLineSegment(sketch, "E2253", {"start": v(-5.7, -4.27) * mm, "end": v(-5.71, -4.29) * mm});
            skLineSegment(sketch, "E2254", {"start": v(-5.71, -4.29) * mm, "end": v(-5.72, -4.3) * mm});
            skLineSegment(sketch, "E2255", {"start": v(-5.72, -4.3) * mm, "end": v(-5.73, -4.32) * mm});
            skLineSegment(sketch, "E2256", {"start": v(-5.73, -4.32) * mm, "end": v(-5.75, -4.34) * mm});
            skLineSegment(sketch, "E2257", {"start": v(-5.75, -4.34) * mm, "end": v(-5.76, -4.36) * mm});
            skLineSegment(sketch, "E2258", {"start": v(-5.76, -4.36) * mm, "end": v(-5.77, -4.38) * mm});
            skLineSegment(sketch, "E2259", {"start": v(-5.77, -4.38) * mm, "end": v(-5.78, -4.4) * mm});
            skLineSegment(sketch, "E2260", {"start": v(-5.78, -4.4) * mm, "end": v(-5.8, -4.42) * mm});
            skLineSegment(sketch, "E2261", {"start": v(-5.8, -4.42) * mm, "end": v(-5.8, -4.44) * mm});
            skLineSegment(sketch, "E2262", {"start": v(-5.8, -4.44) * mm, "end": v(-5.82, -4.46) * mm});
            skLineSegment(sketch, "E2263", {"start": v(-5.82, -4.46) * mm, "end": v(-5.83, -4.48) * mm});
            skLineSegment(sketch, "E2264", {"start": v(-5.83, -4.48) * mm, "end": v(-5.84, -4.5) * mm});
            skLineSegment(sketch, "E2265", {"start": v(-5.84, -4.5) * mm, "end": v(-5.86, -4.53) * mm});
            skLineSegment(sketch, "E2266", {"start": v(-5.86, -4.53) * mm, "end": v(-5.87, -4.55) * mm});
            skLineSegment(sketch, "E2267", {"start": v(-5.87, -4.55) * mm, "end": v(-5.88, -4.58) * mm});
            skLineSegment(sketch, "E2268", {"start": v(-5.88, -4.58) * mm, "end": v(-5.9, -4.6) * mm});
            skLineSegment(sketch, "E2269", {"start": v(-5.9, -4.6) * mm, "end": v(-5.9, -4.63) * mm});
            skLineSegment(sketch, "E2270", {"start": v(-5.9, -4.63) * mm, "end": v(-5.92, -4.65) * mm});
            skLineSegment(sketch, "E2271", {"start": v(-5.92, -4.65) * mm, "end": v(-5.93, -4.68) * mm});
            skLineSegment(sketch, "E2272", {"start": v(-5.93, -4.68) * mm, "end": v(-5.95, -4.7) * mm});
            skLineSegment(sketch, "E2273", {"start": v(-5.95, -4.7) * mm, "end": v(-5.96, -4.73) * mm});
            skLineSegment(sketch, "E2274", {"start": v(-5.96, -4.73) * mm, "end": v(-5.97, -4.76) * mm});
            skLineSegment(sketch, "E2275", {"start": v(-5.97, -4.76) * mm, "end": v(-5.98, -4.8) * mm});
            skLineSegment(sketch, "E2276", {"start": v(-5.98, -4.8) * mm, "end": v(-6, -4.82) * mm});
            skLineSegment(sketch, "E2277", {"start": v(-6, -4.82) * mm, "end": v(-6, -4.85) * mm});
            skLineSegment(sketch, "E2278", {"start": v(-6, -4.85) * mm, "end": v(-6.02, -4.88) * mm});
            skArc(sketch, "E2279", {"start": v(-6.02, -4.88) * mm, "mid": v(-5.94, -4.98) * mm, "end": v(-5.85, -5.08) * mm});
            skLineSegment(sketch, "E2280", {"start": v(-5.68, -3.83) * mm, "end": v(-5.69, -3.82) * mm});
            skLineSegment(sketch, "E2281", {"start": v(-5.69, -3.82) * mm, "end": v(-5.7, -3.82) * mm});
            skLineSegment(sketch, "E2282", {"start": v(-5.7, -3.82) * mm, "end": v(-5.7, -3.82) * mm});
            skLineSegment(sketch, "E2283", {"start": v(-5.7, -3.82) * mm, "end": v(-5.71, -3.82) * mm});
            skLineSegment(sketch, "E2284", {"start": v(-5.71, -3.82) * mm, "end": v(-5.72, -3.82) * mm});
            skLineSegment(sketch, "E2285", {"start": v(-5.72, -3.82) * mm, "end": v(-5.74, -3.82) * mm});
            skLineSegment(sketch, "E2286", {"start": v(-5.74, -3.82) * mm, "end": v(-5.75, -3.83) * mm});
            skLineSegment(sketch, "E2287", {"start": v(-5.75, -3.83) * mm, "end": v(-5.76, -3.83) * mm});
            skLineSegment(sketch, "E2288", {"start": v(-5.76, -3.83) * mm, "end": v(-5.77, -3.83) * mm});
            skLineSegment(sketch, "E2289", {"start": v(-5.77, -3.83) * mm, "end": v(-5.79, -3.84) * mm});
            skLineSegment(sketch, "E2290", {"start": v(-5.79, -3.84) * mm, "end": v(-5.8, -3.84) * mm});
            skLineSegment(sketch, "E2291", {"start": v(-5.8, -3.84) * mm, "end": v(-5.81, -3.85) * mm});
            skLineSegment(sketch, "E2292", {"start": v(-5.81, -3.85) * mm, "end": v(-5.83, -3.85) * mm});
            skLineSegment(sketch, "E2293", {"start": v(-5.83, -3.85) * mm, "end": v(-5.84, -3.86) * mm});
            skLineSegment(sketch, "E2294", {"start": v(-5.84, -3.86) * mm, "end": v(-5.86, -3.86) * mm});
            skLineSegment(sketch, "E2295", {"start": v(-5.86, -3.86) * mm, "end": v(-5.87, -3.87) * mm});
            skLineSegment(sketch, "E2296", {"start": v(-5.87, -3.87) * mm, "end": v(-5.9, -3.87) * mm});
            skLineSegment(sketch, "E2297", {"start": v(-5.9, -3.87) * mm, "end": v(-5.9, -3.88) * mm});
            skLineSegment(sketch, "E2298", {"start": v(-5.9, -3.88) * mm, "end": v(-5.93, -3.89) * mm});
            skLineSegment(sketch, "E2299", {"start": v(-5.93, -3.89) * mm, "end": v(-5.94, -3.9) * mm});
            skLineSegment(sketch, "E2300", {"start": v(-5.94, -3.9) * mm, "end": v(-5.96, -3.9) * mm});
            skLineSegment(sketch, "E2301", {"start": v(-5.96, -3.9) * mm, "end": v(-5.98, -3.9) * mm});
            skLineSegment(sketch, "E2302", {"start": v(-5.98, -3.9) * mm, "end": v(-6, -3.9) * mm});
            skLineSegment(sketch, "E2303", {"start": v(-6, -3.9) * mm, "end": v(-6.02, -3.91) * mm});
            skLineSegment(sketch, "E2304", {"start": v(-6.02, -3.91) * mm, "end": v(-6.04, -3.92) * mm});
            skLineSegment(sketch, "E2305", {"start": v(-6.04, -3.92) * mm, "end": v(-6.06, -3.92) * mm});
            skLineSegment(sketch, "E2306", {"start": v(-6.06, -3.92) * mm, "end": v(-6.09, -3.92) * mm});
            skLineSegment(sketch, "E2307", {"start": v(-6.09, -3.92) * mm, "end": v(-6.1, -3.93) * mm});
            skLineSegment(sketch, "E2308", {"start": v(-6.1, -3.93) * mm, "end": v(-6.13, -3.93) * mm});
            skLineSegment(sketch, "E2309", {"start": v(-6.13, -3.93) * mm, "end": v(-6.16, -3.94) * mm});
            skLineSegment(sketch, "E2310", {"start": v(-6.16, -3.94) * mm, "end": v(-6.18, -3.94) * mm});
            skLineSegment(sketch, "E2311", {"start": v(-6.18, -3.94) * mm, "end": v(-6.2, -3.95) * mm});
            skLineSegment(sketch, "E2312", {"start": v(-6.2, -3.95) * mm, "end": v(-6.23, -3.95) * mm});
            skLineSegment(sketch, "E2313", {"start": v(-6.23, -3.95) * mm, "end": v(-6.26, -3.96) * mm});
            skLineSegment(sketch, "E2314", {"start": v(-6.26, -3.96) * mm, "end": v(-6.28, -3.96) * mm});
            skLineSegment(sketch, "E2315", {"start": v(-6.28, -3.96) * mm, "end": v(-6.31, -3.96) * mm});
            skLineSegment(sketch, "E2316", {"start": v(-6.31, -3.96) * mm, "end": v(-6.34, -3.97) * mm});
            skLineSegment(sketch, "E2317", {"start": v(-6.34, -3.97) * mm, "end": v(-6.37, -3.97) * mm});
            skLineSegment(sketch, "E2318", {"start": v(-6.37, -3.97) * mm, "end": v(-6.4, -3.97) * mm});
            skLineSegment(sketch, "E2319", {"start": v(-6.4, -3.97) * mm, "end": v(-6.43, -3.98) * mm});
            skLineSegment(sketch, "E2320", {"start": v(-6.43, -3.98) * mm, "end": v(-6.46, -3.98) * mm});
            skLineSegment(sketch, "E2321", {"start": v(-6.46, -3.98) * mm, "end": v(-6.49, -3.98) * mm});
            skLineSegment(sketch, "E2322", {"start": v(-6.49, -3.98) * mm, "end": v(-6.52, -3.98) * mm});
            skLineSegment(sketch, "E2323", {"start": v(-6.52, -3.98) * mm, "end": v(-6.55, -3.98) * mm});
            skLineSegment(sketch, "E2324", {"start": v(-6.55, -3.98) * mm, "end": v(-6.58, -3.99) * mm});
            skLineSegment(sketch, "E2325", {"start": v(-6.58, -3.99) * mm, "end": v(-6.61, -3.99) * mm});
            skLineSegment(sketch, "E2326", {"start": v(-6.61, -3.99) * mm, "end": v(-6.65, -3.99) * mm});
            skLineSegment(sketch, "E2327", {"start": v(-6.16, -3) * mm, "end": v(-6.15, -3.02) * mm});
            skLineSegment(sketch, "E2328", {"start": v(-6.15, -3.02) * mm, "end": v(-6.15, -3.02) * mm});
            skLineSegment(sketch, "E2329", {"start": v(-6.15, -3.02) * mm, "end": v(-6.16, -3.03) * mm});
            skLineSegment(sketch, "E2330", {"start": v(-6.16, -3.03) * mm, "end": v(-6.16, -3.04) * mm});
            skLineSegment(sketch, "E2331", {"start": v(-6.16, -3.04) * mm, "end": v(-6.17, -3.05) * mm});
            skLineSegment(sketch, "E2332", {"start": v(-6.17, -3.05) * mm, "end": v(-6.18, -3.06) * mm});
            skLineSegment(sketch, "E2333", {"start": v(-6.18, -3.06) * mm, "end": v(-6.19, -3.07) * mm});
            skLineSegment(sketch, "E2334", {"start": v(-6.19, -3.07) * mm, "end": v(-6.2, -3.07) * mm});
            skLineSegment(sketch, "E2335", {"start": v(-6.2, -3.07) * mm, "end": v(-6.2, -3.08) * mm});
            skLineSegment(sketch, "E2336", {"start": v(-6.2, -3.08) * mm, "end": v(-6.22, -3.1) * mm});
            skLineSegment(sketch, "E2337", {"start": v(-6.22, -3.1) * mm, "end": v(-6.23, -3.1) * mm});
            skLineSegment(sketch, "E2338", {"start": v(-6.23, -3.1) * mm, "end": v(-6.24, -3.11) * mm});
            skLineSegment(sketch, "E2339", {"start": v(-6.24, -3.11) * mm, "end": v(-6.25, -3.12) * mm});
            skLineSegment(sketch, "E2340", {"start": v(-6.25, -3.12) * mm, "end": v(-6.26, -3.13) * mm});
            skLineSegment(sketch, "E2341", {"start": v(-6.26, -3.13) * mm, "end": v(-6.28, -3.14) * mm});
            skLineSegment(sketch, "E2342", {"start": v(-6.28, -3.14) * mm, "end": v(-6.29, -3.15) * mm});
            skLineSegment(sketch, "E2343", {"start": v(-6.29, -3.15) * mm, "end": v(-6.3, -3.16) * mm});
            skLineSegment(sketch, "E2344", {"start": v(-6.3, -3.16) * mm, "end": v(-6.31, -3.18) * mm});
            skLineSegment(sketch, "E2345", {"start": v(-6.31, -3.18) * mm, "end": v(-6.33, -3.19) * mm});
            skLineSegment(sketch, "E2346", {"start": v(-6.33, -3.19) * mm, "end": v(-6.34, -3.2) * mm});
            skLineSegment(sketch, "E2347", {"start": v(-6.34, -3.2) * mm, "end": v(-6.35, -3.22) * mm});
            skLineSegment(sketch, "E2348", {"start": v(-6.35, -3.22) * mm, "end": v(-6.37, -3.23) * mm});
            skLineSegment(sketch, "E2349", {"start": v(-6.37, -3.23) * mm, "end": v(-6.38, -3.24) * mm});
            skLineSegment(sketch, "E2350", {"start": v(-6.38, -3.24) * mm, "end": v(-6.4, -3.26) * mm});
            skLineSegment(sketch, "E2351", {"start": v(-6.4, -3.26) * mm, "end": v(-6.41, -3.28) * mm});
            skLineSegment(sketch, "E2352", {"start": v(-6.41, -3.28) * mm, "end": v(-6.43, -3.3) * mm});
            skLineSegment(sketch, "E2353", {"start": v(-6.43, -3.3) * mm, "end": v(-6.44, -3.3) * mm});
            skLineSegment(sketch, "E2354", {"start": v(-6.44, -3.3) * mm, "end": v(-6.46, -3.33) * mm});
            skLineSegment(sketch, "E2355", {"start": v(-6.46, -3.33) * mm, "end": v(-6.47, -3.34) * mm});
            skLineSegment(sketch, "E2356", {"start": v(-6.47, -3.34) * mm, "end": v(-6.49, -3.36) * mm});
            skLineSegment(sketch, "E2357", {"start": v(-6.49, -3.36) * mm, "end": v(-6.5, -3.38) * mm});
            skLineSegment(sketch, "E2358", {"start": v(-6.5, -3.38) * mm, "end": v(-6.52, -3.4) * mm});
            skLineSegment(sketch, "E2359", {"start": v(-6.52, -3.4) * mm, "end": v(-6.54, -3.42) * mm});
            skLineSegment(sketch, "E2360", {"start": v(-6.54, -3.42) * mm, "end": v(-6.55, -3.44) * mm});
            skLineSegment(sketch, "E2361", {"start": v(-6.55, -3.44) * mm, "end": v(-6.57, -3.46) * mm});
            skLineSegment(sketch, "E2362", {"start": v(-6.57, -3.46) * mm, "end": v(-6.59, -3.48) * mm});
            skLineSegment(sketch, "E2363", {"start": v(-6.59, -3.48) * mm, "end": v(-6.6, -3.5) * mm});
            skLineSegment(sketch, "E2364", {"start": v(-6.6, -3.5) * mm, "end": v(-6.62, -3.53) * mm});
            skLineSegment(sketch, "E2365", {"start": v(-6.62, -3.53) * mm, "end": v(-6.64, -3.55) * mm});
            skLineSegment(sketch, "E2366", {"start": v(-6.64, -3.55) * mm, "end": v(-6.66, -3.58) * mm});
            skLineSegment(sketch, "E2367", {"start": v(-6.66, -3.58) * mm, "end": v(-6.67, -3.6) * mm});
            skLineSegment(sketch, "E2368", {"start": v(-6.67, -3.6) * mm, "end": v(-6.7, -3.63) * mm});
            skLineSegment(sketch, "E2369", {"start": v(-6.7, -3.63) * mm, "end": v(-6.7, -3.65) * mm});
            skLineSegment(sketch, "E2370", {"start": v(-6.7, -3.65) * mm, "end": v(-6.73, -3.68) * mm});
            skLineSegment(sketch, "E2371", {"start": v(-6.73, -3.68) * mm, "end": v(-6.74, -3.7) * mm});
            skLineSegment(sketch, "E2372", {"start": v(-6.74, -3.7) * mm, "end": v(-6.76, -3.73) * mm});
            skLineSegment(sketch, "E2373", {"start": v(-6.76, -3.73) * mm, "end": v(-6.78, -3.76) * mm});
            skArc(sketch, "E2374", {"start": v(-6.78, -3.76) * mm, "mid": v(-6.71, -3.88) * mm, "end": v(-6.65, -3.99) * mm});
            skLineSegment(sketch, "E2375", {"start": v(-6.26, -2.78) * mm, "end": v(-6.27, -2.78) * mm});
            skLineSegment(sketch, "E2376", {"start": v(-6.27, -2.78) * mm, "end": v(-6.27, -2.77) * mm});
            skLineSegment(sketch, "E2377", {"start": v(-6.27, -2.77) * mm, "end": v(-6.28, -2.77) * mm});
            skLineSegment(sketch, "E2378", {"start": v(-6.28, -2.77) * mm, "end": v(-6.29, -2.77) * mm});
            skLineSegment(sketch, "E2379", {"start": v(-6.29, -2.77) * mm, "end": v(-6.3, -2.77) * mm});
            skLineSegment(sketch, "E2380", {"start": v(-6.3, -2.77) * mm, "end": v(-6.31, -2.77) * mm});
            skLineSegment(sketch, "E2381", {"start": v(-6.31, -2.77) * mm, "end": v(-6.33, -2.77) * mm});
            skLineSegment(sketch, "E2382", {"start": v(-6.33, -2.77) * mm, "end": v(-6.34, -2.77) * mm});
            skLineSegment(sketch, "E2383", {"start": v(-6.34, -2.77) * mm, "end": v(-6.35, -2.77) * mm});
            skLineSegment(sketch, "E2384", {"start": v(-6.35, -2.77) * mm, "end": v(-6.37, -2.78) * mm});
            skLineSegment(sketch, "E2385", {"start": v(-6.37, -2.78) * mm, "end": v(-6.38, -2.78) * mm});
            skLineSegment(sketch, "E2386", {"start": v(-6.38, -2.78) * mm, "end": v(-6.4, -2.78) * mm});
            skLineSegment(sketch, "E2387", {"start": v(-6.4, -2.78) * mm, "end": v(-6.4, -2.78) * mm});
            skLineSegment(sketch, "E2388", {"start": v(-6.4, -2.78) * mm, "end": v(-6.42, -2.79) * mm});
            skLineSegment(sketch, "E2389", {"start": v(-6.42, -2.79) * mm, "end": v(-6.44, -2.79) * mm});
            skLineSegment(sketch, "E2390", {"start": v(-6.44, -2.79) * mm, "end": v(-6.46, -2.8) * mm});
            skLineSegment(sketch, "E2391", {"start": v(-6.46, -2.8) * mm, "end": v(-6.47, -2.8) * mm});
            skLineSegment(sketch, "E2392", {"start": v(-6.47, -2.8) * mm, "end": v(-6.5, -2.8) * mm});
            skLineSegment(sketch, "E2393", {"start": v(-6.5, -2.8) * mm, "end": v(-6.51, -2.8) * mm});
            skLineSegment(sketch, "E2394", {"start": v(-6.51, -2.8) * mm, "end": v(-6.53, -2.8) * mm});
            skLineSegment(sketch, "E2395", {"start": v(-6.53, -2.8) * mm, "end": v(-6.55, -2.8) * mm});
            skLineSegment(sketch, "E2396", {"start": v(-6.55, -2.8) * mm, "end": v(-6.57, -2.8) * mm});
            skLineSegment(sketch, "E2397", {"start": v(-6.57, -2.8) * mm, "end": v(-6.59, -2.8) * mm});
            skLineSegment(sketch, "E2398", {"start": v(-6.59, -2.8) * mm, "end": v(-6.6, -2.8) * mm});
            skLineSegment(sketch, "E2399", {"start": v(-6.6, -2.8) * mm, "end": v(-6.63, -2.8) * mm});
            skLineSegment(sketch, "E2400", {"start": v(-6.63, -2.8) * mm, "end": v(-6.65, -2.8) * mm});
            skLineSegment(sketch, "E2401", {"start": v(-6.65, -2.8) * mm, "end": v(-6.68, -2.8) * mm});
            skLineSegment(sketch, "E2402", {"start": v(-6.68, -2.8) * mm, "end": v(-6.7, -2.8) * mm});
            skLineSegment(sketch, "E2403", {"start": v(-6.7, -2.8) * mm, "end": v(-6.72, -2.8) * mm});
            skLineSegment(sketch, "E2404", {"start": v(-6.72, -2.8) * mm, "end": v(-6.75, -2.8) * mm});
            skLineSegment(sketch, "E2405", {"start": v(-6.75, -2.8) * mm, "end": v(-6.77, -2.8) * mm});
            skLineSegment(sketch, "E2406", {"start": v(-6.77, -2.8) * mm, "end": v(-6.8, -2.8) * mm});
            skLineSegment(sketch, "E2407", {"start": v(-6.8, -2.8) * mm, "end": v(-6.82, -2.8) * mm});
            skLineSegment(sketch, "E2408", {"start": v(-6.82, -2.8) * mm, "end": v(-6.85, -2.8) * mm});
            skLineSegment(sketch, "E2409", {"start": v(-6.85, -2.8) * mm, "end": v(-6.88, -2.8) * mm});
            skLineSegment(sketch, "E2410", {"start": v(-6.88, -2.8) * mm, "end": v(-6.9, -2.8) * mm});
            skLineSegment(sketch, "E2411", {"start": v(-6.9, -2.8) * mm, "end": v(-6.93, -2.8) * mm});
            skLineSegment(sketch, "E2412", {"start": v(-6.93, -2.8) * mm, "end": v(-6.96, -2.8) * mm});
            skLineSegment(sketch, "E2413", {"start": v(-6.96, -2.8) * mm, "end": v(-6.99, -2.8) * mm});
            skLineSegment(sketch, "E2414", {"start": v(-6.99, -2.8) * mm, "end": v(-7.02, -2.8) * mm});
            skLineSegment(sketch, "E2415", {"start": v(-7.02, -2.8) * mm, "end": v(-7.05, -2.8) * mm});
            skLineSegment(sketch, "E2416", {"start": v(-7.05, -2.8) * mm, "end": v(-7.08, -2.8) * mm});
            skLineSegment(sketch, "E2417", {"start": v(-7.08, -2.8) * mm, "end": v(-7.1, -2.8) * mm});
            skLineSegment(sketch, "E2418", {"start": v(-7.1, -2.8) * mm, "end": v(-7.14, -2.79) * mm});
            skLineSegment(sketch, "E2419", {"start": v(-7.14, -2.79) * mm, "end": v(-7.17, -2.78) * mm});
            skLineSegment(sketch, "E2420", {"start": v(-7.17, -2.78) * mm, "end": v(-7.2, -2.78) * mm});
            skLineSegment(sketch, "E2421", {"start": v(-7.2, -2.78) * mm, "end": v(-7.24, -2.77) * mm});
            skLineSegment(sketch, "E2422", {"start": v(-6.58, -1.9) * mm, "end": v(-6.58, -1.9) * mm});
            skLineSegment(sketch, "E2423", {"start": v(-6.58, -1.9) * mm, "end": v(-6.59, -1.9) * mm});
            skLineSegment(sketch, "E2424", {"start": v(-6.59, -1.9) * mm, "end": v(-6.59, -1.91) * mm});
            skLineSegment(sketch, "E2425", {"start": v(-6.59, -1.91) * mm, "end": v(-6.6, -1.92) * mm});
            skLineSegment(sketch, "E2426", {"start": v(-6.6, -1.92) * mm, "end": v(-6.6, -1.93) * mm});
            skLineSegment(sketch, "E2427", {"start": v(-6.6, -1.93) * mm, "end": v(-6.62, -1.94) * mm});
            skLineSegment(sketch, "E2428", {"start": v(-6.62, -1.94) * mm, "end": v(-6.63, -1.95) * mm});
            skLineSegment(sketch, "E2429", {"start": v(-6.63, -1.95) * mm, "end": v(-6.64, -1.95) * mm});
            skLineSegment(sketch, "E2430", {"start": v(-6.64, -1.95) * mm, "end": v(-6.65, -1.96) * mm});
            skLineSegment(sketch, "E2431", {"start": v(-6.65, -1.96) * mm, "end": v(-6.66, -1.96) * mm});
            skLineSegment(sketch, "E2432", {"start": v(-6.66, -1.96) * mm, "end": v(-6.67, -1.97) * mm});
            skLineSegment(sketch, "E2433", {"start": v(-6.67, -1.97) * mm, "end": v(-6.69, -1.98) * mm});
            skLineSegment(sketch, "E2434", {"start": v(-6.69, -1.98) * mm, "end": v(-6.7, -1.99) * mm});
            skLineSegment(sketch, "E2435", {"start": v(-6.7, -1.99) * mm, "end": v(-6.71, -2) * mm});
            skLineSegment(sketch, "E2436", {"start": v(-6.71, -2) * mm, "end": v(-6.73, -2) * mm});
            skLineSegment(sketch, "E2437", {"start": v(-6.73, -2) * mm, "end": v(-6.74, -2.01) * mm});
            skLineSegment(sketch, "E2438", {"start": v(-6.74, -2.01) * mm, "end": v(-6.75, -2.02) * mm});
            skLineSegment(sketch, "E2439", {"start": v(-6.75, -2.02) * mm, "end": v(-6.77, -2.03) * mm});
            skLineSegment(sketch, "E2440", {"start": v(-6.77, -2.03) * mm, "end": v(-6.78, -2.04) * mm});
            skLineSegment(sketch, "E2441", {"start": v(-6.78, -2.04) * mm, "end": v(-6.8, -2.05) * mm});
            skLineSegment(sketch, "E2442", {"start": v(-6.8, -2.05) * mm, "end": v(-6.82, -2.06) * mm});
            skLineSegment(sketch, "E2443", {"start": v(-6.82, -2.06) * mm, "end": v(-6.83, -2.08) * mm});
            skLineSegment(sketch, "E2444", {"start": v(-6.83, -2.08) * mm, "end": v(-6.85, -2.09) * mm});
            skLineSegment(sketch, "E2445", {"start": v(-6.85, -2.09) * mm, "end": v(-6.87, -2.1) * mm});
            skLineSegment(sketch, "E2446", {"start": v(-6.87, -2.1) * mm, "end": v(-6.88, -2.11) * mm});
            skLineSegment(sketch, "E2447", {"start": v(-6.88, -2.11) * mm, "end": v(-6.9, -2.13) * mm});
            skLineSegment(sketch, "E2448", {"start": v(-6.9, -2.13) * mm, "end": v(-6.92, -2.14) * mm});
            skLineSegment(sketch, "E2449", {"start": v(-6.92, -2.14) * mm, "end": v(-6.94, -2.15) * mm});
            skLineSegment(sketch, "E2450", {"start": v(-6.94, -2.15) * mm, "end": v(-6.96, -2.17) * mm});
            skLineSegment(sketch, "E2451", {"start": v(-6.96, -2.17) * mm, "end": v(-6.97, -2.18) * mm});
            skLineSegment(sketch, "E2452", {"start": v(-6.97, -2.18) * mm, "end": v(-7, -2.2) * mm});
            skLineSegment(sketch, "E2453", {"start": v(-7, -2.2) * mm, "end": v(-7.01, -2.22) * mm});
            skLineSegment(sketch, "E2454", {"start": v(-7.01, -2.22) * mm, "end": v(-7.03, -2.23) * mm});
            skLineSegment(sketch, "E2455", {"start": v(-7.03, -2.23) * mm, "end": v(-7.05, -2.25) * mm});
            skLineSegment(sketch, "E2456", {"start": v(-7.05, -2.25) * mm, "end": v(-7.07, -2.27) * mm});
            skLineSegment(sketch, "E2457", {"start": v(-7.07, -2.27) * mm, "end": v(-7.1, -2.29) * mm});
            skLineSegment(sketch, "E2458", {"start": v(-7.1, -2.29) * mm, "end": v(-7.11, -2.3) * mm});
            skLineSegment(sketch, "E2459", {"start": v(-7.11, -2.3) * mm, "end": v(-7.13, -2.33) * mm});
            skLineSegment(sketch, "E2460", {"start": v(-7.13, -2.33) * mm, "end": v(-7.15, -2.35) * mm});
            skLineSegment(sketch, "E2461", {"start": v(-7.15, -2.35) * mm, "end": v(-7.18, -2.37) * mm});
            skLineSegment(sketch, "E2462", {"start": v(-7.18, -2.37) * mm, "end": v(-7.2, -2.39) * mm});
            skLineSegment(sketch, "E2463", {"start": v(-7.2, -2.39) * mm, "end": v(-7.22, -2.41) * mm});
            skLineSegment(sketch, "E2464", {"start": v(-7.22, -2.41) * mm, "end": v(-7.24, -2.43) * mm});
            skLineSegment(sketch, "E2465", {"start": v(-7.24, -2.43) * mm, "end": v(-7.26, -2.46) * mm});
            skLineSegment(sketch, "E2466", {"start": v(-7.26, -2.46) * mm, "end": v(-7.28, -2.48) * mm});
            skLineSegment(sketch, "E2467", {"start": v(-7.28, -2.48) * mm, "end": v(-7.3, -2.5) * mm});
            skLineSegment(sketch, "E2468", {"start": v(-7.3, -2.5) * mm, "end": v(-7.33, -2.53) * mm});
            skArc(sketch, "E2469", {"start": v(-7.33, -2.53) * mm, "mid": v(-7.28, -2.65) * mm, "end": v(-7.24, -2.77) * mm});
            skLineSegment(sketch, "E2470", {"start": v(-6.65, -1.65) * mm, "end": v(-6.65, -1.65) * mm});
            skLineSegment(sketch, "E2471", {"start": v(-6.65, -1.65) * mm, "end": v(-6.66, -1.64) * mm});
            skLineSegment(sketch, "E2472", {"start": v(-6.66, -1.64) * mm, "end": v(-6.66, -1.64) * mm});
            skLineSegment(sketch, "E2473", {"start": v(-6.66, -1.64) * mm, "end": v(-6.67, -1.63) * mm});
            skLineSegment(sketch, "E2474", {"start": v(-6.67, -1.63) * mm, "end": v(-6.68, -1.63) * mm});
            skLineSegment(sketch, "E2475", {"start": v(-6.68, -1.63) * mm, "end": v(-6.7, -1.63) * mm});
            skLineSegment(sketch, "E2476", {"start": v(-6.7, -1.63) * mm, "end": v(-6.71, -1.63) * mm});
            skLineSegment(sketch, "E2477", {"start": v(-6.71, -1.63) * mm, "end": v(-6.72, -1.63) * mm});
            skLineSegment(sketch, "E2478", {"start": v(-6.72, -1.63) * mm, "end": v(-6.74, -1.63) * mm});
            skLineSegment(sketch, "E2479", {"start": v(-6.74, -1.63) * mm, "end": v(-6.75, -1.63) * mm});
            skLineSegment(sketch, "E2480", {"start": v(-6.75, -1.63) * mm, "end": v(-6.76, -1.63) * mm});
            skLineSegment(sketch, "E2481", {"start": v(-6.76, -1.63) * mm, "end": v(-6.78, -1.63) * mm});
            skLineSegment(sketch, "E2482", {"start": v(-6.78, -1.63) * mm, "end": v(-6.8, -1.63) * mm});
            skLineSegment(sketch, "E2483", {"start": v(-6.8, -1.63) * mm, "end": v(-6.81, -1.63) * mm});
            skLineSegment(sketch, "E2484", {"start": v(-6.81, -1.63) * mm, "end": v(-6.83, -1.63) * mm});
            skLineSegment(sketch, "E2485", {"start": v(-6.83, -1.63) * mm, "end": v(-6.84, -1.63) * mm});
            skLineSegment(sketch, "E2486", {"start": v(-6.84, -1.63) * mm, "end": v(-6.86, -1.63) * mm});
            skLineSegment(sketch, "E2487", {"start": v(-6.86, -1.63) * mm, "end": v(-6.88, -1.63) * mm});
            skLineSegment(sketch, "E2488", {"start": v(-6.88, -1.63) * mm, "end": v(-6.9, -1.62) * mm});
            skLineSegment(sketch, "E2489", {"start": v(-6.9, -1.62) * mm, "end": v(-6.92, -1.62) * mm});
            skLineSegment(sketch, "E2490", {"start": v(-6.92, -1.62) * mm, "end": v(-6.94, -1.62) * mm});
            skLineSegment(sketch, "E2491", {"start": v(-6.94, -1.62) * mm, "end": v(-6.96, -1.62) * mm});
            skLineSegment(sketch, "E2492", {"start": v(-6.96, -1.62) * mm, "end": v(-6.98, -1.62) * mm});
            skLineSegment(sketch, "E2493", {"start": v(-6.98, -1.62) * mm, "end": v(-7, -1.61) * mm});
            skLineSegment(sketch, "E2494", {"start": v(-7, -1.61) * mm, "end": v(-7.02, -1.61) * mm});
            skLineSegment(sketch, "E2495", {"start": v(-7.02, -1.61) * mm, "end": v(-7.04, -1.6) * mm});
            skLineSegment(sketch, "E2496", {"start": v(-7.04, -1.6) * mm, "end": v(-7.06, -1.6) * mm});
            skLineSegment(sketch, "E2497", {"start": v(-7.06, -1.6) * mm, "end": v(-7.09, -1.6) * mm});
            skLineSegment(sketch, "E2498", {"start": v(-7.09, -1.6) * mm, "end": v(-7.1, -1.6) * mm});
            skLineSegment(sketch, "E2499", {"start": v(-7.1, -1.6) * mm, "end": v(-7.13, -1.6) * mm});
            skLineSegment(sketch, "E2500", {"start": v(-7.13, -1.6) * mm, "end": v(-7.16, -1.6) * mm});
            skLineSegment(sketch, "E2501", {"start": v(-7.16, -1.6) * mm, "end": v(-7.18, -1.59) * mm});
            skLineSegment(sketch, "E2502", {"start": v(-7.18, -1.59) * mm, "end": v(-7.2, -1.58) * mm});
            skLineSegment(sketch, "E2503", {"start": v(-7.2, -1.58) * mm, "end": v(-7.23, -1.58) * mm});
            skLineSegment(sketch, "E2504", {"start": v(-7.23, -1.58) * mm, "end": v(-7.26, -1.57) * mm});
            skLineSegment(sketch, "E2505", {"start": v(-7.26, -1.57) * mm, "end": v(-7.29, -1.57) * mm});
            skLineSegment(sketch, "E2506", {"start": v(-7.29, -1.57) * mm, "end": v(-7.31, -1.56) * mm});
            skLineSegment(sketch, "E2507", {"start": v(-7.31, -1.56) * mm, "end": v(-7.34, -1.55) * mm});
            skLineSegment(sketch, "E2508", {"start": v(-7.34, -1.55) * mm, "end": v(-7.37, -1.55) * mm});
            skLineSegment(sketch, "E2509", {"start": v(-7.37, -1.55) * mm, "end": v(-7.4, -1.54) * mm});
            skLineSegment(sketch, "E2510", {"start": v(-7.4, -1.54) * mm, "end": v(-7.43, -1.53) * mm});
            skLineSegment(sketch, "E2511", {"start": v(-7.43, -1.53) * mm, "end": v(-7.46, -1.52) * mm});
            skLineSegment(sketch, "E2512", {"start": v(-7.46, -1.52) * mm, "end": v(-7.49, -1.51) * mm});
            skLineSegment(sketch, "E2513", {"start": v(-7.49, -1.51) * mm, "end": v(-7.52, -1.5) * mm});
            skLineSegment(sketch, "E2514", {"start": v(-7.52, -1.5) * mm, "end": v(-7.55, -1.5) * mm});
            skLineSegment(sketch, "E2515", {"start": v(-7.55, -1.5) * mm, "end": v(-7.58, -1.49) * mm});
            skLineSegment(sketch, "E2516", {"start": v(-7.58, -1.49) * mm, "end": v(-7.61, -1.47) * mm});
            skLineSegment(sketch, "E2517", {"start": v(-6.81, -0.72) * mm, "end": v(-6.81, -0.73) * mm});
            skLineSegment(sketch, "E2518", {"start": v(-6.81, -0.73) * mm, "end": v(-6.82, -0.73) * mm});
            skLineSegment(sketch, "E2519", {"start": v(-6.82, -0.73) * mm, "end": v(-6.82, -0.74) * mm});
            skLineSegment(sketch, "E2520", {"start": v(-6.82, -0.74) * mm, "end": v(-6.83, -0.75) * mm});
            skLineSegment(sketch, "E2521", {"start": v(-6.83, -0.75) * mm, "end": v(-6.84, -0.75) * mm});
            skLineSegment(sketch, "E2522", {"start": v(-6.84, -0.75) * mm, "end": v(-6.85, -0.76) * mm});
            skLineSegment(sketch, "E2523", {"start": v(-6.85, -0.76) * mm, "end": v(-6.87, -0.77) * mm});
            skLineSegment(sketch, "E2524", {"start": v(-6.87, -0.77) * mm, "end": v(-6.88, -0.77) * mm});
            skLineSegment(sketch, "E2525", {"start": v(-6.88, -0.77) * mm, "end": v(-6.89, -0.77) * mm});
            skLineSegment(sketch, "E2526", {"start": v(-6.89, -0.77) * mm, "end": v(-6.9, -0.78) * mm});
            skLineSegment(sketch, "E2527", {"start": v(-6.9, -0.78) * mm, "end": v(-6.91, -0.78) * mm});
            skLineSegment(sketch, "E2528", {"start": v(-6.91, -0.78) * mm, "end": v(-6.93, -0.79) * mm});
            skLineSegment(sketch, "E2529", {"start": v(-6.93, -0.79) * mm, "end": v(-6.94, -0.8) * mm});
            skLineSegment(sketch, "E2530", {"start": v(-6.94, -0.8) * mm, "end": v(-6.96, -0.8) * mm});
            skLineSegment(sketch, "E2531", {"start": v(-6.96, -0.8) * mm, "end": v(-6.97, -0.8) * mm});
            skLineSegment(sketch, "E2532", {"start": v(-6.97, -0.8) * mm, "end": v(-6.99, -0.81) * mm});
            skLineSegment(sketch, "E2533", {"start": v(-6.99, -0.81) * mm, "end": v(-7, -0.82) * mm});
            skLineSegment(sketch, "E2534", {"start": v(-7, -0.82) * mm, "end": v(-7.02, -0.83) * mm});
            skLineSegment(sketch, "E2535", {"start": v(-7.02, -0.83) * mm, "end": v(-7.04, -0.83) * mm});
            skLineSegment(sketch, "E2536", {"start": v(-7.04, -0.83) * mm, "end": v(-7.05, -0.84) * mm});
            skLineSegment(sketch, "E2537", {"start": v(-7.05, -0.84) * mm, "end": v(-7.07, -0.85) * mm});
            skLineSegment(sketch, "E2538", {"start": v(-7.07, -0.85) * mm, "end": v(-7.09, -0.86) * mm});
            skLineSegment(sketch, "E2539", {"start": v(-7.09, -0.86) * mm, "end": v(-7.1, -0.87) * mm});
            skLineSegment(sketch, "E2540", {"start": v(-7.1, -0.87) * mm, "end": v(-7.13, -0.88) * mm});
            skLineSegment(sketch, "E2541", {"start": v(-7.13, -0.88) * mm, "end": v(-7.15, -0.89) * mm});
            skLineSegment(sketch, "E2542", {"start": v(-7.15, -0.89) * mm, "end": v(-7.17, -0.9) * mm});
            skLineSegment(sketch, "E2543", {"start": v(-7.17, -0.9) * mm, "end": v(-7.19, -0.9) * mm});
            skLineSegment(sketch, "E2544", {"start": v(-7.19, -0.9) * mm, "end": v(-7.2, -0.92) * mm});
            skLineSegment(sketch, "E2545", {"start": v(-7.2, -0.92) * mm, "end": v(-7.23, -0.93) * mm});
            skLineSegment(sketch, "E2546", {"start": v(-7.23, -0.93) * mm, "end": v(-7.25, -0.94) * mm});
            skLineSegment(sketch, "E2547", {"start": v(-7.25, -0.94) * mm, "end": v(-7.27, -0.95) * mm});
            skLineSegment(sketch, "E2548", {"start": v(-7.27, -0.95) * mm, "end": v(-7.3, -0.97) * mm});
            skLineSegment(sketch, "E2549", {"start": v(-7.3, -0.97) * mm, "end": v(-7.31, -0.98) * mm});
            skLineSegment(sketch, "E2550", {"start": v(-7.31, -0.98) * mm, "end": v(-7.34, -1) * mm});
            skLineSegment(sketch, "E2551", {"start": v(-7.34, -1) * mm, "end": v(-7.36, -1) * mm});
            skLineSegment(sketch, "E2552", {"start": v(-7.36, -1) * mm, "end": v(-7.38, -1.02) * mm});
            skLineSegment(sketch, "E2553", {"start": v(-7.38, -1.02) * mm, "end": v(-7.4, -1.04) * mm});
            skLineSegment(sketch, "E2554", {"start": v(-7.4, -1.04) * mm, "end": v(-7.43, -1.05) * mm});
            skLineSegment(sketch, "E2555", {"start": v(-7.43, -1.05) * mm, "end": v(-7.45, -1.07) * mm});
            skLineSegment(sketch, "E2556", {"start": v(-7.45, -1.07) * mm, "end": v(-7.48, -1.09) * mm});
            skLineSegment(sketch, "E2557", {"start": v(-7.48, -1.09) * mm, "end": v(-7.5, -1.1) * mm});
            skLineSegment(sketch, "E2558", {"start": v(-7.5, -1.1) * mm, "end": v(-7.53, -1.12) * mm});
            skLineSegment(sketch, "E2559", {"start": v(-7.53, -1.12) * mm, "end": v(-7.55, -1.14) * mm});
            skLineSegment(sketch, "E2560", {"start": v(-7.55, -1.14) * mm, "end": v(-7.58, -1.16) * mm});
            skLineSegment(sketch, "E2561", {"start": v(-7.58, -1.16) * mm, "end": v(-7.6, -1.18) * mm});
            skLineSegment(sketch, "E2562", {"start": v(-7.6, -1.18) * mm, "end": v(-7.63, -1.2) * mm});
            skLineSegment(sketch, "E2563", {"start": v(-7.63, -1.2) * mm, "end": v(-7.66, -1.22) * mm});
            skArc(sketch, "E2564", {"start": v(-7.66, -1.22) * mm, "mid": v(-7.63, -1.35) * mm, "end": v(-7.61, -1.47) * mm});
            skLineSegment(sketch, "E2565", {"start": v(-6.84, -0.47) * mm, "end": v(-6.84, -0.47) * mm});
            skLineSegment(sketch, "E2566", {"start": v(-6.84, -0.47) * mm, "end": v(-6.84, -0.46) * mm});
            skLineSegment(sketch, "E2567", {"start": v(-6.84, -0.46) * mm, "end": v(-6.85, -0.45) * mm});
            skLineSegment(sketch, "E2568", {"start": v(-6.85, -0.45) * mm, "end": v(-6.86, -0.45) * mm});
            skLineSegment(sketch, "E2569", {"start": v(-6.86, -0.45) * mm, "end": v(-6.87, -0.45) * mm});
            skLineSegment(sketch, "E2570", {"start": v(-6.87, -0.45) * mm, "end": v(-6.88, -0.44) * mm});
            skLineSegment(sketch, "E2571", {"start": v(-6.88, -0.44) * mm, "end": v(-6.9, -0.44) * mm});
            skLineSegment(sketch, "E2572", {"start": v(-6.9, -0.44) * mm, "end": v(-6.9, -0.44) * mm});
            skLineSegment(sketch, "E2573", {"start": v(-6.9, -0.44) * mm, "end": v(-6.92, -0.43) * mm});
            skLineSegment(sketch, "E2574", {"start": v(-6.92, -0.43) * mm, "end": v(-6.93, -0.43) * mm});
            skLineSegment(sketch, "E2575", {"start": v(-6.93, -0.43) * mm, "end": v(-6.94, -0.43) * mm});
            skLineSegment(sketch, "E2576", {"start": v(-6.94, -0.43) * mm, "end": v(-6.96, -0.43) * mm});
            skLineSegment(sketch, "E2577", {"start": v(-6.96, -0.43) * mm, "end": v(-6.97, -0.42) * mm});
            skLineSegment(sketch, "E2578", {"start": v(-6.97, -0.42) * mm, "end": v(-6.99, -0.42) * mm});
            skLineSegment(sketch, "E2579", {"start": v(-6.99, -0.42) * mm, "end": v(-7, -0.42) * mm});
            skLineSegment(sketch, "E2580", {"start": v(-7, -0.42) * mm, "end": v(-7.02, -0.41) * mm});
            skLineSegment(sketch, "E2581", {"start": v(-7.02, -0.41) * mm, "end": v(-7.04, -0.41) * mm});
            skLineSegment(sketch, "E2582", {"start": v(-7.04, -0.41) * mm, "end": v(-7.06, -0.4) * mm});
            skLineSegment(sketch, "E2583", {"start": v(-7.06, -0.4) * mm, "end": v(-7.07, -0.4) * mm});
            skLineSegment(sketch, "E2584", {"start": v(-7.07, -0.4) * mm, "end": v(-7.1, -0.4) * mm});
            skLineSegment(sketch, "E2585", {"start": v(-7.1, -0.4) * mm, "end": v(-7.11, -0.4) * mm});
            skLineSegment(sketch, "E2586", {"start": v(-7.11, -0.4) * mm, "end": v(-7.13, -0.39) * mm});
            skLineSegment(sketch, "E2587", {"start": v(-7.13, -0.39) * mm, "end": v(-7.15, -0.38) * mm});
            skLineSegment(sketch, "E2588", {"start": v(-7.15, -0.38) * mm, "end": v(-7.17, -0.38) * mm});
            skLineSegment(sketch, "E2589", {"start": v(-7.17, -0.38) * mm, "end": v(-7.2, -0.37) * mm});
            skLineSegment(sketch, "E2590", {"start": v(-7.2, -0.37) * mm, "end": v(-7.21, -0.36) * mm});
            skLineSegment(sketch, "E2591", {"start": v(-7.21, -0.36) * mm, "end": v(-7.23, -0.36) * mm});
            skLineSegment(sketch, "E2592", {"start": v(-7.23, -0.36) * mm, "end": v(-7.26, -0.35) * mm});
            skLineSegment(sketch, "E2593", {"start": v(-7.26, -0.35) * mm, "end": v(-7.28, -0.34) * mm});
            skLineSegment(sketch, "E2594", {"start": v(-7.28, -0.34) * mm, "end": v(-7.3, -0.33) * mm});
            skLineSegment(sketch, "E2595", {"start": v(-7.3, -0.33) * mm, "end": v(-7.32, -0.32) * mm});
            skLineSegment(sketch, "E2596", {"start": v(-7.32, -0.32) * mm, "end": v(-7.35, -0.32) * mm});
            skLineSegment(sketch, "E2597", {"start": v(-7.35, -0.32) * mm, "end": v(-7.37, -0.3) * mm});
            skLineSegment(sketch, "E2598", {"start": v(-7.37, -0.3) * mm, "end": v(-7.4, -0.3) * mm});
            skLineSegment(sketch, "E2599", {"start": v(-7.4, -0.3) * mm, "end": v(-7.42, -0.29) * mm});
            skLineSegment(sketch, "E2600", {"start": v(-7.42, -0.29) * mm, "end": v(-7.45, -0.28) * mm});
            skLineSegment(sketch, "E2601", {"start": v(-7.45, -0.28) * mm, "end": v(-7.47, -0.27) * mm});
            skLineSegment(sketch, "E2602", {"start": v(-7.47, -0.27) * mm, "end": v(-7.5, -0.25) * mm});
            skLineSegment(sketch, "E2603", {"start": v(-7.5, -0.25) * mm, "end": v(-7.53, -0.24) * mm});
            skLineSegment(sketch, "E2604", {"start": v(-7.53, -0.24) * mm, "end": v(-7.55, -0.23) * mm});
            skLineSegment(sketch, "E2605", {"start": v(-7.55, -0.23) * mm, "end": v(-7.58, -0.22) * mm});
            skLineSegment(sketch, "E2606", {"start": v(-7.58, -0.22) * mm, "end": v(-7.6, -0.2) * mm});
            skLineSegment(sketch, "E2607", {"start": v(-7.6, -0.2) * mm, "end": v(-7.64, -0.2) * mm});
            skLineSegment(sketch, "E2608", {"start": v(-7.64, -0.2) * mm, "end": v(-7.66, -0.18) * mm});
            skLineSegment(sketch, "E2609", {"start": v(-7.66, -0.18) * mm, "end": v(-7.7, -0.16) * mm});
            skLineSegment(sketch, "E2610", {"start": v(-7.7, -0.16) * mm, "end": v(-7.72, -0.15) * mm});
            skLineSegment(sketch, "E2611", {"start": v(-7.72, -0.15) * mm, "end": v(-7.75, -0.13) * mm});
            skLineSegment(sketch, "E2612", {"start": v(-6.84, 0.47) * mm, "end": v(-6.84, 0.47) * mm});
            skLineSegment(sketch, "E2613", {"start": v(-6.84, 0.47) * mm, "end": v(-6.84, 0.46) * mm});
            skLineSegment(sketch, "E2614", {"start": v(-6.84, 0.46) * mm, "end": v(-6.85, 0.45) * mm});
            skLineSegment(sketch, "E2615", {"start": v(-6.85, 0.45) * mm, "end": v(-6.86, 0.45) * mm});
            skLineSegment(sketch, "E2616", {"start": v(-6.86, 0.45) * mm, "end": v(-6.87, 0.45) * mm});
            skLineSegment(sketch, "E2617", {"start": v(-6.87, 0.45) * mm, "end": v(-6.88, 0.44) * mm});
            skLineSegment(sketch, "E2618", {"start": v(-6.88, 0.44) * mm, "end": v(-6.9, 0.44) * mm});
            skLineSegment(sketch, "E2619", {"start": v(-6.9, 0.44) * mm, "end": v(-6.9, 0.44) * mm});
            skLineSegment(sketch, "E2620", {"start": v(-6.9, 0.44) * mm, "end": v(-6.92, 0.43) * mm});
            skLineSegment(sketch, "E2621", {"start": v(-6.92, 0.43) * mm, "end": v(-6.93, 0.43) * mm});
            skLineSegment(sketch, "E2622", {"start": v(-6.93, 0.43) * mm, "end": v(-6.94, 0.43) * mm});
            skLineSegment(sketch, "E2623", {"start": v(-6.94, 0.43) * mm, "end": v(-6.96, 0.43) * mm});
            skLineSegment(sketch, "E2624", {"start": v(-6.96, 0.43) * mm, "end": v(-6.97, 0.42) * mm});
            skLineSegment(sketch, "E2625", {"start": v(-6.97, 0.42) * mm, "end": v(-6.99, 0.42) * mm});
            skLineSegment(sketch, "E2626", {"start": v(-6.99, 0.42) * mm, "end": v(-7, 0.42) * mm});
            skLineSegment(sketch, "E2627", {"start": v(-7, 0.42) * mm, "end": v(-7.02, 0.41) * mm});
            skLineSegment(sketch, "E2628", {"start": v(-7.02, 0.41) * mm, "end": v(-7.04, 0.41) * mm});
            skLineSegment(sketch, "E2629", {"start": v(-7.04, 0.41) * mm, "end": v(-7.06, 0.4) * mm});
            skLineSegment(sketch, "E2630", {"start": v(-7.06, 0.4) * mm, "end": v(-7.07, 0.4) * mm});
            skLineSegment(sketch, "E2631", {"start": v(-7.07, 0.4) * mm, "end": v(-7.1, 0.4) * mm});
            skLineSegment(sketch, "E2632", {"start": v(-7.1, 0.4) * mm, "end": v(-7.11, 0.4) * mm});
            skLineSegment(sketch, "E2633", {"start": v(-7.11, 0.4) * mm, "end": v(-7.13, 0.39) * mm});
            skLineSegment(sketch, "E2634", {"start": v(-7.13, 0.39) * mm, "end": v(-7.15, 0.38) * mm});
            skLineSegment(sketch, "E2635", {"start": v(-7.15, 0.38) * mm, "end": v(-7.17, 0.38) * mm});
            skLineSegment(sketch, "E2636", {"start": v(-7.17, 0.38) * mm, "end": v(-7.2, 0.37) * mm});
            skLineSegment(sketch, "E2637", {"start": v(-7.2, 0.37) * mm, "end": v(-7.21, 0.36) * mm});
            skLineSegment(sketch, "E2638", {"start": v(-7.21, 0.36) * mm, "end": v(-7.23, 0.36) * mm});
            skLineSegment(sketch, "E2639", {"start": v(-7.23, 0.36) * mm, "end": v(-7.26, 0.35) * mm});
            skLineSegment(sketch, "E2640", {"start": v(-7.26, 0.35) * mm, "end": v(-7.28, 0.34) * mm});
            skLineSegment(sketch, "E2641", {"start": v(-7.28, 0.34) * mm, "end": v(-7.3, 0.33) * mm});
            skLineSegment(sketch, "E2642", {"start": v(-7.3, 0.33) * mm, "end": v(-7.32, 0.32) * mm});
            skLineSegment(sketch, "E2643", {"start": v(-7.32, 0.32) * mm, "end": v(-7.35, 0.32) * mm});
            skLineSegment(sketch, "E2644", {"start": v(-7.35, 0.32) * mm, "end": v(-7.37, 0.3) * mm});
            skLineSegment(sketch, "E2645", {"start": v(-7.37, 0.3) * mm, "end": v(-7.4, 0.3) * mm});
            skLineSegment(sketch, "E2646", {"start": v(-7.4, 0.3) * mm, "end": v(-7.42, 0.29) * mm});
            skLineSegment(sketch, "E2647", {"start": v(-7.42, 0.29) * mm, "end": v(-7.45, 0.28) * mm});
            skLineSegment(sketch, "E2648", {"start": v(-7.45, 0.28) * mm, "end": v(-7.47, 0.27) * mm});
            skLineSegment(sketch, "E2649", {"start": v(-7.47, 0.27) * mm, "end": v(-7.5, 0.25) * mm});
            skLineSegment(sketch, "E2650", {"start": v(-7.5, 0.25) * mm, "end": v(-7.53, 0.24) * mm});
            skLineSegment(sketch, "E2651", {"start": v(-7.53, 0.24) * mm, "end": v(-7.55, 0.23) * mm});
            skLineSegment(sketch, "E2652", {"start": v(-7.55, 0.23) * mm, "end": v(-7.58, 0.22) * mm});
            skLineSegment(sketch, "E2653", {"start": v(-7.58, 0.22) * mm, "end": v(-7.6, 0.2) * mm});
            skLineSegment(sketch, "E2654", {"start": v(-7.6, 0.2) * mm, "end": v(-7.64, 0.2) * mm});
            skLineSegment(sketch, "E2655", {"start": v(-7.64, 0.2) * mm, "end": v(-7.66, 0.18) * mm});
            skLineSegment(sketch, "E2656", {"start": v(-7.66, 0.18) * mm, "end": v(-7.7, 0.16) * mm});
            skLineSegment(sketch, "E2657", {"start": v(-7.7, 0.16) * mm, "end": v(-7.72, 0.15) * mm});
            skLineSegment(sketch, "E2658", {"start": v(-7.72, 0.15) * mm, "end": v(-7.75, 0.13) * mm});
            skArc(sketch, "E2659", {"start": v(-7.75, 0.13) * mm, "mid": v(-7.75, 0) * mm, "end": v(-7.75, -0.13) * mm});
            skLineSegment(sketch, "E2660", {"start": v(-6.81, 0.72) * mm, "end": v(-6.81, 0.73) * mm});
            skLineSegment(sketch, "E2661", {"start": v(-6.81, 0.73) * mm, "end": v(-6.82, 0.73) * mm});
            skLineSegment(sketch, "E2662", {"start": v(-6.82, 0.73) * mm, "end": v(-6.82, 0.74) * mm});
            skLineSegment(sketch, "E2663", {"start": v(-6.82, 0.74) * mm, "end": v(-6.83, 0.75) * mm});
            skLineSegment(sketch, "E2664", {"start": v(-6.83, 0.75) * mm, "end": v(-6.84, 0.75) * mm});
            skLineSegment(sketch, "E2665", {"start": v(-6.84, 0.75) * mm, "end": v(-6.85, 0.76) * mm});
            skLineSegment(sketch, "E2666", {"start": v(-6.85, 0.76) * mm, "end": v(-6.87, 0.77) * mm});
            skLineSegment(sketch, "E2667", {"start": v(-6.87, 0.77) * mm, "end": v(-6.88, 0.77) * mm});
            skLineSegment(sketch, "E2668", {"start": v(-6.88, 0.77) * mm, "end": v(-6.89, 0.77) * mm});
            skLineSegment(sketch, "E2669", {"start": v(-6.89, 0.77) * mm, "end": v(-6.9, 0.78) * mm});
            skLineSegment(sketch, "E2670", {"start": v(-6.9, 0.78) * mm, "end": v(-6.91, 0.78) * mm});
            skLineSegment(sketch, "E2671", {"start": v(-6.91, 0.78) * mm, "end": v(-6.93, 0.79) * mm});
            skLineSegment(sketch, "E2672", {"start": v(-6.93, 0.79) * mm, "end": v(-6.94, 0.8) * mm});
            skLineSegment(sketch, "E2673", {"start": v(-6.94, 0.8) * mm, "end": v(-6.96, 0.8) * mm});
            skLineSegment(sketch, "E2674", {"start": v(-6.96, 0.8) * mm, "end": v(-6.97, 0.8) * mm});
            skLineSegment(sketch, "E2675", {"start": v(-6.97, 0.8) * mm, "end": v(-6.99, 0.81) * mm});
            skLineSegment(sketch, "E2676", {"start": v(-6.99, 0.81) * mm, "end": v(-7, 0.82) * mm});
            skLineSegment(sketch, "E2677", {"start": v(-7, 0.82) * mm, "end": v(-7.02, 0.83) * mm});
            skLineSegment(sketch, "E2678", {"start": v(-7.02, 0.83) * mm, "end": v(-7.04, 0.83) * mm});
            skLineSegment(sketch, "E2679", {"start": v(-7.04, 0.83) * mm, "end": v(-7.05, 0.84) * mm});
            skLineSegment(sketch, "E2680", {"start": v(-7.05, 0.84) * mm, "end": v(-7.07, 0.85) * mm});
            skLineSegment(sketch, "E2681", {"start": v(-7.07, 0.85) * mm, "end": v(-7.09, 0.86) * mm});
            skLineSegment(sketch, "E2682", {"start": v(-7.09, 0.86) * mm, "end": v(-7.1, 0.87) * mm});
            skLineSegment(sketch, "E2683", {"start": v(-7.1, 0.87) * mm, "end": v(-7.13, 0.88) * mm});
            skLineSegment(sketch, "E2684", {"start": v(-7.13, 0.88) * mm, "end": v(-7.15, 0.89) * mm});
            skLineSegment(sketch, "E2685", {"start": v(-7.15, 0.89) * mm, "end": v(-7.17, 0.9) * mm});
            skLineSegment(sketch, "E2686", {"start": v(-7.17, 0.9) * mm, "end": v(-7.19, 0.9) * mm});
            skLineSegment(sketch, "E2687", {"start": v(-7.19, 0.9) * mm, "end": v(-7.2, 0.92) * mm});
            skLineSegment(sketch, "E2688", {"start": v(-7.2, 0.92) * mm, "end": v(-7.23, 0.93) * mm});
            skLineSegment(sketch, "E2689", {"start": v(-7.23, 0.93) * mm, "end": v(-7.25, 0.94) * mm});
            skLineSegment(sketch, "E2690", {"start": v(-7.25, 0.94) * mm, "end": v(-7.27, 0.95) * mm});
            skLineSegment(sketch, "E2691", {"start": v(-7.27, 0.95) * mm, "end": v(-7.3, 0.97) * mm});
            skLineSegment(sketch, "E2692", {"start": v(-7.3, 0.97) * mm, "end": v(-7.31, 0.98) * mm});
            skLineSegment(sketch, "E2693", {"start": v(-7.31, 0.98) * mm, "end": v(-7.34, 1) * mm});
            skLineSegment(sketch, "E2694", {"start": v(-7.34, 1) * mm, "end": v(-7.36, 1) * mm});
            skLineSegment(sketch, "E2695", {"start": v(-7.36, 1) * mm, "end": v(-7.38, 1.02) * mm});
            skLineSegment(sketch, "E2696", {"start": v(-7.38, 1.02) * mm, "end": v(-7.4, 1.04) * mm});
            skLineSegment(sketch, "E2697", {"start": v(-7.4, 1.04) * mm, "end": v(-7.43, 1.05) * mm});
            skLineSegment(sketch, "E2698", {"start": v(-7.43, 1.05) * mm, "end": v(-7.45, 1.07) * mm});
            skLineSegment(sketch, "E2699", {"start": v(-7.45, 1.07) * mm, "end": v(-7.48, 1.09) * mm});
            skLineSegment(sketch, "E2700", {"start": v(-7.48, 1.09) * mm, "end": v(-7.5, 1.1) * mm});
            skLineSegment(sketch, "E2701", {"start": v(-7.5, 1.1) * mm, "end": v(-7.53, 1.12) * mm});
            skLineSegment(sketch, "E2702", {"start": v(-7.53, 1.12) * mm, "end": v(-7.55, 1.14) * mm});
            skLineSegment(sketch, "E2703", {"start": v(-7.55, 1.14) * mm, "end": v(-7.58, 1.16) * mm});
            skLineSegment(sketch, "E2704", {"start": v(-7.58, 1.16) * mm, "end": v(-7.6, 1.18) * mm});
            skLineSegment(sketch, "E2705", {"start": v(-7.6, 1.18) * mm, "end": v(-7.63, 1.2) * mm});
            skLineSegment(sketch, "E2706", {"start": v(-7.63, 1.2) * mm, "end": v(-7.66, 1.22) * mm});
            skLineSegment(sketch, "E2707", {"start": v(-6.65, 1.65) * mm, "end": v(-6.65, 1.65) * mm});
            skLineSegment(sketch, "E2708", {"start": v(-6.65, 1.65) * mm, "end": v(-6.66, 1.64) * mm});
            skLineSegment(sketch, "E2709", {"start": v(-6.66, 1.64) * mm, "end": v(-6.66, 1.64) * mm});
            skLineSegment(sketch, "E2710", {"start": v(-6.66, 1.64) * mm, "end": v(-6.67, 1.63) * mm});
            skLineSegment(sketch, "E2711", {"start": v(-6.67, 1.63) * mm, "end": v(-6.68, 1.63) * mm});
            skLineSegment(sketch, "E2712", {"start": v(-6.68, 1.63) * mm, "end": v(-6.7, 1.63) * mm});
            skLineSegment(sketch, "E2713", {"start": v(-6.7, 1.63) * mm, "end": v(-6.71, 1.63) * mm});
            skLineSegment(sketch, "E2714", {"start": v(-6.71, 1.63) * mm, "end": v(-6.72, 1.63) * mm});
            skLineSegment(sketch, "E2715", {"start": v(-6.72, 1.63) * mm, "end": v(-6.74, 1.63) * mm});
            skLineSegment(sketch, "E2716", {"start": v(-6.74, 1.63) * mm, "end": v(-6.75, 1.63) * mm});
            skLineSegment(sketch, "E2717", {"start": v(-6.75, 1.63) * mm, "end": v(-6.76, 1.63) * mm});
            skLineSegment(sketch, "E2718", {"start": v(-6.76, 1.63) * mm, "end": v(-6.78, 1.63) * mm});
            skLineSegment(sketch, "E2719", {"start": v(-6.78, 1.63) * mm, "end": v(-6.8, 1.63) * mm});
            skLineSegment(sketch, "E2720", {"start": v(-6.8, 1.63) * mm, "end": v(-6.81, 1.63) * mm});
            skLineSegment(sketch, "E2721", {"start": v(-6.81, 1.63) * mm, "end": v(-6.83, 1.63) * mm});
            skLineSegment(sketch, "E2722", {"start": v(-6.83, 1.63) * mm, "end": v(-6.84, 1.63) * mm});
            skLineSegment(sketch, "E2723", {"start": v(-6.84, 1.63) * mm, "end": v(-6.86, 1.63) * mm});
            skLineSegment(sketch, "E2724", {"start": v(-6.86, 1.63) * mm, "end": v(-6.88, 1.63) * mm});
            skLineSegment(sketch, "E2725", {"start": v(-6.88, 1.63) * mm, "end": v(-6.9, 1.62) * mm});
            skLineSegment(sketch, "E2726", {"start": v(-6.9, 1.62) * mm, "end": v(-6.92, 1.62) * mm});
            skLineSegment(sketch, "E2727", {"start": v(-6.92, 1.62) * mm, "end": v(-6.94, 1.62) * mm});
            skLineSegment(sketch, "E2728", {"start": v(-6.94, 1.62) * mm, "end": v(-6.96, 1.62) * mm});
            skLineSegment(sketch, "E2729", {"start": v(-6.96, 1.62) * mm, "end": v(-6.98, 1.62) * mm});
            skLineSegment(sketch, "E2730", {"start": v(-6.98, 1.62) * mm, "end": v(-7, 1.61) * mm});
            skLineSegment(sketch, "E2731", {"start": v(-7, 1.61) * mm, "end": v(-7.02, 1.61) * mm});
            skLineSegment(sketch, "E2732", {"start": v(-7.02, 1.61) * mm, "end": v(-7.04, 1.6) * mm});
            skLineSegment(sketch, "E2733", {"start": v(-7.04, 1.6) * mm, "end": v(-7.06, 1.6) * mm});
            skLineSegment(sketch, "E2734", {"start": v(-7.06, 1.6) * mm, "end": v(-7.09, 1.6) * mm});
            skLineSegment(sketch, "E2735", {"start": v(-7.09, 1.6) * mm, "end": v(-7.1, 1.6) * mm});
            skLineSegment(sketch, "E2736", {"start": v(-7.1, 1.6) * mm, "end": v(-7.13, 1.6) * mm});
            skLineSegment(sketch, "E2737", {"start": v(-7.13, 1.6) * mm, "end": v(-7.16, 1.6) * mm});
            skLineSegment(sketch, "E2738", {"start": v(-7.16, 1.6) * mm, "end": v(-7.18, 1.59) * mm});
            skLineSegment(sketch, "E2739", {"start": v(-7.18, 1.59) * mm, "end": v(-7.2, 1.58) * mm});
            skLineSegment(sketch, "E2740", {"start": v(-7.2, 1.58) * mm, "end": v(-7.23, 1.58) * mm});
            skLineSegment(sketch, "E2741", {"start": v(-7.23, 1.58) * mm, "end": v(-7.26, 1.57) * mm});
            skLineSegment(sketch, "E2742", {"start": v(-7.26, 1.57) * mm, "end": v(-7.29, 1.57) * mm});
            skLineSegment(sketch, "E2743", {"start": v(-7.29, 1.57) * mm, "end": v(-7.31, 1.56) * mm});
            skLineSegment(sketch, "E2744", {"start": v(-7.31, 1.56) * mm, "end": v(-7.34, 1.55) * mm});
            skLineSegment(sketch, "E2745", {"start": v(-7.34, 1.55) * mm, "end": v(-7.37, 1.55) * mm});
            skLineSegment(sketch, "E2746", {"start": v(-7.37, 1.55) * mm, "end": v(-7.4, 1.54) * mm});
            skLineSegment(sketch, "E2747", {"start": v(-7.4, 1.54) * mm, "end": v(-7.43, 1.53) * mm});
            skLineSegment(sketch, "E2748", {"start": v(-7.43, 1.53) * mm, "end": v(-7.46, 1.52) * mm});
            skLineSegment(sketch, "E2749", {"start": v(-7.46, 1.52) * mm, "end": v(-7.49, 1.51) * mm});
            skLineSegment(sketch, "E2750", {"start": v(-7.49, 1.51) * mm, "end": v(-7.52, 1.5) * mm});
            skLineSegment(sketch, "E2751", {"start": v(-7.52, 1.5) * mm, "end": v(-7.55, 1.5) * mm});
            skLineSegment(sketch, "E2752", {"start": v(-7.55, 1.5) * mm, "end": v(-7.58, 1.49) * mm});
            skLineSegment(sketch, "E2753", {"start": v(-7.58, 1.49) * mm, "end": v(-7.61, 1.47) * mm});
            skArc(sketch, "E2754", {"start": v(-7.61, 1.47) * mm, "mid": v(-7.63, 1.35) * mm, "end": v(-7.66, 1.22) * mm});
            skLineSegment(sketch, "E2755", {"start": v(-6.58, 1.9) * mm, "end": v(-6.58, 1.9) * mm});
            skLineSegment(sketch, "E2756", {"start": v(-6.58, 1.9) * mm, "end": v(-6.59, 1.9) * mm});
            skLineSegment(sketch, "E2757", {"start": v(-6.59, 1.9) * mm, "end": v(-6.59, 1.91) * mm});
            skLineSegment(sketch, "E2758", {"start": v(-6.59, 1.91) * mm, "end": v(-6.6, 1.92) * mm});
            skLineSegment(sketch, "E2759", {"start": v(-6.6, 1.92) * mm, "end": v(-6.6, 1.93) * mm});
            skLineSegment(sketch, "E2760", {"start": v(-6.6, 1.93) * mm, "end": v(-6.62, 1.94) * mm});
            skLineSegment(sketch, "E2761", {"start": v(-6.62, 1.94) * mm, "end": v(-6.63, 1.95) * mm});
            skLineSegment(sketch, "E2762", {"start": v(-6.63, 1.95) * mm, "end": v(-6.64, 1.95) * mm});
            skLineSegment(sketch, "E2763", {"start": v(-6.64, 1.95) * mm, "end": v(-6.65, 1.96) * mm});
            skLineSegment(sketch, "E2764", {"start": v(-6.65, 1.96) * mm, "end": v(-6.66, 1.96) * mm});
            skLineSegment(sketch, "E2765", {"start": v(-6.66, 1.96) * mm, "end": v(-6.67, 1.97) * mm});
            skLineSegment(sketch, "E2766", {"start": v(-6.67, 1.97) * mm, "end": v(-6.69, 1.98) * mm});
            skLineSegment(sketch, "E2767", {"start": v(-6.69, 1.98) * mm, "end": v(-6.7, 1.99) * mm});
            skLineSegment(sketch, "E2768", {"start": v(-6.7, 1.99) * mm, "end": v(-6.71, 2) * mm});
            skLineSegment(sketch, "E2769", {"start": v(-6.71, 2) * mm, "end": v(-6.73, 2) * mm});
            skLineSegment(sketch, "E2770", {"start": v(-6.73, 2) * mm, "end": v(-6.74, 2.01) * mm});
            skLineSegment(sketch, "E2771", {"start": v(-6.74, 2.01) * mm, "end": v(-6.75, 2.02) * mm});
            skLineSegment(sketch, "E2772", {"start": v(-6.75, 2.02) * mm, "end": v(-6.77, 2.03) * mm});
            skLineSegment(sketch, "E2773", {"start": v(-6.77, 2.03) * mm, "end": v(-6.78, 2.04) * mm});
            skLineSegment(sketch, "E2774", {"start": v(-6.78, 2.04) * mm, "end": v(-6.8, 2.05) * mm});
            skLineSegment(sketch, "E2775", {"start": v(-6.8, 2.05) * mm, "end": v(-6.82, 2.06) * mm});
            skLineSegment(sketch, "E2776", {"start": v(-6.82, 2.06) * mm, "end": v(-6.83, 2.08) * mm});
            skLineSegment(sketch, "E2777", {"start": v(-6.83, 2.08) * mm, "end": v(-6.85, 2.09) * mm});
            skLineSegment(sketch, "E2778", {"start": v(-6.85, 2.09) * mm, "end": v(-6.87, 2.1) * mm});
            skLineSegment(sketch, "E2779", {"start": v(-6.87, 2.1) * mm, "end": v(-6.88, 2.11) * mm});
            skLineSegment(sketch, "E2780", {"start": v(-6.88, 2.11) * mm, "end": v(-6.9, 2.13) * mm});
            skLineSegment(sketch, "E2781", {"start": v(-6.9, 2.13) * mm, "end": v(-6.92, 2.14) * mm});
            skLineSegment(sketch, "E2782", {"start": v(-6.92, 2.14) * mm, "end": v(-6.94, 2.15) * mm});
            skLineSegment(sketch, "E2783", {"start": v(-6.94, 2.15) * mm, "end": v(-6.96, 2.17) * mm});
            skLineSegment(sketch, "E2784", {"start": v(-6.96, 2.17) * mm, "end": v(-6.97, 2.18) * mm});
            skLineSegment(sketch, "E2785", {"start": v(-6.97, 2.18) * mm, "end": v(-7, 2.2) * mm});
            skLineSegment(sketch, "E2786", {"start": v(-7, 2.2) * mm, "end": v(-7.01, 2.22) * mm});
            skLineSegment(sketch, "E2787", {"start": v(-7.01, 2.22) * mm, "end": v(-7.03, 2.23) * mm});
            skLineSegment(sketch, "E2788", {"start": v(-7.03, 2.23) * mm, "end": v(-7.05, 2.25) * mm});
            skLineSegment(sketch, "E2789", {"start": v(-7.05, 2.25) * mm, "end": v(-7.07, 2.27) * mm});
            skLineSegment(sketch, "E2790", {"start": v(-7.07, 2.27) * mm, "end": v(-7.1, 2.29) * mm});
            skLineSegment(sketch, "E2791", {"start": v(-7.1, 2.29) * mm, "end": v(-7.11, 2.3) * mm});
            skLineSegment(sketch, "E2792", {"start": v(-7.11, 2.3) * mm, "end": v(-7.13, 2.33) * mm});
            skLineSegment(sketch, "E2793", {"start": v(-7.13, 2.33) * mm, "end": v(-7.15, 2.35) * mm});
            skLineSegment(sketch, "E2794", {"start": v(-7.15, 2.35) * mm, "end": v(-7.18, 2.37) * mm});
            skLineSegment(sketch, "E2795", {"start": v(-7.18, 2.37) * mm, "end": v(-7.2, 2.39) * mm});
            skLineSegment(sketch, "E2796", {"start": v(-7.2, 2.39) * mm, "end": v(-7.22, 2.41) * mm});
            skLineSegment(sketch, "E2797", {"start": v(-7.22, 2.41) * mm, "end": v(-7.24, 2.43) * mm});
            skLineSegment(sketch, "E2798", {"start": v(-7.24, 2.43) * mm, "end": v(-7.26, 2.46) * mm});
            skLineSegment(sketch, "E2799", {"start": v(-7.26, 2.46) * mm, "end": v(-7.28, 2.48) * mm});
            skLineSegment(sketch, "E2800", {"start": v(-7.28, 2.48) * mm, "end": v(-7.3, 2.5) * mm});
            skLineSegment(sketch, "E2801", {"start": v(-7.3, 2.5) * mm, "end": v(-7.33, 2.53) * mm});
            skLineSegment(sketch, "E2802", {"start": v(-6.26, 2.78) * mm, "end": v(-6.27, 2.78) * mm});
            skLineSegment(sketch, "E2803", {"start": v(-6.27, 2.78) * mm, "end": v(-6.27, 2.77) * mm});
            skLineSegment(sketch, "E2804", {"start": v(-6.27, 2.77) * mm, "end": v(-6.28, 2.77) * mm});
            skLineSegment(sketch, "E2805", {"start": v(-6.28, 2.77) * mm, "end": v(-6.29, 2.77) * mm});
            skLineSegment(sketch, "E2806", {"start": v(-6.29, 2.77) * mm, "end": v(-6.3, 2.77) * mm});
            skLineSegment(sketch, "E2807", {"start": v(-6.3, 2.77) * mm, "end": v(-6.31, 2.77) * mm});
            skLineSegment(sketch, "E2808", {"start": v(-6.31, 2.77) * mm, "end": v(-6.33, 2.77) * mm});
            skLineSegment(sketch, "E2809", {"start": v(-6.33, 2.77) * mm, "end": v(-6.34, 2.77) * mm});
            skLineSegment(sketch, "E2810", {"start": v(-6.34, 2.77) * mm, "end": v(-6.35, 2.77) * mm});
            skLineSegment(sketch, "E2811", {"start": v(-6.35, 2.77) * mm, "end": v(-6.37, 2.78) * mm});
            skLineSegment(sketch, "E2812", {"start": v(-6.37, 2.78) * mm, "end": v(-6.38, 2.78) * mm});
            skLineSegment(sketch, "E2813", {"start": v(-6.38, 2.78) * mm, "end": v(-6.4, 2.78) * mm});
            skLineSegment(sketch, "E2814", {"start": v(-6.4, 2.78) * mm, "end": v(-6.4, 2.78) * mm});
            skLineSegment(sketch, "E2815", {"start": v(-6.4, 2.78) * mm, "end": v(-6.42, 2.79) * mm});
            skLineSegment(sketch, "E2816", {"start": v(-6.42, 2.79) * mm, "end": v(-6.44, 2.79) * mm});
            skLineSegment(sketch, "E2817", {"start": v(-6.44, 2.79) * mm, "end": v(-6.46, 2.8) * mm});
            skLineSegment(sketch, "E2818", {"start": v(-6.46, 2.8) * mm, "end": v(-6.47, 2.8) * mm});
            skLineSegment(sketch, "E2819", {"start": v(-6.47, 2.8) * mm, "end": v(-6.5, 2.8) * mm});
            skLineSegment(sketch, "E2820", {"start": v(-6.5, 2.8) * mm, "end": v(-6.51, 2.8) * mm});
            skLineSegment(sketch, "E2821", {"start": v(-6.51, 2.8) * mm, "end": v(-6.53, 2.8) * mm});
            skLineSegment(sketch, "E2822", {"start": v(-6.53, 2.8) * mm, "end": v(-6.55, 2.8) * mm});
            skLineSegment(sketch, "E2823", {"start": v(-6.55, 2.8) * mm, "end": v(-6.57, 2.8) * mm});
            skLineSegment(sketch, "E2824", {"start": v(-6.57, 2.8) * mm, "end": v(-6.59, 2.8) * mm});
            skLineSegment(sketch, "E2825", {"start": v(-6.59, 2.8) * mm, "end": v(-6.6, 2.8) * mm});
            skLineSegment(sketch, "E2826", {"start": v(-6.6, 2.8) * mm, "end": v(-6.63, 2.8) * mm});
            skLineSegment(sketch, "E2827", {"start": v(-6.63, 2.8) * mm, "end": v(-6.65, 2.8) * mm});
            skLineSegment(sketch, "E2828", {"start": v(-6.65, 2.8) * mm, "end": v(-6.68, 2.8) * mm});
            skLineSegment(sketch, "E2829", {"start": v(-6.68, 2.8) * mm, "end": v(-6.7, 2.8) * mm});
            skLineSegment(sketch, "E2830", {"start": v(-6.7, 2.8) * mm, "end": v(-6.72, 2.8) * mm});
            skLineSegment(sketch, "E2831", {"start": v(-6.72, 2.8) * mm, "end": v(-6.75, 2.8) * mm});
            skLineSegment(sketch, "E2832", {"start": v(-6.75, 2.8) * mm, "end": v(-6.77, 2.8) * mm});
            skLineSegment(sketch, "E2833", {"start": v(-6.77, 2.8) * mm, "end": v(-6.8, 2.8) * mm});
            skLineSegment(sketch, "E2834", {"start": v(-6.8, 2.8) * mm, "end": v(-6.82, 2.8) * mm});
            skLineSegment(sketch, "E2835", {"start": v(-6.82, 2.8) * mm, "end": v(-6.85, 2.8) * mm});
            skLineSegment(sketch, "E2836", {"start": v(-6.85, 2.8) * mm, "end": v(-6.88, 2.8) * mm});
            skLineSegment(sketch, "E2837", {"start": v(-6.88, 2.8) * mm, "end": v(-6.9, 2.8) * mm});
            skLineSegment(sketch, "E2838", {"start": v(-6.9, 2.8) * mm, "end": v(-6.93, 2.8) * mm});
            skLineSegment(sketch, "E2839", {"start": v(-6.93, 2.8) * mm, "end": v(-6.96, 2.8) * mm});
            skLineSegment(sketch, "E2840", {"start": v(-6.96, 2.8) * mm, "end": v(-6.99, 2.8) * mm});
            skLineSegment(sketch, "E2841", {"start": v(-6.99, 2.8) * mm, "end": v(-7.02, 2.8) * mm});
            skLineSegment(sketch, "E2842", {"start": v(-7.02, 2.8) * mm, "end": v(-7.05, 2.8) * mm});
            skLineSegment(sketch, "E2843", {"start": v(-7.05, 2.8) * mm, "end": v(-7.08, 2.8) * mm});
            skLineSegment(sketch, "E2844", {"start": v(-7.08, 2.8) * mm, "end": v(-7.1, 2.8) * mm});
            skLineSegment(sketch, "E2845", {"start": v(-7.1, 2.8) * mm, "end": v(-7.14, 2.79) * mm});
            skLineSegment(sketch, "E2846", {"start": v(-7.14, 2.79) * mm, "end": v(-7.17, 2.78) * mm});
            skLineSegment(sketch, "E2847", {"start": v(-7.17, 2.78) * mm, "end": v(-7.2, 2.78) * mm});
            skLineSegment(sketch, "E2848", {"start": v(-7.2, 2.78) * mm, "end": v(-7.24, 2.77) * mm});
            skArc(sketch, "E2849", {"start": v(-7.24, 2.77) * mm, "mid": v(-7.28, 2.65) * mm, "end": v(-7.33, 2.53) * mm});
            skLineSegment(sketch, "E2850", {"start": v(-6.16, 3) * mm, "end": v(-6.15, 3.02) * mm});
            skLineSegment(sketch, "E2851", {"start": v(-6.15, 3.02) * mm, "end": v(-6.15, 3.02) * mm});
            skLineSegment(sketch, "E2852", {"start": v(-6.15, 3.02) * mm, "end": v(-6.16, 3.03) * mm});
            skLineSegment(sketch, "E2853", {"start": v(-6.16, 3.03) * mm, "end": v(-6.16, 3.04) * mm});
            skLineSegment(sketch, "E2854", {"start": v(-6.16, 3.04) * mm, "end": v(-6.17, 3.05) * mm});
            skLineSegment(sketch, "E2855", {"start": v(-6.17, 3.05) * mm, "end": v(-6.18, 3.06) * mm});
            skLineSegment(sketch, "E2856", {"start": v(-6.18, 3.06) * mm, "end": v(-6.19, 3.07) * mm});
            skLineSegment(sketch, "E2857", {"start": v(-6.19, 3.07) * mm, "end": v(-6.2, 3.07) * mm});
            skLineSegment(sketch, "E2858", {"start": v(-6.2, 3.07) * mm, "end": v(-6.2, 3.08) * mm});
            skLineSegment(sketch, "E2859", {"start": v(-6.2, 3.08) * mm, "end": v(-6.22, 3.1) * mm});
            skLineSegment(sketch, "E2860", {"start": v(-6.22, 3.1) * mm, "end": v(-6.23, 3.1) * mm});
            skLineSegment(sketch, "E2861", {"start": v(-6.23, 3.1) * mm, "end": v(-6.24, 3.11) * mm});
            skLineSegment(sketch, "E2862", {"start": v(-6.24, 3.11) * mm, "end": v(-6.25, 3.12) * mm});
            skLineSegment(sketch, "E2863", {"start": v(-6.25, 3.12) * mm, "end": v(-6.26, 3.13) * mm});
            skLineSegment(sketch, "E2864", {"start": v(-6.26, 3.13) * mm, "end": v(-6.28, 3.14) * mm});
            skLineSegment(sketch, "E2865", {"start": v(-6.28, 3.14) * mm, "end": v(-6.29, 3.15) * mm});
            skLineSegment(sketch, "E2866", {"start": v(-6.29, 3.15) * mm, "end": v(-6.3, 3.16) * mm});
            skLineSegment(sketch, "E2867", {"start": v(-6.3, 3.16) * mm, "end": v(-6.31, 3.18) * mm});
            skLineSegment(sketch, "E2868", {"start": v(-6.31, 3.18) * mm, "end": v(-6.33, 3.19) * mm});
            skLineSegment(sketch, "E2869", {"start": v(-6.33, 3.19) * mm, "end": v(-6.34, 3.2) * mm});
            skLineSegment(sketch, "E2870", {"start": v(-6.34, 3.2) * mm, "end": v(-6.35, 3.22) * mm});
            skLineSegment(sketch, "E2871", {"start": v(-6.35, 3.22) * mm, "end": v(-6.37, 3.23) * mm});
            skLineSegment(sketch, "E2872", {"start": v(-6.37, 3.23) * mm, "end": v(-6.38, 3.24) * mm});
            skLineSegment(sketch, "E2873", {"start": v(-6.38, 3.24) * mm, "end": v(-6.4, 3.26) * mm});
            skLineSegment(sketch, "E2874", {"start": v(-6.4, 3.26) * mm, "end": v(-6.41, 3.28) * mm});
            skLineSegment(sketch, "E2875", {"start": v(-6.41, 3.28) * mm, "end": v(-6.43, 3.3) * mm});
            skLineSegment(sketch, "E2876", {"start": v(-6.43, 3.3) * mm, "end": v(-6.44, 3.3) * mm});
            skLineSegment(sketch, "E2877", {"start": v(-6.44, 3.3) * mm, "end": v(-6.46, 3.33) * mm});
            skLineSegment(sketch, "E2878", {"start": v(-6.46, 3.33) * mm, "end": v(-6.47, 3.34) * mm});
            skLineSegment(sketch, "E2879", {"start": v(-6.47, 3.34) * mm, "end": v(-6.49, 3.36) * mm});
            skLineSegment(sketch, "E2880", {"start": v(-6.49, 3.36) * mm, "end": v(-6.5, 3.38) * mm});
            skLineSegment(sketch, "E2881", {"start": v(-6.5, 3.38) * mm, "end": v(-6.52, 3.4) * mm});
            skLineSegment(sketch, "E2882", {"start": v(-6.52, 3.4) * mm, "end": v(-6.54, 3.42) * mm});
            skLineSegment(sketch, "E2883", {"start": v(-6.54, 3.42) * mm, "end": v(-6.55, 3.44) * mm});
            skLineSegment(sketch, "E2884", {"start": v(-6.55, 3.44) * mm, "end": v(-6.57, 3.46) * mm});
            skLineSegment(sketch, "E2885", {"start": v(-6.57, 3.46) * mm, "end": v(-6.59, 3.48) * mm});
            skLineSegment(sketch, "E2886", {"start": v(-6.59, 3.48) * mm, "end": v(-6.6, 3.5) * mm});
            skLineSegment(sketch, "E2887", {"start": v(-6.6, 3.5) * mm, "end": v(-6.62, 3.53) * mm});
            skLineSegment(sketch, "E2888", {"start": v(-6.62, 3.53) * mm, "end": v(-6.64, 3.55) * mm});
            skLineSegment(sketch, "E2889", {"start": v(-6.64, 3.55) * mm, "end": v(-6.66, 3.58) * mm});
            skLineSegment(sketch, "E2890", {"start": v(-6.66, 3.58) * mm, "end": v(-6.67, 3.6) * mm});
            skLineSegment(sketch, "E2891", {"start": v(-6.67, 3.6) * mm, "end": v(-6.7, 3.63) * mm});
            skLineSegment(sketch, "E2892", {"start": v(-6.7, 3.63) * mm, "end": v(-6.7, 3.65) * mm});
            skLineSegment(sketch, "E2893", {"start": v(-6.7, 3.65) * mm, "end": v(-6.73, 3.68) * mm});
            skLineSegment(sketch, "E2894", {"start": v(-6.73, 3.68) * mm, "end": v(-6.74, 3.7) * mm});
            skLineSegment(sketch, "E2895", {"start": v(-6.74, 3.7) * mm, "end": v(-6.76, 3.73) * mm});
            skLineSegment(sketch, "E2896", {"start": v(-6.76, 3.73) * mm, "end": v(-6.78, 3.76) * mm});
            skLineSegment(sketch, "E2897", {"start": v(-5.68, 3.83) * mm, "end": v(-5.69, 3.82) * mm});
            skLineSegment(sketch, "E2898", {"start": v(-5.69, 3.82) * mm, "end": v(-5.7, 3.82) * mm});
            skLineSegment(sketch, "E2899", {"start": v(-5.7, 3.82) * mm, "end": v(-5.7, 3.82) * mm});
            skLineSegment(sketch, "E2900", {"start": v(-5.7, 3.82) * mm, "end": v(-5.71, 3.82) * mm});
            skLineSegment(sketch, "E2901", {"start": v(-5.71, 3.82) * mm, "end": v(-5.72, 3.82) * mm});
            skLineSegment(sketch, "E2902", {"start": v(-5.72, 3.82) * mm, "end": v(-5.74, 3.82) * mm});
            skLineSegment(sketch, "E2903", {"start": v(-5.74, 3.82) * mm, "end": v(-5.75, 3.83) * mm});
            skLineSegment(sketch, "E2904", {"start": v(-5.75, 3.83) * mm, "end": v(-5.76, 3.83) * mm});
            skLineSegment(sketch, "E2905", {"start": v(-5.76, 3.83) * mm, "end": v(-5.77, 3.83) * mm});
            skLineSegment(sketch, "E2906", {"start": v(-5.77, 3.83) * mm, "end": v(-5.79, 3.84) * mm});
            skLineSegment(sketch, "E2907", {"start": v(-5.79, 3.84) * mm, "end": v(-5.8, 3.84) * mm});
            skLineSegment(sketch, "E2908", {"start": v(-5.8, 3.84) * mm, "end": v(-5.81, 3.85) * mm});
            skLineSegment(sketch, "E2909", {"start": v(-5.81, 3.85) * mm, "end": v(-5.83, 3.85) * mm});
            skLineSegment(sketch, "E2910", {"start": v(-5.83, 3.85) * mm, "end": v(-5.84, 3.86) * mm});
            skLineSegment(sketch, "E2911", {"start": v(-5.84, 3.86) * mm, "end": v(-5.86, 3.86) * mm});
            skLineSegment(sketch, "E2912", {"start": v(-5.86, 3.86) * mm, "end": v(-5.87, 3.87) * mm});
            skLineSegment(sketch, "E2913", {"start": v(-5.87, 3.87) * mm, "end": v(-5.9, 3.87) * mm});
            skLineSegment(sketch, "E2914", {"start": v(-5.9, 3.87) * mm, "end": v(-5.9, 3.88) * mm});
            skLineSegment(sketch, "E2915", {"start": v(-5.9, 3.88) * mm, "end": v(-5.93, 3.89) * mm});
            skLineSegment(sketch, "E2916", {"start": v(-5.93, 3.89) * mm, "end": v(-5.94, 3.9) * mm});
            skLineSegment(sketch, "E2917", {"start": v(-5.94, 3.9) * mm, "end": v(-5.96, 3.9) * mm});
            skLineSegment(sketch, "E2918", {"start": v(-5.96, 3.9) * mm, "end": v(-5.98, 3.9) * mm});
            skLineSegment(sketch, "E2919", {"start": v(-5.98, 3.9) * mm, "end": v(-6, 3.9) * mm});
            skLineSegment(sketch, "E2920", {"start": v(-6, 3.9) * mm, "end": v(-6.02, 3.91) * mm});
            skLineSegment(sketch, "E2921", {"start": v(-6.02, 3.91) * mm, "end": v(-6.04, 3.92) * mm});
            skLineSegment(sketch, "E2922", {"start": v(-6.04, 3.92) * mm, "end": v(-6.06, 3.92) * mm});
            skLineSegment(sketch, "E2923", {"start": v(-6.06, 3.92) * mm, "end": v(-6.09, 3.92) * mm});
            skLineSegment(sketch, "E2924", {"start": v(-6.09, 3.92) * mm, "end": v(-6.1, 3.93) * mm});
            skLineSegment(sketch, "E2925", {"start": v(-6.1, 3.93) * mm, "end": v(-6.13, 3.93) * mm});
            skLineSegment(sketch, "E2926", {"start": v(-6.13, 3.93) * mm, "end": v(-6.16, 3.94) * mm});
            skLineSegment(sketch, "E2927", {"start": v(-6.16, 3.94) * mm, "end": v(-6.18, 3.94) * mm});
            skLineSegment(sketch, "E2928", {"start": v(-6.18, 3.94) * mm, "end": v(-6.2, 3.95) * mm});
            skLineSegment(sketch, "E2929", {"start": v(-6.2, 3.95) * mm, "end": v(-6.23, 3.95) * mm});
            skLineSegment(sketch, "E2930", {"start": v(-6.23, 3.95) * mm, "end": v(-6.26, 3.96) * mm});
            skLineSegment(sketch, "E2931", {"start": v(-6.26, 3.96) * mm, "end": v(-6.28, 3.96) * mm});
            skLineSegment(sketch, "E2932", {"start": v(-6.28, 3.96) * mm, "end": v(-6.31, 3.96) * mm});
            skLineSegment(sketch, "E2933", {"start": v(-6.31, 3.96) * mm, "end": v(-6.34, 3.97) * mm});
            skLineSegment(sketch, "E2934", {"start": v(-6.34, 3.97) * mm, "end": v(-6.37, 3.97) * mm});
            skLineSegment(sketch, "E2935", {"start": v(-6.37, 3.97) * mm, "end": v(-6.4, 3.97) * mm});
            skLineSegment(sketch, "E2936", {"start": v(-6.4, 3.97) * mm, "end": v(-6.43, 3.98) * mm});
            skLineSegment(sketch, "E2937", {"start": v(-6.43, 3.98) * mm, "end": v(-6.46, 3.98) * mm});
            skLineSegment(sketch, "E2938", {"start": v(-6.46, 3.98) * mm, "end": v(-6.49, 3.98) * mm});
            skLineSegment(sketch, "E2939", {"start": v(-6.49, 3.98) * mm, "end": v(-6.52, 3.98) * mm});
            skLineSegment(sketch, "E2940", {"start": v(-6.52, 3.98) * mm, "end": v(-6.55, 3.98) * mm});
            skLineSegment(sketch, "E2941", {"start": v(-6.55, 3.98) * mm, "end": v(-6.58, 3.99) * mm});
            skLineSegment(sketch, "E2942", {"start": v(-6.58, 3.99) * mm, "end": v(-6.61, 3.99) * mm});
            skLineSegment(sketch, "E2943", {"start": v(-6.61, 3.99) * mm, "end": v(-6.65, 3.99) * mm});
            skArc(sketch, "E2944", {"start": v(-6.65, 3.99) * mm, "mid": v(-6.71, 3.88) * mm, "end": v(-6.78, 3.76) * mm});
            skLineSegment(sketch, "E2945", {"start": v(-5.54, 4.03) * mm, "end": v(-5.54, 4.04) * mm});
            skLineSegment(sketch, "E2946", {"start": v(-5.54, 4.04) * mm, "end": v(-5.54, 4.04) * mm});
            skLineSegment(sketch, "E2947", {"start": v(-5.54, 4.04) * mm, "end": v(-5.54, 4.05) * mm});
            skLineSegment(sketch, "E2948", {"start": v(-5.54, 4.05) * mm, "end": v(-5.54, 4.06) * mm});
            skLineSegment(sketch, "E2949", {"start": v(-5.54, 4.06) * mm, "end": v(-5.55, 4.07) * mm});
            skLineSegment(sketch, "E2950", {"start": v(-5.55, 4.07) * mm, "end": v(-5.55, 4.08) * mm});
            skLineSegment(sketch, "E2951", {"start": v(-5.55, 4.08) * mm, "end": v(-5.56, 4.1) * mm});
            skLineSegment(sketch, "E2952", {"start": v(-5.56, 4.1) * mm, "end": v(-5.57, 4.1) * mm});
            skLineSegment(sketch, "E2953", {"start": v(-5.57, 4.1) * mm, "end": v(-5.58, 4.11) * mm});
            skLineSegment(sketch, "E2954", {"start": v(-5.58, 4.11) * mm, "end": v(-5.59, 4.12) * mm});
            skLineSegment(sketch, "E2955", {"start": v(-5.59, 4.12) * mm, "end": v(-5.6, 4.14) * mm});
            skLineSegment(sketch, "E2956", {"start": v(-5.6, 4.14) * mm, "end": v(-5.6, 4.15) * mm});
            skLineSegment(sketch, "E2957", {"start": v(-5.6, 4.15) * mm, "end": v(-5.62, 4.16) * mm});
            skLineSegment(sketch, "E2958", {"start": v(-5.62, 4.16) * mm, "end": v(-5.63, 4.17) * mm});
            skLineSegment(sketch, "E2959", {"start": v(-5.63, 4.17) * mm, "end": v(-5.64, 4.18) * mm});
            skLineSegment(sketch, "E2960", {"start": v(-5.64, 4.18) * mm, "end": v(-5.65, 4.2) * mm});
            skLineSegment(sketch, "E2961", {"start": v(-5.65, 4.2) * mm, "end": v(-5.66, 4.21) * mm});
            skLineSegment(sketch, "E2962", {"start": v(-5.66, 4.21) * mm, "end": v(-5.67, 4.22) * mm});
            skLineSegment(sketch, "E2963", {"start": v(-5.67, 4.22) * mm, "end": v(-5.68, 4.24) * mm});
            skLineSegment(sketch, "E2964", {"start": v(-5.68, 4.24) * mm, "end": v(-5.69, 4.25) * mm});
            skLineSegment(sketch, "E2965", {"start": v(-5.69, 4.25) * mm, "end": v(-5.7, 4.27) * mm});
            skLineSegment(sketch, "E2966", {"start": v(-5.7, 4.27) * mm, "end": v(-5.71, 4.29) * mm});
            skLineSegment(sketch, "E2967", {"start": v(-5.71, 4.29) * mm, "end": v(-5.72, 4.3) * mm});
            skLineSegment(sketch, "E2968", {"start": v(-5.72, 4.3) * mm, "end": v(-5.73, 4.32) * mm});
            skLineSegment(sketch, "E2969", {"start": v(-5.73, 4.32) * mm, "end": v(-5.75, 4.34) * mm});
            skLineSegment(sketch, "E2970", {"start": v(-5.75, 4.34) * mm, "end": v(-5.76, 4.36) * mm});
            skLineSegment(sketch, "E2971", {"start": v(-5.76, 4.36) * mm, "end": v(-5.77, 4.38) * mm});
            skLineSegment(sketch, "E2972", {"start": v(-5.77, 4.38) * mm, "end": v(-5.78, 4.4) * mm});
            skLineSegment(sketch, "E2973", {"start": v(-5.78, 4.4) * mm, "end": v(-5.8, 4.42) * mm});
            skLineSegment(sketch, "E2974", {"start": v(-5.8, 4.42) * mm, "end": v(-5.8, 4.44) * mm});
            skLineSegment(sketch, "E2975", {"start": v(-5.8, 4.44) * mm, "end": v(-5.82, 4.46) * mm});
            skLineSegment(sketch, "E2976", {"start": v(-5.82, 4.46) * mm, "end": v(-5.83, 4.48) * mm});
            skLineSegment(sketch, "E2977", {"start": v(-5.83, 4.48) * mm, "end": v(-5.84, 4.5) * mm});
            skLineSegment(sketch, "E2978", {"start": v(-5.84, 4.5) * mm, "end": v(-5.86, 4.53) * mm});
            skLineSegment(sketch, "E2979", {"start": v(-5.86, 4.53) * mm, "end": v(-5.87, 4.55) * mm});
            skLineSegment(sketch, "E2980", {"start": v(-5.87, 4.55) * mm, "end": v(-5.88, 4.58) * mm});
            skLineSegment(sketch, "E2981", {"start": v(-5.88, 4.58) * mm, "end": v(-5.9, 4.6) * mm});
            skLineSegment(sketch, "E2982", {"start": v(-5.9, 4.6) * mm, "end": v(-5.9, 4.63) * mm});
            skLineSegment(sketch, "E2983", {"start": v(-5.9, 4.63) * mm, "end": v(-5.92, 4.65) * mm});
            skLineSegment(sketch, "E2984", {"start": v(-5.92, 4.65) * mm, "end": v(-5.93, 4.68) * mm});
            skLineSegment(sketch, "E2985", {"start": v(-5.93, 4.68) * mm, "end": v(-5.95, 4.7) * mm});
            skLineSegment(sketch, "E2986", {"start": v(-5.95, 4.7) * mm, "end": v(-5.96, 4.73) * mm});
            skLineSegment(sketch, "E2987", {"start": v(-5.96, 4.73) * mm, "end": v(-5.97, 4.76) * mm});
            skLineSegment(sketch, "E2988", {"start": v(-5.97, 4.76) * mm, "end": v(-5.98, 4.8) * mm});
            skLineSegment(sketch, "E2989", {"start": v(-5.98, 4.8) * mm, "end": v(-6, 4.82) * mm});
            skLineSegment(sketch, "E2990", {"start": v(-6, 4.82) * mm, "end": v(-6, 4.85) * mm});
            skLineSegment(sketch, "E2991", {"start": v(-6, 4.85) * mm, "end": v(-6.02, 4.88) * mm});
            skLineSegment(sketch, "E2992", {"start": v(-4.93, 4.76) * mm, "end": v(-4.94, 4.75) * mm});
            skLineSegment(sketch, "E2993", {"start": v(-4.94, 4.75) * mm, "end": v(-4.94, 4.75) * mm});
            skLineSegment(sketch, "E2994", {"start": v(-4.94, 4.75) * mm, "end": v(-4.95, 4.75) * mm});
            skLineSegment(sketch, "E2995", {"start": v(-4.95, 4.75) * mm, "end": v(-4.96, 4.75) * mm});
            skLineSegment(sketch, "E2996", {"start": v(-4.96, 4.75) * mm, "end": v(-4.97, 4.75) * mm});
            skLineSegment(sketch, "E2997", {"start": v(-4.97, 4.75) * mm, "end": v(-4.99, 4.76) * mm});
            skLineSegment(sketch, "E2998", {"start": v(-4.99, 4.76) * mm, "end": v(-5, 4.77) * mm});
            skLineSegment(sketch, "E2999", {"start": v(-5, 4.77) * mm, "end": v(-5, 4.77) * mm});
            skLineSegment(sketch, "E3000", {"start": v(-5, 4.77) * mm, "end": v(-5.02, 4.78) * mm});
            skLineSegment(sketch, "E3001", {"start": v(-5.02, 4.78) * mm, "end": v(-5.03, 4.79) * mm});
            skLineSegment(sketch, "E3002", {"start": v(-5.03, 4.79) * mm, "end": v(-5.04, 4.8) * mm});
            skLineSegment(sketch, "E3003", {"start": v(-5.04, 4.8) * mm, "end": v(-5.06, 4.8) * mm});
            skLineSegment(sketch, "E3004", {"start": v(-5.06, 4.8) * mm, "end": v(-5.07, 4.8) * mm});
            skLineSegment(sketch, "E3005", {"start": v(-5.07, 4.8) * mm, "end": v(-5.08, 4.82) * mm});
            skLineSegment(sketch, "E3006", {"start": v(-5.08, 4.82) * mm, "end": v(-5.1, 4.82) * mm});
            skLineSegment(sketch, "E3007", {"start": v(-5.1, 4.82) * mm, "end": v(-5.11, 4.83) * mm});
            skLineSegment(sketch, "E3008", {"start": v(-5.11, 4.83) * mm, "end": v(-5.13, 4.84) * mm});
            skLineSegment(sketch, "E3009", {"start": v(-5.13, 4.84) * mm, "end": v(-5.14, 4.85) * mm});
            skLineSegment(sketch, "E3010", {"start": v(-5.14, 4.85) * mm, "end": v(-5.16, 4.85) * mm});
            skLineSegment(sketch, "E3011", {"start": v(-5.16, 4.85) * mm, "end": v(-5.18, 4.86) * mm});
            skLineSegment(sketch, "E3012", {"start": v(-5.18, 4.86) * mm, "end": v(-5.2, 4.87) * mm});
            skLineSegment(sketch, "E3013", {"start": v(-5.2, 4.87) * mm, "end": v(-5.21, 4.88) * mm});
            skLineSegment(sketch, "E3014", {"start": v(-5.21, 4.88) * mm, "end": v(-5.23, 4.89) * mm});
            skLineSegment(sketch, "E3015", {"start": v(-5.23, 4.89) * mm, "end": v(-5.25, 4.9) * mm});
            skLineSegment(sketch, "E3016", {"start": v(-5.25, 4.9) * mm, "end": v(-5.27, 4.9) * mm});
            skLineSegment(sketch, "E3017", {"start": v(-5.27, 4.9) * mm, "end": v(-5.3, 4.91) * mm});
            skLineSegment(sketch, "E3018", {"start": v(-5.3, 4.91) * mm, "end": v(-5.31, 4.92) * mm});
            skLineSegment(sketch, "E3019", {"start": v(-5.31, 4.92) * mm, "end": v(-5.33, 4.93) * mm});
            skLineSegment(sketch, "E3020", {"start": v(-5.33, 4.93) * mm, "end": v(-5.36, 4.94) * mm});
            skLineSegment(sketch, "E3021", {"start": v(-5.36, 4.94) * mm, "end": v(-5.38, 4.95) * mm});
            skLineSegment(sketch, "E3022", {"start": v(-5.38, 4.95) * mm, "end": v(-5.4, 4.96) * mm});
            skLineSegment(sketch, "E3023", {"start": v(-5.4, 4.96) * mm, "end": v(-5.43, 4.96) * mm});
            skLineSegment(sketch, "E3024", {"start": v(-5.43, 4.96) * mm, "end": v(-5.45, 4.97) * mm});
            skLineSegment(sketch, "E3025", {"start": v(-5.45, 4.97) * mm, "end": v(-5.48, 4.98) * mm});
            skLineSegment(sketch, "E3026", {"start": v(-5.48, 4.98) * mm, "end": v(-5.5, 5) * mm});
            skLineSegment(sketch, "E3027", {"start": v(-5.5, 5) * mm, "end": v(-5.53, 5) * mm});
            skLineSegment(sketch, "E3028", {"start": v(-5.53, 5) * mm, "end": v(-5.55, 5) * mm});
            skLineSegment(sketch, "E3029", {"start": v(-5.55, 5) * mm, "end": v(-5.58, 5.01) * mm});
            skLineSegment(sketch, "E3030", {"start": v(-5.58, 5.01) * mm, "end": v(-5.6, 5.02) * mm});
            skLineSegment(sketch, "E3031", {"start": v(-5.6, 5.02) * mm, "end": v(-5.64, 5.03) * mm});
            skLineSegment(sketch, "E3032", {"start": v(-5.64, 5.03) * mm, "end": v(-5.67, 5.04) * mm});
            skLineSegment(sketch, "E3033", {"start": v(-5.67, 5.04) * mm, "end": v(-5.7, 5.05) * mm});
            skLineSegment(sketch, "E3034", {"start": v(-5.7, 5.05) * mm, "end": v(-5.73, 5.05) * mm});
            skLineSegment(sketch, "E3035", {"start": v(-5.73, 5.05) * mm, "end": v(-5.76, 5.06) * mm});
            skLineSegment(sketch, "E3036", {"start": v(-5.76, 5.06) * mm, "end": v(-5.79, 5.07) * mm});
            skLineSegment(sketch, "E3037", {"start": v(-5.79, 5.07) * mm, "end": v(-5.82, 5.08) * mm});
            skLineSegment(sketch, "E3038", {"start": v(-5.82, 5.08) * mm, "end": v(-5.85, 5.08) * mm});
            skArc(sketch, "E3039", {"start": v(-5.85, 5.08) * mm, "mid": v(-5.94, 4.98) * mm, "end": v(-6.02, 4.88) * mm});
            skLineSegment(sketch, "E3040", {"start": v(-4.76, 4.93) * mm, "end": v(-4.75, 4.94) * mm});
            skLineSegment(sketch, "E3041", {"start": v(-4.75, 4.94) * mm, "end": v(-4.75, 4.94) * mm});
            skLineSegment(sketch, "E3042", {"start": v(-4.75, 4.94) * mm, "end": v(-4.75, 4.95) * mm});
            skLineSegment(sketch, "E3043", {"start": v(-4.75, 4.95) * mm, "end": v(-4.75, 4.96) * mm});
            skLineSegment(sketch, "E3044", {"start": v(-4.75, 4.96) * mm, "end": v(-4.75, 4.97) * mm});
            skLineSegment(sketch, "E3045", {"start": v(-4.75, 4.97) * mm, "end": v(-4.76, 4.99) * mm});
            skLineSegment(sketch, "E3046", {"start": v(-4.76, 4.99) * mm, "end": v(-4.77, 5) * mm});
            skLineSegment(sketch, "E3047", {"start": v(-4.77, 5) * mm, "end": v(-4.77, 5) * mm});
            skLineSegment(sketch, "E3048", {"start": v(-4.77, 5) * mm, "end": v(-4.78, 5.02) * mm});
            skLineSegment(sketch, "E3049", {"start": v(-4.78, 5.02) * mm, "end": v(-4.79, 5.03) * mm});
            skLineSegment(sketch, "E3050", {"start": v(-4.79, 5.03) * mm, "end": v(-4.8, 5.04) * mm});
            skLineSegment(sketch, "E3051", {"start": v(-4.8, 5.04) * mm, "end": v(-4.8, 5.06) * mm});
            skLineSegment(sketch, "E3052", {"start": v(-4.8, 5.06) * mm, "end": v(-4.8, 5.07) * mm});
            skLineSegment(sketch, "E3053", {"start": v(-4.8, 5.07) * mm, "end": v(-4.82, 5.08) * mm});
            skLineSegment(sketch, "E3054", {"start": v(-4.82, 5.08) * mm, "end": v(-4.82, 5.1) * mm});
            skLineSegment(sketch, "E3055", {"start": v(-4.82, 5.1) * mm, "end": v(-4.83, 5.11) * mm});
            skLineSegment(sketch, "E3056", {"start": v(-4.83, 5.11) * mm, "end": v(-4.84, 5.13) * mm});
            skLineSegment(sketch, "E3057", {"start": v(-4.84, 5.13) * mm, "end": v(-4.85, 5.14) * mm});
            skLineSegment(sketch, "E3058", {"start": v(-4.85, 5.14) * mm, "end": v(-4.85, 5.16) * mm});
            skLineSegment(sketch, "E3059", {"start": v(-4.85, 5.16) * mm, "end": v(-4.86, 5.18) * mm});
            skLineSegment(sketch, "E3060", {"start": v(-4.86, 5.18) * mm, "end": v(-4.87, 5.2) * mm});
            skLineSegment(sketch, "E3061", {"start": v(-4.87, 5.2) * mm, "end": v(-4.88, 5.21) * mm});
            skLineSegment(sketch, "E3062", {"start": v(-4.88, 5.21) * mm, "end": v(-4.89, 5.23) * mm});
            skLineSegment(sketch, "E3063", {"start": v(-4.89, 5.23) * mm, "end": v(-4.9, 5.25) * mm});
            skLineSegment(sketch, "E3064", {"start": v(-4.9, 5.25) * mm, "end": v(-4.9, 5.27) * mm});
            skLineSegment(sketch, "E3065", {"start": v(-4.9, 5.27) * mm, "end": v(-4.91, 5.3) * mm});
            skLineSegment(sketch, "E3066", {"start": v(-4.91, 5.3) * mm, "end": v(-4.92, 5.31) * mm});
            skLineSegment(sketch, "E3067", {"start": v(-4.92, 5.31) * mm, "end": v(-4.93, 5.33) * mm});
            skLineSegment(sketch, "E3068", {"start": v(-4.93, 5.33) * mm, "end": v(-4.94, 5.36) * mm});
            skLineSegment(sketch, "E3069", {"start": v(-4.94, 5.36) * mm, "end": v(-4.95, 5.38) * mm});
            skLineSegment(sketch, "E3070", {"start": v(-4.95, 5.38) * mm, "end": v(-4.96, 5.4) * mm});
            skLineSegment(sketch, "E3071", {"start": v(-4.96, 5.4) * mm, "end": v(-4.96, 5.43) * mm});
            skLineSegment(sketch, "E3072", {"start": v(-4.96, 5.43) * mm, "end": v(-4.97, 5.45) * mm});
            skLineSegment(sketch, "E3073", {"start": v(-4.97, 5.45) * mm, "end": v(-4.98, 5.48) * mm});
            skLineSegment(sketch, "E3074", {"start": v(-4.98, 5.48) * mm, "end": v(-5, 5.5) * mm});
            skLineSegment(sketch, "E3075", {"start": v(-5, 5.5) * mm, "end": v(-5, 5.53) * mm});
            skLineSegment(sketch, "E3076", {"start": v(-5, 5.53) * mm, "end": v(-5, 5.55) * mm});
            skLineSegment(sketch, "E3077", {"start": v(-5, 5.55) * mm, "end": v(-5.01, 5.58) * mm});
            skLineSegment(sketch, "E3078", {"start": v(-5.01, 5.58) * mm, "end": v(-5.02, 5.6) * mm});
            skLineSegment(sketch, "E3079", {"start": v(-5.02, 5.6) * mm, "end": v(-5.03, 5.64) * mm});
            skLineSegment(sketch, "E3080", {"start": v(-5.03, 5.64) * mm, "end": v(-5.04, 5.67) * mm});
            skLineSegment(sketch, "E3081", {"start": v(-5.04, 5.67) * mm, "end": v(-5.05, 5.7) * mm});
            skLineSegment(sketch, "E3082", {"start": v(-5.05, 5.7) * mm, "end": v(-5.05, 5.73) * mm});
            skLineSegment(sketch, "E3083", {"start": v(-5.05, 5.73) * mm, "end": v(-5.06, 5.76) * mm});
            skLineSegment(sketch, "E3084", {"start": v(-5.06, 5.76) * mm, "end": v(-5.07, 5.79) * mm});
            skLineSegment(sketch, "E3085", {"start": v(-5.07, 5.79) * mm, "end": v(-5.08, 5.82) * mm});
            skLineSegment(sketch, "E3086", {"start": v(-5.08, 5.82) * mm, "end": v(-5.08, 5.85) * mm});
            skLineSegment(sketch, "E3087", {"start": v(-4.03, 5.54) * mm, "end": v(-4.04, 5.54) * mm});
            skLineSegment(sketch, "E3088", {"start": v(-4.04, 5.54) * mm, "end": v(-4.04, 5.54) * mm});
            skLineSegment(sketch, "E3089", {"start": v(-4.04, 5.54) * mm, "end": v(-4.05, 5.54) * mm});
            skLineSegment(sketch, "E3090", {"start": v(-4.05, 5.54) * mm, "end": v(-4.06, 5.54) * mm});
            skLineSegment(sketch, "E3091", {"start": v(-4.06, 5.54) * mm, "end": v(-4.07, 5.55) * mm});
            skLineSegment(sketch, "E3092", {"start": v(-4.07, 5.55) * mm, "end": v(-4.08, 5.55) * mm});
            skLineSegment(sketch, "E3093", {"start": v(-4.08, 5.55) * mm, "end": v(-4.1, 5.56) * mm});
            skLineSegment(sketch, "E3094", {"start": v(-4.1, 5.56) * mm, "end": v(-4.1, 5.57) * mm});
            skLineSegment(sketch, "E3095", {"start": v(-4.1, 5.57) * mm, "end": v(-4.11, 5.58) * mm});
            skLineSegment(sketch, "E3096", {"start": v(-4.11, 5.58) * mm, "end": v(-4.12, 5.59) * mm});
            skLineSegment(sketch, "E3097", {"start": v(-4.12, 5.59) * mm, "end": v(-4.14, 5.6) * mm});
            skLineSegment(sketch, "E3098", {"start": v(-4.14, 5.6) * mm, "end": v(-4.15, 5.6) * mm});
            skLineSegment(sketch, "E3099", {"start": v(-4.15, 5.6) * mm, "end": v(-4.16, 5.62) * mm});
            skLineSegment(sketch, "E3100", {"start": v(-4.16, 5.62) * mm, "end": v(-4.17, 5.63) * mm});
            skLineSegment(sketch, "E3101", {"start": v(-4.17, 5.63) * mm, "end": v(-4.18, 5.64) * mm});
            skLineSegment(sketch, "E3102", {"start": v(-4.18, 5.64) * mm, "end": v(-4.2, 5.65) * mm});
            skLineSegment(sketch, "E3103", {"start": v(-4.2, 5.65) * mm, "end": v(-4.21, 5.66) * mm});
            skLineSegment(sketch, "E3104", {"start": v(-4.21, 5.66) * mm, "end": v(-4.22, 5.67) * mm});
            skLineSegment(sketch, "E3105", {"start": v(-4.22, 5.67) * mm, "end": v(-4.24, 5.68) * mm});
            skLineSegment(sketch, "E3106", {"start": v(-4.24, 5.68) * mm, "end": v(-4.25, 5.69) * mm});
            skLineSegment(sketch, "E3107", {"start": v(-4.25, 5.69) * mm, "end": v(-4.27, 5.7) * mm});
            skLineSegment(sketch, "E3108", {"start": v(-4.27, 5.7) * mm, "end": v(-4.29, 5.71) * mm});
            skLineSegment(sketch, "E3109", {"start": v(-4.29, 5.71) * mm, "end": v(-4.3, 5.72) * mm});
            skLineSegment(sketch, "E3110", {"start": v(-4.3, 5.72) * mm, "end": v(-4.32, 5.73) * mm});
            skLineSegment(sketch, "E3111", {"start": v(-4.32, 5.73) * mm, "end": v(-4.34, 5.75) * mm});
            skLineSegment(sketch, "E3112", {"start": v(-4.34, 5.75) * mm, "end": v(-4.36, 5.76) * mm});
            skLineSegment(sketch, "E3113", {"start": v(-4.36, 5.76) * mm, "end": v(-4.38, 5.77) * mm});
            skLineSegment(sketch, "E3114", {"start": v(-4.38, 5.77) * mm, "end": v(-4.4, 5.78) * mm});
            skLineSegment(sketch, "E3115", {"start": v(-4.4, 5.78) * mm, "end": v(-4.42, 5.8) * mm});
            skLineSegment(sketch, "E3116", {"start": v(-4.42, 5.8) * mm, "end": v(-4.44, 5.8) * mm});
            skLineSegment(sketch, "E3117", {"start": v(-4.44, 5.8) * mm, "end": v(-4.46, 5.82) * mm});
            skLineSegment(sketch, "E3118", {"start": v(-4.46, 5.82) * mm, "end": v(-4.48, 5.83) * mm});
            skLineSegment(sketch, "E3119", {"start": v(-4.48, 5.83) * mm, "end": v(-4.5, 5.84) * mm});
            skLineSegment(sketch, "E3120", {"start": v(-4.5, 5.84) * mm, "end": v(-4.53, 5.86) * mm});
            skLineSegment(sketch, "E3121", {"start": v(-4.53, 5.86) * mm, "end": v(-4.55, 5.87) * mm});
            skLineSegment(sketch, "E3122", {"start": v(-4.55, 5.87) * mm, "end": v(-4.58, 5.88) * mm});
            skLineSegment(sketch, "E3123", {"start": v(-4.58, 5.88) * mm, "end": v(-4.6, 5.9) * mm});
            skLineSegment(sketch, "E3124", {"start": v(-4.6, 5.9) * mm, "end": v(-4.63, 5.9) * mm});
            skLineSegment(sketch, "E3125", {"start": v(-4.63, 5.9) * mm, "end": v(-4.65, 5.92) * mm});
            skLineSegment(sketch, "E3126", {"start": v(-4.65, 5.92) * mm, "end": v(-4.68, 5.93) * mm});
            skLineSegment(sketch, "E3127", {"start": v(-4.68, 5.93) * mm, "end": v(-4.7, 5.95) * mm});
            skLineSegment(sketch, "E3128", {"start": v(-4.7, 5.95) * mm, "end": v(-4.73, 5.96) * mm});
            skLineSegment(sketch, "E3129", {"start": v(-4.73, 5.96) * mm, "end": v(-4.76, 5.97) * mm});
            skLineSegment(sketch, "E3130", {"start": v(-4.76, 5.97) * mm, "end": v(-4.8, 5.98) * mm});
            skLineSegment(sketch, "E3131", {"start": v(-4.8, 5.98) * mm, "end": v(-4.82, 6) * mm});
            skLineSegment(sketch, "E3132", {"start": v(-4.82, 6) * mm, "end": v(-4.85, 6) * mm});
            skLineSegment(sketch, "E3133", {"start": v(-4.85, 6) * mm, "end": v(-4.88, 6.02) * mm});
            skArc(sketch, "E3134", {"start": v(-4.88, 6.02) * mm, "mid": v(-4.98, 5.94) * mm, "end": v(-5.08, 5.85) * mm});
            skLineSegment(sketch, "E3135", {"start": v(-3.83, 5.68) * mm, "end": v(-3.82, 5.69) * mm});
            skLineSegment(sketch, "E3136", {"start": v(-3.82, 5.69) * mm, "end": v(-3.82, 5.7) * mm});
            skLineSegment(sketch, "E3137", {"start": v(-3.82, 5.7) * mm, "end": v(-3.82, 5.7) * mm});
            skLineSegment(sketch, "E3138", {"start": v(-3.82, 5.7) * mm, "end": v(-3.82, 5.71) * mm});
            skLineSegment(sketch, "E3139", {"start": v(-3.82, 5.71) * mm, "end": v(-3.82, 5.72) * mm});
            skLineSegment(sketch, "E3140", {"start": v(-3.82, 5.72) * mm, "end": v(-3.82, 5.74) * mm});
            skLineSegment(sketch, "E3141", {"start": v(-3.82, 5.74) * mm, "end": v(-3.83, 5.75) * mm});
            skLineSegment(sketch, "E3142", {"start": v(-3.83, 5.75) * mm, "end": v(-3.83, 5.76) * mm});
            skLineSegment(sketch, "E3143", {"start": v(-3.83, 5.76) * mm, "end": v(-3.83, 5.77) * mm});
            skLineSegment(sketch, "E3144", {"start": v(-3.83, 5.77) * mm, "end": v(-3.84, 5.79) * mm});
            skLineSegment(sketch, "E3145", {"start": v(-3.84, 5.79) * mm, "end": v(-3.84, 5.8) * mm});
            skLineSegment(sketch, "E3146", {"start": v(-3.84, 5.8) * mm, "end": v(-3.85, 5.81) * mm});
            skLineSegment(sketch, "E3147", {"start": v(-3.85, 5.81) * mm, "end": v(-3.85, 5.83) * mm});
            skLineSegment(sketch, "E3148", {"start": v(-3.85, 5.83) * mm, "end": v(-3.86, 5.84) * mm});
            skLineSegment(sketch, "E3149", {"start": v(-3.86, 5.84) * mm, "end": v(-3.86, 5.86) * mm});
            skLineSegment(sketch, "E3150", {"start": v(-3.86, 5.86) * mm, "end": v(-3.87, 5.87) * mm});
            skLineSegment(sketch, "E3151", {"start": v(-3.87, 5.87) * mm, "end": v(-3.87, 5.9) * mm});
            skLineSegment(sketch, "E3152", {"start": v(-3.87, 5.9) * mm, "end": v(-3.88, 5.9) * mm});
            skLineSegment(sketch, "E3153", {"start": v(-3.88, 5.9) * mm, "end": v(-3.89, 5.93) * mm});
            skLineSegment(sketch, "E3154", {"start": v(-3.89, 5.93) * mm, "end": v(-3.9, 5.94) * mm});
            skLineSegment(sketch, "E3155", {"start": v(-3.9, 5.94) * mm, "end": v(-3.9, 5.96) * mm});
            skLineSegment(sketch, "E3156", {"start": v(-3.9, 5.96) * mm, "end": v(-3.9, 5.98) * mm});
            skLineSegment(sketch, "E3157", {"start": v(-3.9, 5.98) * mm, "end": v(-3.9, 6) * mm});
            skLineSegment(sketch, "E3158", {"start": v(-3.9, 6) * mm, "end": v(-3.91, 6.02) * mm});
            skLineSegment(sketch, "E3159", {"start": v(-3.91, 6.02) * mm, "end": v(-3.92, 6.04) * mm});
            skLineSegment(sketch, "E3160", {"start": v(-3.92, 6.04) * mm, "end": v(-3.92, 6.06) * mm});
            skLineSegment(sketch, "E3161", {"start": v(-3.92, 6.06) * mm, "end": v(-3.92, 6.09) * mm});
            skLineSegment(sketch, "E3162", {"start": v(-3.92, 6.09) * mm, "end": v(-3.93, 6.1) * mm});
            skLineSegment(sketch, "E3163", {"start": v(-3.93, 6.1) * mm, "end": v(-3.93, 6.13) * mm});
            skLineSegment(sketch, "E3164", {"start": v(-3.93, 6.13) * mm, "end": v(-3.94, 6.16) * mm});
            skLineSegment(sketch, "E3165", {"start": v(-3.94, 6.16) * mm, "end": v(-3.94, 6.18) * mm});
            skLineSegment(sketch, "E3166", {"start": v(-3.94, 6.18) * mm, "end": v(-3.95, 6.2) * mm});
            skLineSegment(sketch, "E3167", {"start": v(-3.95, 6.2) * mm, "end": v(-3.95, 6.23) * mm});
            skLineSegment(sketch, "E3168", {"start": v(-3.95, 6.23) * mm, "end": v(-3.96, 6.26) * mm});
            skLineSegment(sketch, "E3169", {"start": v(-3.96, 6.26) * mm, "end": v(-3.96, 6.28) * mm});
            skLineSegment(sketch, "E3170", {"start": v(-3.96, 6.28) * mm, "end": v(-3.96, 6.31) * mm});
            skLineSegment(sketch, "E3171", {"start": v(-3.96, 6.31) * mm, "end": v(-3.97, 6.34) * mm});
            skLineSegment(sketch, "E3172", {"start": v(-3.97, 6.34) * mm, "end": v(-3.97, 6.37) * mm});
            skLineSegment(sketch, "E3173", {"start": v(-3.97, 6.37) * mm, "end": v(-3.97, 6.4) * mm});
            skLineSegment(sketch, "E3174", {"start": v(-3.97, 6.4) * mm, "end": v(-3.98, 6.43) * mm});
            skLineSegment(sketch, "E3175", {"start": v(-3.98, 6.43) * mm, "end": v(-3.98, 6.46) * mm});
            skLineSegment(sketch, "E3176", {"start": v(-3.98, 6.46) * mm, "end": v(-3.98, 6.49) * mm});
            skLineSegment(sketch, "E3177", {"start": v(-3.98, 6.49) * mm, "end": v(-3.98, 6.52) * mm});
            skLineSegment(sketch, "E3178", {"start": v(-3.98, 6.52) * mm, "end": v(-3.98, 6.55) * mm});
            skLineSegment(sketch, "E3179", {"start": v(-3.98, 6.55) * mm, "end": v(-3.99, 6.58) * mm});
            skLineSegment(sketch, "E3180", {"start": v(-3.99, 6.58) * mm, "end": v(-3.99, 6.61) * mm});
            skLineSegment(sketch, "E3181", {"start": v(-3.99, 6.61) * mm, "end": v(-3.99, 6.65) * mm});
            skLineSegment(sketch, "E3182", {"start": v(-3, 6.16) * mm, "end": v(-3.02, 6.15) * mm});
            skLineSegment(sketch, "E3183", {"start": v(-3.02, 6.15) * mm, "end": v(-3.02, 6.15) * mm});
            skLineSegment(sketch, "E3184", {"start": v(-3.02, 6.15) * mm, "end": v(-3.03, 6.16) * mm});
            skLineSegment(sketch, "E3185", {"start": v(-3.03, 6.16) * mm, "end": v(-3.04, 6.16) * mm});
            skLineSegment(sketch, "E3186", {"start": v(-3.04, 6.16) * mm, "end": v(-3.05, 6.17) * mm});
            skLineSegment(sketch, "E3187", {"start": v(-3.05, 6.17) * mm, "end": v(-3.06, 6.18) * mm});
            skLineSegment(sketch, "E3188", {"start": v(-3.06, 6.18) * mm, "end": v(-3.07, 6.19) * mm});
            skLineSegment(sketch, "E3189", {"start": v(-3.07, 6.19) * mm, "end": v(-3.07, 6.2) * mm});
            skLineSegment(sketch, "E3190", {"start": v(-3.07, 6.2) * mm, "end": v(-3.08, 6.2) * mm});
            skLineSegment(sketch, "E3191", {"start": v(-3.08, 6.2) * mm, "end": v(-3.1, 6.22) * mm});
            skLineSegment(sketch, "E3192", {"start": v(-3.1, 6.22) * mm, "end": v(-3.1, 6.23) * mm});
            skLineSegment(sketch, "E3193", {"start": v(-3.1, 6.23) * mm, "end": v(-3.11, 6.24) * mm});
            skLineSegment(sketch, "E3194", {"start": v(-3.11, 6.24) * mm, "end": v(-3.12, 6.25) * mm});
            skLineSegment(sketch, "E3195", {"start": v(-3.12, 6.25) * mm, "end": v(-3.13, 6.26) * mm});
            skLineSegment(sketch, "E3196", {"start": v(-3.13, 6.26) * mm, "end": v(-3.14, 6.28) * mm});
            skLineSegment(sketch, "E3197", {"start": v(-3.14, 6.28) * mm, "end": v(-3.15, 6.29) * mm});
            skLineSegment(sketch, "E3198", {"start": v(-3.15, 6.29) * mm, "end": v(-3.16, 6.3) * mm});
            skLineSegment(sketch, "E3199", {"start": v(-3.16, 6.3) * mm, "end": v(-3.18, 6.31) * mm});
            skLineSegment(sketch, "E3200", {"start": v(-3.18, 6.31) * mm, "end": v(-3.19, 6.33) * mm});
            skLineSegment(sketch, "E3201", {"start": v(-3.19, 6.33) * mm, "end": v(-3.2, 6.34) * mm});
            skLineSegment(sketch, "E3202", {"start": v(-3.2, 6.34) * mm, "end": v(-3.22, 6.35) * mm});
            skLineSegment(sketch, "E3203", {"start": v(-3.22, 6.35) * mm, "end": v(-3.23, 6.37) * mm});
            skLineSegment(sketch, "E3204", {"start": v(-3.23, 6.37) * mm, "end": v(-3.24, 6.38) * mm});
            skLineSegment(sketch, "E3205", {"start": v(-3.24, 6.38) * mm, "end": v(-3.26, 6.4) * mm});
            skLineSegment(sketch, "E3206", {"start": v(-3.26, 6.4) * mm, "end": v(-3.28, 6.41) * mm});
            skLineSegment(sketch, "E3207", {"start": v(-3.28, 6.41) * mm, "end": v(-3.3, 6.43) * mm});
            skLineSegment(sketch, "E3208", {"start": v(-3.3, 6.43) * mm, "end": v(-3.3, 6.44) * mm});
            skLineSegment(sketch, "E3209", {"start": v(-3.3, 6.44) * mm, "end": v(-3.33, 6.46) * mm});
            skLineSegment(sketch, "E3210", {"start": v(-3.33, 6.46) * mm, "end": v(-3.34, 6.47) * mm});
            skLineSegment(sketch, "E3211", {"start": v(-3.34, 6.47) * mm, "end": v(-3.36, 6.49) * mm});
            skLineSegment(sketch, "E3212", {"start": v(-3.36, 6.49) * mm, "end": v(-3.38, 6.5) * mm});
            skLineSegment(sketch, "E3213", {"start": v(-3.38, 6.5) * mm, "end": v(-3.4, 6.52) * mm});
            skLineSegment(sketch, "E3214", {"start": v(-3.4, 6.52) * mm, "end": v(-3.42, 6.54) * mm});
            skLineSegment(sketch, "E3215", {"start": v(-3.42, 6.54) * mm, "end": v(-3.44, 6.55) * mm});
            skLineSegment(sketch, "E3216", {"start": v(-3.44, 6.55) * mm, "end": v(-3.46, 6.57) * mm});
            skLineSegment(sketch, "E3217", {"start": v(-3.46, 6.57) * mm, "end": v(-3.48, 6.59) * mm});
            skLineSegment(sketch, "E3218", {"start": v(-3.48, 6.59) * mm, "end": v(-3.5, 6.6) * mm});
            skLineSegment(sketch, "E3219", {"start": v(-3.5, 6.6) * mm, "end": v(-3.53, 6.62) * mm});
            skLineSegment(sketch, "E3220", {"start": v(-3.53, 6.62) * mm, "end": v(-3.55, 6.64) * mm});
            skLineSegment(sketch, "E3221", {"start": v(-3.55, 6.64) * mm, "end": v(-3.58, 6.66) * mm});
            skLineSegment(sketch, "E3222", {"start": v(-3.58, 6.66) * mm, "end": v(-3.6, 6.67) * mm});
            skLineSegment(sketch, "E3223", {"start": v(-3.6, 6.67) * mm, "end": v(-3.63, 6.7) * mm});
            skLineSegment(sketch, "E3224", {"start": v(-3.63, 6.7) * mm, "end": v(-3.65, 6.7) * mm});
            skLineSegment(sketch, "E3225", {"start": v(-3.65, 6.7) * mm, "end": v(-3.68, 6.73) * mm});
            skLineSegment(sketch, "E3226", {"start": v(-3.68, 6.73) * mm, "end": v(-3.7, 6.74) * mm});
            skLineSegment(sketch, "E3227", {"start": v(-3.7, 6.74) * mm, "end": v(-3.73, 6.76) * mm});
            skLineSegment(sketch, "E3228", {"start": v(-3.73, 6.76) * mm, "end": v(-3.76, 6.78) * mm});
            skArc(sketch, "E3229", {"start": v(-3.76, 6.78) * mm, "mid": v(-3.88, 6.71) * mm, "end": v(-3.99, 6.65) * mm});
            skLineSegment(sketch, "E3230", {"start": v(-2.78, 6.26) * mm, "end": v(-2.78, 6.27) * mm});
            skLineSegment(sketch, "E3231", {"start": v(-2.78, 6.27) * mm, "end": v(-2.77, 6.27) * mm});
            skLineSegment(sketch, "E3232", {"start": v(-2.77, 6.27) * mm, "end": v(-2.77, 6.28) * mm});
            skLineSegment(sketch, "E3233", {"start": v(-2.77, 6.28) * mm, "end": v(-2.77, 6.29) * mm});
            skLineSegment(sketch, "E3234", {"start": v(-2.77, 6.29) * mm, "end": v(-2.77, 6.3) * mm});
            skLineSegment(sketch, "E3235", {"start": v(-2.77, 6.3) * mm, "end": v(-2.77, 6.31) * mm});
            skLineSegment(sketch, "E3236", {"start": v(-2.77, 6.31) * mm, "end": v(-2.77, 6.33) * mm});
            skLineSegment(sketch, "E3237", {"start": v(-2.77, 6.33) * mm, "end": v(-2.77, 6.34) * mm});
            skLineSegment(sketch, "E3238", {"start": v(-2.77, 6.34) * mm, "end": v(-2.77, 6.35) * mm});
            skLineSegment(sketch, "E3239", {"start": v(-2.77, 6.35) * mm, "end": v(-2.78, 6.37) * mm});
            skLineSegment(sketch, "E3240", {"start": v(-2.78, 6.37) * mm, "end": v(-2.78, 6.38) * mm});
            skLineSegment(sketch, "E3241", {"start": v(-2.78, 6.38) * mm, "end": v(-2.78, 6.4) * mm});
            skLineSegment(sketch, "E3242", {"start": v(-2.78, 6.4) * mm, "end": v(-2.78, 6.4) * mm});
            skLineSegment(sketch, "E3243", {"start": v(-2.78, 6.4) * mm, "end": v(-2.79, 6.42) * mm});
            skLineSegment(sketch, "E3244", {"start": v(-2.79, 6.42) * mm, "end": v(-2.79, 6.44) * mm});
            skLineSegment(sketch, "E3245", {"start": v(-2.79, 6.44) * mm, "end": v(-2.8, 6.46) * mm});
            skLineSegment(sketch, "E3246", {"start": v(-2.8, 6.46) * mm, "end": v(-2.8, 6.47) * mm});
            skLineSegment(sketch, "E3247", {"start": v(-2.8, 6.47) * mm, "end": v(-2.8, 6.5) * mm});
            skLineSegment(sketch, "E3248", {"start": v(-2.8, 6.5) * mm, "end": v(-2.8, 6.51) * mm});
            skLineSegment(sketch, "E3249", {"start": v(-2.8, 6.51) * mm, "end": v(-2.8, 6.53) * mm});
            skLineSegment(sketch, "E3250", {"start": v(-2.8, 6.53) * mm, "end": v(-2.8, 6.55) * mm});
            skLineSegment(sketch, "E3251", {"start": v(-2.8, 6.55) * mm, "end": v(-2.8, 6.57) * mm});
            skLineSegment(sketch, "E3252", {"start": v(-2.8, 6.57) * mm, "end": v(-2.8, 6.59) * mm});
            skLineSegment(sketch, "E3253", {"start": v(-2.8, 6.59) * mm, "end": v(-2.8, 6.6) * mm});
            skLineSegment(sketch, "E3254", {"start": v(-2.8, 6.6) * mm, "end": v(-2.8, 6.63) * mm});
            skLineSegment(sketch, "E3255", {"start": v(-2.8, 6.63) * mm, "end": v(-2.8, 6.65) * mm});
            skLineSegment(sketch, "E3256", {"start": v(-2.8, 6.65) * mm, "end": v(-2.8, 6.68) * mm});
            skLineSegment(sketch, "E3257", {"start": v(-2.8, 6.68) * mm, "end": v(-2.8, 6.7) * mm});
            skLineSegment(sketch, "E3258", {"start": v(-2.8, 6.7) * mm, "end": v(-2.8, 6.72) * mm});
            skLineSegment(sketch, "E3259", {"start": v(-2.8, 6.72) * mm, "end": v(-2.8, 6.75) * mm});
            skLineSegment(sketch, "E3260", {"start": v(-2.8, 6.75) * mm, "end": v(-2.8, 6.77) * mm});
            skLineSegment(sketch, "E3261", {"start": v(-2.8, 6.77) * mm, "end": v(-2.8, 6.8) * mm});
            skLineSegment(sketch, "E3262", {"start": v(-2.8, 6.8) * mm, "end": v(-2.8, 6.82) * mm});
            skLineSegment(sketch, "E3263", {"start": v(-2.8, 6.82) * mm, "end": v(-2.8, 6.85) * mm});
            skLineSegment(sketch, "E3264", {"start": v(-2.8, 6.85) * mm, "end": v(-2.8, 6.88) * mm});
            skLineSegment(sketch, "E3265", {"start": v(-2.8, 6.88) * mm, "end": v(-2.8, 6.9) * mm});
            skLineSegment(sketch, "E3266", {"start": v(-2.8, 6.9) * mm, "end": v(-2.8, 6.93) * mm});
            skLineSegment(sketch, "E3267", {"start": v(-2.8, 6.93) * mm, "end": v(-2.8, 6.96) * mm});
            skLineSegment(sketch, "E3268", {"start": v(-2.8, 6.96) * mm, "end": v(-2.8, 6.99) * mm});
            skLineSegment(sketch, "E3269", {"start": v(-2.8, 6.99) * mm, "end": v(-2.8, 7.02) * mm});
            skLineSegment(sketch, "E3270", {"start": v(-2.8, 7.02) * mm, "end": v(-2.8, 7.05) * mm});
            skLineSegment(sketch, "E3271", {"start": v(-2.8, 7.05) * mm, "end": v(-2.8, 7.08) * mm});
            skLineSegment(sketch, "E3272", {"start": v(-2.8, 7.08) * mm, "end": v(-2.8, 7.1) * mm});
            skLineSegment(sketch, "E3273", {"start": v(-2.8, 7.1) * mm, "end": v(-2.79, 7.14) * mm});
            skLineSegment(sketch, "E3274", {"start": v(-2.79, 7.14) * mm, "end": v(-2.78, 7.17) * mm});
            skLineSegment(sketch, "E3275", {"start": v(-2.78, 7.17) * mm, "end": v(-2.78, 7.2) * mm});
            skLineSegment(sketch, "E3276", {"start": v(-2.78, 7.2) * mm, "end": v(-2.77, 7.24) * mm});
            skLineSegment(sketch, "E3277", {"start": v(-1.9, 6.58) * mm, "end": v(-1.9, 6.58) * mm});
            skLineSegment(sketch, "E3278", {"start": v(-1.9, 6.58) * mm, "end": v(-1.9, 6.59) * mm});
            skLineSegment(sketch, "E3279", {"start": v(-1.9, 6.59) * mm, "end": v(-1.91, 6.59) * mm});
            skLineSegment(sketch, "E3280", {"start": v(-1.91, 6.59) * mm, "end": v(-1.92, 6.6) * mm});
            skLineSegment(sketch, "E3281", {"start": v(-1.92, 6.6) * mm, "end": v(-1.93, 6.6) * mm});
            skLineSegment(sketch, "E3282", {"start": v(-1.93, 6.6) * mm, "end": v(-1.94, 6.62) * mm});
            skLineSegment(sketch, "E3283", {"start": v(-1.94, 6.62) * mm, "end": v(-1.95, 6.63) * mm});
            skLineSegment(sketch, "E3284", {"start": v(-1.95, 6.63) * mm, "end": v(-1.95, 6.64) * mm});
            skLineSegment(sketch, "E3285", {"start": v(-1.95, 6.64) * mm, "end": v(-1.96, 6.65) * mm});
            skLineSegment(sketch, "E3286", {"start": v(-1.96, 6.65) * mm, "end": v(-1.96, 6.66) * mm});
            skLineSegment(sketch, "E3287", {"start": v(-1.96, 6.66) * mm, "end": v(-1.97, 6.67) * mm});
            skLineSegment(sketch, "E3288", {"start": v(-1.97, 6.67) * mm, "end": v(-1.98, 6.69) * mm});
            skLineSegment(sketch, "E3289", {"start": v(-1.98, 6.69) * mm, "end": v(-1.99, 6.7) * mm});
            skLineSegment(sketch, "E3290", {"start": v(-1.99, 6.7) * mm, "end": v(-2, 6.71) * mm});
            skLineSegment(sketch, "E3291", {"start": v(-2, 6.71) * mm, "end": v(-2, 6.73) * mm});
            skLineSegment(sketch, "E3292", {"start": v(-2, 6.73) * mm, "end": v(-2.01, 6.74) * mm});
            skLineSegment(sketch, "E3293", {"start": v(-2.01, 6.74) * mm, "end": v(-2.02, 6.75) * mm});
            skLineSegment(sketch, "E3294", {"start": v(-2.02, 6.75) * mm, "end": v(-2.03, 6.77) * mm});
            skLineSegment(sketch, "E3295", {"start": v(-2.03, 6.77) * mm, "end": v(-2.04, 6.78) * mm});
            skLineSegment(sketch, "E3296", {"start": v(-2.04, 6.78) * mm, "end": v(-2.05, 6.8) * mm});
            skLineSegment(sketch, "E3297", {"start": v(-2.05, 6.8) * mm, "end": v(-2.06, 6.82) * mm});
            skLineSegment(sketch, "E3298", {"start": v(-2.06, 6.82) * mm, "end": v(-2.08, 6.83) * mm});
            skLineSegment(sketch, "E3299", {"start": v(-2.08, 6.83) * mm, "end": v(-2.09, 6.85) * mm});
            skLineSegment(sketch, "E3300", {"start": v(-2.09, 6.85) * mm, "end": v(-2.1, 6.87) * mm});
            skLineSegment(sketch, "E3301", {"start": v(-2.1, 6.87) * mm, "end": v(-2.11, 6.88) * mm});
            skLineSegment(sketch, "E3302", {"start": v(-2.11, 6.88) * mm, "end": v(-2.13, 6.9) * mm});
            skLineSegment(sketch, "E3303", {"start": v(-2.13, 6.9) * mm, "end": v(-2.14, 6.92) * mm});
            skLineSegment(sketch, "E3304", {"start": v(-2.14, 6.92) * mm, "end": v(-2.15, 6.94) * mm});
            skLineSegment(sketch, "E3305", {"start": v(-2.15, 6.94) * mm, "end": v(-2.17, 6.96) * mm});
            skLineSegment(sketch, "E3306", {"start": v(-2.17, 6.96) * mm, "end": v(-2.18, 6.97) * mm});
            skLineSegment(sketch, "E3307", {"start": v(-2.18, 6.97) * mm, "end": v(-2.2, 7) * mm});
            skLineSegment(sketch, "E3308", {"start": v(-2.2, 7) * mm, "end": v(-2.22, 7.01) * mm});
            skLineSegment(sketch, "E3309", {"start": v(-2.22, 7.01) * mm, "end": v(-2.23, 7.03) * mm});
            skLineSegment(sketch, "E3310", {"start": v(-2.23, 7.03) * mm, "end": v(-2.25, 7.05) * mm});
            skLineSegment(sketch, "E3311", {"start": v(-2.25, 7.05) * mm, "end": v(-2.27, 7.07) * mm});
            skLineSegment(sketch, "E3312", {"start": v(-2.27, 7.07) * mm, "end": v(-2.29, 7.1) * mm});
            skLineSegment(sketch, "E3313", {"start": v(-2.29, 7.1) * mm, "end": v(-2.3, 7.11) * mm});
            skLineSegment(sketch, "E3314", {"start": v(-2.3, 7.11) * mm, "end": v(-2.33, 7.13) * mm});
            skLineSegment(sketch, "E3315", {"start": v(-2.33, 7.13) * mm, "end": v(-2.35, 7.15) * mm});
            skLineSegment(sketch, "E3316", {"start": v(-2.35, 7.15) * mm, "end": v(-2.37, 7.18) * mm});
            skLineSegment(sketch, "E3317", {"start": v(-2.37, 7.18) * mm, "end": v(-2.39, 7.2) * mm});
            skLineSegment(sketch, "E3318", {"start": v(-2.39, 7.2) * mm, "end": v(-2.41, 7.22) * mm});
            skLineSegment(sketch, "E3319", {"start": v(-2.41, 7.22) * mm, "end": v(-2.43, 7.24) * mm});
            skLineSegment(sketch, "E3320", {"start": v(-2.43, 7.24) * mm, "end": v(-2.46, 7.26) * mm});
            skLineSegment(sketch, "E3321", {"start": v(-2.46, 7.26) * mm, "end": v(-2.48, 7.28) * mm});
            skLineSegment(sketch, "E3322", {"start": v(-2.48, 7.28) * mm, "end": v(-2.5, 7.3) * mm});
            skLineSegment(sketch, "E3323", {"start": v(-2.5, 7.3) * mm, "end": v(-2.53, 7.33) * mm});
            skArc(sketch, "E3324", {"start": v(-2.53, 7.33) * mm, "mid": v(-2.65, 7.28) * mm, "end": v(-2.77, 7.24) * mm});
            skLineSegment(sketch, "E3325", {"start": v(-1.65, 6.65) * mm, "end": v(-1.65, 6.65) * mm});
            skLineSegment(sketch, "E3326", {"start": v(-1.65, 6.65) * mm, "end": v(-1.64, 6.66) * mm});
            skLineSegment(sketch, "E3327", {"start": v(-1.64, 6.66) * mm, "end": v(-1.64, 6.66) * mm});
            skLineSegment(sketch, "E3328", {"start": v(-1.64, 6.66) * mm, "end": v(-1.63, 6.67) * mm});
            skLineSegment(sketch, "E3329", {"start": v(-1.63, 6.67) * mm, "end": v(-1.63, 6.68) * mm});
            skLineSegment(sketch, "E3330", {"start": v(-1.63, 6.68) * mm, "end": v(-1.63, 6.7) * mm});
            skLineSegment(sketch, "E3331", {"start": v(-1.63, 6.7) * mm, "end": v(-1.63, 6.71) * mm});
            skLineSegment(sketch, "E3332", {"start": v(-1.63, 6.71) * mm, "end": v(-1.63, 6.72) * mm});
            skLineSegment(sketch, "E3333", {"start": v(-1.63, 6.72) * mm, "end": v(-1.63, 6.74) * mm});
            skLineSegment(sketch, "E3334", {"start": v(-1.63, 6.74) * mm, "end": v(-1.63, 6.75) * mm});
            skLineSegment(sketch, "E3335", {"start": v(-1.63, 6.75) * mm, "end": v(-1.63, 6.76) * mm});
            skLineSegment(sketch, "E3336", {"start": v(-1.63, 6.76) * mm, "end": v(-1.63, 6.78) * mm});
            skLineSegment(sketch, "E3337", {"start": v(-1.63, 6.78) * mm, "end": v(-1.63, 6.8) * mm});
            skLineSegment(sketch, "E3338", {"start": v(-1.63, 6.8) * mm, "end": v(-1.63, 6.81) * mm});
            skLineSegment(sketch, "E3339", {"start": v(-1.63, 6.81) * mm, "end": v(-1.63, 6.83) * mm});
            skLineSegment(sketch, "E3340", {"start": v(-1.63, 6.83) * mm, "end": v(-1.63, 6.84) * mm});
            skLineSegment(sketch, "E3341", {"start": v(-1.63, 6.84) * mm, "end": v(-1.63, 6.86) * mm});
            skLineSegment(sketch, "E3342", {"start": v(-1.63, 6.86) * mm, "end": v(-1.63, 6.88) * mm});
            skLineSegment(sketch, "E3343", {"start": v(-1.63, 6.88) * mm, "end": v(-1.62, 6.9) * mm});
            skLineSegment(sketch, "E3344", {"start": v(-1.62, 6.9) * mm, "end": v(-1.62, 6.92) * mm});
            skLineSegment(sketch, "E3345", {"start": v(-1.62, 6.92) * mm, "end": v(-1.62, 6.94) * mm});
            skLineSegment(sketch, "E3346", {"start": v(-1.62, 6.94) * mm, "end": v(-1.62, 6.96) * mm});
            skLineSegment(sketch, "E3347", {"start": v(-1.62, 6.96) * mm, "end": v(-1.62, 6.98) * mm});
            skLineSegment(sketch, "E3348", {"start": v(-1.62, 6.98) * mm, "end": v(-1.61, 7) * mm});
            skLineSegment(sketch, "E3349", {"start": v(-1.61, 7) * mm, "end": v(-1.61, 7.02) * mm});
            skLineSegment(sketch, "E3350", {"start": v(-1.61, 7.02) * mm, "end": v(-1.6, 7.04) * mm});
            skLineSegment(sketch, "E3351", {"start": v(-1.6, 7.04) * mm, "end": v(-1.6, 7.06) * mm});
            skLineSegment(sketch, "E3352", {"start": v(-1.6, 7.06) * mm, "end": v(-1.6, 7.09) * mm});
            skLineSegment(sketch, "E3353", {"start": v(-1.6, 7.09) * mm, "end": v(-1.6, 7.1) * mm});
            skLineSegment(sketch, "E3354", {"start": v(-1.6, 7.1) * mm, "end": v(-1.6, 7.13) * mm});
            skLineSegment(sketch, "E3355", {"start": v(-1.6, 7.13) * mm, "end": v(-1.6, 7.16) * mm});
            skLineSegment(sketch, "E3356", {"start": v(-1.6, 7.16) * mm, "end": v(-1.59, 7.18) * mm});
            skLineSegment(sketch, "E3357", {"start": v(-1.59, 7.18) * mm, "end": v(-1.58, 7.2) * mm});
            skLineSegment(sketch, "E3358", {"start": v(-1.58, 7.2) * mm, "end": v(-1.58, 7.23) * mm});
            skLineSegment(sketch, "E3359", {"start": v(-1.58, 7.23) * mm, "end": v(-1.57, 7.26) * mm});
            skLineSegment(sketch, "E3360", {"start": v(-1.57, 7.26) * mm, "end": v(-1.57, 7.29) * mm});
            skLineSegment(sketch, "E3361", {"start": v(-1.57, 7.29) * mm, "end": v(-1.56, 7.31) * mm});
            skLineSegment(sketch, "E3362", {"start": v(-1.56, 7.31) * mm, "end": v(-1.55, 7.34) * mm});
            skLineSegment(sketch, "E3363", {"start": v(-1.55, 7.34) * mm, "end": v(-1.55, 7.37) * mm});
            skLineSegment(sketch, "E3364", {"start": v(-1.55, 7.37) * mm, "end": v(-1.54, 7.4) * mm});
            skLineSegment(sketch, "E3365", {"start": v(-1.54, 7.4) * mm, "end": v(-1.53, 7.43) * mm});
            skLineSegment(sketch, "E3366", {"start": v(-1.53, 7.43) * mm, "end": v(-1.52, 7.46) * mm});
            skLineSegment(sketch, "E3367", {"start": v(-1.52, 7.46) * mm, "end": v(-1.51, 7.49) * mm});
            skLineSegment(sketch, "E3368", {"start": v(-1.51, 7.49) * mm, "end": v(-1.5, 7.52) * mm});
            skLineSegment(sketch, "E3369", {"start": v(-1.5, 7.52) * mm, "end": v(-1.5, 7.55) * mm});
            skLineSegment(sketch, "E3370", {"start": v(-1.5, 7.55) * mm, "end": v(-1.49, 7.58) * mm});
            skLineSegment(sketch, "E3371", {"start": v(-1.49, 7.58) * mm, "end": v(-1.47, 7.61) * mm});
            skLineSegment(sketch, "E3372", {"start": v(-0.72, 6.81) * mm, "end": v(-0.73, 6.81) * mm});
            skLineSegment(sketch, "E3373", {"start": v(-0.73, 6.81) * mm, "end": v(-0.73, 6.82) * mm});
            skLineSegment(sketch, "E3374", {"start": v(-0.73, 6.82) * mm, "end": v(-0.74, 6.82) * mm});
            skLineSegment(sketch, "E3375", {"start": v(-0.74, 6.82) * mm, "end": v(-0.75, 6.83) * mm});
            skLineSegment(sketch, "E3376", {"start": v(-0.75, 6.83) * mm, "end": v(-0.75, 6.84) * mm});
            skLineSegment(sketch, "E3377", {"start": v(-0.75, 6.84) * mm, "end": v(-0.76, 6.85) * mm});
            skLineSegment(sketch, "E3378", {"start": v(-0.76, 6.85) * mm, "end": v(-0.77, 6.87) * mm});
            skLineSegment(sketch, "E3379", {"start": v(-0.77, 6.87) * mm, "end": v(-0.77, 6.88) * mm});
            skLineSegment(sketch, "E3380", {"start": v(-0.77, 6.88) * mm, "end": v(-0.77, 6.89) * mm});
            skLineSegment(sketch, "E3381", {"start": v(-0.77, 6.89) * mm, "end": v(-0.78, 6.9) * mm});
            skLineSegment(sketch, "E3382", {"start": v(-0.78, 6.9) * mm, "end": v(-0.78, 6.91) * mm});
            skLineSegment(sketch, "E3383", {"start": v(-0.78, 6.91) * mm, "end": v(-0.79, 6.93) * mm});
            skLineSegment(sketch, "E3384", {"start": v(-0.79, 6.93) * mm, "end": v(-0.8, 6.94) * mm});
            skLineSegment(sketch, "E3385", {"start": v(-0.8, 6.94) * mm, "end": v(-0.8, 6.96) * mm});
            skLineSegment(sketch, "E3386", {"start": v(-0.8, 6.96) * mm, "end": v(-0.8, 6.97) * mm});
            skLineSegment(sketch, "E3387", {"start": v(-0.8, 6.97) * mm, "end": v(-0.81, 6.99) * mm});
            skLineSegment(sketch, "E3388", {"start": v(-0.81, 6.99) * mm, "end": v(-0.82, 7) * mm});
            skLineSegment(sketch, "E3389", {"start": v(-0.82, 7) * mm, "end": v(-0.83, 7.02) * mm});
            skLineSegment(sketch, "E3390", {"start": v(-0.83, 7.02) * mm, "end": v(-0.83, 7.04) * mm});
            skLineSegment(sketch, "E3391", {"start": v(-0.83, 7.04) * mm, "end": v(-0.84, 7.05) * mm});
            skLineSegment(sketch, "E3392", {"start": v(-0.84, 7.05) * mm, "end": v(-0.85, 7.07) * mm});
            skLineSegment(sketch, "E3393", {"start": v(-0.85, 7.07) * mm, "end": v(-0.86, 7.09) * mm});
            skLineSegment(sketch, "E3394", {"start": v(-0.86, 7.09) * mm, "end": v(-0.87, 7.1) * mm});
            skLineSegment(sketch, "E3395", {"start": v(-0.87, 7.1) * mm, "end": v(-0.88, 7.13) * mm});
            skLineSegment(sketch, "E3396", {"start": v(-0.88, 7.13) * mm, "end": v(-0.89, 7.15) * mm});
            skLineSegment(sketch, "E3397", {"start": v(-0.89, 7.15) * mm, "end": v(-0.9, 7.17) * mm});
            skLineSegment(sketch, "E3398", {"start": v(-0.9, 7.17) * mm, "end": v(-0.9, 7.19) * mm});
            skLineSegment(sketch, "E3399", {"start": v(-0.9, 7.19) * mm, "end": v(-0.92, 7.2) * mm});
            skLineSegment(sketch, "E3400", {"start": v(-0.92, 7.2) * mm, "end": v(-0.93, 7.23) * mm});
            skLineSegment(sketch, "E3401", {"start": v(-0.93, 7.23) * mm, "end": v(-0.94, 7.25) * mm});
            skLineSegment(sketch, "E3402", {"start": v(-0.94, 7.25) * mm, "end": v(-0.95, 7.27) * mm});
            skLineSegment(sketch, "E3403", {"start": v(-0.95, 7.27) * mm, "end": v(-0.97, 7.3) * mm});
            skLineSegment(sketch, "E3404", {"start": v(-0.97, 7.3) * mm, "end": v(-0.98, 7.31) * mm});
            skLineSegment(sketch, "E3405", {"start": v(-0.98, 7.31) * mm, "end": v(-1, 7.34) * mm});
            skLineSegment(sketch, "E3406", {"start": v(-1, 7.34) * mm, "end": v(-1, 7.36) * mm});
            skLineSegment(sketch, "E3407", {"start": v(-1, 7.36) * mm, "end": v(-1.02, 7.38) * mm});
            skLineSegment(sketch, "E3408", {"start": v(-1.02, 7.38) * mm, "end": v(-1.04, 7.4) * mm});
            skLineSegment(sketch, "E3409", {"start": v(-1.04, 7.4) * mm, "end": v(-1.05, 7.43) * mm});
            skLineSegment(sketch, "E3410", {"start": v(-1.05, 7.43) * mm, "end": v(-1.07, 7.45) * mm});
            skLineSegment(sketch, "E3411", {"start": v(-1.07, 7.45) * mm, "end": v(-1.09, 7.48) * mm});
            skLineSegment(sketch, "E3412", {"start": v(-1.09, 7.48) * mm, "end": v(-1.1, 7.5) * mm});
            skLineSegment(sketch, "E3413", {"start": v(-1.1, 7.5) * mm, "end": v(-1.12, 7.53) * mm});
            skLineSegment(sketch, "E3414", {"start": v(-1.12, 7.53) * mm, "end": v(-1.14, 7.55) * mm});
            skLineSegment(sketch, "E3415", {"start": v(-1.14, 7.55) * mm, "end": v(-1.16, 7.58) * mm});
            skLineSegment(sketch, "E3416", {"start": v(-1.16, 7.58) * mm, "end": v(-1.18, 7.6) * mm});
            skLineSegment(sketch, "E3417", {"start": v(-1.18, 7.6) * mm, "end": v(-1.2, 7.63) * mm});
            skLineSegment(sketch, "E3418", {"start": v(-1.2, 7.63) * mm, "end": v(-1.22, 7.66) * mm});
            skArc(sketch, "E3419", {"start": v(-1.22, 7.66) * mm, "mid": v(-1.35, 7.63) * mm, "end": v(-1.47, 7.61) * mm});
            skArc(sketch, "E3420", {"start": v(0.72, 6.81) * mm, "mid": v(0.6, 6.83) * mm, "end": v(0.47, 6.84) * mm});
            skArc(sketch, "E3421", {"start": v(1.9, 6.58) * mm, "mid": v(1.77, 6.62) * mm, "end": v(1.65, 6.65) * mm});
            skArc(sketch, "E3422", {"start": v(3, 6.16) * mm, "mid": v(2.9, 6.21) * mm, "end": v(2.78, 6.26) * mm});
            skArc(sketch, "E3423", {"start": v(4.03, 5.54) * mm, "mid": v(3.93, 5.61) * mm, "end": v(3.83, 5.68) * mm});
            skArc(sketch, "E3424", {"start": v(4.93, 4.76) * mm, "mid": v(4.85, 4.85) * mm, "end": v(4.76, 4.93) * mm});
            skArc(sketch, "E3425", {"start": v(5.68, 3.83) * mm, "mid": v(5.61, 3.93) * mm, "end": v(5.54, 4.03) * mm});
            skArc(sketch, "E3426", {"start": v(6.26, 2.78) * mm, "mid": v(6.21, 2.9) * mm, "end": v(6.16, 3) * mm});
            skArc(sketch, "E3427", {"start": v(6.65, 1.65) * mm, "mid": v(6.62, 1.77) * mm, "end": v(6.58, 1.9) * mm});
            skArc(sketch, "E3428", {"start": v(6.84, 0.47) * mm, "mid": v(6.83, 0.6) * mm, "end": v(6.81, 0.72) * mm});
            skArc(sketch, "E3429", {"start": v(6.81, -0.72) * mm, "mid": v(6.83, -0.6) * mm, "end": v(6.84, -0.47) * mm});
            skArc(sketch, "E3430", {"start": v(6.58, -1.9) * mm, "mid": v(6.62, -1.77) * mm, "end": v(6.65, -1.65) * mm});
            skArc(sketch, "E3431", {"start": v(6.16, -3) * mm, "mid": v(6.21, -2.9) * mm, "end": v(6.26, -2.78) * mm});
            skArc(sketch, "E3432", {"start": v(5.54, -4.03) * mm, "mid": v(5.61, -3.93) * mm, "end": v(5.68, -3.83) * mm});
            skArc(sketch, "E3433", {"start": v(4.76, -4.93) * mm, "mid": v(4.85, -4.85) * mm, "end": v(4.93, -4.76) * mm});
            skArc(sketch, "E3434", {"start": v(3.83, -5.68) * mm, "mid": v(3.93, -5.61) * mm, "end": v(4.03, -5.54) * mm});
            skArc(sketch, "E3435", {"start": v(2.78, -6.26) * mm, "mid": v(2.9, -6.21) * mm, "end": v(3, -6.16) * mm});
            skArc(sketch, "E3436", {"start": v(1.65, -6.65) * mm, "mid": v(1.77, -6.62) * mm, "end": v(1.9, -6.58) * mm});
            skArc(sketch, "E3437", {"start": v(0.47, -6.84) * mm, "mid": v(0.6, -6.83) * mm, "end": v(0.72, -6.81) * mm});
            skArc(sketch, "E3438", {"start": v(-0.72, -6.81) * mm, "mid": v(-0.6, -6.83) * mm, "end": v(-0.47, -6.84) * mm});
            skArc(sketch, "E3439", {"start": v(-1.9, -6.58) * mm, "mid": v(-1.77, -6.62) * mm, "end": v(-1.65, -6.65) * mm});
            skArc(sketch, "E3440", {"start": v(-3, -6.16) * mm, "mid": v(-2.9, -6.21) * mm, "end": v(-2.78, -6.26) * mm});
            skArc(sketch, "E3441", {"start": v(-4.03, -5.54) * mm, "mid": v(-3.93, -5.61) * mm, "end": v(-3.83, -5.68) * mm});
            skArc(sketch, "E3442", {"start": v(-4.93, -4.76) * mm, "mid": v(-4.85, -4.85) * mm, "end": v(-4.76, -4.93) * mm});
            skArc(sketch, "E3443", {"start": v(-5.68, -3.83) * mm, "mid": v(-5.61, -3.93) * mm, "end": v(-5.54, -4.03) * mm});
            skArc(sketch, "E3444", {"start": v(-6.26, -2.78) * mm, "mid": v(-6.21, -2.9) * mm, "end": v(-6.16, -3) * mm});
            skArc(sketch, "E3445", {"start": v(-6.65, -1.65) * mm, "mid": v(-6.62, -1.77) * mm, "end": v(-6.58, -1.9) * mm});
            skArc(sketch, "E3446", {"start": v(-6.84, -0.47) * mm, "mid": v(-6.83, -0.6) * mm, "end": v(-6.81, -0.72) * mm});
            skArc(sketch, "E3447", {"start": v(-6.81, 0.72) * mm, "mid": v(-6.83, 0.6) * mm, "end": v(-6.84, 0.47) * mm});
            skArc(sketch, "E3448", {"start": v(-6.58, 1.9) * mm, "mid": v(-6.62, 1.77) * mm, "end": v(-6.65, 1.65) * mm});
            skArc(sketch, "E3449", {"start": v(-6.16, 3) * mm, "mid": v(-6.21, 2.9) * mm, "end": v(-6.26, 2.78) * mm});
            skArc(sketch, "E3450", {"start": v(-5.54, 4.03) * mm, "mid": v(-5.61, 3.93) * mm, "end": v(-5.68, 3.83) * mm});
            skArc(sketch, "E3451", {"start": v(-4.76, 4.93) * mm, "mid": v(-4.85, 4.85) * mm, "end": v(-4.93, 4.76) * mm});
            skArc(sketch, "E3452", {"start": v(-3.83, 5.68) * mm, "mid": v(-3.93, 5.61) * mm, "end": v(-4.03, 5.54) * mm});
            skArc(sketch, "E3453", {"start": v(-2.78, 6.26) * mm, "mid": v(-2.9, 6.21) * mm, "end": v(-3, 6.16) * mm});
            skArc(sketch, "E3454", {"start": v(-1.65, 6.65) * mm, "mid": v(-1.77, 6.62) * mm, "end": v(-1.9, 6.58) * mm});
            skArc(sketch, "E3455", {"start": v(-0.47, 6.84) * mm, "mid": v(-0.6, 6.83) * mm, "end": v(-0.72, 6.81) * mm});
            skSolve(sketch);
        }
        {
            var Q0;
            Q0 = qSketchRegion(id + "F0", true);
            extrude(context, id + "F1", {"entities" : qUnion([Q0]), "depth" : 3 * mm, "offsetDistance" : 25 * mm});
        }
        {
            var Q0;
            Q0=makeQuery(id+"F1.opExtrude","CAP_FACE",FACE,{"disambiguationData":[OSD([sQuery(id+"F0.wireOp",EDGE,"E0"),sQuery(id+"F0.wireOp",EDGE,"E1"),sQuery(id+"F0.wireOp",EDGE,"E2"),sQuery(id+"F0.wireOp",EDGE,"E3"),sQuery(id+"F0.wireOp",EDGE,"E4"),sQuery(id+"F0.wireOp",EDGE,"E5"),sQuery(id+"F0.wireOp",EDGE,"E6"),sQuery(id+"F0.wireOp",EDGE,"E7"),sQuery(id+"F0.wireOp",EDGE,"E8"),sQuery(id+"F0.wireOp",EDGE,"E9"),sQuery(id+"F0.wireOp",EDGE,"E10"),sQuery(id+"F0.wireOp",EDGE,"E11"),sQuery(id+"F0.wireOp",EDGE,"E12"),sQuery(id+"F0.wireOp",EDGE,"E13"),sQuery(id+"F0.wireOp",EDGE,"E14"),sQuery(id+"F0.wireOp",EDGE,"E15"),sQuery(id+"F0.wireOp",EDGE,"E16"),sQuery(id+"F0.wireOp",EDGE,"E17"),sQuery(id+"F0.wireOp",EDGE,"E18"),sQuery(id+"F0.wireOp",EDGE,"E19"),sQuery(id+"F0.wireOp",EDGE,"E20"),sQuery(id+"F0.wireOp",EDGE,"E21"),sQuery(id+"F0.wireOp",EDGE,"E22"),sQuery(id+"F0.wireOp",EDGE,"E23"),sQuery(id+"F0.wireOp",EDGE,"E24"),sQuery(id+"F0.wireOp",EDGE,"E25"),sQuery(id+"F0.wireOp",EDGE,"E26"),sQuery(id+"F0.wireOp",EDGE,"E27"),sQuery(id+"F0.wireOp",EDGE,"E28"),sQuery(id+"F0.wireOp",EDGE,"E29"),sQuery(id+"F0.wireOp",EDGE,"E30"),sQuery(id+"F0.wireOp",EDGE,"E31"),sQuery(id+"F0.wireOp",EDGE,"E32"),sQuery(id+"F0.wireOp",EDGE,"E33"),sQuery(id+"F0.wireOp",EDGE,"E34"),sQuery(id+"F0.wireOp",EDGE,"E35"),sQuery(id+"F0.wireOp",EDGE,"E36"),sQuery(id+"F0.wireOp",EDGE,"E37"),sQuery(id+"F0.wireOp",EDGE,"E38"),sQuery(id+"F0.wireOp",EDGE,"E39"),sQuery(id+"F0.wireOp",EDGE,"E40"),sQuery(id+"F0.wireOp",EDGE,"E41"),sQuery(id+"F0.wireOp",EDGE,"E42"),sQuery(id+"F0.wireOp",EDGE,"E43"),sQuery(id+"F0.wireOp",EDGE,"E44"),sQuery(id+"F0.wireOp",EDGE,"E45"),sQuery(id+"F0.wireOp",EDGE,"E46"),sQuery(id+"F0.wireOp",EDGE,"E47"),sQuery(id+"F0.wireOp",EDGE,"E48"),sQuery(id+"F0.wireOp",EDGE,"E49"),sQuery(id+"F0.wireOp",EDGE,"E50"),sQuery(id+"F0.wireOp",EDGE,"E51"),sQuery(id+"F0.wireOp",EDGE,"E52"),sQuery(id+"F0.wireOp",EDGE,"E53"),sQuery(id+"F0.wireOp",EDGE,"E54"),sQuery(id+"F0.wireOp",EDGE,"E55"),sQuery(id+"F0.wireOp",EDGE,"E56"),sQuery(id+"F0.wireOp",EDGE,"E57"),sQuery(id+"F0.wireOp",EDGE,"E58"),sQuery(id+"F0.wireOp",EDGE,"E59"),sQuery(id+"F0.wireOp",EDGE,"E60"),sQuery(id+"F0.wireOp",EDGE,"E61"),sQuery(id+"F0.wireOp",EDGE,"E62"),sQuery(id+"F0.wireOp",EDGE,"E63"),sQuery(id+"F0.wireOp",EDGE,"E64"),sQuery(id+"F0.wireOp",EDGE,"E65"),sQuery(id+"F0.wireOp",EDGE,"E66"),sQuery(id+"F0.wireOp",EDGE,"E67"),sQuery(id+"F0.wireOp",EDGE,"E68"),sQuery(id+"F0.wireOp",EDGE,"E69"),sQuery(id+"F0.wireOp",EDGE,"E70"),sQuery(id+"F0.wireOp",EDGE,"E71"),sQuery(id+"F0.wireOp",EDGE,"E72"),sQuery(id+"F0.wireOp",EDGE,"E73"),sQuery(id+"F0.wireOp",EDGE,"E74"),sQuery(id+"F0.wireOp",EDGE,"E75"),sQuery(id+"F0.wireOp",EDGE,"E76"),sQuery(id+"F0.wireOp",EDGE,"E77"),sQuery(id+"F0.wireOp",EDGE,"E78"),sQuery(id+"F0.wireOp",EDGE,"E79"),sQuery(id+"F0.wireOp",EDGE,"E80"),sQuery(id+"F0.wireOp",EDGE,"E81"),sQuery(id+"F0.wireOp",EDGE,"E82"),sQuery(id+"F0.wireOp",EDGE,"E83"),sQuery(id+"F0.wireOp",EDGE,"E84"),sQuery(id+"F0.wireOp",EDGE,"E85"),sQuery(id+"F0.wireOp",EDGE,"E86"),sQuery(id+"F0.wireOp",EDGE,"E87"),sQuery(id+"F0.wireOp",EDGE,"E88"),sQuery(id+"F0.wireOp",EDGE,"E89"),sQuery(id+"F0.wireOp",EDGE,"E90"),sQuery(id+"F0.wireOp",EDGE,"E91"),sQuery(id+"F0.wireOp",EDGE,"E92"),sQuery(id+"F0.wireOp",EDGE,"E93"),sQuery(id+"F0.wireOp",EDGE,"E94"),sQuery(id+"F0.wireOp",EDGE,"E95"),sQuery(id+"F0.wireOp",EDGE,"E96"),sQuery(id+"F0.wireOp",EDGE,"E97"),sQuery(id+"F0.wireOp",EDGE,"E98"),sQuery(id+"F0.wireOp",EDGE,"E99"),sQuery(id+"F0.wireOp",EDGE,"E100"),sQuery(id+"F0.wireOp",EDGE,"E101"),sQuery(id+"F0.wireOp",EDGE,"E102"),sQuery(id+"F0.wireOp",EDGE,"E103"),sQuery(id+"F0.wireOp",EDGE,"E104"),sQuery(id+"F0.wireOp",EDGE,"E105"),sQuery(id+"F0.wireOp",EDGE,"E106"),sQuery(id+"F0.wireOp",EDGE,"E107"),sQuery(id+"F0.wireOp",EDGE,"E108"),sQuery(id+"F0.wireOp",EDGE,"E109"),sQuery(id+"F0.wireOp",EDGE,"E110"),sQuery(id+"F0.wireOp",EDGE,"E111"),sQuery(id+"F0.wireOp",EDGE,"E112"),sQuery(id+"F0.wireOp",EDGE,"E113"),sQuery(id+"F0.wireOp",EDGE,"E114"),sQuery(id+"F0.wireOp",EDGE,"E115"),sQuery(id+"F0.wireOp",EDGE,"E116"),sQuery(id+"F0.wireOp",EDGE,"E117"),sQuery(id+"F0.wireOp",EDGE,"E118"),sQuery(id+"F0.wireOp",EDGE,"E119"),sQuery(id+"F0.wireOp",EDGE,"E120"),sQuery(id+"F0.wireOp",EDGE,"E121"),sQuery(id+"F0.wireOp",EDGE,"E122"),sQuery(id+"F0.wireOp",EDGE,"E123"),sQuery(id+"F0.wireOp",EDGE,"E124"),sQuery(id+"F0.wireOp",EDGE,"E125"),sQuery(id+"F0.wireOp",EDGE,"E126"),sQuery(id+"F0.wireOp",EDGE,"E127"),sQuery(id+"F0.wireOp",EDGE,"E128"),sQuery(id+"F0.wireOp",EDGE,"E129"),sQuery(id+"F0.wireOp",EDGE,"E130"),sQuery(id+"F0.wireOp",EDGE,"E131"),sQuery(id+"F0.wireOp",EDGE,"E132"),sQuery(id+"F0.wireOp",EDGE,"E133"),sQuery(id+"F0.wireOp",EDGE,"E134"),sQuery(id+"F0.wireOp",EDGE,"E135"),sQuery(id+"F0.wireOp",EDGE,"E136"),sQuery(id+"F0.wireOp",EDGE,"E137"),sQuery(id+"F0.wireOp",EDGE,"E138"),sQuery(id+"F0.wireOp",EDGE,"E139"),sQuery(id+"F0.wireOp",EDGE,"E140"),sQuery(id+"F0.wireOp",EDGE,"E141"),sQuery(id+"F0.wireOp",EDGE,"E142"),sQuery(id+"F0.wireOp",EDGE,"E143"),sQuery(id+"F0.wireOp",EDGE,"E144"),sQuery(id+"F0.wireOp",EDGE,"E145"),sQuery(id+"F0.wireOp",EDGE,"E146"),sQuery(id+"F0.wireOp",EDGE,"E147"),sQuery(id+"F0.wireOp",EDGE,"E148"),sQuery(id+"F0.wireOp",EDGE,"E149"),sQuery(id+"F0.wireOp",EDGE,"E150"),sQuery(id+"F0.wireOp",EDGE,"E151"),sQuery(id+"F0.wireOp",EDGE,"E152"),sQuery(id+"F0.wireOp",EDGE,"E153"),sQuery(id+"F0.wireOp",EDGE,"E154"),sQuery(id+"F0.wireOp",EDGE,"E155"),sQuery(id+"F0.wireOp",EDGE,"E156"),sQuery(id+"F0.wireOp",EDGE,"E157"),sQuery(id+"F0.wireOp",EDGE,"E158"),sQuery(id+"F0.wireOp",EDGE,"E159"),sQuery(id+"F0.wireOp",EDGE,"E160"),sQuery(id+"F0.wireOp",EDGE,"E161"),sQuery(id+"F0.wireOp",EDGE,"E162"),sQuery(id+"F0.wireOp",EDGE,"E163"),sQuery(id+"F0.wireOp",EDGE,"E164"),sQuery(id+"F0.wireOp",EDGE,"E165"),sQuery(id+"F0.wireOp",EDGE,"E166"),sQuery(id+"F0.wireOp",EDGE,"E167"),sQuery(id+"F0.wireOp",EDGE,"E168"),sQuery(id+"F0.wireOp",EDGE,"E169"),sQuery(id+"F0.wireOp",EDGE,"E170"),sQuery(id+"F0.wireOp",EDGE,"E171"),sQuery(id+"F0.wireOp",EDGE,"E172"),sQuery(id+"F0.wireOp",EDGE,"E173"),sQuery(id+"F0.wireOp",EDGE,"E174"),sQuery(id+"F0.wireOp",EDGE,"E175"),sQuery(id+"F0.wireOp",EDGE,"E176"),sQuery(id+"F0.wireOp",EDGE,"E177"),sQuery(id+"F0.wireOp",EDGE,"E178"),sQuery(id+"F0.wireOp",EDGE,"E179"),sQuery(id+"F0.wireOp",EDGE,"E180"),sQuery(id+"F0.wireOp",EDGE,"E181"),sQuery(id+"F0.wireOp",EDGE,"E182"),sQuery(id+"F0.wireOp",EDGE,"E183"),sQuery(id+"F0.wireOp",EDGE,"E184"),sQuery(id+"F0.wireOp",EDGE,"E185"),sQuery(id+"F0.wireOp",EDGE,"E186"),sQuery(id+"F0.wireOp",EDGE,"E187"),sQuery(id+"F0.wireOp",EDGE,"E188"),sQuery(id+"F0.wireOp",EDGE,"E189"),sQuery(id+"F0.wireOp",EDGE,"E190"),sQuery(id+"F0.wireOp",EDGE,"E191"),sQuery(id+"F0.wireOp",EDGE,"E192"),sQuery(id+"F0.wireOp",EDGE,"E193"),sQuery(id+"F0.wireOp",EDGE,"E194"),sQuery(id+"F0.wireOp",EDGE,"E195"),sQuery(id+"F0.wireOp",EDGE,"E196"),sQuery(id+"F0.wireOp",EDGE,"E197"),sQuery(id+"F0.wireOp",EDGE,"E198"),sQuery(id+"F0.wireOp",EDGE,"E199"),sQuery(id+"F0.wireOp",EDGE,"E200"),sQuery(id+"F0.wireOp",EDGE,"E201"),sQuery(id+"F0.wireOp",EDGE,"E202"),sQuery(id+"F0.wireOp",EDGE,"E203"),sQuery(id+"F0.wireOp",EDGE,"E204"),sQuery(id+"F0.wireOp",EDGE,"E205"),sQuery(id+"F0.wireOp",EDGE,"E206"),sQuery(id+"F0.wireOp",EDGE,"E207"),sQuery(id+"F0.wireOp",EDGE,"E208"),sQuery(id+"F0.wireOp",EDGE,"E209"),sQuery(id+"F0.wireOp",EDGE,"E210"),sQuery(id+"F0.wireOp",EDGE,"E211"),sQuery(id+"F0.wireOp",EDGE,"E212"),sQuery(id+"F0.wireOp",EDGE,"E213"),sQuery(id+"F0.wireOp",EDGE,"E214"),sQuery(id+"F0.wireOp",EDGE,"E215"),sQuery(id+"F0.wireOp",EDGE,"E216"),sQuery(id+"F0.wireOp",EDGE,"E217"),sQuery(id+"F0.wireOp",EDGE,"E218"),sQuery(id+"F0.wireOp",EDGE,"E219"),sQuery(id+"F0.wireOp",EDGE,"E220"),sQuery(id+"F0.wireOp",EDGE,"E221"),sQuery(id+"F0.wireOp",EDGE,"E222"),sQuery(id+"F0.wireOp",EDGE,"E223"),sQuery(id+"F0.wireOp",EDGE,"E224"),sQuery(id+"F0.wireOp",EDGE,"E225"),sQuery(id+"F0.wireOp",EDGE,"E226"),sQuery(id+"F0.wireOp",EDGE,"E227"),sQuery(id+"F0.wireOp",EDGE,"E228"),sQuery(id+"F0.wireOp",EDGE,"E229"),sQuery(id+"F0.wireOp",EDGE,"E230"),sQuery(id+"F0.wireOp",EDGE,"E231"),sQuery(id+"F0.wireOp",EDGE,"E232"),sQuery(id+"F0.wireOp",EDGE,"E233"),sQuery(id+"F0.wireOp",EDGE,"E234"),sQuery(id+"F0.wireOp",EDGE,"E235"),sQuery(id+"F0.wireOp",EDGE,"E236"),sQuery(id+"F0.wireOp",EDGE,"E237"),sQuery(id+"F0.wireOp",EDGE,"E238"),sQuery(id+"F0.wireOp",EDGE,"E239"),sQuery(id+"F0.wireOp",EDGE,"E240"),sQuery(id+"F0.wireOp",EDGE,"E241"),sQuery(id+"F0.wireOp",EDGE,"E242"),sQuery(id+"F0.wireOp",EDGE,"E243"),sQuery(id+"F0.wireOp",EDGE,"E244"),sQuery(id+"F0.wireOp",EDGE,"E245"),sQuery(id+"F0.wireOp",EDGE,"E246"),sQuery(id+"F0.wireOp",EDGE,"E247"),sQuery(id+"F0.wireOp",EDGE,"E248"),sQuery(id+"F0.wireOp",EDGE,"E249"),sQuery(id+"F0.wireOp",EDGE,"E250"),sQuery(id+"F0.wireOp",EDGE,"E251"),sQuery(id+"F0.wireOp",EDGE,"E252"),sQuery(id+"F0.wireOp",EDGE,"E253"),sQuery(id+"F0.wireOp",EDGE,"E254"),sQuery(id+"F0.wireOp",EDGE,"E255"),sQuery(id+"F0.wireOp",EDGE,"E256"),sQuery(id+"F0.wireOp",EDGE,"E257"),sQuery(id+"F0.wireOp",EDGE,"E258"),sQuery(id+"F0.wireOp",EDGE,"E259"),sQuery(id+"F0.wireOp",EDGE,"E260"),sQuery(id+"F0.wireOp",EDGE,"E261"),sQuery(id+"F0.wireOp",EDGE,"E262"),sQuery(id+"F0.wireOp",EDGE,"E263"),sQuery(id+"F0.wireOp",EDGE,"E264"),sQuery(id+"F0.wireOp",EDGE,"E265"),sQuery(id+"F0.wireOp",EDGE,"E266"),sQuery(id+"F0.wireOp",EDGE,"E267"),sQuery(id+"F0.wireOp",EDGE,"E268"),sQuery(id+"F0.wireOp",EDGE,"E269"),sQuery(id+"F0.wireOp",EDGE,"E270"),sQuery(id+"F0.wireOp",EDGE,"E271"),sQuery(id+"F0.wireOp",EDGE,"E272"),sQuery(id+"F0.wireOp",EDGE,"E273"),sQuery(id+"F0.wireOp",EDGE,"E274"),sQuery(id+"F0.wireOp",EDGE,"E275"),sQuery(id+"F0.wireOp",EDGE,"E276"),sQuery(id+"F0.wireOp",EDGE,"E277"),sQuery(id+"F0.wireOp",EDGE,"E278"),sQuery(id+"F0.wireOp",EDGE,"E279"),sQuery(id+"F0.wireOp",EDGE,"E280"),sQuery(id+"F0.wireOp",EDGE,"E281"),sQuery(id+"F0.wireOp",EDGE,"E282"),sQuery(id+"F0.wireOp",EDGE,"E283"),sQuery(id+"F0.wireOp",EDGE,"E284"),sQuery(id+"F0.wireOp",EDGE,"E285"),sQuery(id+"F0.wireOp",EDGE,"E286"),sQuery(id+"F0.wireOp",EDGE,"E287"),sQuery(id+"F0.wireOp",EDGE,"E288"),sQuery(id+"F0.wireOp",EDGE,"E289"),sQuery(id+"F0.wireOp",EDGE,"E290"),sQuery(id+"F0.wireOp",EDGE,"E291"),sQuery(id+"F0.wireOp",EDGE,"E292"),sQuery(id+"F0.wireOp",EDGE,"E293"),sQuery(id+"F0.wireOp",EDGE,"E294"),sQuery(id+"F0.wireOp",EDGE,"E295"),sQuery(id+"F0.wireOp",EDGE,"E296"),sQuery(id+"F0.wireOp",EDGE,"E297"),sQuery(id+"F0.wireOp",EDGE,"E298"),sQuery(id+"F0.wireOp",EDGE,"E299"),sQuery(id+"F0.wireOp",EDGE,"E300"),sQuery(id+"F0.wireOp",EDGE,"E301"),sQuery(id+"F0.wireOp",EDGE,"E302"),sQuery(id+"F0.wireOp",EDGE,"E303"),sQuery(id+"F0.wireOp",EDGE,"E304"),sQuery(id+"F0.wireOp",EDGE,"E305"),sQuery(id+"F0.wireOp",EDGE,"E306"),sQuery(id+"F0.wireOp",EDGE,"E307"),sQuery(id+"F0.wireOp",EDGE,"E308"),sQuery(id+"F0.wireOp",EDGE,"E309"),sQuery(id+"F0.wireOp",EDGE,"E310"),sQuery(id+"F0.wireOp",EDGE,"E311"),sQuery(id+"F0.wireOp",EDGE,"E312"),sQuery(id+"F0.wireOp",EDGE,"E313"),sQuery(id+"F0.wireOp",EDGE,"E314"),sQuery(id+"F0.wireOp",EDGE,"E315"),sQuery(id+"F0.wireOp",EDGE,"E316"),sQuery(id+"F0.wireOp",EDGE,"E317"),sQuery(id+"F0.wireOp",EDGE,"E318"),sQuery(id+"F0.wireOp",EDGE,"E319"),sQuery(id+"F0.wireOp",EDGE,"E320"),sQuery(id+"F0.wireOp",EDGE,"E321"),sQuery(id+"F0.wireOp",EDGE,"E322"),sQuery(id+"F0.wireOp",EDGE,"E323"),sQuery(id+"F0.wireOp",EDGE,"E324"),sQuery(id+"F0.wireOp",EDGE,"E325"),sQuery(id+"F0.wireOp",EDGE,"E326"),sQuery(id+"F0.wireOp",EDGE,"E327"),sQuery(id+"F0.wireOp",EDGE,"E328"),sQuery(id+"F0.wireOp",EDGE,"E329"),sQuery(id+"F0.wireOp",EDGE,"E330"),sQuery(id+"F0.wireOp",EDGE,"E331"),sQuery(id+"F0.wireOp",EDGE,"E332"),sQuery(id+"F0.wireOp",EDGE,"E333"),sQuery(id+"F0.wireOp",EDGE,"E334"),sQuery(id+"F0.wireOp",EDGE,"E335"),sQuery(id+"F0.wireOp",EDGE,"E336"),sQuery(id+"F0.wireOp",EDGE,"E337"),sQuery(id+"F0.wireOp",EDGE,"E338"),sQuery(id+"F0.wireOp",EDGE,"E339"),sQuery(id+"F0.wireOp",EDGE,"E340"),sQuery(id+"F0.wireOp",EDGE,"E341"),sQuery(id+"F0.wireOp",EDGE,"E342"),sQuery(id+"F0.wireOp",EDGE,"E343"),sQuery(id+"F0.wireOp",EDGE,"E344"),sQuery(id+"F0.wireOp",EDGE,"E345"),sQuery(id+"F0.wireOp",EDGE,"E346"),sQuery(id+"F0.wireOp",EDGE,"E347"),sQuery(id+"F0.wireOp",EDGE,"E348"),sQuery(id+"F0.wireOp",EDGE,"E349"),sQuery(id+"F0.wireOp",EDGE,"E350"),sQuery(id+"F0.wireOp",EDGE,"E351"),sQuery(id+"F0.wireOp",EDGE,"E352"),sQuery(id+"F0.wireOp",EDGE,"E353"),sQuery(id+"F0.wireOp",EDGE,"E354"),sQuery(id+"F0.wireOp",EDGE,"E355"),sQuery(id+"F0.wireOp",EDGE,"E356"),sQuery(id+"F0.wireOp",EDGE,"E357"),sQuery(id+"F0.wireOp",EDGE,"E358"),sQuery(id+"F0.wireOp",EDGE,"E359"),sQuery(id+"F0.wireOp",EDGE,"E360"),sQuery(id+"F0.wireOp",EDGE,"E361"),sQuery(id+"F0.wireOp",EDGE,"E362"),sQuery(id+"F0.wireOp",EDGE,"E363"),sQuery(id+"F0.wireOp",EDGE,"E364"),sQuery(id+"F0.wireOp",EDGE,"E365"),sQuery(id+"F0.wireOp",EDGE,"E366"),sQuery(id+"F0.wireOp",EDGE,"E367"),sQuery(id+"F0.wireOp",EDGE,"E368"),sQuery(id+"F0.wireOp",EDGE,"E369"),sQuery(id+"F0.wireOp",EDGE,"E370"),sQuery(id+"F0.wireOp",EDGE,"E371"),sQuery(id+"F0.wireOp",EDGE,"E372"),sQuery(id+"F0.wireOp",EDGE,"E373"),sQuery(id+"F0.wireOp",EDGE,"E374"),sQuery(id+"F0.wireOp",EDGE,"E375"),sQuery(id+"F0.wireOp",EDGE,"E376"),sQuery(id+"F0.wireOp",EDGE,"E377"),sQuery(id+"F0.wireOp",EDGE,"E378"),sQuery(id+"F0.wireOp",EDGE,"E379"),sQuery(id+"F0.wireOp",EDGE,"E380"),sQuery(id+"F0.wireOp",EDGE,"E381"),sQuery(id+"F0.wireOp",EDGE,"E382"),sQuery(id+"F0.wireOp",EDGE,"E383"),sQuery(id+"F0.wireOp",EDGE,"E384"),sQuery(id+"F0.wireOp",EDGE,"E385"),sQuery(id+"F0.wireOp",EDGE,"E386"),sQuery(id+"F0.wireOp",EDGE,"E387"),sQuery(id+"F0.wireOp",EDGE,"E388"),sQuery(id+"F0.wireOp",EDGE,"E389"),sQuery(id+"F0.wireOp",EDGE,"E390"),sQuery(id+"F0.wireOp",EDGE,"E391"),sQuery(id+"F0.wireOp",EDGE,"E392"),sQuery(id+"F0.wireOp",EDGE,"E393"),sQuery(id+"F0.wireOp",EDGE,"E394"),sQuery(id+"F0.wireOp",EDGE,"E395"),sQuery(id+"F0.wireOp",EDGE,"E396"),sQuery(id+"F0.wireOp",EDGE,"E397"),sQuery(id+"F0.wireOp",EDGE,"E398"),sQuery(id+"F0.wireOp",EDGE,"E399"),sQuery(id+"F0.wireOp",EDGE,"E400"),sQuery(id+"F0.wireOp",EDGE,"E401"),sQuery(id+"F0.wireOp",EDGE,"E402"),sQuery(id+"F0.wireOp",EDGE,"E403"),sQuery(id+"F0.wireOp",EDGE,"E404"),sQuery(id+"F0.wireOp",EDGE,"E405"),sQuery(id+"F0.wireOp",EDGE,"E406"),sQuery(id+"F0.wireOp",EDGE,"E407"),sQuery(id+"F0.wireOp",EDGE,"E408"),sQuery(id+"F0.wireOp",EDGE,"E409"),sQuery(id+"F0.wireOp",EDGE,"E410"),sQuery(id+"F0.wireOp",EDGE,"E411"),sQuery(id+"F0.wireOp",EDGE,"E412"),sQuery(id+"F0.wireOp",EDGE,"E413"),sQuery(id+"F0.wireOp",EDGE,"E414"),sQuery(id+"F0.wireOp",EDGE,"E415"),sQuery(id+"F0.wireOp",EDGE,"E416"),sQuery(id+"F0.wireOp",EDGE,"E417"),sQuery(id+"F0.wireOp",EDGE,"E418"),sQuery(id+"F0.wireOp",EDGE,"E419"),sQuery(id+"F0.wireOp",EDGE,"E420"),sQuery(id+"F0.wireOp",EDGE,"E421"),sQuery(id+"F0.wireOp",EDGE,"E422"),sQuery(id+"F0.wireOp",EDGE,"E423"),sQuery(id+"F0.wireOp",EDGE,"E424"),sQuery(id+"F0.wireOp",EDGE,"E425"),sQuery(id+"F0.wireOp",EDGE,"E426"),sQuery(id+"F0.wireOp",EDGE,"E427"),sQuery(id+"F0.wireOp",EDGE,"E428"),sQuery(id+"F0.wireOp",EDGE,"E429"),sQuery(id+"F0.wireOp",EDGE,"E430"),sQuery(id+"F0.wireOp",EDGE,"E431"),sQuery(id+"F0.wireOp",EDGE,"E432"),sQuery(id+"F0.wireOp",EDGE,"E433"),sQuery(id+"F0.wireOp",EDGE,"E434"),sQuery(id+"F0.wireOp",EDGE,"E435"),sQuery(id+"F0.wireOp",EDGE,"E436"),sQuery(id+"F0.wireOp",EDGE,"E437"),sQuery(id+"F0.wireOp",EDGE,"E438"),sQuery(id+"F0.wireOp",EDGE,"E439"),sQuery(id+"F0.wireOp",EDGE,"E440"),sQuery(id+"F0.wireOp",EDGE,"E441"),sQuery(id+"F0.wireOp",EDGE,"E442"),sQuery(id+"F0.wireOp",EDGE,"E443"),sQuery(id+"F0.wireOp",EDGE,"E444"),sQuery(id+"F0.wireOp",EDGE,"E445"),sQuery(id+"F0.wireOp",EDGE,"E446"),sQuery(id+"F0.wireOp",EDGE,"E447"),sQuery(id+"F0.wireOp",EDGE,"E448"),sQuery(id+"F0.wireOp",EDGE,"E449"),sQuery(id+"F0.wireOp",EDGE,"E450"),sQuery(id+"F0.wireOp",EDGE,"E451"),sQuery(id+"F0.wireOp",EDGE,"E452"),sQuery(id+"F0.wireOp",EDGE,"E453"),sQuery(id+"F0.wireOp",EDGE,"E454"),sQuery(id+"F0.wireOp",EDGE,"E455"),sQuery(id+"F0.wireOp",EDGE,"E456"),sQuery(id+"F0.wireOp",EDGE,"E457"),sQuery(id+"F0.wireOp",EDGE,"E458"),sQuery(id+"F0.wireOp",EDGE,"E459"),sQuery(id+"F0.wireOp",EDGE,"E460"),sQuery(id+"F0.wireOp",EDGE,"E461"),sQuery(id+"F0.wireOp",EDGE,"E462"),sQuery(id+"F0.wireOp",EDGE,"E463"),sQuery(id+"F0.wireOp",EDGE,"E464"),sQuery(id+"F0.wireOp",EDGE,"E465"),sQuery(id+"F0.wireOp",EDGE,"E466"),sQuery(id+"F0.wireOp",EDGE,"E467"),sQuery(id+"F0.wireOp",EDGE,"E468"),sQuery(id+"F0.wireOp",EDGE,"E469"),sQuery(id+"F0.wireOp",EDGE,"E470"),sQuery(id+"F0.wireOp",EDGE,"E471"),sQuery(id+"F0.wireOp",EDGE,"E472"),sQuery(id+"F0.wireOp",EDGE,"E473"),sQuery(id+"F0.wireOp",EDGE,"E474"),sQuery(id+"F0.wireOp",EDGE,"E475"),sQuery(id+"F0.wireOp",EDGE,"E476"),sQuery(id+"F0.wireOp",EDGE,"E477"),sQuery(id+"F0.wireOp",EDGE,"E478"),sQuery(id+"F0.wireOp",EDGE,"E479"),sQuery(id+"F0.wireOp",EDGE,"E480"),sQuery(id+"F0.wireOp",EDGE,"E481"),sQuery(id+"F0.wireOp",EDGE,"E482"),sQuery(id+"F0.wireOp",EDGE,"E483"),sQuery(id+"F0.wireOp",EDGE,"E484"),sQuery(id+"F0.wireOp",EDGE,"E485"),sQuery(id+"F0.wireOp",EDGE,"E486"),sQuery(id+"F0.wireOp",EDGE,"E487"),sQuery(id+"F0.wireOp",EDGE,"E488"),sQuery(id+"F0.wireOp",EDGE,"E489"),sQuery(id+"F0.wireOp",EDGE,"E490"),sQuery(id+"F0.wireOp",EDGE,"E491"),sQuery(id+"F0.wireOp",EDGE,"E492"),sQuery(id+"F0.wireOp",EDGE,"E493"),sQuery(id+"F0.wireOp",EDGE,"E494"),sQuery(id+"F0.wireOp",EDGE,"E495"),sQuery(id+"F0.wireOp",EDGE,"E496"),sQuery(id+"F0.wireOp",EDGE,"E497"),sQuery(id+"F0.wireOp",EDGE,"E498"),sQuery(id+"F0.wireOp",EDGE,"E499"),sQuery(id+"F0.wireOp",EDGE,"E500"),sQuery(id+"F0.wireOp",EDGE,"E501"),sQuery(id+"F0.wireOp",EDGE,"E502"),sQuery(id+"F0.wireOp",EDGE,"E503"),sQuery(id+"F0.wireOp",EDGE,"E504"),sQuery(id+"F0.wireOp",EDGE,"E505"),sQuery(id+"F0.wireOp",EDGE,"E506"),sQuery(id+"F0.wireOp",EDGE,"E507"),sQuery(id+"F0.wireOp",EDGE,"E508"),sQuery(id+"F0.wireOp",EDGE,"E509"),sQuery(id+"F0.wireOp",EDGE,"E510"),sQuery(id+"F0.wireOp",EDGE,"E511"),sQuery(id+"F0.wireOp",EDGE,"E512"),sQuery(id+"F0.wireOp",EDGE,"E513"),sQuery(id+"F0.wireOp",EDGE,"E514"),sQuery(id+"F0.wireOp",EDGE,"E515"),sQuery(id+"F0.wireOp",EDGE,"E516"),sQuery(id+"F0.wireOp",EDGE,"E517"),sQuery(id+"F0.wireOp",EDGE,"E518"),sQuery(id+"F0.wireOp",EDGE,"E519"),sQuery(id+"F0.wireOp",EDGE,"E520"),sQuery(id+"F0.wireOp",EDGE,"E521"),sQuery(id+"F0.wireOp",EDGE,"E522"),sQuery(id+"F0.wireOp",EDGE,"E523"),sQuery(id+"F0.wireOp",EDGE,"E524"),sQuery(id+"F0.wireOp",EDGE,"E525"),sQuery(id+"F0.wireOp",EDGE,"E526"),sQuery(id+"F0.wireOp",EDGE,"E527"),sQuery(id+"F0.wireOp",EDGE,"E528"),sQuery(id+"F0.wireOp",EDGE,"E529"),sQuery(id+"F0.wireOp",EDGE,"E530"),sQuery(id+"F0.wireOp",EDGE,"E531"),sQuery(id+"F0.wireOp",EDGE,"E532"),sQuery(id+"F0.wireOp",EDGE,"E533"),sQuery(id+"F0.wireOp",EDGE,"E534"),sQuery(id+"F0.wireOp",EDGE,"E535"),sQuery(id+"F0.wireOp",EDGE,"E536"),sQuery(id+"F0.wireOp",EDGE,"E537"),sQuery(id+"F0.wireOp",EDGE,"E538"),sQuery(id+"F0.wireOp",EDGE,"E539"),sQuery(id+"F0.wireOp",EDGE,"E540"),sQuery(id+"F0.wireOp",EDGE,"E541"),sQuery(id+"F0.wireOp",EDGE,"E542"),sQuery(id+"F0.wireOp",EDGE,"E543"),sQuery(id+"F0.wireOp",EDGE,"E544"),sQuery(id+"F0.wireOp",EDGE,"E545"),sQuery(id+"F0.wireOp",EDGE,"E546"),sQuery(id+"F0.wireOp",EDGE,"E547"),sQuery(id+"F0.wireOp",EDGE,"E548"),sQuery(id+"F0.wireOp",EDGE,"E549"),sQuery(id+"F0.wireOp",EDGE,"E550"),sQuery(id+"F0.wireOp",EDGE,"E551"),sQuery(id+"F0.wireOp",EDGE,"E552"),sQuery(id+"F0.wireOp",EDGE,"E553"),sQuery(id+"F0.wireOp",EDGE,"E554"),sQuery(id+"F0.wireOp",EDGE,"E555"),sQuery(id+"F0.wireOp",EDGE,"E556"),sQuery(id+"F0.wireOp",EDGE,"E557"),sQuery(id+"F0.wireOp",EDGE,"E558"),sQuery(id+"F0.wireOp",EDGE,"E559"),sQuery(id+"F0.wireOp",EDGE,"E560"),sQuery(id+"F0.wireOp",EDGE,"E561"),sQuery(id+"F0.wireOp",EDGE,"E562"),sQuery(id+"F0.wireOp",EDGE,"E563"),sQuery(id+"F0.wireOp",EDGE,"E564"),sQuery(id+"F0.wireOp",EDGE,"E565"),sQuery(id+"F0.wireOp",EDGE,"E566"),sQuery(id+"F0.wireOp",EDGE,"E567"),sQuery(id+"F0.wireOp",EDGE,"E568"),sQuery(id+"F0.wireOp",EDGE,"E569"),sQuery(id+"F0.wireOp",EDGE,"E570"),sQuery(id+"F0.wireOp",EDGE,"E571"),sQuery(id+"F0.wireOp",EDGE,"E572"),sQuery(id+"F0.wireOp",EDGE,"E573"),sQuery(id+"F0.wireOp",EDGE,"E574"),sQuery(id+"F0.wireOp",EDGE,"E575"),sQuery(id+"F0.wireOp",EDGE,"E576"),sQuery(id+"F0.wireOp",EDGE,"E577"),sQuery(id+"F0.wireOp",EDGE,"E578"),sQuery(id+"F0.wireOp",EDGE,"E579"),sQuery(id+"F0.wireOp",EDGE,"E580"),sQuery(id+"F0.wireOp",EDGE,"E581"),sQuery(id+"F0.wireOp",EDGE,"E582"),sQuery(id+"F0.wireOp",EDGE,"E583"),sQuery(id+"F0.wireOp",EDGE,"E584"),sQuery(id+"F0.wireOp",EDGE,"E585"),sQuery(id+"F0.wireOp",EDGE,"E586"),sQuery(id+"F0.wireOp",EDGE,"E587"),sQuery(id+"F0.wireOp",EDGE,"E588"),sQuery(id+"F0.wireOp",EDGE,"E589"),sQuery(id+"F0.wireOp",EDGE,"E590"),sQuery(id+"F0.wireOp",EDGE,"E591"),sQuery(id+"F0.wireOp",EDGE,"E592"),sQuery(id+"F0.wireOp",EDGE,"E593"),sQuery(id+"F0.wireOp",EDGE,"E594"),sQuery(id+"F0.wireOp",EDGE,"E595"),sQuery(id+"F0.wireOp",EDGE,"E596"),sQuery(id+"F0.wireOp",EDGE,"E597"),sQuery(id+"F0.wireOp",EDGE,"E598"),sQuery(id+"F0.wireOp",EDGE,"E599"),sQuery(id+"F0.wireOp",EDGE,"E600"),sQuery(id+"F0.wireOp",EDGE,"E601"),sQuery(id+"F0.wireOp",EDGE,"E602"),sQuery(id+"F0.wireOp",EDGE,"E603"),sQuery(id+"F0.wireOp",EDGE,"E604"),sQuery(id+"F0.wireOp",EDGE,"E605"),sQuery(id+"F0.wireOp",EDGE,"E606"),sQuery(id+"F0.wireOp",EDGE,"E607"),sQuery(id+"F0.wireOp",EDGE,"E608"),sQuery(id+"F0.wireOp",EDGE,"E609"),sQuery(id+"F0.wireOp",EDGE,"E610"),sQuery(id+"F0.wireOp",EDGE,"E611"),sQuery(id+"F0.wireOp",EDGE,"E612"),sQuery(id+"F0.wireOp",EDGE,"E613"),sQuery(id+"F0.wireOp",EDGE,"E614"),sQuery(id+"F0.wireOp",EDGE,"E615"),sQuery(id+"F0.wireOp",EDGE,"E616"),sQuery(id+"F0.wireOp",EDGE,"E617"),sQuery(id+"F0.wireOp",EDGE,"E618"),sQuery(id+"F0.wireOp",EDGE,"E619"),sQuery(id+"F0.wireOp",EDGE,"E620"),sQuery(id+"F0.wireOp",EDGE,"E621"),sQuery(id+"F0.wireOp",EDGE,"E622"),sQuery(id+"F0.wireOp",EDGE,"E623"),sQuery(id+"F0.wireOp",EDGE,"E624"),sQuery(id+"F0.wireOp",EDGE,"E625"),sQuery(id+"F0.wireOp",EDGE,"E626"),sQuery(id+"F0.wireOp",EDGE,"E627"),sQuery(id+"F0.wireOp",EDGE,"E628"),sQuery(id+"F0.wireOp",EDGE,"E629"),sQuery(id+"F0.wireOp",EDGE,"E630"),sQuery(id+"F0.wireOp",EDGE,"E631"),sQuery(id+"F0.wireOp",EDGE,"E632"),sQuery(id+"F0.wireOp",EDGE,"E633"),sQuery(id+"F0.wireOp",EDGE,"E634"),sQuery(id+"F0.wireOp",EDGE,"E635"),sQuery(id+"F0.wireOp",EDGE,"E636"),sQuery(id+"F0.wireOp",EDGE,"E637"),sQuery(id+"F0.wireOp",EDGE,"E638"),sQuery(id+"F0.wireOp",EDGE,"E639"),sQuery(id+"F0.wireOp",EDGE,"E640"),sQuery(id+"F0.wireOp",EDGE,"E641"),sQuery(id+"F0.wireOp",EDGE,"E642"),sQuery(id+"F0.wireOp",EDGE,"E643"),sQuery(id+"F0.wireOp",EDGE,"E644"),sQuery(id+"F0.wireOp",EDGE,"E645"),sQuery(id+"F0.wireOp",EDGE,"E646"),sQuery(id+"F0.wireOp",EDGE,"E647"),sQuery(id+"F0.wireOp",EDGE,"E648"),sQuery(id+"F0.wireOp",EDGE,"E649"),sQuery(id+"F0.wireOp",EDGE,"E650"),sQuery(id+"F0.wireOp",EDGE,"E651"),sQuery(id+"F0.wireOp",EDGE,"E652"),sQuery(id+"F0.wireOp",EDGE,"E653"),sQuery(id+"F0.wireOp",EDGE,"E654"),sQuery(id+"F0.wireOp",EDGE,"E655"),sQuery(id+"F0.wireOp",EDGE,"E656"),sQuery(id+"F0.wireOp",EDGE,"E657"),sQuery(id+"F0.wireOp",EDGE,"E658"),sQuery(id+"F0.wireOp",EDGE,"E659"),sQuery(id+"F0.wireOp",EDGE,"E660"),sQuery(id+"F0.wireOp",EDGE,"E661"),sQuery(id+"F0.wireOp",EDGE,"E662"),sQuery(id+"F0.wireOp",EDGE,"E663"),sQuery(id+"F0.wireOp",EDGE,"E664"),sQuery(id+"F0.wireOp",EDGE,"E665"),sQuery(id+"F0.wireOp",EDGE,"E666"),sQuery(id+"F0.wireOp",EDGE,"E667"),sQuery(id+"F0.wireOp",EDGE,"E668"),sQuery(id+"F0.wireOp",EDGE,"E669"),sQuery(id+"F0.wireOp",EDGE,"E670"),sQuery(id+"F0.wireOp",EDGE,"E671"),sQuery(id+"F0.wireOp",EDGE,"E672"),sQuery(id+"F0.wireOp",EDGE,"E673"),sQuery(id+"F0.wireOp",EDGE,"E674"),sQuery(id+"F0.wireOp",EDGE,"E675"),sQuery(id+"F0.wireOp",EDGE,"E676"),sQuery(id+"F0.wireOp",EDGE,"E677"),sQuery(id+"F0.wireOp",EDGE,"E678"),sQuery(id+"F0.wireOp",EDGE,"E679"),sQuery(id+"F0.wireOp",EDGE,"E680"),sQuery(id+"F0.wireOp",EDGE,"E681"),sQuery(id+"F0.wireOp",EDGE,"E682"),sQuery(id+"F0.wireOp",EDGE,"E683"),sQuery(id+"F0.wireOp",EDGE,"E684"),sQuery(id+"F0.wireOp",EDGE,"E685"),sQuery(id+"F0.wireOp",EDGE,"E686"),sQuery(id+"F0.wireOp",EDGE,"E687"),sQuery(id+"F0.wireOp",EDGE,"E688"),sQuery(id+"F0.wireOp",EDGE,"E689"),sQuery(id+"F0.wireOp",EDGE,"E690"),sQuery(id+"F0.wireOp",EDGE,"E691"),sQuery(id+"F0.wireOp",EDGE,"E692"),sQuery(id+"F0.wireOp",EDGE,"E693"),sQuery(id+"F0.wireOp",EDGE,"E694"),sQuery(id+"F0.wireOp",EDGE,"E695"),sQuery(id+"F0.wireOp",EDGE,"E696"),sQuery(id+"F0.wireOp",EDGE,"E697"),sQuery(id+"F0.wireOp",EDGE,"E698"),sQuery(id+"F0.wireOp",EDGE,"E699"),sQuery(id+"F0.wireOp",EDGE,"E700"),sQuery(id+"F0.wireOp",EDGE,"E701"),sQuery(id+"F0.wireOp",EDGE,"E702"),sQuery(id+"F0.wireOp",EDGE,"E703"),sQuery(id+"F0.wireOp",EDGE,"E704"),sQuery(id+"F0.wireOp",EDGE,"E705"),sQuery(id+"F0.wireOp",EDGE,"E706"),sQuery(id+"F0.wireOp",EDGE,"E707"),sQuery(id+"F0.wireOp",EDGE,"E708"),sQuery(id+"F0.wireOp",EDGE,"E709"),sQuery(id+"F0.wireOp",EDGE,"E710"),sQuery(id+"F0.wireOp",EDGE,"E711"),sQuery(id+"F0.wireOp",EDGE,"E712"),sQuery(id+"F0.wireOp",EDGE,"E713"),sQuery(id+"F0.wireOp",EDGE,"E714"),sQuery(id+"F0.wireOp",EDGE,"E715"),sQuery(id+"F0.wireOp",EDGE,"E716"),sQuery(id+"F0.wireOp",EDGE,"E717"),sQuery(id+"F0.wireOp",EDGE,"E718"),sQuery(id+"F0.wireOp",EDGE,"E719"),sQuery(id+"F0.wireOp",EDGE,"E720"),sQuery(id+"F0.wireOp",EDGE,"E721"),sQuery(id+"F0.wireOp",EDGE,"E722"),sQuery(id+"F0.wireOp",EDGE,"E723"),sQuery(id+"F0.wireOp",EDGE,"E724"),sQuery(id+"F0.wireOp",EDGE,"E725"),sQuery(id+"F0.wireOp",EDGE,"E726"),sQuery(id+"F0.wireOp",EDGE,"E727"),sQuery(id+"F0.wireOp",EDGE,"E728"),sQuery(id+"F0.wireOp",EDGE,"E729"),sQuery(id+"F0.wireOp",EDGE,"E730"),sQuery(id+"F0.wireOp",EDGE,"E731"),sQuery(id+"F0.wireOp",EDGE,"E732"),sQuery(id+"F0.wireOp",EDGE,"E733"),sQuery(id+"F0.wireOp",EDGE,"E734"),sQuery(id+"F0.wireOp",EDGE,"E735"),sQuery(id+"F0.wireOp",EDGE,"E736"),sQuery(id+"F0.wireOp",EDGE,"E737"),sQuery(id+"F0.wireOp",EDGE,"E738"),sQuery(id+"F0.wireOp",EDGE,"E739"),sQuery(id+"F0.wireOp",EDGE,"E740"),sQuery(id+"F0.wireOp",EDGE,"E741"),sQuery(id+"F0.wireOp",EDGE,"E742"),sQuery(id+"F0.wireOp",EDGE,"E743"),sQuery(id+"F0.wireOp",EDGE,"E744"),sQuery(id+"F0.wireOp",EDGE,"E745"),sQuery(id+"F0.wireOp",EDGE,"E746"),sQuery(id+"F0.wireOp",EDGE,"E747"),sQuery(id+"F0.wireOp",EDGE,"E748"),sQuery(id+"F0.wireOp",EDGE,"E749"),sQuery(id+"F0.wireOp",EDGE,"E750"),sQuery(id+"F0.wireOp",EDGE,"E751"),sQuery(id+"F0.wireOp",EDGE,"E752"),sQuery(id+"F0.wireOp",EDGE,"E753"),sQuery(id+"F0.wireOp",EDGE,"E754"),sQuery(id+"F0.wireOp",EDGE,"E755"),sQuery(id+"F0.wireOp",EDGE,"E756"),sQuery(id+"F0.wireOp",EDGE,"E757"),sQuery(id+"F0.wireOp",EDGE,"E758"),sQuery(id+"F0.wireOp",EDGE,"E759"),sQuery(id+"F0.wireOp",EDGE,"E760"),sQuery(id+"F0.wireOp",EDGE,"E761"),sQuery(id+"F0.wireOp",EDGE,"E762"),sQuery(id+"F0.wireOp",EDGE,"E763"),sQuery(id+"F0.wireOp",EDGE,"E764"),sQuery(id+"F0.wireOp",EDGE,"E765"),sQuery(id+"F0.wireOp",EDGE,"E766"),sQuery(id+"F0.wireOp",EDGE,"E767"),sQuery(id+"F0.wireOp",EDGE,"E768"),sQuery(id+"F0.wireOp",EDGE,"E769"),sQuery(id+"F0.wireOp",EDGE,"E770"),sQuery(id+"F0.wireOp",EDGE,"E771"),sQuery(id+"F0.wireOp",EDGE,"E772"),sQuery(id+"F0.wireOp",EDGE,"E773"),sQuery(id+"F0.wireOp",EDGE,"E774"),sQuery(id+"F0.wireOp",EDGE,"E775"),sQuery(id+"F0.wireOp",EDGE,"E776"),sQuery(id+"F0.wireOp",EDGE,"E777"),sQuery(id+"F0.wireOp",EDGE,"E778"),sQuery(id+"F0.wireOp",EDGE,"E779"),sQuery(id+"F0.wireOp",EDGE,"E780"),sQuery(id+"F0.wireOp",EDGE,"E781"),sQuery(id+"F0.wireOp",EDGE,"E782"),sQuery(id+"F0.wireOp",EDGE,"E783"),sQuery(id+"F0.wireOp",EDGE,"E784"),sQuery(id+"F0.wireOp",EDGE,"E785"),sQuery(id+"F0.wireOp",EDGE,"E786"),sQuery(id+"F0.wireOp",EDGE,"E787"),sQuery(id+"F0.wireOp",EDGE,"E788"),sQuery(id+"F0.wireOp",EDGE,"E789"),sQuery(id+"F0.wireOp",EDGE,"E790"),sQuery(id+"F0.wireOp",EDGE,"E791"),sQuery(id+"F0.wireOp",EDGE,"E792"),sQuery(id+"F0.wireOp",EDGE,"E793"),sQuery(id+"F0.wireOp",EDGE,"E794"),sQuery(id+"F0.wireOp",EDGE,"E795"),sQuery(id+"F0.wireOp",EDGE,"E796"),sQuery(id+"F0.wireOp",EDGE,"E797"),sQuery(id+"F0.wireOp",EDGE,"E798"),sQuery(id+"F0.wireOp",EDGE,"E799"),sQuery(id+"F0.wireOp",EDGE,"E800"),sQuery(id+"F0.wireOp",EDGE,"E801"),sQuery(id+"F0.wireOp",EDGE,"E802"),sQuery(id+"F0.wireOp",EDGE,"E803"),sQuery(id+"F0.wireOp",EDGE,"E804"),sQuery(id+"F0.wireOp",EDGE,"E805"),sQuery(id+"F0.wireOp",EDGE,"E806"),sQuery(id+"F0.wireOp",EDGE,"E807"),sQuery(id+"F0.wireOp",EDGE,"E808"),sQuery(id+"F0.wireOp",EDGE,"E809"),sQuery(id+"F0.wireOp",EDGE,"E810"),sQuery(id+"F0.wireOp",EDGE,"E811"),sQuery(id+"F0.wireOp",EDGE,"E812"),sQuery(id+"F0.wireOp",EDGE,"E813"),sQuery(id+"F0.wireOp",EDGE,"E814"),sQuery(id+"F0.wireOp",EDGE,"E815"),sQuery(id+"F0.wireOp",EDGE,"E816"),sQuery(id+"F0.wireOp",EDGE,"E817"),sQuery(id+"F0.wireOp",EDGE,"E818"),sQuery(id+"F0.wireOp",EDGE,"E819"),sQuery(id+"F0.wireOp",EDGE,"E820"),sQuery(id+"F0.wireOp",EDGE,"E821"),sQuery(id+"F0.wireOp",EDGE,"E822"),sQuery(id+"F0.wireOp",EDGE,"E823"),sQuery(id+"F0.wireOp",EDGE,"E824"),sQuery(id+"F0.wireOp",EDGE,"E825"),sQuery(id+"F0.wireOp",EDGE,"E826"),sQuery(id+"F0.wireOp",EDGE,"E827"),sQuery(id+"F0.wireOp",EDGE,"E828"),sQuery(id+"F0.wireOp",EDGE,"E829"),sQuery(id+"F0.wireOp",EDGE,"E830"),sQuery(id+"F0.wireOp",EDGE,"E831"),sQuery(id+"F0.wireOp",EDGE,"E832"),sQuery(id+"F0.wireOp",EDGE,"E833"),sQuery(id+"F0.wireOp",EDGE,"E834"),sQuery(id+"F0.wireOp",EDGE,"E835"),sQuery(id+"F0.wireOp",EDGE,"E836"),sQuery(id+"F0.wireOp",EDGE,"E837"),sQuery(id+"F0.wireOp",EDGE,"E838"),sQuery(id+"F0.wireOp",EDGE,"E839"),sQuery(id+"F0.wireOp",EDGE,"E840"),sQuery(id+"F0.wireOp",EDGE,"E841"),sQuery(id+"F0.wireOp",EDGE,"E842"),sQuery(id+"F0.wireOp",EDGE,"E843"),sQuery(id+"F0.wireOp",EDGE,"E844"),sQuery(id+"F0.wireOp",EDGE,"E845"),sQuery(id+"F0.wireOp",EDGE,"E846"),sQuery(id+"F0.wireOp",EDGE,"E847"),sQuery(id+"F0.wireOp",EDGE,"E848"),sQuery(id+"F0.wireOp",EDGE,"E849"),sQuery(id+"F0.wireOp",EDGE,"E850"),sQuery(id+"F0.wireOp",EDGE,"E851"),sQuery(id+"F0.wireOp",EDGE,"E852"),sQuery(id+"F0.wireOp",EDGE,"E853"),sQuery(id+"F0.wireOp",EDGE,"E854"),sQuery(id+"F0.wireOp",EDGE,"E855"),sQuery(id+"F0.wireOp",EDGE,"E856"),sQuery(id+"F0.wireOp",EDGE,"E857"),sQuery(id+"F0.wireOp",EDGE,"E858"),sQuery(id+"F0.wireOp",EDGE,"E859"),sQuery(id+"F0.wireOp",EDGE,"E860"),sQuery(id+"F0.wireOp",EDGE,"E861"),sQuery(id+"F0.wireOp",EDGE,"E862"),sQuery(id+"F0.wireOp",EDGE,"E863"),sQuery(id+"F0.wireOp",EDGE,"E864"),sQuery(id+"F0.wireOp",EDGE,"E865"),sQuery(id+"F0.wireOp",EDGE,"E866"),sQuery(id+"F0.wireOp",EDGE,"E867"),sQuery(id+"F0.wireOp",EDGE,"E868"),sQuery(id+"F0.wireOp",EDGE,"E869"),sQuery(id+"F0.wireOp",EDGE,"E870"),sQuery(id+"F0.wireOp",EDGE,"E871"),sQuery(id+"F0.wireOp",EDGE,"E872"),sQuery(id+"F0.wireOp",EDGE,"E873"),sQuery(id+"F0.wireOp",EDGE,"E874"),sQuery(id+"F0.wireOp",EDGE,"E875"),sQuery(id+"F0.wireOp",EDGE,"E876"),sQuery(id+"F0.wireOp",EDGE,"E877"),sQuery(id+"F0.wireOp",EDGE,"E878"),sQuery(id+"F0.wireOp",EDGE,"E879"),sQuery(id+"F0.wireOp",EDGE,"E880"),sQuery(id+"F0.wireOp",EDGE,"E881"),sQuery(id+"F0.wireOp",EDGE,"E882"),sQuery(id+"F0.wireOp",EDGE,"E883"),sQuery(id+"F0.wireOp",EDGE,"E884"),sQuery(id+"F0.wireOp",EDGE,"E885"),sQuery(id+"F0.wireOp",EDGE,"E886"),sQuery(id+"F0.wireOp",EDGE,"E887"),sQuery(id+"F0.wireOp",EDGE,"E888"),sQuery(id+"F0.wireOp",EDGE,"E889"),sQuery(id+"F0.wireOp",EDGE,"E890"),sQuery(id+"F0.wireOp",EDGE,"E891"),sQuery(id+"F0.wireOp",EDGE,"E892"),sQuery(id+"F0.wireOp",EDGE,"E893"),sQuery(id+"F0.wireOp",EDGE,"E894"),sQuery(id+"F0.wireOp",EDGE,"E895"),sQuery(id+"F0.wireOp",EDGE,"E896"),sQuery(id+"F0.wireOp",EDGE,"E897"),sQuery(id+"F0.wireOp",EDGE,"E898"),sQuery(id+"F0.wireOp",EDGE,"E899"),sQuery(id+"F0.wireOp",EDGE,"E900"),sQuery(id+"F0.wireOp",EDGE,"E901"),sQuery(id+"F0.wireOp",EDGE,"E902"),sQuery(id+"F0.wireOp",EDGE,"E903"),sQuery(id+"F0.wireOp",EDGE,"E904"),sQuery(id+"F0.wireOp",EDGE,"E905"),sQuery(id+"F0.wireOp",EDGE,"E906"),sQuery(id+"F0.wireOp",EDGE,"E907"),sQuery(id+"F0.wireOp",EDGE,"E908"),sQuery(id+"F0.wireOp",EDGE,"E909"),sQuery(id+"F0.wireOp",EDGE,"E910"),sQuery(id+"F0.wireOp",EDGE,"E911"),sQuery(id+"F0.wireOp",EDGE,"E912"),sQuery(id+"F0.wireOp",EDGE,"E913"),sQuery(id+"F0.wireOp",EDGE,"E914"),sQuery(id+"F0.wireOp",EDGE,"E915"),sQuery(id+"F0.wireOp",EDGE,"E916"),sQuery(id+"F0.wireOp",EDGE,"E917"),sQuery(id+"F0.wireOp",EDGE,"E918"),sQuery(id+"F0.wireOp",EDGE,"E919"),sQuery(id+"F0.wireOp",EDGE,"E920"),sQuery(id+"F0.wireOp",EDGE,"E921"),sQuery(id+"F0.wireOp",EDGE,"E922"),sQuery(id+"F0.wireOp",EDGE,"E923"),sQuery(id+"F0.wireOp",EDGE,"E924"),sQuery(id+"F0.wireOp",EDGE,"E925"),sQuery(id+"F0.wireOp",EDGE,"E926"),sQuery(id+"F0.wireOp",EDGE,"E927"),sQuery(id+"F0.wireOp",EDGE,"E928"),sQuery(id+"F0.wireOp",EDGE,"E929"),sQuery(id+"F0.wireOp",EDGE,"E930"),sQuery(id+"F0.wireOp",EDGE,"E931"),sQuery(id+"F0.wireOp",EDGE,"E932"),sQuery(id+"F0.wireOp",EDGE,"E933"),sQuery(id+"F0.wireOp",EDGE,"E934"),sQuery(id+"F0.wireOp",EDGE,"E935"),sQuery(id+"F0.wireOp",EDGE,"E936"),sQuery(id+"F0.wireOp",EDGE,"E937"),sQuery(id+"F0.wireOp",EDGE,"E938"),sQuery(id+"F0.wireOp",EDGE,"E939"),sQuery(id+"F0.wireOp",EDGE,"E940"),sQuery(id+"F0.wireOp",EDGE,"E941"),sQuery(id+"F0.wireOp",EDGE,"E942"),sQuery(id+"F0.wireOp",EDGE,"E943"),sQuery(id+"F0.wireOp",EDGE,"E944"),sQuery(id+"F0.wireOp",EDGE,"E945"),sQuery(id+"F0.wireOp",EDGE,"E946"),sQuery(id+"F0.wireOp",EDGE,"E947"),sQuery(id+"F0.wireOp",EDGE,"E948"),sQuery(id+"F0.wireOp",EDGE,"E949"),sQuery(id+"F0.wireOp",EDGE,"E950"),sQuery(id+"F0.wireOp",EDGE,"E951"),sQuery(id+"F0.wireOp",EDGE,"E952"),sQuery(id+"F0.wireOp",EDGE,"E953"),sQuery(id+"F0.wireOp",EDGE,"E954"),sQuery(id+"F0.wireOp",EDGE,"E955"),sQuery(id+"F0.wireOp",EDGE,"E956"),sQuery(id+"F0.wireOp",EDGE,"E957"),sQuery(id+"F0.wireOp",EDGE,"E958"),sQuery(id+"F0.wireOp",EDGE,"E959"),sQuery(id+"F0.wireOp",EDGE,"E960"),sQuery(id+"F0.wireOp",EDGE,"E961"),sQuery(id+"F0.wireOp",EDGE,"E962"),sQuery(id+"F0.wireOp",EDGE,"E963"),sQuery(id+"F0.wireOp",EDGE,"E964"),sQuery(id+"F0.wireOp",EDGE,"E965"),sQuery(id+"F0.wireOp",EDGE,"E966"),sQuery(id+"F0.wireOp",EDGE,"E967"),sQuery(id+"F0.wireOp",EDGE,"E968"),sQuery(id+"F0.wireOp",EDGE,"E969"),sQuery(id+"F0.wireOp",EDGE,"E970"),sQuery(id+"F0.wireOp",EDGE,"E971"),sQuery(id+"F0.wireOp",EDGE,"E972"),sQuery(id+"F0.wireOp",EDGE,"E973"),sQuery(id+"F0.wireOp",EDGE,"E974"),sQuery(id+"F0.wireOp",EDGE,"E975"),sQuery(id+"F0.wireOp",EDGE,"E976"),sQuery(id+"F0.wireOp",EDGE,"E977"),sQuery(id+"F0.wireOp",EDGE,"E978"),sQuery(id+"F0.wireOp",EDGE,"E979"),sQuery(id+"F0.wireOp",EDGE,"E980"),sQuery(id+"F0.wireOp",EDGE,"E981"),sQuery(id+"F0.wireOp",EDGE,"E982"),sQuery(id+"F0.wireOp",EDGE,"E983"),sQuery(id+"F0.wireOp",EDGE,"E984"),sQuery(id+"F0.wireOp",EDGE,"E985"),sQuery(id+"F0.wireOp",EDGE,"E986"),sQuery(id+"F0.wireOp",EDGE,"E987"),sQuery(id+"F0.wireOp",EDGE,"E988"),sQuery(id+"F0.wireOp",EDGE,"E989"),sQuery(id+"F0.wireOp",EDGE,"E990"),sQuery(id+"F0.wireOp",EDGE,"E991"),sQuery(id+"F0.wireOp",EDGE,"E992"),sQuery(id+"F0.wireOp",EDGE,"E993"),sQuery(id+"F0.wireOp",EDGE,"E994"),sQuery(id+"F0.wireOp",EDGE,"E995"),sQuery(id+"F0.wireOp",EDGE,"E996"),sQuery(id+"F0.wireOp",EDGE,"E997"),sQuery(id+"F0.wireOp",EDGE,"E998"),sQuery(id+"F0.wireOp",EDGE,"E999"),sQuery(id+"F0.wireOp",EDGE,"E1000"),sQuery(id+"F0.wireOp",EDGE,"E1001"),sQuery(id+"F0.wireOp",EDGE,"E1002"),sQuery(id+"F0.wireOp",EDGE,"E1003"),sQuery(id+"F0.wireOp",EDGE,"E1004"),sQuery(id+"F0.wireOp",EDGE,"E1005"),sQuery(id+"F0.wireOp",EDGE,"E1006"),sQuery(id+"F0.wireOp",EDGE,"E1007"),sQuery(id+"F0.wireOp",EDGE,"E1008"),sQuery(id+"F0.wireOp",EDGE,"E1009"),sQuery(id+"F0.wireOp",EDGE,"E1010"),sQuery(id+"F0.wireOp",EDGE,"E1011"),sQuery(id+"F0.wireOp",EDGE,"E1012"),sQuery(id+"F0.wireOp",EDGE,"E1013"),sQuery(id+"F0.wireOp",EDGE,"E1014"),sQuery(id+"F0.wireOp",EDGE,"E1015"),sQuery(id+"F0.wireOp",EDGE,"E1016"),sQuery(id+"F0.wireOp",EDGE,"E1017"),sQuery(id+"F0.wireOp",EDGE,"E1018"),sQuery(id+"F0.wireOp",EDGE,"E1019"),sQuery(id+"F0.wireOp",EDGE,"E1020"),sQuery(id+"F0.wireOp",EDGE,"E1021"),sQuery(id+"F0.wireOp",EDGE,"E1022"),sQuery(id+"F0.wireOp",EDGE,"E1023"),sQuery(id+"F0.wireOp",EDGE,"E1024"),sQuery(id+"F0.wireOp",EDGE,"E1025"),sQuery(id+"F0.wireOp",EDGE,"E1026"),sQuery(id+"F0.wireOp",EDGE,"E1027"),sQuery(id+"F0.wireOp",EDGE,"E1028"),sQuery(id+"F0.wireOp",EDGE,"E1029"),sQuery(id+"F0.wireOp",EDGE,"E1030"),sQuery(id+"F0.wireOp",EDGE,"E1031"),sQuery(id+"F0.wireOp",EDGE,"E1032"),sQuery(id+"F0.wireOp",EDGE,"E1033"),sQuery(id+"F0.wireOp",EDGE,"E1034"),sQuery(id+"F0.wireOp",EDGE,"E1035"),sQuery(id+"F0.wireOp",EDGE,"E1036"),sQuery(id+"F0.wireOp",EDGE,"E1037"),sQuery(id+"F0.wireOp",EDGE,"E1038"),sQuery(id+"F0.wireOp",EDGE,"E1039"),sQuery(id+"F0.wireOp",EDGE,"E1040"),sQuery(id+"F0.wireOp",EDGE,"E1041"),sQuery(id+"F0.wireOp",EDGE,"E1042"),sQuery(id+"F0.wireOp",EDGE,"E1043"),sQuery(id+"F0.wireOp",EDGE,"E1044"),sQuery(id+"F0.wireOp",EDGE,"E1045"),sQuery(id+"F0.wireOp",EDGE,"E1046"),sQuery(id+"F0.wireOp",EDGE,"E1047"),sQuery(id+"F0.wireOp",EDGE,"E1048"),sQuery(id+"F0.wireOp",EDGE,"E1049"),sQuery(id+"F0.wireOp",EDGE,"E1050"),sQuery(id+"F0.wireOp",EDGE,"E1051"),sQuery(id+"F0.wireOp",EDGE,"E1052"),sQuery(id+"F0.wireOp",EDGE,"E1053"),sQuery(id+"F0.wireOp",EDGE,"E1054"),sQuery(id+"F0.wireOp",EDGE,"E1055"),sQuery(id+"F0.wireOp",EDGE,"E1056"),sQuery(id+"F0.wireOp",EDGE,"E1057"),sQuery(id+"F0.wireOp",EDGE,"E1058"),sQuery(id+"F0.wireOp",EDGE,"E1059"),sQuery(id+"F0.wireOp",EDGE,"E1060"),sQuery(id+"F0.wireOp",EDGE,"E1061"),sQuery(id+"F0.wireOp",EDGE,"E1062"),sQuery(id+"F0.wireOp",EDGE,"E1063"),sQuery(id+"F0.wireOp",EDGE,"E1064"),sQuery(id+"F0.wireOp",EDGE,"E1065"),sQuery(id+"F0.wireOp",EDGE,"E1066"),sQuery(id+"F0.wireOp",EDGE,"E1067"),sQuery(id+"F0.wireOp",EDGE,"E1068"),sQuery(id+"F0.wireOp",EDGE,"E1069"),sQuery(id+"F0.wireOp",EDGE,"E1070"),sQuery(id+"F0.wireOp",EDGE,"E1071"),sQuery(id+"F0.wireOp",EDGE,"E1072"),sQuery(id+"F0.wireOp",EDGE,"E1073"),sQuery(id+"F0.wireOp",EDGE,"E1074"),sQuery(id+"F0.wireOp",EDGE,"E1075"),sQuery(id+"F0.wireOp",EDGE,"E1076"),sQuery(id+"F0.wireOp",EDGE,"E1077"),sQuery(id+"F0.wireOp",EDGE,"E1078"),sQuery(id+"F0.wireOp",EDGE,"E1079"),sQuery(id+"F0.wireOp",EDGE,"E1080"),sQuery(id+"F0.wireOp",EDGE,"E1081"),sQuery(id+"F0.wireOp",EDGE,"E1082"),sQuery(id+"F0.wireOp",EDGE,"E1083"),sQuery(id+"F0.wireOp",EDGE,"E1084"),sQuery(id+"F0.wireOp",EDGE,"E1085"),sQuery(id+"F0.wireOp",EDGE,"E1086"),sQuery(id+"F0.wireOp",EDGE,"E1087"),sQuery(id+"F0.wireOp",EDGE,"E1088"),sQuery(id+"F0.wireOp",EDGE,"E1089"),sQuery(id+"F0.wireOp",EDGE,"E1090"),sQuery(id+"F0.wireOp",EDGE,"E1091"),sQuery(id+"F0.wireOp",EDGE,"E1092"),sQuery(id+"F0.wireOp",EDGE,"E1093"),sQuery(id+"F0.wireOp",EDGE,"E1094"),sQuery(id+"F0.wireOp",EDGE,"E1095"),sQuery(id+"F0.wireOp",EDGE,"E1096"),sQuery(id+"F0.wireOp",EDGE,"E1097"),sQuery(id+"F0.wireOp",EDGE,"E1098"),sQuery(id+"F0.wireOp",EDGE,"E1099"),sQuery(id+"F0.wireOp",EDGE,"E1100"),sQuery(id+"F0.wireOp",EDGE,"E1101"),sQuery(id+"F0.wireOp",EDGE,"E1102"),sQuery(id+"F0.wireOp",EDGE,"E1103"),sQuery(id+"F0.wireOp",EDGE,"E1104"),sQuery(id+"F0.wireOp",EDGE,"E1105"),sQuery(id+"F0.wireOp",EDGE,"E1106"),sQuery(id+"F0.wireOp",EDGE,"E1107"),sQuery(id+"F0.wireOp",EDGE,"E1108"),sQuery(id+"F0.wireOp",EDGE,"E1109"),sQuery(id+"F0.wireOp",EDGE,"E1110"),sQuery(id+"F0.wireOp",EDGE,"E1111"),sQuery(id+"F0.wireOp",EDGE,"E1112"),sQuery(id+"F0.wireOp",EDGE,"E1113"),sQuery(id+"F0.wireOp",EDGE,"E1114"),sQuery(id+"F0.wireOp",EDGE,"E1115"),sQuery(id+"F0.wireOp",EDGE,"E1116"),sQuery(id+"F0.wireOp",EDGE,"E1117"),sQuery(id+"F0.wireOp",EDGE,"E1118"),sQuery(id+"F0.wireOp",EDGE,"E1119"),sQuery(id+"F0.wireOp",EDGE,"E1120"),sQuery(id+"F0.wireOp",EDGE,"E1121"),sQuery(id+"F0.wireOp",EDGE,"E1122"),sQuery(id+"F0.wireOp",EDGE,"E1123"),sQuery(id+"F0.wireOp",EDGE,"E1124"),sQuery(id+"F0.wireOp",EDGE,"E1125"),sQuery(id+"F0.wireOp",EDGE,"E1126"),sQuery(id+"F0.wireOp",EDGE,"E1127"),sQuery(id+"F0.wireOp",EDGE,"E1128"),sQuery(id+"F0.wireOp",EDGE,"E1129"),sQuery(id+"F0.wireOp",EDGE,"E1130"),sQuery(id+"F0.wireOp",EDGE,"E1131"),sQuery(id+"F0.wireOp",EDGE,"E1132"),sQuery(id+"F0.wireOp",EDGE,"E1133"),sQuery(id+"F0.wireOp",EDGE,"E1134"),sQuery(id+"F0.wireOp",EDGE,"E1135"),sQuery(id+"F0.wireOp",EDGE,"E1136"),sQuery(id+"F0.wireOp",EDGE,"E1137"),sQuery(id+"F0.wireOp",EDGE,"E1138"),sQuery(id+"F0.wireOp",EDGE,"E1139"),sQuery(id+"F0.wireOp",EDGE,"E1140"),sQuery(id+"F0.wireOp",EDGE,"E1141"),sQuery(id+"F0.wireOp",EDGE,"E1142"),sQuery(id+"F0.wireOp",EDGE,"E1143"),sQuery(id+"F0.wireOp",EDGE,"E1144"),sQuery(id+"F0.wireOp",EDGE,"E1145"),sQuery(id+"F0.wireOp",EDGE,"E1146"),sQuery(id+"F0.wireOp",EDGE,"E1147"),sQuery(id+"F0.wireOp",EDGE,"E1148"),sQuery(id+"F0.wireOp",EDGE,"E1149"),sQuery(id+"F0.wireOp",EDGE,"E1150"),sQuery(id+"F0.wireOp",EDGE,"E1151"),sQuery(id+"F0.wireOp",EDGE,"E1152"),sQuery(id+"F0.wireOp",EDGE,"E1153"),sQuery(id+"F0.wireOp",EDGE,"E1154"),sQuery(id+"F0.wireOp",EDGE,"E1155"),sQuery(id+"F0.wireOp",EDGE,"E1156"),sQuery(id+"F0.wireOp",EDGE,"E1157"),sQuery(id+"F0.wireOp",EDGE,"E1158"),sQuery(id+"F0.wireOp",EDGE,"E1159"),sQuery(id+"F0.wireOp",EDGE,"E1160"),sQuery(id+"F0.wireOp",EDGE,"E1161"),sQuery(id+"F0.wireOp",EDGE,"E1162"),sQuery(id+"F0.wireOp",EDGE,"E1163"),sQuery(id+"F0.wireOp",EDGE,"E1164"),sQuery(id+"F0.wireOp",EDGE,"E1165"),sQuery(id+"F0.wireOp",EDGE,"E1166"),sQuery(id+"F0.wireOp",EDGE,"E1167"),sQuery(id+"F0.wireOp",EDGE,"E1168"),sQuery(id+"F0.wireOp",EDGE,"E1169"),sQuery(id+"F0.wireOp",EDGE,"E1170"),sQuery(id+"F0.wireOp",EDGE,"E1171"),sQuery(id+"F0.wireOp",EDGE,"E1172"),sQuery(id+"F0.wireOp",EDGE,"E1173"),sQuery(id+"F0.wireOp",EDGE,"E1174"),sQuery(id+"F0.wireOp",EDGE,"E1175"),sQuery(id+"F0.wireOp",EDGE,"E1176"),sQuery(id+"F0.wireOp",EDGE,"E1177"),sQuery(id+"F0.wireOp",EDGE,"E1178"),sQuery(id+"F0.wireOp",EDGE,"E1179"),sQuery(id+"F0.wireOp",EDGE,"E1180"),sQuery(id+"F0.wireOp",EDGE,"E1181"),sQuery(id+"F0.wireOp",EDGE,"E1182"),sQuery(id+"F0.wireOp",EDGE,"E1183"),sQuery(id+"F0.wireOp",EDGE,"E1184"),sQuery(id+"F0.wireOp",EDGE,"E1185"),sQuery(id+"F0.wireOp",EDGE,"E1186"),sQuery(id+"F0.wireOp",EDGE,"E1187"),sQuery(id+"F0.wireOp",EDGE,"E1188"),sQuery(id+"F0.wireOp",EDGE,"E1189"),sQuery(id+"F0.wireOp",EDGE,"E1190"),sQuery(id+"F0.wireOp",EDGE,"E1191"),sQuery(id+"F0.wireOp",EDGE,"E1192"),sQuery(id+"F0.wireOp",EDGE,"E1193"),sQuery(id+"F0.wireOp",EDGE,"E1194"),sQuery(id+"F0.wireOp",EDGE,"E1195"),sQuery(id+"F0.wireOp",EDGE,"E1196"),sQuery(id+"F0.wireOp",EDGE,"E1197"),sQuery(id+"F0.wireOp",EDGE,"E1198"),sQuery(id+"F0.wireOp",EDGE,"E1199"),sQuery(id+"F0.wireOp",EDGE,"E1200"),sQuery(id+"F0.wireOp",EDGE,"E1201"),sQuery(id+"F0.wireOp",EDGE,"E1202"),sQuery(id+"F0.wireOp",EDGE,"E1203"),sQuery(id+"F0.wireOp",EDGE,"E1204"),sQuery(id+"F0.wireOp",EDGE,"E1205"),sQuery(id+"F0.wireOp",EDGE,"E1206"),sQuery(id+"F0.wireOp",EDGE,"E1207"),sQuery(id+"F0.wireOp",EDGE,"E1208"),sQuery(id+"F0.wireOp",EDGE,"E1209"),sQuery(id+"F0.wireOp",EDGE,"E1210"),sQuery(id+"F0.wireOp",EDGE,"E1211"),sQuery(id+"F0.wireOp",EDGE,"E1212"),sQuery(id+"F0.wireOp",EDGE,"E1213"),sQuery(id+"F0.wireOp",EDGE,"E1214"),sQuery(id+"F0.wireOp",EDGE,"E1215"),sQuery(id+"F0.wireOp",EDGE,"E1216"),sQuery(id+"F0.wireOp",EDGE,"E1217"),sQuery(id+"F0.wireOp",EDGE,"E1218"),sQuery(id+"F0.wireOp",EDGE,"E1219"),sQuery(id+"F0.wireOp",EDGE,"E1220"),sQuery(id+"F0.wireOp",EDGE,"E1221"),sQuery(id+"F0.wireOp",EDGE,"E1222"),sQuery(id+"F0.wireOp",EDGE,"E1223"),sQuery(id+"F0.wireOp",EDGE,"E1224"),sQuery(id+"F0.wireOp",EDGE,"E1225"),sQuery(id+"F0.wireOp",EDGE,"E1226"),sQuery(id+"F0.wireOp",EDGE,"E1227"),sQuery(id+"F0.wireOp",EDGE,"E1228"),sQuery(id+"F0.wireOp",EDGE,"E1229"),sQuery(id+"F0.wireOp",EDGE,"E1230"),sQuery(id+"F0.wireOp",EDGE,"E1231"),sQuery(id+"F0.wireOp",EDGE,"E1232"),sQuery(id+"F0.wireOp",EDGE,"E1233"),sQuery(id+"F0.wireOp",EDGE,"E1234"),sQuery(id+"F0.wireOp",EDGE,"E1235"),sQuery(id+"F0.wireOp",EDGE,"E1236"),sQuery(id+"F0.wireOp",EDGE,"E1237"),sQuery(id+"F0.wireOp",EDGE,"E1238"),sQuery(id+"F0.wireOp",EDGE,"E1239"),sQuery(id+"F0.wireOp",EDGE,"E1240"),sQuery(id+"F0.wireOp",EDGE,"E1241"),sQuery(id+"F0.wireOp",EDGE,"E1242"),sQuery(id+"F0.wireOp",EDGE,"E1243"),sQuery(id+"F0.wireOp",EDGE,"E1244"),sQuery(id+"F0.wireOp",EDGE,"E1245"),sQuery(id+"F0.wireOp",EDGE,"E1246"),sQuery(id+"F0.wireOp",EDGE,"E1247"),sQuery(id+"F0.wireOp",EDGE,"E1248"),sQuery(id+"F0.wireOp",EDGE,"E1249"),sQuery(id+"F0.wireOp",EDGE,"E1250"),sQuery(id+"F0.wireOp",EDGE,"E1251"),sQuery(id+"F0.wireOp",EDGE,"E1252"),sQuery(id+"F0.wireOp",EDGE,"E1253"),sQuery(id+"F0.wireOp",EDGE,"E1254"),sQuery(id+"F0.wireOp",EDGE,"E1255"),sQuery(id+"F0.wireOp",EDGE,"E1256"),sQuery(id+"F0.wireOp",EDGE,"E1257"),sQuery(id+"F0.wireOp",EDGE,"E1258"),sQuery(id+"F0.wireOp",EDGE,"E1259"),sQuery(id+"F0.wireOp",EDGE,"E1260"),sQuery(id+"F0.wireOp",EDGE,"E1261"),sQuery(id+"F0.wireOp",EDGE,"E1262"),sQuery(id+"F0.wireOp",EDGE,"E1263"),sQuery(id+"F0.wireOp",EDGE,"E1264"),sQuery(id+"F0.wireOp",EDGE,"E1265"),sQuery(id+"F0.wireOp",EDGE,"E1266"),sQuery(id+"F0.wireOp",EDGE,"E1267"),sQuery(id+"F0.wireOp",EDGE,"E1268"),sQuery(id+"F0.wireOp",EDGE,"E1269"),sQuery(id+"F0.wireOp",EDGE,"E1270"),sQuery(id+"F0.wireOp",EDGE,"E1271"),sQuery(id+"F0.wireOp",EDGE,"E1272"),sQuery(id+"F0.wireOp",EDGE,"E1273"),sQuery(id+"F0.wireOp",EDGE,"E1274"),sQuery(id+"F0.wireOp",EDGE,"E1275"),sQuery(id+"F0.wireOp",EDGE,"E1276"),sQuery(id+"F0.wireOp",EDGE,"E1277"),sQuery(id+"F0.wireOp",EDGE,"E1278"),sQuery(id+"F0.wireOp",EDGE,"E1279"),sQuery(id+"F0.wireOp",EDGE,"E1280"),sQuery(id+"F0.wireOp",EDGE,"E1281"),sQuery(id+"F0.wireOp",EDGE,"E1282"),sQuery(id+"F0.wireOp",EDGE,"E1283"),sQuery(id+"F0.wireOp",EDGE,"E1284"),sQuery(id+"F0.wireOp",EDGE,"E1285"),sQuery(id+"F0.wireOp",EDGE,"E1286"),sQuery(id+"F0.wireOp",EDGE,"E1287"),sQuery(id+"F0.wireOp",EDGE,"E1288"),sQuery(id+"F0.wireOp",EDGE,"E1289"),sQuery(id+"F0.wireOp",EDGE,"E1290"),sQuery(id+"F0.wireOp",EDGE,"E1291"),sQuery(id+"F0.wireOp",EDGE,"E1292"),sQuery(id+"F0.wireOp",EDGE,"E1293"),sQuery(id+"F0.wireOp",EDGE,"E1294"),sQuery(id+"F0.wireOp",EDGE,"E1295"),sQuery(id+"F0.wireOp",EDGE,"E1296"),sQuery(id+"F0.wireOp",EDGE,"E1297"),sQuery(id+"F0.wireOp",EDGE,"E1298"),sQuery(id+"F0.wireOp",EDGE,"E1299"),sQuery(id+"F0.wireOp",EDGE,"E1300"),sQuery(id+"F0.wireOp",EDGE,"E1301"),sQuery(id+"F0.wireOp",EDGE,"E1302"),sQuery(id+"F0.wireOp",EDGE,"E1303"),sQuery(id+"F0.wireOp",EDGE,"E1304"),sQuery(id+"F0.wireOp",EDGE,"E1305"),sQuery(id+"F0.wireOp",EDGE,"E1306"),sQuery(id+"F0.wireOp",EDGE,"E1307"),sQuery(id+"F0.wireOp",EDGE,"E1308"),sQuery(id+"F0.wireOp",EDGE,"E1309"),sQuery(id+"F0.wireOp",EDGE,"E1310"),sQuery(id+"F0.wireOp",EDGE,"E1311"),sQuery(id+"F0.wireOp",EDGE,"E1312"),sQuery(id+"F0.wireOp",EDGE,"E1313"),sQuery(id+"F0.wireOp",EDGE,"E1314"),sQuery(id+"F0.wireOp",EDGE,"E1315"),sQuery(id+"F0.wireOp",EDGE,"E1316"),sQuery(id+"F0.wireOp",EDGE,"E1317"),sQuery(id+"F0.wireOp",EDGE,"E1318"),sQuery(id+"F0.wireOp",EDGE,"E1319"),sQuery(id+"F0.wireOp",EDGE,"E1320"),sQuery(id+"F0.wireOp",EDGE,"E1321"),sQuery(id+"F0.wireOp",EDGE,"E1322"),sQuery(id+"F0.wireOp",EDGE,"E1323"),sQuery(id+"F0.wireOp",EDGE,"E1324"),sQuery(id+"F0.wireOp",EDGE,"E1325"),sQuery(id+"F0.wireOp",EDGE,"E1326"),sQuery(id+"F0.wireOp",EDGE,"E1327"),sQuery(id+"F0.wireOp",EDGE,"E1328"),sQuery(id+"F0.wireOp",EDGE,"E1329"),sQuery(id+"F0.wireOp",EDGE,"E1330"),sQuery(id+"F0.wireOp",EDGE,"E1331"),sQuery(id+"F0.wireOp",EDGE,"E1332"),sQuery(id+"F0.wireOp",EDGE,"E1333"),sQuery(id+"F0.wireOp",EDGE,"E1334"),sQuery(id+"F0.wireOp",EDGE,"E1335"),sQuery(id+"F0.wireOp",EDGE,"E1336"),sQuery(id+"F0.wireOp",EDGE,"E1337"),sQuery(id+"F0.wireOp",EDGE,"E1338"),sQuery(id+"F0.wireOp",EDGE,"E1339"),sQuery(id+"F0.wireOp",EDGE,"E1340"),sQuery(id+"F0.wireOp",EDGE,"E1341"),sQuery(id+"F0.wireOp",EDGE,"E1342"),sQuery(id+"F0.wireOp",EDGE,"E1343"),sQuery(id+"F0.wireOp",EDGE,"E1344"),sQuery(id+"F0.wireOp",EDGE,"E1345"),sQuery(id+"F0.wireOp",EDGE,"E1346"),sQuery(id+"F0.wireOp",EDGE,"E1347"),sQuery(id+"F0.wireOp",EDGE,"E1348"),sQuery(id+"F0.wireOp",EDGE,"E1349"),sQuery(id+"F0.wireOp",EDGE,"E1350"),sQuery(id+"F0.wireOp",EDGE,"E1351"),sQuery(id+"F0.wireOp",EDGE,"E1352"),sQuery(id+"F0.wireOp",EDGE,"E1353"),sQuery(id+"F0.wireOp",EDGE,"E1354"),sQuery(id+"F0.wireOp",EDGE,"E1355"),sQuery(id+"F0.wireOp",EDGE,"E1356"),sQuery(id+"F0.wireOp",EDGE,"E1357"),sQuery(id+"F0.wireOp",EDGE,"E1358"),sQuery(id+"F0.wireOp",EDGE,"E1359"),sQuery(id+"F0.wireOp",EDGE,"E1360"),sQuery(id+"F0.wireOp",EDGE,"E1361"),sQuery(id+"F0.wireOp",EDGE,"E1362"),sQuery(id+"F0.wireOp",EDGE,"E1363"),sQuery(id+"F0.wireOp",EDGE,"E1364"),sQuery(id+"F0.wireOp",EDGE,"E1365"),sQuery(id+"F0.wireOp",EDGE,"E1366"),sQuery(id+"F0.wireOp",EDGE,"E1367"),sQuery(id+"F0.wireOp",EDGE,"E1368"),sQuery(id+"F0.wireOp",EDGE,"E1369"),sQuery(id+"F0.wireOp",EDGE,"E1370"),sQuery(id+"F0.wireOp",EDGE,"E1371"),sQuery(id+"F0.wireOp",EDGE,"E1372"),sQuery(id+"F0.wireOp",EDGE,"E1373"),sQuery(id+"F0.wireOp",EDGE,"E1374"),sQuery(id+"F0.wireOp",EDGE,"E1375"),sQuery(id+"F0.wireOp",EDGE,"E1376"),sQuery(id+"F0.wireOp",EDGE,"E1377"),sQuery(id+"F0.wireOp",EDGE,"E1378"),sQuery(id+"F0.wireOp",EDGE,"E1379"),sQuery(id+"F0.wireOp",EDGE,"E1380"),sQuery(id+"F0.wireOp",EDGE,"E1381"),sQuery(id+"F0.wireOp",EDGE,"E1382"),sQuery(id+"F0.wireOp",EDGE,"E1383"),sQuery(id+"F0.wireOp",EDGE,"E1384"),sQuery(id+"F0.wireOp",EDGE,"E1385"),sQuery(id+"F0.wireOp",EDGE,"E1386"),sQuery(id+"F0.wireOp",EDGE,"E1387"),sQuery(id+"F0.wireOp",EDGE,"E1388"),sQuery(id+"F0.wireOp",EDGE,"E1389"),sQuery(id+"F0.wireOp",EDGE,"E1390"),sQuery(id+"F0.wireOp",EDGE,"E1391"),sQuery(id+"F0.wireOp",EDGE,"E1392"),sQuery(id+"F0.wireOp",EDGE,"E1393"),sQuery(id+"F0.wireOp",EDGE,"E1394"),sQuery(id+"F0.wireOp",EDGE,"E1395"),sQuery(id+"F0.wireOp",EDGE,"E1396"),sQuery(id+"F0.wireOp",EDGE,"E1397"),sQuery(id+"F0.wireOp",EDGE,"E1398"),sQuery(id+"F0.wireOp",EDGE,"E1399"),sQuery(id+"F0.wireOp",EDGE,"E1400"),sQuery(id+"F0.wireOp",EDGE,"E1401"),sQuery(id+"F0.wireOp",EDGE,"E1402"),sQuery(id+"F0.wireOp",EDGE,"E1403"),sQuery(id+"F0.wireOp",EDGE,"E1404"),sQuery(id+"F0.wireOp",EDGE,"E1405"),sQuery(id+"F0.wireOp",EDGE,"E1406"),sQuery(id+"F0.wireOp",EDGE,"E1407"),sQuery(id+"F0.wireOp",EDGE,"E1408"),sQuery(id+"F0.wireOp",EDGE,"E1409"),sQuery(id+"F0.wireOp",EDGE,"E1410"),sQuery(id+"F0.wireOp",EDGE,"E1411"),sQuery(id+"F0.wireOp",EDGE,"E1412"),sQuery(id+"F0.wireOp",EDGE,"E1413"),sQuery(id+"F0.wireOp",EDGE,"E1414"),sQuery(id+"F0.wireOp",EDGE,"E1415"),sQuery(id+"F0.wireOp",EDGE,"E1416"),sQuery(id+"F0.wireOp",EDGE,"E1417"),sQuery(id+"F0.wireOp",EDGE,"E1418"),sQuery(id+"F0.wireOp",EDGE,"E1419"),sQuery(id+"F0.wireOp",EDGE,"E1420"),sQuery(id+"F0.wireOp",EDGE,"E1421"),sQuery(id+"F0.wireOp",EDGE,"E1422"),sQuery(id+"F0.wireOp",EDGE,"E1423"),sQuery(id+"F0.wireOp",EDGE,"E1424"),sQuery(id+"F0.wireOp",EDGE,"E1425"),sQuery(id+"F0.wireOp",EDGE,"E1426"),sQuery(id+"F0.wireOp",EDGE,"E1427"),sQuery(id+"F0.wireOp",EDGE,"E1428"),sQuery(id+"F0.wireOp",EDGE,"E1429"),sQuery(id+"F0.wireOp",EDGE,"E1430"),sQuery(id+"F0.wireOp",EDGE,"E1431"),sQuery(id+"F0.wireOp",EDGE,"E1432"),sQuery(id+"F0.wireOp",EDGE,"E1433"),sQuery(id+"F0.wireOp",EDGE,"E1434"),sQuery(id+"F0.wireOp",EDGE,"E1435"),sQuery(id+"F0.wireOp",EDGE,"E1436"),sQuery(id+"F0.wireOp",EDGE,"E1437"),sQuery(id+"F0.wireOp",EDGE,"E1438"),sQuery(id+"F0.wireOp",EDGE,"E1439"),sQuery(id+"F0.wireOp",EDGE,"E1440"),sQuery(id+"F0.wireOp",EDGE,"E1441"),sQuery(id+"F0.wireOp",EDGE,"E1442"),sQuery(id+"F0.wireOp",EDGE,"E1443"),sQuery(id+"F0.wireOp",EDGE,"E1444"),sQuery(id+"F0.wireOp",EDGE,"E1445"),sQuery(id+"F0.wireOp",EDGE,"E1446"),sQuery(id+"F0.wireOp",EDGE,"E1447"),sQuery(id+"F0.wireOp",EDGE,"E1448"),sQuery(id+"F0.wireOp",EDGE,"E1449"),sQuery(id+"F0.wireOp",EDGE,"E1450"),sQuery(id+"F0.wireOp",EDGE,"E1451"),sQuery(id+"F0.wireOp",EDGE,"E1452"),sQuery(id+"F0.wireOp",EDGE,"E1453"),sQuery(id+"F0.wireOp",EDGE,"E1454"),sQuery(id+"F0.wireOp",EDGE,"E1455"),sQuery(id+"F0.wireOp",EDGE,"E1456"),sQuery(id+"F0.wireOp",EDGE,"E1457"),sQuery(id+"F0.wireOp",EDGE,"E1458"),sQuery(id+"F0.wireOp",EDGE,"E1459"),sQuery(id+"F0.wireOp",EDGE,"E1460"),sQuery(id+"F0.wireOp",EDGE,"E1461"),sQuery(id+"F0.wireOp",EDGE,"E1462"),sQuery(id+"F0.wireOp",EDGE,"E1463"),sQuery(id+"F0.wireOp",EDGE,"E1464"),sQuery(id+"F0.wireOp",EDGE,"E1465"),sQuery(id+"F0.wireOp",EDGE,"E1466"),sQuery(id+"F0.wireOp",EDGE,"E1467"),sQuery(id+"F0.wireOp",EDGE,"E1468"),sQuery(id+"F0.wireOp",EDGE,"E1469"),sQuery(id+"F0.wireOp",EDGE,"E1470"),sQuery(id+"F0.wireOp",EDGE,"E1471"),sQuery(id+"F0.wireOp",EDGE,"E1472"),sQuery(id+"F0.wireOp",EDGE,"E1473"),sQuery(id+"F0.wireOp",EDGE,"E1474"),sQuery(id+"F0.wireOp",EDGE,"E1475"),sQuery(id+"F0.wireOp",EDGE,"E1476"),sQuery(id+"F0.wireOp",EDGE,"E1477"),sQuery(id+"F0.wireOp",EDGE,"E1478"),sQuery(id+"F0.wireOp",EDGE,"E1479"),sQuery(id+"F0.wireOp",EDGE,"E1480"),sQuery(id+"F0.wireOp",EDGE,"E1481"),sQuery(id+"F0.wireOp",EDGE,"E1482"),sQuery(id+"F0.wireOp",EDGE,"E1483"),sQuery(id+"F0.wireOp",EDGE,"E1484"),sQuery(id+"F0.wireOp",EDGE,"E1485"),sQuery(id+"F0.wireOp",EDGE,"E1486"),sQuery(id+"F0.wireOp",EDGE,"E1487"),sQuery(id+"F0.wireOp",EDGE,"E1488"),sQuery(id+"F0.wireOp",EDGE,"E1489"),sQuery(id+"F0.wireOp",EDGE,"E1490"),sQuery(id+"F0.wireOp",EDGE,"E1491"),sQuery(id+"F0.wireOp",EDGE,"E1492"),sQuery(id+"F0.wireOp",EDGE,"E1493"),sQuery(id+"F0.wireOp",EDGE,"E1494"),sQuery(id+"F0.wireOp",EDGE,"E1495"),sQuery(id+"F0.wireOp",EDGE,"E1496"),sQuery(id+"F0.wireOp",EDGE,"E1497"),sQuery(id+"F0.wireOp",EDGE,"E1498"),sQuery(id+"F0.wireOp",EDGE,"E1499"),sQuery(id+"F0.wireOp",EDGE,"E1500"),sQuery(id+"F0.wireOp",EDGE,"E1501"),sQuery(id+"F0.wireOp",EDGE,"E1502"),sQuery(id+"F0.wireOp",EDGE,"E1503"),sQuery(id+"F0.wireOp",EDGE,"E1504"),sQuery(id+"F0.wireOp",EDGE,"E1505"),sQuery(id+"F0.wireOp",EDGE,"E1506"),sQuery(id+"F0.wireOp",EDGE,"E1507"),sQuery(id+"F0.wireOp",EDGE,"E1508"),sQuery(id+"F0.wireOp",EDGE,"E1509"),sQuery(id+"F0.wireOp",EDGE,"E1510"),sQuery(id+"F0.wireOp",EDGE,"E1511"),sQuery(id+"F0.wireOp",EDGE,"E1512"),sQuery(id+"F0.wireOp",EDGE,"E1513"),sQuery(id+"F0.wireOp",EDGE,"E1514"),sQuery(id+"F0.wireOp",EDGE,"E1515"),sQuery(id+"F0.wireOp",EDGE,"E1516"),sQuery(id+"F0.wireOp",EDGE,"E1517"),sQuery(id+"F0.wireOp",EDGE,"E1518"),sQuery(id+"F0.wireOp",EDGE,"E1519"),sQuery(id+"F0.wireOp",EDGE,"E1520"),sQuery(id+"F0.wireOp",EDGE,"E1521"),sQuery(id+"F0.wireOp",EDGE,"E1522"),sQuery(id+"F0.wireOp",EDGE,"E1523"),sQuery(id+"F0.wireOp",EDGE,"E1524"),sQuery(id+"F0.wireOp",EDGE,"E1525"),sQuery(id+"F0.wireOp",EDGE,"E1526"),sQuery(id+"F0.wireOp",EDGE,"E1527"),sQuery(id+"F0.wireOp",EDGE,"E1528"),sQuery(id+"F0.wireOp",EDGE,"E1529"),sQuery(id+"F0.wireOp",EDGE,"E1530"),sQuery(id+"F0.wireOp",EDGE,"E1531"),sQuery(id+"F0.wireOp",EDGE,"E1532"),sQuery(id+"F0.wireOp",EDGE,"E1533"),sQuery(id+"F0.wireOp",EDGE,"E1534"),sQuery(id+"F0.wireOp",EDGE,"E1535"),sQuery(id+"F0.wireOp",EDGE,"E1536"),sQuery(id+"F0.wireOp",EDGE,"E1537"),sQuery(id+"F0.wireOp",EDGE,"E1538"),sQuery(id+"F0.wireOp",EDGE,"E1539"),sQuery(id+"F0.wireOp",EDGE,"E1540"),sQuery(id+"F0.wireOp",EDGE,"E1541"),sQuery(id+"F0.wireOp",EDGE,"E1542"),sQuery(id+"F0.wireOp",EDGE,"E1543"),sQuery(id+"F0.wireOp",EDGE,"E1544"),sQuery(id+"F0.wireOp",EDGE,"E1545"),sQuery(id+"F0.wireOp",EDGE,"E1546"),sQuery(id+"F0.wireOp",EDGE,"E1547"),sQuery(id+"F0.wireOp",EDGE,"E1548"),sQuery(id+"F0.wireOp",EDGE,"E1549"),sQuery(id+"F0.wireOp",EDGE,"E1550"),sQuery(id+"F0.wireOp",EDGE,"E1551"),sQuery(id+"F0.wireOp",EDGE,"E1552"),sQuery(id+"F0.wireOp",EDGE,"E1553"),sQuery(id+"F0.wireOp",EDGE,"E1554"),sQuery(id+"F0.wireOp",EDGE,"E1555"),sQuery(id+"F0.wireOp",EDGE,"E1556"),sQuery(id+"F0.wireOp",EDGE,"E1557"),sQuery(id+"F0.wireOp",EDGE,"E1558"),sQuery(id+"F0.wireOp",EDGE,"E1559"),sQuery(id+"F0.wireOp",EDGE,"E1560"),sQuery(id+"F0.wireOp",EDGE,"E1561"),sQuery(id+"F0.wireOp",EDGE,"E1562"),sQuery(id+"F0.wireOp",EDGE,"E1563"),sQuery(id+"F0.wireOp",EDGE,"E1564"),sQuery(id+"F0.wireOp",EDGE,"E1565"),sQuery(id+"F0.wireOp",EDGE,"E1566"),sQuery(id+"F0.wireOp",EDGE,"E1567"),sQuery(id+"F0.wireOp",EDGE,"E1568"),sQuery(id+"F0.wireOp",EDGE,"E1569"),sQuery(id+"F0.wireOp",EDGE,"E1570"),sQuery(id+"F0.wireOp",EDGE,"E1571"),sQuery(id+"F0.wireOp",EDGE,"E1572"),sQuery(id+"F0.wireOp",EDGE,"E1573"),sQuery(id+"F0.wireOp",EDGE,"E1574"),sQuery(id+"F0.wireOp",EDGE,"E1575"),sQuery(id+"F0.wireOp",EDGE,"E1576"),sQuery(id+"F0.wireOp",EDGE,"E1577"),sQuery(id+"F0.wireOp",EDGE,"E1578"),sQuery(id+"F0.wireOp",EDGE,"E1579"),sQuery(id+"F0.wireOp",EDGE,"E1580"),sQuery(id+"F0.wireOp",EDGE,"E1581"),sQuery(id+"F0.wireOp",EDGE,"E1582"),sQuery(id+"F0.wireOp",EDGE,"E1583"),sQuery(id+"F0.wireOp",EDGE,"E1584"),sQuery(id+"F0.wireOp",EDGE,"E1585"),sQuery(id+"F0.wireOp",EDGE,"E1586"),sQuery(id+"F0.wireOp",EDGE,"E1587"),sQuery(id+"F0.wireOp",EDGE,"E1588"),sQuery(id+"F0.wireOp",EDGE,"E1589"),sQuery(id+"F0.wireOp",EDGE,"E1590"),sQuery(id+"F0.wireOp",EDGE,"E1591"),sQuery(id+"F0.wireOp",EDGE,"E1592"),sQuery(id+"F0.wireOp",EDGE,"E1593"),sQuery(id+"F0.wireOp",EDGE,"E1594"),sQuery(id+"F0.wireOp",EDGE,"E1595"),sQuery(id+"F0.wireOp",EDGE,"E1596"),sQuery(id+"F0.wireOp",EDGE,"E1597"),sQuery(id+"F0.wireOp",EDGE,"E1598"),sQuery(id+"F0.wireOp",EDGE,"E1599"),sQuery(id+"F0.wireOp",EDGE,"E1600"),sQuery(id+"F0.wireOp",EDGE,"E1601"),sQuery(id+"F0.wireOp",EDGE,"E1602"),sQuery(id+"F0.wireOp",EDGE,"E1603"),sQuery(id+"F0.wireOp",EDGE,"E1604"),sQuery(id+"F0.wireOp",EDGE,"E1605"),sQuery(id+"F0.wireOp",EDGE,"E1606"),sQuery(id+"F0.wireOp",EDGE,"E1607"),sQuery(id+"F0.wireOp",EDGE,"E1608"),sQuery(id+"F0.wireOp",EDGE,"E1609"),sQuery(id+"F0.wireOp",EDGE,"E1610"),sQuery(id+"F0.wireOp",EDGE,"E1611"),sQuery(id+"F0.wireOp",EDGE,"E1612"),sQuery(id+"F0.wireOp",EDGE,"E1613"),sQuery(id+"F0.wireOp",EDGE,"E1614"),sQuery(id+"F0.wireOp",EDGE,"E1615"),sQuery(id+"F0.wireOp",EDGE,"E1616"),sQuery(id+"F0.wireOp",EDGE,"E1617"),sQuery(id+"F0.wireOp",EDGE,"E1618"),sQuery(id+"F0.wireOp",EDGE,"E1619"),sQuery(id+"F0.wireOp",EDGE,"E1620"),sQuery(id+"F0.wireOp",EDGE,"E1621"),sQuery(id+"F0.wireOp",EDGE,"E1622"),sQuery(id+"F0.wireOp",EDGE,"E1623"),sQuery(id+"F0.wireOp",EDGE,"E1624"),sQuery(id+"F0.wireOp",EDGE,"E1625"),sQuery(id+"F0.wireOp",EDGE,"E1626"),sQuery(id+"F0.wireOp",EDGE,"E1627"),sQuery(id+"F0.wireOp",EDGE,"E1628"),sQuery(id+"F0.wireOp",EDGE,"E1629"),sQuery(id+"F0.wireOp",EDGE,"E1630"),sQuery(id+"F0.wireOp",EDGE,"E1631"),sQuery(id+"F0.wireOp",EDGE,"E1632"),sQuery(id+"F0.wireOp",EDGE,"E1633"),sQuery(id+"F0.wireOp",EDGE,"E1634"),sQuery(id+"F0.wireOp",EDGE,"E1635"),sQuery(id+"F0.wireOp",EDGE,"E1636"),sQuery(id+"F0.wireOp",EDGE,"E1637"),sQuery(id+"F0.wireOp",EDGE,"E1638"),sQuery(id+"F0.wireOp",EDGE,"E1639"),sQuery(id+"F0.wireOp",EDGE,"E1640"),sQuery(id+"F0.wireOp",EDGE,"E1641"),sQuery(id+"F0.wireOp",EDGE,"E1642"),sQuery(id+"F0.wireOp",EDGE,"E1643"),sQuery(id+"F0.wireOp",EDGE,"E1644"),sQuery(id+"F0.wireOp",EDGE,"E1645"),sQuery(id+"F0.wireOp",EDGE,"E1646"),sQuery(id+"F0.wireOp",EDGE,"E1647"),sQuery(id+"F0.wireOp",EDGE,"E1648"),sQuery(id+"F0.wireOp",EDGE,"E1649"),sQuery(id+"F0.wireOp",EDGE,"E1650"),sQuery(id+"F0.wireOp",EDGE,"E1651"),sQuery(id+"F0.wireOp",EDGE,"E1652"),sQuery(id+"F0.wireOp",EDGE,"E1653"),sQuery(id+"F0.wireOp",EDGE,"E1654"),sQuery(id+"F0.wireOp",EDGE,"E1655"),sQuery(id+"F0.wireOp",EDGE,"E1656"),sQuery(id+"F0.wireOp",EDGE,"E1657"),sQuery(id+"F0.wireOp",EDGE,"E1658"),sQuery(id+"F0.wireOp",EDGE,"E1659"),sQuery(id+"F0.wireOp",EDGE,"E1660"),sQuery(id+"F0.wireOp",EDGE,"E1661"),sQuery(id+"F0.wireOp",EDGE,"E1662"),sQuery(id+"F0.wireOp",EDGE,"E1663"),sQuery(id+"F0.wireOp",EDGE,"E1664"),sQuery(id+"F0.wireOp",EDGE,"E1665"),sQuery(id+"F0.wireOp",EDGE,"E1666"),sQuery(id+"F0.wireOp",EDGE,"E1667"),sQuery(id+"F0.wireOp",EDGE,"E1668"),sQuery(id+"F0.wireOp",EDGE,"E1669"),sQuery(id+"F0.wireOp",EDGE,"E1670"),sQuery(id+"F0.wireOp",EDGE,"E1671"),sQuery(id+"F0.wireOp",EDGE,"E1672"),sQuery(id+"F0.wireOp",EDGE,"E1673"),sQuery(id+"F0.wireOp",EDGE,"E1674"),sQuery(id+"F0.wireOp",EDGE,"E1675"),sQuery(id+"F0.wireOp",EDGE,"E1676"),sQuery(id+"F0.wireOp",EDGE,"E1677"),sQuery(id+"F0.wireOp",EDGE,"E1678"),sQuery(id+"F0.wireOp",EDGE,"E1679"),sQuery(id+"F0.wireOp",EDGE,"E1680"),sQuery(id+"F0.wireOp",EDGE,"E1681"),sQuery(id+"F0.wireOp",EDGE,"E1682"),sQuery(id+"F0.wireOp",EDGE,"E1683"),sQuery(id+"F0.wireOp",EDGE,"E1684"),sQuery(id+"F0.wireOp",EDGE,"E1685"),sQuery(id+"F0.wireOp",EDGE,"E1686"),sQuery(id+"F0.wireOp",EDGE,"E1687"),sQuery(id+"F0.wireOp",EDGE,"E1688"),sQuery(id+"F0.wireOp",EDGE,"E1689"),sQuery(id+"F0.wireOp",EDGE,"E1690"),sQuery(id+"F0.wireOp",EDGE,"E1691"),sQuery(id+"F0.wireOp",EDGE,"E1692"),sQuery(id+"F0.wireOp",EDGE,"E1693"),sQuery(id+"F0.wireOp",EDGE,"E1694"),sQuery(id+"F0.wireOp",EDGE,"E1695"),sQuery(id+"F0.wireOp",EDGE,"E1696"),sQuery(id+"F0.wireOp",EDGE,"E1697"),sQuery(id+"F0.wireOp",EDGE,"E1698"),sQuery(id+"F0.wireOp",EDGE,"E1699"),sQuery(id+"F0.wireOp",EDGE,"E1700"),sQuery(id+"F0.wireOp",EDGE,"E1701"),sQuery(id+"F0.wireOp",EDGE,"E1702"),sQuery(id+"F0.wireOp",EDGE,"E1703"),sQuery(id+"F0.wireOp",EDGE,"E1704"),sQuery(id+"F0.wireOp",EDGE,"E1705"),sQuery(id+"F0.wireOp",EDGE,"E1706"),sQuery(id+"F0.wireOp",EDGE,"E1707"),sQuery(id+"F0.wireOp",EDGE,"E1708"),sQuery(id+"F0.wireOp",EDGE,"E1709"),sQuery(id+"F0.wireOp",EDGE,"E1710"),sQuery(id+"F0.wireOp",EDGE,"E1711"),sQuery(id+"F0.wireOp",EDGE,"E1712"),sQuery(id+"F0.wireOp",EDGE,"E1713"),sQuery(id+"F0.wireOp",EDGE,"E1714"),sQuery(id+"F0.wireOp",EDGE,"E1715"),sQuery(id+"F0.wireOp",EDGE,"E1716"),sQuery(id+"F0.wireOp",EDGE,"E1717"),sQuery(id+"F0.wireOp",EDGE,"E1718"),sQuery(id+"F0.wireOp",EDGE,"E1719"),sQuery(id+"F0.wireOp",EDGE,"E1720"),sQuery(id+"F0.wireOp",EDGE,"E1721"),sQuery(id+"F0.wireOp",EDGE,"E1722"),sQuery(id+"F0.wireOp",EDGE,"E1723"),sQuery(id+"F0.wireOp",EDGE,"E1724"),sQuery(id+"F0.wireOp",EDGE,"E1725"),sQuery(id+"F0.wireOp",EDGE,"E1726"),sQuery(id+"F0.wireOp",EDGE,"E1727"),sQuery(id+"F0.wireOp",EDGE,"E1728"),sQuery(id+"F0.wireOp",EDGE,"E1729"),sQuery(id+"F0.wireOp",EDGE,"E1730"),sQuery(id+"F0.wireOp",EDGE,"E1731"),sQuery(id+"F0.wireOp",EDGE,"E1732"),sQuery(id+"F0.wireOp",EDGE,"E1733"),sQuery(id+"F0.wireOp",EDGE,"E1734"),sQuery(id+"F0.wireOp",EDGE,"E1735"),sQuery(id+"F0.wireOp",EDGE,"E1736"),sQuery(id+"F0.wireOp",EDGE,"E1737"),sQuery(id+"F0.wireOp",EDGE,"E1738"),sQuery(id+"F0.wireOp",EDGE,"E1739"),sQuery(id+"F0.wireOp",EDGE,"E1740"),sQuery(id+"F0.wireOp",EDGE,"E1741"),sQuery(id+"F0.wireOp",EDGE,"E1742"),sQuery(id+"F0.wireOp",EDGE,"E1743"),sQuery(id+"F0.wireOp",EDGE,"E1744"),sQuery(id+"F0.wireOp",EDGE,"E1745"),sQuery(id+"F0.wireOp",EDGE,"E1746"),sQuery(id+"F0.wireOp",EDGE,"E1747"),sQuery(id+"F0.wireOp",EDGE,"E1748"),sQuery(id+"F0.wireOp",EDGE,"E1749"),sQuery(id+"F0.wireOp",EDGE,"E1750"),sQuery(id+"F0.wireOp",EDGE,"E1751"),sQuery(id+"F0.wireOp",EDGE,"E1752"),sQuery(id+"F0.wireOp",EDGE,"E1753"),sQuery(id+"F0.wireOp",EDGE,"E1754"),sQuery(id+"F0.wireOp",EDGE,"E1755"),sQuery(id+"F0.wireOp",EDGE,"E1756"),sQuery(id+"F0.wireOp",EDGE,"E1757"),sQuery(id+"F0.wireOp",EDGE,"E1758"),sQuery(id+"F0.wireOp",EDGE,"E1759"),sQuery(id+"F0.wireOp",EDGE,"E1760"),sQuery(id+"F0.wireOp",EDGE,"E1761"),sQuery(id+"F0.wireOp",EDGE,"E1762"),sQuery(id+"F0.wireOp",EDGE,"E1763"),sQuery(id+"F0.wireOp",EDGE,"E1764"),sQuery(id+"F0.wireOp",EDGE,"E1765"),sQuery(id+"F0.wireOp",EDGE,"E1766"),sQuery(id+"F0.wireOp",EDGE,"E1767"),sQuery(id+"F0.wireOp",EDGE,"E1768"),sQuery(id+"F0.wireOp",EDGE,"E1769"),sQuery(id+"F0.wireOp",EDGE,"E1770"),sQuery(id+"F0.wireOp",EDGE,"E1771"),sQuery(id+"F0.wireOp",EDGE,"E1772"),sQuery(id+"F0.wireOp",EDGE,"E1773"),sQuery(id+"F0.wireOp",EDGE,"E1774"),sQuery(id+"F0.wireOp",EDGE,"E1775"),sQuery(id+"F0.wireOp",EDGE,"E1776"),sQuery(id+"F0.wireOp",EDGE,"E1777"),sQuery(id+"F0.wireOp",EDGE,"E1778"),sQuery(id+"F0.wireOp",EDGE,"E1779"),sQuery(id+"F0.wireOp",EDGE,"E1780"),sQuery(id+"F0.wireOp",EDGE,"E1781"),sQuery(id+"F0.wireOp",EDGE,"E1782"),sQuery(id+"F0.wireOp",EDGE,"E1783"),sQuery(id+"F0.wireOp",EDGE,"E1784"),sQuery(id+"F0.wireOp",EDGE,"E1785"),sQuery(id+"F0.wireOp",EDGE,"E1786"),sQuery(id+"F0.wireOp",EDGE,"E1787"),sQuery(id+"F0.wireOp",EDGE,"E1788"),sQuery(id+"F0.wireOp",EDGE,"E1789"),sQuery(id+"F0.wireOp",EDGE,"E1790"),sQuery(id+"F0.wireOp",EDGE,"E1791"),sQuery(id+"F0.wireOp",EDGE,"E1792"),sQuery(id+"F0.wireOp",EDGE,"E1793"),sQuery(id+"F0.wireOp",EDGE,"E1794"),sQuery(id+"F0.wireOp",EDGE,"E1795"),sQuery(id+"F0.wireOp",EDGE,"E1796"),sQuery(id+"F0.wireOp",EDGE,"E1797"),sQuery(id+"F0.wireOp",EDGE,"E1798"),sQuery(id+"F0.wireOp",EDGE,"E1799"),sQuery(id+"F0.wireOp",EDGE,"E1800"),sQuery(id+"F0.wireOp",EDGE,"E1801"),sQuery(id+"F0.wireOp",EDGE,"E1802"),sQuery(id+"F0.wireOp",EDGE,"E1803"),sQuery(id+"F0.wireOp",EDGE,"E1804"),sQuery(id+"F0.wireOp",EDGE,"E1805"),sQuery(id+"F0.wireOp",EDGE,"E1806"),sQuery(id+"F0.wireOp",EDGE,"E1807"),sQuery(id+"F0.wireOp",EDGE,"E1808"),sQuery(id+"F0.wireOp",EDGE,"E1809"),sQuery(id+"F0.wireOp",EDGE,"E1810"),sQuery(id+"F0.wireOp",EDGE,"E1811"),sQuery(id+"F0.wireOp",EDGE,"E1812"),sQuery(id+"F0.wireOp",EDGE,"E1813"),sQuery(id+"F0.wireOp",EDGE,"E1814"),sQuery(id+"F0.wireOp",EDGE,"E1815"),sQuery(id+"F0.wireOp",EDGE,"E1816"),sQuery(id+"F0.wireOp",EDGE,"E1817"),sQuery(id+"F0.wireOp",EDGE,"E1818"),sQuery(id+"F0.wireOp",EDGE,"E1819"),sQuery(id+"F0.wireOp",EDGE,"E1820"),sQuery(id+"F0.wireOp",EDGE,"E1821"),sQuery(id+"F0.wireOp",EDGE,"E1822"),sQuery(id+"F0.wireOp",EDGE,"E1823"),sQuery(id+"F0.wireOp",EDGE,"E1824"),sQuery(id+"F0.wireOp",EDGE,"E1825"),sQuery(id+"F0.wireOp",EDGE,"E1826"),sQuery(id+"F0.wireOp",EDGE,"E1827"),sQuery(id+"F0.wireOp",EDGE,"E1828"),sQuery(id+"F0.wireOp",EDGE,"E1829"),sQuery(id+"F0.wireOp",EDGE,"E1830"),sQuery(id+"F0.wireOp",EDGE,"E1831"),sQuery(id+"F0.wireOp",EDGE,"E1832"),sQuery(id+"F0.wireOp",EDGE,"E1833"),sQuery(id+"F0.wireOp",EDGE,"E1834"),sQuery(id+"F0.wireOp",EDGE,"E1835"),sQuery(id+"F0.wireOp",EDGE,"E1836"),sQuery(id+"F0.wireOp",EDGE,"E1837"),sQuery(id+"F0.wireOp",EDGE,"E1838"),sQuery(id+"F0.wireOp",EDGE,"E1839"),sQuery(id+"F0.wireOp",EDGE,"E1840"),sQuery(id+"F0.wireOp",EDGE,"E1841"),sQuery(id+"F0.wireOp",EDGE,"E1842"),sQuery(id+"F0.wireOp",EDGE,"E1843"),sQuery(id+"F0.wireOp",EDGE,"E1844"),sQuery(id+"F0.wireOp",EDGE,"E1845"),sQuery(id+"F0.wireOp",EDGE,"E1846"),sQuery(id+"F0.wireOp",EDGE,"E1847"),sQuery(id+"F0.wireOp",EDGE,"E1848"),sQuery(id+"F0.wireOp",EDGE,"E1849"),sQuery(id+"F0.wireOp",EDGE,"E1850"),sQuery(id+"F0.wireOp",EDGE,"E1851"),sQuery(id+"F0.wireOp",EDGE,"E1852"),sQuery(id+"F0.wireOp",EDGE,"E1853"),sQuery(id+"F0.wireOp",EDGE,"E1854"),sQuery(id+"F0.wireOp",EDGE,"E1855"),sQuery(id+"F0.wireOp",EDGE,"E1856"),sQuery(id+"F0.wireOp",EDGE,"E1857"),sQuery(id+"F0.wireOp",EDGE,"E1858"),sQuery(id+"F0.wireOp",EDGE,"E1859"),sQuery(id+"F0.wireOp",EDGE,"E1860"),sQuery(id+"F0.wireOp",EDGE,"E1861"),sQuery(id+"F0.wireOp",EDGE,"E1862"),sQuery(id+"F0.wireOp",EDGE,"E1863"),sQuery(id+"F0.wireOp",EDGE,"E1864"),sQuery(id+"F0.wireOp",EDGE,"E1865"),sQuery(id+"F0.wireOp",EDGE,"E1866"),sQuery(id+"F0.wireOp",EDGE,"E1867"),sQuery(id+"F0.wireOp",EDGE,"E1868"),sQuery(id+"F0.wireOp",EDGE,"E1869"),sQuery(id+"F0.wireOp",EDGE,"E1870"),sQuery(id+"F0.wireOp",EDGE,"E1871"),sQuery(id+"F0.wireOp",EDGE,"E1872"),sQuery(id+"F0.wireOp",EDGE,"E1873"),sQuery(id+"F0.wireOp",EDGE,"E1874"),sQuery(id+"F0.wireOp",EDGE,"E1875"),sQuery(id+"F0.wireOp",EDGE,"E1876"),sQuery(id+"F0.wireOp",EDGE,"E1877"),sQuery(id+"F0.wireOp",EDGE,"E1878"),sQuery(id+"F0.wireOp",EDGE,"E1879"),sQuery(id+"F0.wireOp",EDGE,"E1880"),sQuery(id+"F0.wireOp",EDGE,"E1881"),sQuery(id+"F0.wireOp",EDGE,"E1882"),sQuery(id+"F0.wireOp",EDGE,"E1883"),sQuery(id+"F0.wireOp",EDGE,"E1884"),sQuery(id+"F0.wireOp",EDGE,"E1885"),sQuery(id+"F0.wireOp",EDGE,"E1886"),sQuery(id+"F0.wireOp",EDGE,"E1887"),sQuery(id+"F0.wireOp",EDGE,"E1888"),sQuery(id+"F0.wireOp",EDGE,"E1889"),sQuery(id+"F0.wireOp",EDGE,"E1890"),sQuery(id+"F0.wireOp",EDGE,"E1891"),sQuery(id+"F0.wireOp",EDGE,"E1892"),sQuery(id+"F0.wireOp",EDGE,"E1893"),sQuery(id+"F0.wireOp",EDGE,"E1894"),sQuery(id+"F0.wireOp",EDGE,"E1895"),sQuery(id+"F0.wireOp",EDGE,"E1896"),sQuery(id+"F0.wireOp",EDGE,"E1897"),sQuery(id+"F0.wireOp",EDGE,"E1898"),sQuery(id+"F0.wireOp",EDGE,"E1899"),sQuery(id+"F0.wireOp",EDGE,"E1900"),sQuery(id+"F0.wireOp",EDGE,"E1901"),sQuery(id+"F0.wireOp",EDGE,"E1902"),sQuery(id+"F0.wireOp",EDGE,"E1903"),sQuery(id+"F0.wireOp",EDGE,"E1904"),sQuery(id+"F0.wireOp",EDGE,"E1905"),sQuery(id+"F0.wireOp",EDGE,"E1906"),sQuery(id+"F0.wireOp",EDGE,"E1907"),sQuery(id+"F0.wireOp",EDGE,"E1908"),sQuery(id+"F0.wireOp",EDGE,"E1909"),sQuery(id+"F0.wireOp",EDGE,"E1910"),sQuery(id+"F0.wireOp",EDGE,"E1911"),sQuery(id+"F0.wireOp",EDGE,"E1912"),sQuery(id+"F0.wireOp",EDGE,"E1913"),sQuery(id+"F0.wireOp",EDGE,"E1914"),sQuery(id+"F0.wireOp",EDGE,"E1915"),sQuery(id+"F0.wireOp",EDGE,"E1916"),sQuery(id+"F0.wireOp",EDGE,"E1917"),sQuery(id+"F0.wireOp",EDGE,"E1918"),sQuery(id+"F0.wireOp",EDGE,"E1919"),sQuery(id+"F0.wireOp",EDGE,"E1920"),sQuery(id+"F0.wireOp",EDGE,"E1921"),sQuery(id+"F0.wireOp",EDGE,"E1922"),sQuery(id+"F0.wireOp",EDGE,"E1923"),sQuery(id+"F0.wireOp",EDGE,"E1924"),sQuery(id+"F0.wireOp",EDGE,"E1925"),sQuery(id+"F0.wireOp",EDGE,"E1926"),sQuery(id+"F0.wireOp",EDGE,"E1927"),sQuery(id+"F0.wireOp",EDGE,"E1928"),sQuery(id+"F0.wireOp",EDGE,"E1929"),sQuery(id+"F0.wireOp",EDGE,"E1930"),sQuery(id+"F0.wireOp",EDGE,"E1931"),sQuery(id+"F0.wireOp",EDGE,"E1932"),sQuery(id+"F0.wireOp",EDGE,"E1933"),sQuery(id+"F0.wireOp",EDGE,"E1934"),sQuery(id+"F0.wireOp",EDGE,"E1935"),sQuery(id+"F0.wireOp",EDGE,"E1936"),sQuery(id+"F0.wireOp",EDGE,"E1937"),sQuery(id+"F0.wireOp",EDGE,"E1938"),sQuery(id+"F0.wireOp",EDGE,"E1939"),sQuery(id+"F0.wireOp",EDGE,"E1940"),sQuery(id+"F0.wireOp",EDGE,"E1941"),sQuery(id+"F0.wireOp",EDGE,"E1942"),sQuery(id+"F0.wireOp",EDGE,"E1943"),sQuery(id+"F0.wireOp",EDGE,"E1944"),sQuery(id+"F0.wireOp",EDGE,"E1945"),sQuery(id+"F0.wireOp",EDGE,"E1946"),sQuery(id+"F0.wireOp",EDGE,"E1947"),sQuery(id+"F0.wireOp",EDGE,"E1948"),sQuery(id+"F0.wireOp",EDGE,"E1949"),sQuery(id+"F0.wireOp",EDGE,"E1950"),sQuery(id+"F0.wireOp",EDGE,"E1951"),sQuery(id+"F0.wireOp",EDGE,"E1952"),sQuery(id+"F0.wireOp",EDGE,"E1953"),sQuery(id+"F0.wireOp",EDGE,"E1954"),sQuery(id+"F0.wireOp",EDGE,"E1955"),sQuery(id+"F0.wireOp",EDGE,"E1956"),sQuery(id+"F0.wireOp",EDGE,"E1957"),sQuery(id+"F0.wireOp",EDGE,"E1958"),sQuery(id+"F0.wireOp",EDGE,"E1959"),sQuery(id+"F0.wireOp",EDGE,"E1960"),sQuery(id+"F0.wireOp",EDGE,"E1961"),sQuery(id+"F0.wireOp",EDGE,"E1962"),sQuery(id+"F0.wireOp",EDGE,"E1963"),sQuery(id+"F0.wireOp",EDGE,"E1964"),sQuery(id+"F0.wireOp",EDGE,"E1965"),sQuery(id+"F0.wireOp",EDGE,"E1966"),sQuery(id+"F0.wireOp",EDGE,"E1967"),sQuery(id+"F0.wireOp",EDGE,"E1968"),sQuery(id+"F0.wireOp",EDGE,"E1969"),sQuery(id+"F0.wireOp",EDGE,"E1970"),sQuery(id+"F0.wireOp",EDGE,"E1971"),sQuery(id+"F0.wireOp",EDGE,"E1972"),sQuery(id+"F0.wireOp",EDGE,"E1973"),sQuery(id+"F0.wireOp",EDGE,"E1974"),sQuery(id+"F0.wireOp",EDGE,"E1975"),sQuery(id+"F0.wireOp",EDGE,"E1976"),sQuery(id+"F0.wireOp",EDGE,"E1977"),sQuery(id+"F0.wireOp",EDGE,"E1978"),sQuery(id+"F0.wireOp",EDGE,"E1979"),sQuery(id+"F0.wireOp",EDGE,"E1980"),sQuery(id+"F0.wireOp",EDGE,"E1981"),sQuery(id+"F0.wireOp",EDGE,"E1982"),sQuery(id+"F0.wireOp",EDGE,"E1983"),sQuery(id+"F0.wireOp",EDGE,"E1984"),sQuery(id+"F0.wireOp",EDGE,"E1985"),sQuery(id+"F0.wireOp",EDGE,"E1986"),sQuery(id+"F0.wireOp",EDGE,"E1987"),sQuery(id+"F0.wireOp",EDGE,"E1988"),sQuery(id+"F0.wireOp",EDGE,"E1989"),sQuery(id+"F0.wireOp",EDGE,"E1990"),sQuery(id+"F0.wireOp",EDGE,"E1991"),sQuery(id+"F0.wireOp",EDGE,"E1992"),sQuery(id+"F0.wireOp",EDGE,"E1993"),sQuery(id+"F0.wireOp",EDGE,"E1994"),sQuery(id+"F0.wireOp",EDGE,"E1995"),sQuery(id+"F0.wireOp",EDGE,"E1996"),sQuery(id+"F0.wireOp",EDGE,"E1997"),sQuery(id+"F0.wireOp",EDGE,"E1998"),sQuery(id+"F0.wireOp",EDGE,"E1999"),sQuery(id+"F0.wireOp",EDGE,"E2000"),sQuery(id+"F0.wireOp",EDGE,"E2001"),sQuery(id+"F0.wireOp",EDGE,"E2002"),sQuery(id+"F0.wireOp",EDGE,"E2003"),sQuery(id+"F0.wireOp",EDGE,"E2004"),sQuery(id+"F0.wireOp",EDGE,"E2005"),sQuery(id+"F0.wireOp",EDGE,"E2006"),sQuery(id+"F0.wireOp",EDGE,"E2007"),sQuery(id+"F0.wireOp",EDGE,"E2008"),sQuery(id+"F0.wireOp",EDGE,"E2009"),sQuery(id+"F0.wireOp",EDGE,"E2010"),sQuery(id+"F0.wireOp",EDGE,"E2011"),sQuery(id+"F0.wireOp",EDGE,"E2012"),sQuery(id+"F0.wireOp",EDGE,"E2013"),sQuery(id+"F0.wireOp",EDGE,"E2014"),sQuery(id+"F0.wireOp",EDGE,"E2015"),sQuery(id+"F0.wireOp",EDGE,"E2016"),sQuery(id+"F0.wireOp",EDGE,"E2017"),sQuery(id+"F0.wireOp",EDGE,"E2018"),sQuery(id+"F0.wireOp",EDGE,"E2019"),sQuery(id+"F0.wireOp",EDGE,"E2020"),sQuery(id+"F0.wireOp",EDGE,"E2021"),sQuery(id+"F0.wireOp",EDGE,"E2022"),sQuery(id+"F0.wireOp",EDGE,"E2023"),sQuery(id+"F0.wireOp",EDGE,"E2024"),sQuery(id+"F0.wireOp",EDGE,"E2025"),sQuery(id+"F0.wireOp",EDGE,"E2026"),sQuery(id+"F0.wireOp",EDGE,"E2027"),sQuery(id+"F0.wireOp",EDGE,"E2028"),sQuery(id+"F0.wireOp",EDGE,"E2029"),sQuery(id+"F0.wireOp",EDGE,"E2030"),sQuery(id+"F0.wireOp",EDGE,"E2031"),sQuery(id+"F0.wireOp",EDGE,"E2032"),sQuery(id+"F0.wireOp",EDGE,"E2033"),sQuery(id+"F0.wireOp",EDGE,"E2034"),sQuery(id+"F0.wireOp",EDGE,"E2035"),sQuery(id+"F0.wireOp",EDGE,"E2036"),sQuery(id+"F0.wireOp",EDGE,"E2037"),sQuery(id+"F0.wireOp",EDGE,"E2038"),sQuery(id+"F0.wireOp",EDGE,"E2039"),sQuery(id+"F0.wireOp",EDGE,"E2040"),sQuery(id+"F0.wireOp",EDGE,"E2041"),sQuery(id+"F0.wireOp",EDGE,"E2042"),sQuery(id+"F0.wireOp",EDGE,"E2043"),sQuery(id+"F0.wireOp",EDGE,"E2044"),sQuery(id+"F0.wireOp",EDGE,"E2045"),sQuery(id+"F0.wireOp",EDGE,"E2046"),sQuery(id+"F0.wireOp",EDGE,"E2047"),sQuery(id+"F0.wireOp",EDGE,"E2048"),sQuery(id+"F0.wireOp",EDGE,"E2049"),sQuery(id+"F0.wireOp",EDGE,"E2050"),sQuery(id+"F0.wireOp",EDGE,"E2051"),sQuery(id+"F0.wireOp",EDGE,"E2052"),sQuery(id+"F0.wireOp",EDGE,"E2053"),sQuery(id+"F0.wireOp",EDGE,"E2054"),sQuery(id+"F0.wireOp",EDGE,"E2055"),sQuery(id+"F0.wireOp",EDGE,"E2056"),sQuery(id+"F0.wireOp",EDGE,"E2057"),sQuery(id+"F0.wireOp",EDGE,"E2058"),sQuery(id+"F0.wireOp",EDGE,"E2059"),sQuery(id+"F0.wireOp",EDGE,"E2060"),sQuery(id+"F0.wireOp",EDGE,"E2061"),sQuery(id+"F0.wireOp",EDGE,"E2062"),sQuery(id+"F0.wireOp",EDGE,"E2063"),sQuery(id+"F0.wireOp",EDGE,"E2064"),sQuery(id+"F0.wireOp",EDGE,"E2065"),sQuery(id+"F0.wireOp",EDGE,"E2066"),sQuery(id+"F0.wireOp",EDGE,"E2067"),sQuery(id+"F0.wireOp",EDGE,"E2068"),sQuery(id+"F0.wireOp",EDGE,"E2069"),sQuery(id+"F0.wireOp",EDGE,"E2070"),sQuery(id+"F0.wireOp",EDGE,"E2071"),sQuery(id+"F0.wireOp",EDGE,"E2072"),sQuery(id+"F0.wireOp",EDGE,"E2073"),sQuery(id+"F0.wireOp",EDGE,"E2074"),sQuery(id+"F0.wireOp",EDGE,"E2075"),sQuery(id+"F0.wireOp",EDGE,"E2076"),sQuery(id+"F0.wireOp",EDGE,"E2077"),sQuery(id+"F0.wireOp",EDGE,"E2078"),sQuery(id+"F0.wireOp",EDGE,"E2079"),sQuery(id+"F0.wireOp",EDGE,"E2080"),sQuery(id+"F0.wireOp",EDGE,"E2081"),sQuery(id+"F0.wireOp",EDGE,"E2082"),sQuery(id+"F0.wireOp",EDGE,"E2083"),sQuery(id+"F0.wireOp",EDGE,"E2084"),sQuery(id+"F0.wireOp",EDGE,"E2085"),sQuery(id+"F0.wireOp",EDGE,"E2086"),sQuery(id+"F0.wireOp",EDGE,"E2087"),sQuery(id+"F0.wireOp",EDGE,"E2088"),sQuery(id+"F0.wireOp",EDGE,"E2089"),sQuery(id+"F0.wireOp",EDGE,"E2090"),sQuery(id+"F0.wireOp",EDGE,"E2091"),sQuery(id+"F0.wireOp",EDGE,"E2092"),sQuery(id+"F0.wireOp",EDGE,"E2093"),sQuery(id+"F0.wireOp",EDGE,"E2094"),sQuery(id+"F0.wireOp",EDGE,"E2095"),sQuery(id+"F0.wireOp",EDGE,"E2096"),sQuery(id+"F0.wireOp",EDGE,"E2097"),sQuery(id+"F0.wireOp",EDGE,"E2098"),sQuery(id+"F0.wireOp",EDGE,"E2099"),sQuery(id+"F0.wireOp",EDGE,"E2100"),sQuery(id+"F0.wireOp",EDGE,"E2101"),sQuery(id+"F0.wireOp",EDGE,"E2102"),sQuery(id+"F0.wireOp",EDGE,"E2103"),sQuery(id+"F0.wireOp",EDGE,"E2104"),sQuery(id+"F0.wireOp",EDGE,"E2105"),sQuery(id+"F0.wireOp",EDGE,"E2106"),sQuery(id+"F0.wireOp",EDGE,"E2107"),sQuery(id+"F0.wireOp",EDGE,"E2108"),sQuery(id+"F0.wireOp",EDGE,"E2109"),sQuery(id+"F0.wireOp",EDGE,"E2110"),sQuery(id+"F0.wireOp",EDGE,"E2111"),sQuery(id+"F0.wireOp",EDGE,"E2112"),sQuery(id+"F0.wireOp",EDGE,"E2113"),sQuery(id+"F0.wireOp",EDGE,"E2114"),sQuery(id+"F0.wireOp",EDGE,"E2115"),sQuery(id+"F0.wireOp",EDGE,"E2116"),sQuery(id+"F0.wireOp",EDGE,"E2117"),sQuery(id+"F0.wireOp",EDGE,"E2118"),sQuery(id+"F0.wireOp",EDGE,"E2119"),sQuery(id+"F0.wireOp",EDGE,"E2120"),sQuery(id+"F0.wireOp",EDGE,"E2121"),sQuery(id+"F0.wireOp",EDGE,"E2122"),sQuery(id+"F0.wireOp",EDGE,"E2123"),sQuery(id+"F0.wireOp",EDGE,"E2124"),sQuery(id+"F0.wireOp",EDGE,"E2125"),sQuery(id+"F0.wireOp",EDGE,"E2126"),sQuery(id+"F0.wireOp",EDGE,"E2127"),sQuery(id+"F0.wireOp",EDGE,"E2128"),sQuery(id+"F0.wireOp",EDGE,"E2129"),sQuery(id+"F0.wireOp",EDGE,"E2130"),sQuery(id+"F0.wireOp",EDGE,"E2131"),sQuery(id+"F0.wireOp",EDGE,"E2132"),sQuery(id+"F0.wireOp",EDGE,"E2133"),sQuery(id+"F0.wireOp",EDGE,"E2134"),sQuery(id+"F0.wireOp",EDGE,"E2135"),sQuery(id+"F0.wireOp",EDGE,"E2136"),sQuery(id+"F0.wireOp",EDGE,"E2137"),sQuery(id+"F0.wireOp",EDGE,"E2138"),sQuery(id+"F0.wireOp",EDGE,"E2139"),sQuery(id+"F0.wireOp",EDGE,"E2140"),sQuery(id+"F0.wireOp",EDGE,"E2141"),sQuery(id+"F0.wireOp",EDGE,"E2142"),sQuery(id+"F0.wireOp",EDGE,"E2143"),sQuery(id+"F0.wireOp",EDGE,"E2144"),sQuery(id+"F0.wireOp",EDGE,"E2145"),sQuery(id+"F0.wireOp",EDGE,"E2146"),sQuery(id+"F0.wireOp",EDGE,"E2147"),sQuery(id+"F0.wireOp",EDGE,"E2148"),sQuery(id+"F0.wireOp",EDGE,"E2149"),sQuery(id+"F0.wireOp",EDGE,"E2150"),sQuery(id+"F0.wireOp",EDGE,"E2151"),sQuery(id+"F0.wireOp",EDGE,"E2152"),sQuery(id+"F0.wireOp",EDGE,"E2153"),sQuery(id+"F0.wireOp",EDGE,"E2154"),sQuery(id+"F0.wireOp",EDGE,"E2155"),sQuery(id+"F0.wireOp",EDGE,"E2156"),sQuery(id+"F0.wireOp",EDGE,"E2157"),sQuery(id+"F0.wireOp",EDGE,"E2158"),sQuery(id+"F0.wireOp",EDGE,"E2159"),sQuery(id+"F0.wireOp",EDGE,"E2160"),sQuery(id+"F0.wireOp",EDGE,"E2161"),sQuery(id+"F0.wireOp",EDGE,"E2162"),sQuery(id+"F0.wireOp",EDGE,"E2163"),sQuery(id+"F0.wireOp",EDGE,"E2164"),sQuery(id+"F0.wireOp",EDGE,"E2165"),sQuery(id+"F0.wireOp",EDGE,"E2166"),sQuery(id+"F0.wireOp",EDGE,"E2167"),sQuery(id+"F0.wireOp",EDGE,"E2168"),sQuery(id+"F0.wireOp",EDGE,"E2169"),sQuery(id+"F0.wireOp",EDGE,"E2170"),sQuery(id+"F0.wireOp",EDGE,"E2171"),sQuery(id+"F0.wireOp",EDGE,"E2172"),sQuery(id+"F0.wireOp",EDGE,"E2173"),sQuery(id+"F0.wireOp",EDGE,"E2174"),sQuery(id+"F0.wireOp",EDGE,"E2175"),sQuery(id+"F0.wireOp",EDGE,"E2176"),sQuery(id+"F0.wireOp",EDGE,"E2177"),sQuery(id+"F0.wireOp",EDGE,"E2178"),sQuery(id+"F0.wireOp",EDGE,"E2179"),sQuery(id+"F0.wireOp",EDGE,"E2180"),sQuery(id+"F0.wireOp",EDGE,"E2181"),sQuery(id+"F0.wireOp",EDGE,"E2182"),sQuery(id+"F0.wireOp",EDGE,"E2183"),sQuery(id+"F0.wireOp",EDGE,"E2184"),sQuery(id+"F0.wireOp",EDGE,"E2185"),sQuery(id+"F0.wireOp",EDGE,"E2186"),sQuery(id+"F0.wireOp",EDGE,"E2187"),sQuery(id+"F0.wireOp",EDGE,"E2188"),sQuery(id+"F0.wireOp",EDGE,"E2189"),sQuery(id+"F0.wireOp",EDGE,"E2190"),sQuery(id+"F0.wireOp",EDGE,"E2191"),sQuery(id+"F0.wireOp",EDGE,"E2192"),sQuery(id+"F0.wireOp",EDGE,"E2193"),sQuery(id+"F0.wireOp",EDGE,"E2194"),sQuery(id+"F0.wireOp",EDGE,"E2195"),sQuery(id+"F0.wireOp",EDGE,"E2196"),sQuery(id+"F0.wireOp",EDGE,"E2197"),sQuery(id+"F0.wireOp",EDGE,"E2198"),sQuery(id+"F0.wireOp",EDGE,"E2199"),sQuery(id+"F0.wireOp",EDGE,"E2200"),sQuery(id+"F0.wireOp",EDGE,"E2201"),sQuery(id+"F0.wireOp",EDGE,"E2202"),sQuery(id+"F0.wireOp",EDGE,"E2203"),sQuery(id+"F0.wireOp",EDGE,"E2204"),sQuery(id+"F0.wireOp",EDGE,"E2205"),sQuery(id+"F0.wireOp",EDGE,"E2206"),sQuery(id+"F0.wireOp",EDGE,"E2207"),sQuery(id+"F0.wireOp",EDGE,"E2208"),sQuery(id+"F0.wireOp",EDGE,"E2209"),sQuery(id+"F0.wireOp",EDGE,"E2210"),sQuery(id+"F0.wireOp",EDGE,"E2211"),sQuery(id+"F0.wireOp",EDGE,"E2212"),sQuery(id+"F0.wireOp",EDGE,"E2213"),sQuery(id+"F0.wireOp",EDGE,"E2214"),sQuery(id+"F0.wireOp",EDGE,"E2215"),sQuery(id+"F0.wireOp",EDGE,"E2216"),sQuery(id+"F0.wireOp",EDGE,"E2217"),sQuery(id+"F0.wireOp",EDGE,"E2218"),sQuery(id+"F0.wireOp",EDGE,"E2219"),sQuery(id+"F0.wireOp",EDGE,"E2220"),sQuery(id+"F0.wireOp",EDGE,"E2221"),sQuery(id+"F0.wireOp",EDGE,"E2222"),sQuery(id+"F0.wireOp",EDGE,"E2223"),sQuery(id+"F0.wireOp",EDGE,"E2224"),sQuery(id+"F0.wireOp",EDGE,"E2225"),sQuery(id+"F0.wireOp",EDGE,"E2226"),sQuery(id+"F0.wireOp",EDGE,"E2227"),sQuery(id+"F0.wireOp",EDGE,"E2228"),sQuery(id+"F0.wireOp",EDGE,"E2229"),sQuery(id+"F0.wireOp",EDGE,"E2230"),sQuery(id+"F0.wireOp",EDGE,"E2231"),sQuery(id+"F0.wireOp",EDGE,"E2232"),sQuery(id+"F0.wireOp",EDGE,"E2233"),sQuery(id+"F0.wireOp",EDGE,"E2234"),sQuery(id+"F0.wireOp",EDGE,"E2235"),sQuery(id+"F0.wireOp",EDGE,"E2236"),sQuery(id+"F0.wireOp",EDGE,"E2237"),sQuery(id+"F0.wireOp",EDGE,"E2238"),sQuery(id+"F0.wireOp",EDGE,"E2239"),sQuery(id+"F0.wireOp",EDGE,"E2240"),sQuery(id+"F0.wireOp",EDGE,"E2241"),sQuery(id+"F0.wireOp",EDGE,"E2242"),sQuery(id+"F0.wireOp",EDGE,"E2243"),sQuery(id+"F0.wireOp",EDGE,"E2244"),sQuery(id+"F0.wireOp",EDGE,"E2245"),sQuery(id+"F0.wireOp",EDGE,"E2246"),sQuery(id+"F0.wireOp",EDGE,"E2247"),sQuery(id+"F0.wireOp",EDGE,"E2248"),sQuery(id+"F0.wireOp",EDGE,"E2249"),sQuery(id+"F0.wireOp",EDGE,"E2250"),sQuery(id+"F0.wireOp",EDGE,"E2251"),sQuery(id+"F0.wireOp",EDGE,"E2252"),sQuery(id+"F0.wireOp",EDGE,"E2253"),sQuery(id+"F0.wireOp",EDGE,"E2254"),sQuery(id+"F0.wireOp",EDGE,"E2255"),sQuery(id+"F0.wireOp",EDGE,"E2256"),sQuery(id+"F0.wireOp",EDGE,"E2257"),sQuery(id+"F0.wireOp",EDGE,"E2258"),sQuery(id+"F0.wireOp",EDGE,"E2259"),sQuery(id+"F0.wireOp",EDGE,"E2260"),sQuery(id+"F0.wireOp",EDGE,"E2261"),sQuery(id+"F0.wireOp",EDGE,"E2262"),sQuery(id+"F0.wireOp",EDGE,"E2263"),sQuery(id+"F0.wireOp",EDGE,"E2264"),sQuery(id+"F0.wireOp",EDGE,"E2265"),sQuery(id+"F0.wireOp",EDGE,"E2266"),sQuery(id+"F0.wireOp",EDGE,"E2267"),sQuery(id+"F0.wireOp",EDGE,"E2268"),sQuery(id+"F0.wireOp",EDGE,"E2269"),sQuery(id+"F0.wireOp",EDGE,"E2270"),sQuery(id+"F0.wireOp",EDGE,"E2271"),sQuery(id+"F0.wireOp",EDGE,"E2272"),sQuery(id+"F0.wireOp",EDGE,"E2273"),sQuery(id+"F0.wireOp",EDGE,"E2274"),sQuery(id+"F0.wireOp",EDGE,"E2275"),sQuery(id+"F0.wireOp",EDGE,"E2276"),sQuery(id+"F0.wireOp",EDGE,"E2277"),sQuery(id+"F0.wireOp",EDGE,"E2278"),sQuery(id+"F0.wireOp",EDGE,"E2279"),sQuery(id+"F0.wireOp",EDGE,"E2280"),sQuery(id+"F0.wireOp",EDGE,"E2281"),sQuery(id+"F0.wireOp",EDGE,"E2282"),sQuery(id+"F0.wireOp",EDGE,"E2283"),sQuery(id+"F0.wireOp",EDGE,"E2284"),sQuery(id+"F0.wireOp",EDGE,"E2285"),sQuery(id+"F0.wireOp",EDGE,"E2286"),sQuery(id+"F0.wireOp",EDGE,"E2287"),sQuery(id+"F0.wireOp",EDGE,"E2288"),sQuery(id+"F0.wireOp",EDGE,"E2289"),sQuery(id+"F0.wireOp",EDGE,"E2290"),sQuery(id+"F0.wireOp",EDGE,"E2291"),sQuery(id+"F0.wireOp",EDGE,"E2292"),sQuery(id+"F0.wireOp",EDGE,"E2293"),sQuery(id+"F0.wireOp",EDGE,"E2294"),sQuery(id+"F0.wireOp",EDGE,"E2295"),sQuery(id+"F0.wireOp",EDGE,"E2296"),sQuery(id+"F0.wireOp",EDGE,"E2297"),sQuery(id+"F0.wireOp",EDGE,"E2298"),sQuery(id+"F0.wireOp",EDGE,"E2299"),sQuery(id+"F0.wireOp",EDGE,"E2300"),sQuery(id+"F0.wireOp",EDGE,"E2301"),sQuery(id+"F0.wireOp",EDGE,"E2302"),sQuery(id+"F0.wireOp",EDGE,"E2303"),sQuery(id+"F0.wireOp",EDGE,"E2304"),sQuery(id+"F0.wireOp",EDGE,"E2305"),sQuery(id+"F0.wireOp",EDGE,"E2306"),sQuery(id+"F0.wireOp",EDGE,"E2307"),sQuery(id+"F0.wireOp",EDGE,"E2308"),sQuery(id+"F0.wireOp",EDGE,"E2309"),sQuery(id+"F0.wireOp",EDGE,"E2310"),sQuery(id+"F0.wireOp",EDGE,"E2311"),sQuery(id+"F0.wireOp",EDGE,"E2312"),sQuery(id+"F0.wireOp",EDGE,"E2313"),sQuery(id+"F0.wireOp",EDGE,"E2314"),sQuery(id+"F0.wireOp",EDGE,"E2315"),sQuery(id+"F0.wireOp",EDGE,"E2316"),sQuery(id+"F0.wireOp",EDGE,"E2317"),sQuery(id+"F0.wireOp",EDGE,"E2318"),sQuery(id+"F0.wireOp",EDGE,"E2319"),sQuery(id+"F0.wireOp",EDGE,"E2320"),sQuery(id+"F0.wireOp",EDGE,"E2321"),sQuery(id+"F0.wireOp",EDGE,"E2322"),sQuery(id+"F0.wireOp",EDGE,"E2323"),sQuery(id+"F0.wireOp",EDGE,"E2324"),sQuery(id+"F0.wireOp",EDGE,"E2325"),sQuery(id+"F0.wireOp",EDGE,"E2326"),sQuery(id+"F0.wireOp",EDGE,"E2327"),sQuery(id+"F0.wireOp",EDGE,"E2328"),sQuery(id+"F0.wireOp",EDGE,"E2329"),sQuery(id+"F0.wireOp",EDGE,"E2330"),sQuery(id+"F0.wireOp",EDGE,"E2331"),sQuery(id+"F0.wireOp",EDGE,"E2332"),sQuery(id+"F0.wireOp",EDGE,"E2333"),sQuery(id+"F0.wireOp",EDGE,"E2334"),sQuery(id+"F0.wireOp",EDGE,"E2335"),sQuery(id+"F0.wireOp",EDGE,"E2336"),sQuery(id+"F0.wireOp",EDGE,"E2337"),sQuery(id+"F0.wireOp",EDGE,"E2338"),sQuery(id+"F0.wireOp",EDGE,"E2339"),sQuery(id+"F0.wireOp",EDGE,"E2340"),sQuery(id+"F0.wireOp",EDGE,"E2341"),sQuery(id+"F0.wireOp",EDGE,"E2342"),sQuery(id+"F0.wireOp",EDGE,"E2343"),sQuery(id+"F0.wireOp",EDGE,"E2344"),sQuery(id+"F0.wireOp",EDGE,"E2345"),sQuery(id+"F0.wireOp",EDGE,"E2346"),sQuery(id+"F0.wireOp",EDGE,"E2347"),sQuery(id+"F0.wireOp",EDGE,"E2348"),sQuery(id+"F0.wireOp",EDGE,"E2349"),sQuery(id+"F0.wireOp",EDGE,"E2350"),sQuery(id+"F0.wireOp",EDGE,"E2351"),sQuery(id+"F0.wireOp",EDGE,"E2352"),sQuery(id+"F0.wireOp",EDGE,"E2353"),sQuery(id+"F0.wireOp",EDGE,"E2354"),sQuery(id+"F0.wireOp",EDGE,"E2355"),sQuery(id+"F0.wireOp",EDGE,"E2356"),sQuery(id+"F0.wireOp",EDGE,"E2357"),sQuery(id+"F0.wireOp",EDGE,"E2358"),sQuery(id+"F0.wireOp",EDGE,"E2359"),sQuery(id+"F0.wireOp",EDGE,"E2360"),sQuery(id+"F0.wireOp",EDGE,"E2361"),sQuery(id+"F0.wireOp",EDGE,"E2362"),sQuery(id+"F0.wireOp",EDGE,"E2363"),sQuery(id+"F0.wireOp",EDGE,"E2364"),sQuery(id+"F0.wireOp",EDGE,"E2365"),sQuery(id+"F0.wireOp",EDGE,"E2366"),sQuery(id+"F0.wireOp",EDGE,"E2367"),sQuery(id+"F0.wireOp",EDGE,"E2368"),sQuery(id+"F0.wireOp",EDGE,"E2369"),sQuery(id+"F0.wireOp",EDGE,"E2370"),sQuery(id+"F0.wireOp",EDGE,"E2371"),sQuery(id+"F0.wireOp",EDGE,"E2372"),sQuery(id+"F0.wireOp",EDGE,"E2373"),sQuery(id+"F0.wireOp",EDGE,"E2374"),sQuery(id+"F0.wireOp",EDGE,"E2375"),sQuery(id+"F0.wireOp",EDGE,"E2376"),sQuery(id+"F0.wireOp",EDGE,"E2377"),sQuery(id+"F0.wireOp",EDGE,"E2378"),sQuery(id+"F0.wireOp",EDGE,"E2379"),sQuery(id+"F0.wireOp",EDGE,"E2380"),sQuery(id+"F0.wireOp",EDGE,"E2381"),sQuery(id+"F0.wireOp",EDGE,"E2382"),sQuery(id+"F0.wireOp",EDGE,"E2383"),sQuery(id+"F0.wireOp",EDGE,"E2384"),sQuery(id+"F0.wireOp",EDGE,"E2385"),sQuery(id+"F0.wireOp",EDGE,"E2386"),sQuery(id+"F0.wireOp",EDGE,"E2387"),sQuery(id+"F0.wireOp",EDGE,"E2388"),sQuery(id+"F0.wireOp",EDGE,"E2389"),sQuery(id+"F0.wireOp",EDGE,"E2390"),sQuery(id+"F0.wireOp",EDGE,"E2391"),sQuery(id+"F0.wireOp",EDGE,"E2392"),sQuery(id+"F0.wireOp",EDGE,"E2393"),sQuery(id+"F0.wireOp",EDGE,"E2394"),sQuery(id+"F0.wireOp",EDGE,"E2395"),sQuery(id+"F0.wireOp",EDGE,"E2396"),sQuery(id+"F0.wireOp",EDGE,"E2397"),sQuery(id+"F0.wireOp",EDGE,"E2398"),sQuery(id+"F0.wireOp",EDGE,"E2399"),sQuery(id+"F0.wireOp",EDGE,"E2400"),sQuery(id+"F0.wireOp",EDGE,"E2401"),sQuery(id+"F0.wireOp",EDGE,"E2402"),sQuery(id+"F0.wireOp",EDGE,"E2403"),sQuery(id+"F0.wireOp",EDGE,"E2404"),sQuery(id+"F0.wireOp",EDGE,"E2405"),sQuery(id+"F0.wireOp",EDGE,"E2406"),sQuery(id+"F0.wireOp",EDGE,"E2407"),sQuery(id+"F0.wireOp",EDGE,"E2408"),sQuery(id+"F0.wireOp",EDGE,"E2409"),sQuery(id+"F0.wireOp",EDGE,"E2410"),sQuery(id+"F0.wireOp",EDGE,"E2411"),sQuery(id+"F0.wireOp",EDGE,"E2412"),sQuery(id+"F0.wireOp",EDGE,"E2413"),sQuery(id+"F0.wireOp",EDGE,"E2414"),sQuery(id+"F0.wireOp",EDGE,"E2415"),sQuery(id+"F0.wireOp",EDGE,"E2416"),sQuery(id+"F0.wireOp",EDGE,"E2417"),sQuery(id+"F0.wireOp",EDGE,"E2418"),sQuery(id+"F0.wireOp",EDGE,"E2419"),sQuery(id+"F0.wireOp",EDGE,"E2420"),sQuery(id+"F0.wireOp",EDGE,"E2421"),sQuery(id+"F0.wireOp",EDGE,"E2422"),sQuery(id+"F0.wireOp",EDGE,"E2423"),sQuery(id+"F0.wireOp",EDGE,"E2424"),sQuery(id+"F0.wireOp",EDGE,"E2425"),sQuery(id+"F0.wireOp",EDGE,"E2426"),sQuery(id+"F0.wireOp",EDGE,"E2427"),sQuery(id+"F0.wireOp",EDGE,"E2428"),sQuery(id+"F0.wireOp",EDGE,"E2429"),sQuery(id+"F0.wireOp",EDGE,"E2430"),sQuery(id+"F0.wireOp",EDGE,"E2431"),sQuery(id+"F0.wireOp",EDGE,"E2432"),sQuery(id+"F0.wireOp",EDGE,"E2433"),sQuery(id+"F0.wireOp",EDGE,"E2434"),sQuery(id+"F0.wireOp",EDGE,"E2435"),sQuery(id+"F0.wireOp",EDGE,"E2436"),sQuery(id+"F0.wireOp",EDGE,"E2437"),sQuery(id+"F0.wireOp",EDGE,"E2438"),sQuery(id+"F0.wireOp",EDGE,"E2439"),sQuery(id+"F0.wireOp",EDGE,"E2440"),sQuery(id+"F0.wireOp",EDGE,"E2441"),sQuery(id+"F0.wireOp",EDGE,"E2442"),sQuery(id+"F0.wireOp",EDGE,"E2443"),sQuery(id+"F0.wireOp",EDGE,"E2444"),sQuery(id+"F0.wireOp",EDGE,"E2445"),sQuery(id+"F0.wireOp",EDGE,"E2446"),sQuery(id+"F0.wireOp",EDGE,"E2447"),sQuery(id+"F0.wireOp",EDGE,"E2448"),sQuery(id+"F0.wireOp",EDGE,"E2449"),sQuery(id+"F0.wireOp",EDGE,"E2450"),sQuery(id+"F0.wireOp",EDGE,"E2451"),sQuery(id+"F0.wireOp",EDGE,"E2452"),sQuery(id+"F0.wireOp",EDGE,"E2453"),sQuery(id+"F0.wireOp",EDGE,"E2454"),sQuery(id+"F0.wireOp",EDGE,"E2455"),sQuery(id+"F0.wireOp",EDGE,"E2456"),sQuery(id+"F0.wireOp",EDGE,"E2457"),sQuery(id+"F0.wireOp",EDGE,"E2458"),sQuery(id+"F0.wireOp",EDGE,"E2459"),sQuery(id+"F0.wireOp",EDGE,"E2460"),sQuery(id+"F0.wireOp",EDGE,"E2461"),sQuery(id+"F0.wireOp",EDGE,"E2462"),sQuery(id+"F0.wireOp",EDGE,"E2463"),sQuery(id+"F0.wireOp",EDGE,"E2464"),sQuery(id+"F0.wireOp",EDGE,"E2465"),sQuery(id+"F0.wireOp",EDGE,"E2466"),sQuery(id+"F0.wireOp",EDGE,"E2467"),sQuery(id+"F0.wireOp",EDGE,"E2468"),sQuery(id+"F0.wireOp",EDGE,"E2469"),sQuery(id+"F0.wireOp",EDGE,"E2470"),sQuery(id+"F0.wireOp",EDGE,"E2471"),sQuery(id+"F0.wireOp",EDGE,"E2472"),sQuery(id+"F0.wireOp",EDGE,"E2473"),sQuery(id+"F0.wireOp",EDGE,"E2474"),sQuery(id+"F0.wireOp",EDGE,"E2475"),sQuery(id+"F0.wireOp",EDGE,"E2476"),sQuery(id+"F0.wireOp",EDGE,"E2477"),sQuery(id+"F0.wireOp",EDGE,"E2478"),sQuery(id+"F0.wireOp",EDGE,"E2479"),sQuery(id+"F0.wireOp",EDGE,"E2480"),sQuery(id+"F0.wireOp",EDGE,"E2481"),sQuery(id+"F0.wireOp",EDGE,"E2482"),sQuery(id+"F0.wireOp",EDGE,"E2483"),sQuery(id+"F0.wireOp",EDGE,"E2484"),sQuery(id+"F0.wireOp",EDGE,"E2485"),sQuery(id+"F0.wireOp",EDGE,"E2486"),sQuery(id+"F0.wireOp",EDGE,"E2487"),sQuery(id+"F0.wireOp",EDGE,"E2488"),sQuery(id+"F0.wireOp",EDGE,"E2489"),sQuery(id+"F0.wireOp",EDGE,"E2490"),sQuery(id+"F0.wireOp",EDGE,"E2491"),sQuery(id+"F0.wireOp",EDGE,"E2492"),sQuery(id+"F0.wireOp",EDGE,"E2493"),sQuery(id+"F0.wireOp",EDGE,"E2494"),sQuery(id+"F0.wireOp",EDGE,"E2495"),sQuery(id+"F0.wireOp",EDGE,"E2496"),sQuery(id+"F0.wireOp",EDGE,"E2497"),sQuery(id+"F0.wireOp",EDGE,"E2498"),sQuery(id+"F0.wireOp",EDGE,"E2499"),sQuery(id+"F0.wireOp",EDGE,"E2500"),sQuery(id+"F0.wireOp",EDGE,"E2501"),sQuery(id+"F0.wireOp",EDGE,"E2502"),sQuery(id+"F0.wireOp",EDGE,"E2503"),sQuery(id+"F0.wireOp",EDGE,"E2504"),sQuery(id+"F0.wireOp",EDGE,"E2505"),sQuery(id+"F0.wireOp",EDGE,"E2506"),sQuery(id+"F0.wireOp",EDGE,"E2507"),sQuery(id+"F0.wireOp",EDGE,"E2508"),sQuery(id+"F0.wireOp",EDGE,"E2509"),sQuery(id+"F0.wireOp",EDGE,"E2510"),sQuery(id+"F0.wireOp",EDGE,"E2511"),sQuery(id+"F0.wireOp",EDGE,"E2512"),sQuery(id+"F0.wireOp",EDGE,"E2513"),sQuery(id+"F0.wireOp",EDGE,"E2514"),sQuery(id+"F0.wireOp",EDGE,"E2515"),sQuery(id+"F0.wireOp",EDGE,"E2516"),sQuery(id+"F0.wireOp",EDGE,"E2517"),sQuery(id+"F0.wireOp",EDGE,"E2518"),sQuery(id+"F0.wireOp",EDGE,"E2519"),sQuery(id+"F0.wireOp",EDGE,"E2520"),sQuery(id+"F0.wireOp",EDGE,"E2521"),sQuery(id+"F0.wireOp",EDGE,"E2522"),sQuery(id+"F0.wireOp",EDGE,"E2523"),sQuery(id+"F0.wireOp",EDGE,"E2524"),sQuery(id+"F0.wireOp",EDGE,"E2525"),sQuery(id+"F0.wireOp",EDGE,"E2526"),sQuery(id+"F0.wireOp",EDGE,"E2527"),sQuery(id+"F0.wireOp",EDGE,"E2528"),sQuery(id+"F0.wireOp",EDGE,"E2529"),sQuery(id+"F0.wireOp",EDGE,"E2530"),sQuery(id+"F0.wireOp",EDGE,"E2531"),sQuery(id+"F0.wireOp",EDGE,"E2532"),sQuery(id+"F0.wireOp",EDGE,"E2533"),sQuery(id+"F0.wireOp",EDGE,"E2534"),sQuery(id+"F0.wireOp",EDGE,"E2535"),sQuery(id+"F0.wireOp",EDGE,"E2536"),sQuery(id+"F0.wireOp",EDGE,"E2537"),sQuery(id+"F0.wireOp",EDGE,"E2538"),sQuery(id+"F0.wireOp",EDGE,"E2539"),sQuery(id+"F0.wireOp",EDGE,"E2540"),sQuery(id+"F0.wireOp",EDGE,"E2541"),sQuery(id+"F0.wireOp",EDGE,"E2542"),sQuery(id+"F0.wireOp",EDGE,"E2543"),sQuery(id+"F0.wireOp",EDGE,"E2544"),sQuery(id+"F0.wireOp",EDGE,"E2545"),sQuery(id+"F0.wireOp",EDGE,"E2546"),sQuery(id+"F0.wireOp",EDGE,"E2547"),sQuery(id+"F0.wireOp",EDGE,"E2548"),sQuery(id+"F0.wireOp",EDGE,"E2549"),sQuery(id+"F0.wireOp",EDGE,"E2550"),sQuery(id+"F0.wireOp",EDGE,"E2551"),sQuery(id+"F0.wireOp",EDGE,"E2552"),sQuery(id+"F0.wireOp",EDGE,"E2553"),sQuery(id+"F0.wireOp",EDGE,"E2554"),sQuery(id+"F0.wireOp",EDGE,"E2555"),sQuery(id+"F0.wireOp",EDGE,"E2556"),sQuery(id+"F0.wireOp",EDGE,"E2557"),sQuery(id+"F0.wireOp",EDGE,"E2558"),sQuery(id+"F0.wireOp",EDGE,"E2559"),sQuery(id+"F0.wireOp",EDGE,"E2560"),sQuery(id+"F0.wireOp",EDGE,"E2561"),sQuery(id+"F0.wireOp",EDGE,"E2562"),sQuery(id+"F0.wireOp",EDGE,"E2563"),sQuery(id+"F0.wireOp",EDGE,"E2564"),sQuery(id+"F0.wireOp",EDGE,"E2565"),sQuery(id+"F0.wireOp",EDGE,"E2566"),sQuery(id+"F0.wireOp",EDGE,"E2567"),sQuery(id+"F0.wireOp",EDGE,"E2568"),sQuery(id+"F0.wireOp",EDGE,"E2569"),sQuery(id+"F0.wireOp",EDGE,"E2570"),sQuery(id+"F0.wireOp",EDGE,"E2571"),sQuery(id+"F0.wireOp",EDGE,"E2572"),sQuery(id+"F0.wireOp",EDGE,"E2573"),sQuery(id+"F0.wireOp",EDGE,"E2574"),sQuery(id+"F0.wireOp",EDGE,"E2575"),sQuery(id+"F0.wireOp",EDGE,"E2576"),sQuery(id+"F0.wireOp",EDGE,"E2577"),sQuery(id+"F0.wireOp",EDGE,"E2578"),sQuery(id+"F0.wireOp",EDGE,"E2579"),sQuery(id+"F0.wireOp",EDGE,"E2580"),sQuery(id+"F0.wireOp",EDGE,"E2581"),sQuery(id+"F0.wireOp",EDGE,"E2582"),sQuery(id+"F0.wireOp",EDGE,"E2583"),sQuery(id+"F0.wireOp",EDGE,"E2584"),sQuery(id+"F0.wireOp",EDGE,"E2585"),sQuery(id+"F0.wireOp",EDGE,"E2586"),sQuery(id+"F0.wireOp",EDGE,"E2587"),sQuery(id+"F0.wireOp",EDGE,"E2588"),sQuery(id+"F0.wireOp",EDGE,"E2589"),sQuery(id+"F0.wireOp",EDGE,"E2590"),sQuery(id+"F0.wireOp",EDGE,"E2591"),sQuery(id+"F0.wireOp",EDGE,"E2592"),sQuery(id+"F0.wireOp",EDGE,"E2593"),sQuery(id+"F0.wireOp",EDGE,"E2594"),sQuery(id+"F0.wireOp",EDGE,"E2595"),sQuery(id+"F0.wireOp",EDGE,"E2596"),sQuery(id+"F0.wireOp",EDGE,"E2597"),sQuery(id+"F0.wireOp",EDGE,"E2598"),sQuery(id+"F0.wireOp",EDGE,"E2599"),sQuery(id+"F0.wireOp",EDGE,"E2600"),sQuery(id+"F0.wireOp",EDGE,"E2601"),sQuery(id+"F0.wireOp",EDGE,"E2602"),sQuery(id+"F0.wireOp",EDGE,"E2603"),sQuery(id+"F0.wireOp",EDGE,"E2604"),sQuery(id+"F0.wireOp",EDGE,"E2605"),sQuery(id+"F0.wireOp",EDGE,"E2606"),sQuery(id+"F0.wireOp",EDGE,"E2607"),sQuery(id+"F0.wireOp",EDGE,"E2608"),sQuery(id+"F0.wireOp",EDGE,"E2609"),sQuery(id+"F0.wireOp",EDGE,"E2610"),sQuery(id+"F0.wireOp",EDGE,"E2611"),sQuery(id+"F0.wireOp",EDGE,"E2612"),sQuery(id+"F0.wireOp",EDGE,"E2613"),sQuery(id+"F0.wireOp",EDGE,"E2614"),sQuery(id+"F0.wireOp",EDGE,"E2615"),sQuery(id+"F0.wireOp",EDGE,"E2616"),sQuery(id+"F0.wireOp",EDGE,"E2617"),sQuery(id+"F0.wireOp",EDGE,"E2618"),sQuery(id+"F0.wireOp",EDGE,"E2619"),sQuery(id+"F0.wireOp",EDGE,"E2620"),sQuery(id+"F0.wireOp",EDGE,"E2621"),sQuery(id+"F0.wireOp",EDGE,"E2622"),sQuery(id+"F0.wireOp",EDGE,"E2623"),sQuery(id+"F0.wireOp",EDGE,"E2624"),sQuery(id+"F0.wireOp",EDGE,"E2625"),sQuery(id+"F0.wireOp",EDGE,"E2626"),sQuery(id+"F0.wireOp",EDGE,"E2627"),sQuery(id+"F0.wireOp",EDGE,"E2628"),sQuery(id+"F0.wireOp",EDGE,"E2629"),sQuery(id+"F0.wireOp",EDGE,"E2630"),sQuery(id+"F0.wireOp",EDGE,"E2631"),sQuery(id+"F0.wireOp",EDGE,"E2632"),sQuery(id+"F0.wireOp",EDGE,"E2633"),sQuery(id+"F0.wireOp",EDGE,"E2634"),sQuery(id+"F0.wireOp",EDGE,"E2635"),sQuery(id+"F0.wireOp",EDGE,"E2636"),sQuery(id+"F0.wireOp",EDGE,"E2637"),sQuery(id+"F0.wireOp",EDGE,"E2638"),sQuery(id+"F0.wireOp",EDGE,"E2639"),sQuery(id+"F0.wireOp",EDGE,"E2640"),sQuery(id+"F0.wireOp",EDGE,"E2641"),sQuery(id+"F0.wireOp",EDGE,"E2642"),sQuery(id+"F0.wireOp",EDGE,"E2643"),sQuery(id+"F0.wireOp",EDGE,"E2644"),sQuery(id+"F0.wireOp",EDGE,"E2645"),sQuery(id+"F0.wireOp",EDGE,"E2646"),sQuery(id+"F0.wireOp",EDGE,"E2647"),sQuery(id+"F0.wireOp",EDGE,"E2648"),sQuery(id+"F0.wireOp",EDGE,"E2649"),sQuery(id+"F0.wireOp",EDGE,"E2650"),sQuery(id+"F0.wireOp",EDGE,"E2651"),sQuery(id+"F0.wireOp",EDGE,"E2652"),sQuery(id+"F0.wireOp",EDGE,"E2653"),sQuery(id+"F0.wireOp",EDGE,"E2654"),sQuery(id+"F0.wireOp",EDGE,"E2655"),sQuery(id+"F0.wireOp",EDGE,"E2656"),sQuery(id+"F0.wireOp",EDGE,"E2657"),sQuery(id+"F0.wireOp",EDGE,"E2658"),sQuery(id+"F0.wireOp",EDGE,"E2659"),sQuery(id+"F0.wireOp",EDGE,"E2660"),sQuery(id+"F0.wireOp",EDGE,"E2661"),sQuery(id+"F0.wireOp",EDGE,"E2662"),sQuery(id+"F0.wireOp",EDGE,"E2663"),sQuery(id+"F0.wireOp",EDGE,"E2664"),sQuery(id+"F0.wireOp",EDGE,"E2665"),sQuery(id+"F0.wireOp",EDGE,"E2666"),sQuery(id+"F0.wireOp",EDGE,"E2667"),sQuery(id+"F0.wireOp",EDGE,"E2668"),sQuery(id+"F0.wireOp",EDGE,"E2669"),sQuery(id+"F0.wireOp",EDGE,"E2670"),sQuery(id+"F0.wireOp",EDGE,"E2671"),sQuery(id+"F0.wireOp",EDGE,"E2672"),sQuery(id+"F0.wireOp",EDGE,"E2673"),sQuery(id+"F0.wireOp",EDGE,"E2674"),sQuery(id+"F0.wireOp",EDGE,"E2675"),sQuery(id+"F0.wireOp",EDGE,"E2676"),sQuery(id+"F0.wireOp",EDGE,"E2677"),sQuery(id+"F0.wireOp",EDGE,"E2678"),sQuery(id+"F0.wireOp",EDGE,"E2679"),sQuery(id+"F0.wireOp",EDGE,"E2680"),sQuery(id+"F0.wireOp",EDGE,"E2681"),sQuery(id+"F0.wireOp",EDGE,"E2682"),sQuery(id+"F0.wireOp",EDGE,"E2683"),sQuery(id+"F0.wireOp",EDGE,"E2684"),sQuery(id+"F0.wireOp",EDGE,"E2685"),sQuery(id+"F0.wireOp",EDGE,"E2686"),sQuery(id+"F0.wireOp",EDGE,"E2687"),sQuery(id+"F0.wireOp",EDGE,"E2688"),sQuery(id+"F0.wireOp",EDGE,"E2689"),sQuery(id+"F0.wireOp",EDGE,"E2690"),sQuery(id+"F0.wireOp",EDGE,"E2691"),sQuery(id+"F0.wireOp",EDGE,"E2692"),sQuery(id+"F0.wireOp",EDGE,"E2693"),sQuery(id+"F0.wireOp",EDGE,"E2694"),sQuery(id+"F0.wireOp",EDGE,"E2695"),sQuery(id+"F0.wireOp",EDGE,"E2696"),sQuery(id+"F0.wireOp",EDGE,"E2697"),sQuery(id+"F0.wireOp",EDGE,"E2698"),sQuery(id+"F0.wireOp",EDGE,"E2699"),sQuery(id+"F0.wireOp",EDGE,"E2700"),sQuery(id+"F0.wireOp",EDGE,"E2701"),sQuery(id+"F0.wireOp",EDGE,"E2702"),sQuery(id+"F0.wireOp",EDGE,"E2703"),sQuery(id+"F0.wireOp",EDGE,"E2704"),sQuery(id+"F0.wireOp",EDGE,"E2705"),sQuery(id+"F0.wireOp",EDGE,"E2706"),sQuery(id+"F0.wireOp",EDGE,"E2707"),sQuery(id+"F0.wireOp",EDGE,"E2708"),sQuery(id+"F0.wireOp",EDGE,"E2709"),sQuery(id+"F0.wireOp",EDGE,"E2710"),sQuery(id+"F0.wireOp",EDGE,"E2711"),sQuery(id+"F0.wireOp",EDGE,"E2712"),sQuery(id+"F0.wireOp",EDGE,"E2713"),sQuery(id+"F0.wireOp",EDGE,"E2714"),sQuery(id+"F0.wireOp",EDGE,"E2715"),sQuery(id+"F0.wireOp",EDGE,"E2716"),sQuery(id+"F0.wireOp",EDGE,"E2717"),sQuery(id+"F0.wireOp",EDGE,"E2718"),sQuery(id+"F0.wireOp",EDGE,"E2719"),sQuery(id+"F0.wireOp",EDGE,"E2720"),sQuery(id+"F0.wireOp",EDGE,"E2721"),sQuery(id+"F0.wireOp",EDGE,"E2722"),sQuery(id+"F0.wireOp",EDGE,"E2723"),sQuery(id+"F0.wireOp",EDGE,"E2724"),sQuery(id+"F0.wireOp",EDGE,"E2725"),sQuery(id+"F0.wireOp",EDGE,"E2726"),sQuery(id+"F0.wireOp",EDGE,"E2727"),sQuery(id+"F0.wireOp",EDGE,"E2728"),sQuery(id+"F0.wireOp",EDGE,"E2729"),sQuery(id+"F0.wireOp",EDGE,"E2730"),sQuery(id+"F0.wireOp",EDGE,"E2731"),sQuery(id+"F0.wireOp",EDGE,"E2732"),sQuery(id+"F0.wireOp",EDGE,"E2733"),sQuery(id+"F0.wireOp",EDGE,"E2734"),sQuery(id+"F0.wireOp",EDGE,"E2735"),sQuery(id+"F0.wireOp",EDGE,"E2736"),sQuery(id+"F0.wireOp",EDGE,"E2737"),sQuery(id+"F0.wireOp",EDGE,"E2738"),sQuery(id+"F0.wireOp",EDGE,"E2739"),sQuery(id+"F0.wireOp",EDGE,"E2740"),sQuery(id+"F0.wireOp",EDGE,"E2741"),sQuery(id+"F0.wireOp",EDGE,"E2742"),sQuery(id+"F0.wireOp",EDGE,"E2743"),sQuery(id+"F0.wireOp",EDGE,"E2744"),sQuery(id+"F0.wireOp",EDGE,"E2745"),sQuery(id+"F0.wireOp",EDGE,"E2746"),sQuery(id+"F0.wireOp",EDGE,"E2747"),sQuery(id+"F0.wireOp",EDGE,"E2748"),sQuery(id+"F0.wireOp",EDGE,"E2749"),sQuery(id+"F0.wireOp",EDGE,"E2750"),sQuery(id+"F0.wireOp",EDGE,"E2751"),sQuery(id+"F0.wireOp",EDGE,"E2752"),sQuery(id+"F0.wireOp",EDGE,"E2753"),sQuery(id+"F0.wireOp",EDGE,"E2754"),sQuery(id+"F0.wireOp",EDGE,"E2755"),sQuery(id+"F0.wireOp",EDGE,"E2756"),sQuery(id+"F0.wireOp",EDGE,"E2757"),sQuery(id+"F0.wireOp",EDGE,"E2758"),sQuery(id+"F0.wireOp",EDGE,"E2759"),sQuery(id+"F0.wireOp",EDGE,"E2760"),sQuery(id+"F0.wireOp",EDGE,"E2761"),sQuery(id+"F0.wireOp",EDGE,"E2762"),sQuery(id+"F0.wireOp",EDGE,"E2763"),sQuery(id+"F0.wireOp",EDGE,"E2764"),sQuery(id+"F0.wireOp",EDGE,"E2765"),sQuery(id+"F0.wireOp",EDGE,"E2766"),sQuery(id+"F0.wireOp",EDGE,"E2767"),sQuery(id+"F0.wireOp",EDGE,"E2768"),sQuery(id+"F0.wireOp",EDGE,"E2769"),sQuery(id+"F0.wireOp",EDGE,"E2770"),sQuery(id+"F0.wireOp",EDGE,"E2771"),sQuery(id+"F0.wireOp",EDGE,"E2772"),sQuery(id+"F0.wireOp",EDGE,"E2773"),sQuery(id+"F0.wireOp",EDGE,"E2774"),sQuery(id+"F0.wireOp",EDGE,"E2775"),sQuery(id+"F0.wireOp",EDGE,"E2776"),sQuery(id+"F0.wireOp",EDGE,"E2777"),sQuery(id+"F0.wireOp",EDGE,"E2778"),sQuery(id+"F0.wireOp",EDGE,"E2779"),sQuery(id+"F0.wireOp",EDGE,"E2780"),sQuery(id+"F0.wireOp",EDGE,"E2781"),sQuery(id+"F0.wireOp",EDGE,"E2782"),sQuery(id+"F0.wireOp",EDGE,"E2783"),sQuery(id+"F0.wireOp",EDGE,"E2784"),sQuery(id+"F0.wireOp",EDGE,"E2785"),sQuery(id+"F0.wireOp",EDGE,"E2786"),sQuery(id+"F0.wireOp",EDGE,"E2787"),sQuery(id+"F0.wireOp",EDGE,"E2788"),sQuery(id+"F0.wireOp",EDGE,"E2789"),sQuery(id+"F0.wireOp",EDGE,"E2790"),sQuery(id+"F0.wireOp",EDGE,"E2791"),sQuery(id+"F0.wireOp",EDGE,"E2792"),sQuery(id+"F0.wireOp",EDGE,"E2793"),sQuery(id+"F0.wireOp",EDGE,"E2794"),sQuery(id+"F0.wireOp",EDGE,"E2795"),sQuery(id+"F0.wireOp",EDGE,"E2796"),sQuery(id+"F0.wireOp",EDGE,"E2797"),sQuery(id+"F0.wireOp",EDGE,"E2798"),sQuery(id+"F0.wireOp",EDGE,"E2799"),sQuery(id+"F0.wireOp",EDGE,"E2800"),sQuery(id+"F0.wireOp",EDGE,"E2801"),sQuery(id+"F0.wireOp",EDGE,"E2802"),sQuery(id+"F0.wireOp",EDGE,"E2803"),sQuery(id+"F0.wireOp",EDGE,"E2804"),sQuery(id+"F0.wireOp",EDGE,"E2805"),sQuery(id+"F0.wireOp",EDGE,"E2806"),sQuery(id+"F0.wireOp",EDGE,"E2807"),sQuery(id+"F0.wireOp",EDGE,"E2808"),sQuery(id+"F0.wireOp",EDGE,"E2809"),sQuery(id+"F0.wireOp",EDGE,"E2810"),sQuery(id+"F0.wireOp",EDGE,"E2811"),sQuery(id+"F0.wireOp",EDGE,"E2812"),sQuery(id+"F0.wireOp",EDGE,"E2813"),sQuery(id+"F0.wireOp",EDGE,"E2814"),sQuery(id+"F0.wireOp",EDGE,"E2815"),sQuery(id+"F0.wireOp",EDGE,"E2816"),sQuery(id+"F0.wireOp",EDGE,"E2817"),sQuery(id+"F0.wireOp",EDGE,"E2818"),sQuery(id+"F0.wireOp",EDGE,"E2819"),sQuery(id+"F0.wireOp",EDGE,"E2820"),sQuery(id+"F0.wireOp",EDGE,"E2821"),sQuery(id+"F0.wireOp",EDGE,"E2822"),sQuery(id+"F0.wireOp",EDGE,"E2823"),sQuery(id+"F0.wireOp",EDGE,"E2824"),sQuery(id+"F0.wireOp",EDGE,"E2825"),sQuery(id+"F0.wireOp",EDGE,"E2826"),sQuery(id+"F0.wireOp",EDGE,"E2827"),sQuery(id+"F0.wireOp",EDGE,"E2828"),sQuery(id+"F0.wireOp",EDGE,"E2829"),sQuery(id+"F0.wireOp",EDGE,"E2830"),sQuery(id+"F0.wireOp",EDGE,"E2831"),sQuery(id+"F0.wireOp",EDGE,"E2832"),sQuery(id+"F0.wireOp",EDGE,"E2833"),sQuery(id+"F0.wireOp",EDGE,"E2834"),sQuery(id+"F0.wireOp",EDGE,"E2835"),sQuery(id+"F0.wireOp",EDGE,"E2836"),sQuery(id+"F0.wireOp",EDGE,"E2837"),sQuery(id+"F0.wireOp",EDGE,"E2838"),sQuery(id+"F0.wireOp",EDGE,"E2839"),sQuery(id+"F0.wireOp",EDGE,"E2840"),sQuery(id+"F0.wireOp",EDGE,"E2841"),sQuery(id+"F0.wireOp",EDGE,"E2842"),sQuery(id+"F0.wireOp",EDGE,"E2843"),sQuery(id+"F0.wireOp",EDGE,"E2844"),sQuery(id+"F0.wireOp",EDGE,"E2845"),sQuery(id+"F0.wireOp",EDGE,"E2846"),sQuery(id+"F0.wireOp",EDGE,"E2847"),sQuery(id+"F0.wireOp",EDGE,"E2848"),sQuery(id+"F0.wireOp",EDGE,"E2849"),sQuery(id+"F0.wireOp",EDGE,"E2850"),sQuery(id+"F0.wireOp",EDGE,"E2851"),sQuery(id+"F0.wireOp",EDGE,"E2852"),sQuery(id+"F0.wireOp",EDGE,"E2853"),sQuery(id+"F0.wireOp",EDGE,"E2854"),sQuery(id+"F0.wireOp",EDGE,"E2855"),sQuery(id+"F0.wireOp",EDGE,"E2856"),sQuery(id+"F0.wireOp",EDGE,"E2857"),sQuery(id+"F0.wireOp",EDGE,"E2858"),sQuery(id+"F0.wireOp",EDGE,"E2859"),sQuery(id+"F0.wireOp",EDGE,"E2860"),sQuery(id+"F0.wireOp",EDGE,"E2861"),sQuery(id+"F0.wireOp",EDGE,"E2862"),sQuery(id+"F0.wireOp",EDGE,"E2863"),sQuery(id+"F0.wireOp",EDGE,"E2864"),sQuery(id+"F0.wireOp",EDGE,"E2865"),sQuery(id+"F0.wireOp",EDGE,"E2866"),sQuery(id+"F0.wireOp",EDGE,"E2867"),sQuery(id+"F0.wireOp",EDGE,"E2868"),sQuery(id+"F0.wireOp",EDGE,"E2869"),sQuery(id+"F0.wireOp",EDGE,"E2870"),sQuery(id+"F0.wireOp",EDGE,"E2871"),sQuery(id+"F0.wireOp",EDGE,"E2872"),sQuery(id+"F0.wireOp",EDGE,"E2873"),sQuery(id+"F0.wireOp",EDGE,"E2874"),sQuery(id+"F0.wireOp",EDGE,"E2875"),sQuery(id+"F0.wireOp",EDGE,"E2876"),sQuery(id+"F0.wireOp",EDGE,"E2877"),sQuery(id+"F0.wireOp",EDGE,"E2878"),sQuery(id+"F0.wireOp",EDGE,"E2879"),sQuery(id+"F0.wireOp",EDGE,"E2880"),sQuery(id+"F0.wireOp",EDGE,"E2881"),sQuery(id+"F0.wireOp",EDGE,"E2882"),sQuery(id+"F0.wireOp",EDGE,"E2883"),sQuery(id+"F0.wireOp",EDGE,"E2884"),sQuery(id+"F0.wireOp",EDGE,"E2885"),sQuery(id+"F0.wireOp",EDGE,"E2886"),sQuery(id+"F0.wireOp",EDGE,"E2887"),sQuery(id+"F0.wireOp",EDGE,"E2888"),sQuery(id+"F0.wireOp",EDGE,"E2889"),sQuery(id+"F0.wireOp",EDGE,"E2890"),sQuery(id+"F0.wireOp",EDGE,"E2891"),sQuery(id+"F0.wireOp",EDGE,"E2892"),sQuery(id+"F0.wireOp",EDGE,"E2893"),sQuery(id+"F0.wireOp",EDGE,"E2894"),sQuery(id+"F0.wireOp",EDGE,"E2895"),sQuery(id+"F0.wireOp",EDGE,"E2896"),sQuery(id+"F0.wireOp",EDGE,"E2897"),sQuery(id+"F0.wireOp",EDGE,"E2898"),sQuery(id+"F0.wireOp",EDGE,"E2899"),sQuery(id+"F0.wireOp",EDGE,"E2900"),sQuery(id+"F0.wireOp",EDGE,"E2901"),sQuery(id+"F0.wireOp",EDGE,"E2902"),sQuery(id+"F0.wireOp",EDGE,"E2903"),sQuery(id+"F0.wireOp",EDGE,"E2904"),sQuery(id+"F0.wireOp",EDGE,"E2905"),sQuery(id+"F0.wireOp",EDGE,"E2906"),sQuery(id+"F0.wireOp",EDGE,"E2907"),sQuery(id+"F0.wireOp",EDGE,"E2908"),sQuery(id+"F0.wireOp",EDGE,"E2909"),sQuery(id+"F0.wireOp",EDGE,"E2910"),sQuery(id+"F0.wireOp",EDGE,"E2911"),sQuery(id+"F0.wireOp",EDGE,"E2912"),sQuery(id+"F0.wireOp",EDGE,"E2913"),sQuery(id+"F0.wireOp",EDGE,"E2914"),sQuery(id+"F0.wireOp",EDGE,"E2915"),sQuery(id+"F0.wireOp",EDGE,"E2916"),sQuery(id+"F0.wireOp",EDGE,"E2917"),sQuery(id+"F0.wireOp",EDGE,"E2918"),sQuery(id+"F0.wireOp",EDGE,"E2919"),sQuery(id+"F0.wireOp",EDGE,"E2920"),sQuery(id+"F0.wireOp",EDGE,"E2921"),sQuery(id+"F0.wireOp",EDGE,"E2922"),sQuery(id+"F0.wireOp",EDGE,"E2923"),sQuery(id+"F0.wireOp",EDGE,"E2924"),sQuery(id+"F0.wireOp",EDGE,"E2925"),sQuery(id+"F0.wireOp",EDGE,"E2926"),sQuery(id+"F0.wireOp",EDGE,"E2927"),sQuery(id+"F0.wireOp",EDGE,"E2928"),sQuery(id+"F0.wireOp",EDGE,"E2929"),sQuery(id+"F0.wireOp",EDGE,"E2930"),sQuery(id+"F0.wireOp",EDGE,"E2931"),sQuery(id+"F0.wireOp",EDGE,"E2932"),sQuery(id+"F0.wireOp",EDGE,"E2933"),sQuery(id+"F0.wireOp",EDGE,"E2934"),sQuery(id+"F0.wireOp",EDGE,"E2935"),sQuery(id+"F0.wireOp",EDGE,"E2936"),sQuery(id+"F0.wireOp",EDGE,"E2937"),sQuery(id+"F0.wireOp",EDGE,"E2938"),sQuery(id+"F0.wireOp",EDGE,"E2939"),sQuery(id+"F0.wireOp",EDGE,"E2940"),sQuery(id+"F0.wireOp",EDGE,"E2941"),sQuery(id+"F0.wireOp",EDGE,"E2942"),sQuery(id+"F0.wireOp",EDGE,"E2943"),sQuery(id+"F0.wireOp",EDGE,"E2944"),sQuery(id+"F0.wireOp",EDGE,"E2945"),sQuery(id+"F0.wireOp",EDGE,"E2946"),sQuery(id+"F0.wireOp",EDGE,"E2947"),sQuery(id+"F0.wireOp",EDGE,"E2948"),sQuery(id+"F0.wireOp",EDGE,"E2949"),sQuery(id+"F0.wireOp",EDGE,"E2950"),sQuery(id+"F0.wireOp",EDGE,"E2951"),sQuery(id+"F0.wireOp",EDGE,"E2952"),sQuery(id+"F0.wireOp",EDGE,"E2953"),sQuery(id+"F0.wireOp",EDGE,"E2954"),sQuery(id+"F0.wireOp",EDGE,"E2955"),sQuery(id+"F0.wireOp",EDGE,"E2956"),sQuery(id+"F0.wireOp",EDGE,"E2957"),sQuery(id+"F0.wireOp",EDGE,"E2958"),sQuery(id+"F0.wireOp",EDGE,"E2959"),sQuery(id+"F0.wireOp",EDGE,"E2960"),sQuery(id+"F0.wireOp",EDGE,"E2961"),sQuery(id+"F0.wireOp",EDGE,"E2962"),sQuery(id+"F0.wireOp",EDGE,"E2963"),sQuery(id+"F0.wireOp",EDGE,"E2964"),sQuery(id+"F0.wireOp",EDGE,"E2965"),sQuery(id+"F0.wireOp",EDGE,"E2966"),sQuery(id+"F0.wireOp",EDGE,"E2967"),sQuery(id+"F0.wireOp",EDGE,"E2968"),sQuery(id+"F0.wireOp",EDGE,"E2969"),sQuery(id+"F0.wireOp",EDGE,"E2970"),sQuery(id+"F0.wireOp",EDGE,"E2971"),sQuery(id+"F0.wireOp",EDGE,"E2972"),sQuery(id+"F0.wireOp",EDGE,"E2973"),sQuery(id+"F0.wireOp",EDGE,"E2974"),sQuery(id+"F0.wireOp",EDGE,"E2975"),sQuery(id+"F0.wireOp",EDGE,"E2976"),sQuery(id+"F0.wireOp",EDGE,"E2977"),sQuery(id+"F0.wireOp",EDGE,"E2978"),sQuery(id+"F0.wireOp",EDGE,"E2979"),sQuery(id+"F0.wireOp",EDGE,"E2980"),sQuery(id+"F0.wireOp",EDGE,"E2981"),sQuery(id+"F0.wireOp",EDGE,"E2982"),sQuery(id+"F0.wireOp",EDGE,"E2983"),sQuery(id+"F0.wireOp",EDGE,"E2984"),sQuery(id+"F0.wireOp",EDGE,"E2985"),sQuery(id+"F0.wireOp",EDGE,"E2986"),sQuery(id+"F0.wireOp",EDGE,"E2987"),sQuery(id+"F0.wireOp",EDGE,"E2988"),sQuery(id+"F0.wireOp",EDGE,"E2989"),sQuery(id+"F0.wireOp",EDGE,"E2990"),sQuery(id+"F0.wireOp",EDGE,"E2991"),sQuery(id+"F0.wireOp",EDGE,"E2992"),sQuery(id+"F0.wireOp",EDGE,"E2993"),sQuery(id+"F0.wireOp",EDGE,"E2994"),sQuery(id+"F0.wireOp",EDGE,"E2995"),sQuery(id+"F0.wireOp",EDGE,"E2996"),sQuery(id+"F0.wireOp",EDGE,"E2997"),sQuery(id+"F0.wireOp",EDGE,"E2998"),sQuery(id+"F0.wireOp",EDGE,"E2999"),sQuery(id+"F0.wireOp",EDGE,"E3000"),sQuery(id+"F0.wireOp",EDGE,"E3001"),sQuery(id+"F0.wireOp",EDGE,"E3002"),sQuery(id+"F0.wireOp",EDGE,"E3003"),sQuery(id+"F0.wireOp",EDGE,"E3004"),sQuery(id+"F0.wireOp",EDGE,"E3005"),sQuery(id+"F0.wireOp",EDGE,"E3006"),sQuery(id+"F0.wireOp",EDGE,"E3007"),sQuery(id+"F0.wireOp",EDGE,"E3008"),sQuery(id+"F0.wireOp",EDGE,"E3009"),sQuery(id+"F0.wireOp",EDGE,"E3010"),sQuery(id+"F0.wireOp",EDGE,"E3011"),sQuery(id+"F0.wireOp",EDGE,"E3012"),sQuery(id+"F0.wireOp",EDGE,"E3013"),sQuery(id+"F0.wireOp",EDGE,"E3014"),sQuery(id+"F0.wireOp",EDGE,"E3015"),sQuery(id+"F0.wireOp",EDGE,"E3016"),sQuery(id+"F0.wireOp",EDGE,"E3017"),sQuery(id+"F0.wireOp",EDGE,"E3018"),sQuery(id+"F0.wireOp",EDGE,"E3019"),sQuery(id+"F0.wireOp",EDGE,"E3020"),sQuery(id+"F0.wireOp",EDGE,"E3021"),sQuery(id+"F0.wireOp",EDGE,"E3022"),sQuery(id+"F0.wireOp",EDGE,"E3023"),sQuery(id+"F0.wireOp",EDGE,"E3024"),sQuery(id+"F0.wireOp",EDGE,"E3025"),sQuery(id+"F0.wireOp",EDGE,"E3026"),sQuery(id+"F0.wireOp",EDGE,"E3027"),sQuery(id+"F0.wireOp",EDGE,"E3028"),sQuery(id+"F0.wireOp",EDGE,"E3029"),sQuery(id+"F0.wireOp",EDGE,"E3030"),sQuery(id+"F0.wireOp",EDGE,"E3031"),sQuery(id+"F0.wireOp",EDGE,"E3032"),sQuery(id+"F0.wireOp",EDGE,"E3033"),sQuery(id+"F0.wireOp",EDGE,"E3034"),sQuery(id+"F0.wireOp",EDGE,"E3035"),sQuery(id+"F0.wireOp",EDGE,"E3036"),sQuery(id+"F0.wireOp",EDGE,"E3037"),sQuery(id+"F0.wireOp",EDGE,"E3038"),sQuery(id+"F0.wireOp",EDGE,"E3039"),sQuery(id+"F0.wireOp",EDGE,"E3040"),sQuery(id+"F0.wireOp",EDGE,"E3041"),sQuery(id+"F0.wireOp",EDGE,"E3042"),sQuery(id+"F0.wireOp",EDGE,"E3043"),sQuery(id+"F0.wireOp",EDGE,"E3044"),sQuery(id+"F0.wireOp",EDGE,"E3045"),sQuery(id+"F0.wireOp",EDGE,"E3046"),sQuery(id+"F0.wireOp",EDGE,"E3047"),sQuery(id+"F0.wireOp",EDGE,"E3048"),sQuery(id+"F0.wireOp",EDGE,"E3049"),sQuery(id+"F0.wireOp",EDGE,"E3050"),sQuery(id+"F0.wireOp",EDGE,"E3051"),sQuery(id+"F0.wireOp",EDGE,"E3052"),sQuery(id+"F0.wireOp",EDGE,"E3053"),sQuery(id+"F0.wireOp",EDGE,"E3054"),sQuery(id+"F0.wireOp",EDGE,"E3055"),sQuery(id+"F0.wireOp",EDGE,"E3056"),sQuery(id+"F0.wireOp",EDGE,"E3057"),sQuery(id+"F0.wireOp",EDGE,"E3058"),sQuery(id+"F0.wireOp",EDGE,"E3059"),sQuery(id+"F0.wireOp",EDGE,"E3060"),sQuery(id+"F0.wireOp",EDGE,"E3061"),sQuery(id+"F0.wireOp",EDGE,"E3062"),sQuery(id+"F0.wireOp",EDGE,"E3063"),sQuery(id+"F0.wireOp",EDGE,"E3064"),sQuery(id+"F0.wireOp",EDGE,"E3065"),sQuery(id+"F0.wireOp",EDGE,"E3066"),sQuery(id+"F0.wireOp",EDGE,"E3067"),sQuery(id+"F0.wireOp",EDGE,"E3068"),sQuery(id+"F0.wireOp",EDGE,"E3069"),sQuery(id+"F0.wireOp",EDGE,"E3070"),sQuery(id+"F0.wireOp",EDGE,"E3071"),sQuery(id+"F0.wireOp",EDGE,"E3072"),sQuery(id+"F0.wireOp",EDGE,"E3073"),sQuery(id+"F0.wireOp",EDGE,"E3074"),sQuery(id+"F0.wireOp",EDGE,"E3075"),sQuery(id+"F0.wireOp",EDGE,"E3076"),sQuery(id+"F0.wireOp",EDGE,"E3077"),sQuery(id+"F0.wireOp",EDGE,"E3078"),sQuery(id+"F0.wireOp",EDGE,"E3079"),sQuery(id+"F0.wireOp",EDGE,"E3080"),sQuery(id+"F0.wireOp",EDGE,"E3081"),sQuery(id+"F0.wireOp",EDGE,"E3082"),sQuery(id+"F0.wireOp",EDGE,"E3083"),sQuery(id+"F0.wireOp",EDGE,"E3084"),sQuery(id+"F0.wireOp",EDGE,"E3085"),sQuery(id+"F0.wireOp",EDGE,"E3086"),sQuery(id+"F0.wireOp",EDGE,"E3087"),sQuery(id+"F0.wireOp",EDGE,"E3088"),sQuery(id+"F0.wireOp",EDGE,"E3089"),sQuery(id+"F0.wireOp",EDGE,"E3090"),sQuery(id+"F0.wireOp",EDGE,"E3091"),sQuery(id+"F0.wireOp",EDGE,"E3092"),sQuery(id+"F0.wireOp",EDGE,"E3093"),sQuery(id+"F0.wireOp",EDGE,"E3094"),sQuery(id+"F0.wireOp",EDGE,"E3095"),sQuery(id+"F0.wireOp",EDGE,"E3096"),sQuery(id+"F0.wireOp",EDGE,"E3097"),sQuery(id+"F0.wireOp",EDGE,"E3098"),sQuery(id+"F0.wireOp",EDGE,"E3099"),sQuery(id+"F0.wireOp",EDGE,"E3100"),sQuery(id+"F0.wireOp",EDGE,"E3101"),sQuery(id+"F0.wireOp",EDGE,"E3102"),sQuery(id+"F0.wireOp",EDGE,"E3103"),sQuery(id+"F0.wireOp",EDGE,"E3104"),sQuery(id+"F0.wireOp",EDGE,"E3105"),sQuery(id+"F0.wireOp",EDGE,"E3106"),sQuery(id+"F0.wireOp",EDGE,"E3107"),sQuery(id+"F0.wireOp",EDGE,"E3108"),sQuery(id+"F0.wireOp",EDGE,"E3109"),sQuery(id+"F0.wireOp",EDGE,"E3110"),sQuery(id+"F0.wireOp",EDGE,"E3111"),sQuery(id+"F0.wireOp",EDGE,"E3112"),sQuery(id+"F0.wireOp",EDGE,"E3113"),sQuery(id+"F0.wireOp",EDGE,"E3114"),sQuery(id+"F0.wireOp",EDGE,"E3115"),sQuery(id+"F0.wireOp",EDGE,"E3116"),sQuery(id+"F0.wireOp",EDGE,"E3117"),sQuery(id+"F0.wireOp",EDGE,"E3118"),sQuery(id+"F0.wireOp",EDGE,"E3119"),sQuery(id+"F0.wireOp",EDGE,"E3120"),sQuery(id+"F0.wireOp",EDGE,"E3121"),sQuery(id+"F0.wireOp",EDGE,"E3122"),sQuery(id+"F0.wireOp",EDGE,"E3123"),sQuery(id+"F0.wireOp",EDGE,"E3124"),sQuery(id+"F0.wireOp",EDGE,"E3125"),sQuery(id+"F0.wireOp",EDGE,"E3126"),sQuery(id+"F0.wireOp",EDGE,"E3127"),sQuery(id+"F0.wireOp",EDGE,"E3128"),sQuery(id+"F0.wireOp",EDGE,"E3129"),sQuery(id+"F0.wireOp",EDGE,"E3130"),sQuery(id+"F0.wireOp",EDGE,"E3131"),sQuery(id+"F0.wireOp",EDGE,"E3132"),sQuery(id+"F0.wireOp",EDGE,"E3133"),sQuery(id+"F0.wireOp",EDGE,"E3134"),sQuery(id+"F0.wireOp",EDGE,"E3135"),sQuery(id+"F0.wireOp",EDGE,"E3136"),sQuery(id+"F0.wireOp",EDGE,"E3137"),sQuery(id+"F0.wireOp",EDGE,"E3138"),sQuery(id+"F0.wireOp",EDGE,"E3139"),sQuery(id+"F0.wireOp",EDGE,"E3140"),sQuery(id+"F0.wireOp",EDGE,"E3141"),sQuery(id+"F0.wireOp",EDGE,"E3142"),sQuery(id+"F0.wireOp",EDGE,"E3143"),sQuery(id+"F0.wireOp",EDGE,"E3144"),sQuery(id+"F0.wireOp",EDGE,"E3145"),sQuery(id+"F0.wireOp",EDGE,"E3146"),sQuery(id+"F0.wireOp",EDGE,"E3147"),sQuery(id+"F0.wireOp",EDGE,"E3148"),sQuery(id+"F0.wireOp",EDGE,"E3149"),sQuery(id+"F0.wireOp",EDGE,"E3150"),sQuery(id+"F0.wireOp",EDGE,"E3151"),sQuery(id+"F0.wireOp",EDGE,"E3152"),sQuery(id+"F0.wireOp",EDGE,"E3153"),sQuery(id+"F0.wireOp",EDGE,"E3154"),sQuery(id+"F0.wireOp",EDGE,"E3155"),sQuery(id+"F0.wireOp",EDGE,"E3156"),sQuery(id+"F0.wireOp",EDGE,"E3157"),sQuery(id+"F0.wireOp",EDGE,"E3158"),sQuery(id+"F0.wireOp",EDGE,"E3159"),sQuery(id+"F0.wireOp",EDGE,"E3160"),sQuery(id+"F0.wireOp",EDGE,"E3161"),sQuery(id+"F0.wireOp",EDGE,"E3162"),sQuery(id+"F0.wireOp",EDGE,"E3163"),sQuery(id+"F0.wireOp",EDGE,"E3164"),sQuery(id+"F0.wireOp",EDGE,"E3165"),sQuery(id+"F0.wireOp",EDGE,"E3166"),sQuery(id+"F0.wireOp",EDGE,"E3167"),sQuery(id+"F0.wireOp",EDGE,"E3168"),sQuery(id+"F0.wireOp",EDGE,"E3169"),sQuery(id+"F0.wireOp",EDGE,"E3170"),sQuery(id+"F0.wireOp",EDGE,"E3171"),sQuery(id+"F0.wireOp",EDGE,"E3172"),sQuery(id+"F0.wireOp",EDGE,"E3173"),sQuery(id+"F0.wireOp",EDGE,"E3174"),sQuery(id+"F0.wireOp",EDGE,"E3175"),sQuery(id+"F0.wireOp",EDGE,"E3176"),sQuery(id+"F0.wireOp",EDGE,"E3177"),sQuery(id+"F0.wireOp",EDGE,"E3178"),sQuery(id+"F0.wireOp",EDGE,"E3179"),sQuery(id+"F0.wireOp",EDGE,"E3180"),sQuery(id+"F0.wireOp",EDGE,"E3181"),sQuery(id+"F0.wireOp",EDGE,"E3182"),sQuery(id+"F0.wireOp",EDGE,"E3183"),sQuery(id+"F0.wireOp",EDGE,"E3184"),sQuery(id+"F0.wireOp",EDGE,"E3185"),sQuery(id+"F0.wireOp",EDGE,"E3186"),sQuery(id+"F0.wireOp",EDGE,"E3187"),sQuery(id+"F0.wireOp",EDGE,"E3188"),sQuery(id+"F0.wireOp",EDGE,"E3189"),sQuery(id+"F0.wireOp",EDGE,"E3190"),sQuery(id+"F0.wireOp",EDGE,"E3191"),sQuery(id+"F0.wireOp",EDGE,"E3192"),sQuery(id+"F0.wireOp",EDGE,"E3193"),sQuery(id+"F0.wireOp",EDGE,"E3194"),sQuery(id+"F0.wireOp",EDGE,"E3195"),sQuery(id+"F0.wireOp",EDGE,"E3196"),sQuery(id+"F0.wireOp",EDGE,"E3197"),sQuery(id+"F0.wireOp",EDGE,"E3198"),sQuery(id+"F0.wireOp",EDGE,"E3199"),sQuery(id+"F0.wireOp",EDGE,"E3200"),sQuery(id+"F0.wireOp",EDGE,"E3201"),sQuery(id+"F0.wireOp",EDGE,"E3202"),sQuery(id+"F0.wireOp",EDGE,"E3203"),sQuery(id+"F0.wireOp",EDGE,"E3204"),sQuery(id+"F0.wireOp",EDGE,"E3205"),sQuery(id+"F0.wireOp",EDGE,"E3206"),sQuery(id+"F0.wireOp",EDGE,"E3207"),sQuery(id+"F0.wireOp",EDGE,"E3208"),sQuery(id+"F0.wireOp",EDGE,"E3209"),sQuery(id+"F0.wireOp",EDGE,"E3210"),sQuery(id+"F0.wireOp",EDGE,"E3211"),sQuery(id+"F0.wireOp",EDGE,"E3212"),sQuery(id+"F0.wireOp",EDGE,"E3213"),sQuery(id+"F0.wireOp",EDGE,"E3214"),sQuery(id+"F0.wireOp",EDGE,"E3215"),sQuery(id+"F0.wireOp",EDGE,"E3216"),sQuery(id+"F0.wireOp",EDGE,"E3217"),sQuery(id+"F0.wireOp",EDGE,"E3218"),sQuery(id+"F0.wireOp",EDGE,"E3219"),sQuery(id+"F0.wireOp",EDGE,"E3220"),sQuery(id+"F0.wireOp",EDGE,"E3221"),sQuery(id+"F0.wireOp",EDGE,"E3222"),sQuery(id+"F0.wireOp",EDGE,"E3223"),sQuery(id+"F0.wireOp",EDGE,"E3224"),sQuery(id+"F0.wireOp",EDGE,"E3225"),sQuery(id+"F0.wireOp",EDGE,"E3226"),sQuery(id+"F0.wireOp",EDGE,"E3227"),sQuery(id+"F0.wireOp",EDGE,"E3228"),sQuery(id+"F0.wireOp",EDGE,"E3229"),sQuery(id+"F0.wireOp",EDGE,"E3230"),sQuery(id+"F0.wireOp",EDGE,"E3231"),sQuery(id+"F0.wireOp",EDGE,"E3232"),sQuery(id+"F0.wireOp",EDGE,"E3233"),sQuery(id+"F0.wireOp",EDGE,"E3234"),sQuery(id+"F0.wireOp",EDGE,"E3235"),sQuery(id+"F0.wireOp",EDGE,"E3236"),sQuery(id+"F0.wireOp",EDGE,"E3237"),sQuery(id+"F0.wireOp",EDGE,"E3238"),sQuery(id+"F0.wireOp",EDGE,"E3239"),sQuery(id+"F0.wireOp",EDGE,"E3240"),sQuery(id+"F0.wireOp",EDGE,"E3241"),sQuery(id+"F0.wireOp",EDGE,"E3242"),sQuery(id+"F0.wireOp",EDGE,"E3243"),sQuery(id+"F0.wireOp",EDGE,"E3244"),sQuery(id+"F0.wireOp",EDGE,"E3245"),sQuery(id+"F0.wireOp",EDGE,"E3246"),sQuery(id+"F0.wireOp",EDGE,"E3247"),sQuery(id+"F0.wireOp",EDGE,"E3248"),sQuery(id+"F0.wireOp",EDGE,"E3249"),sQuery(id+"F0.wireOp",EDGE,"E3250"),sQuery(id+"F0.wireOp",EDGE,"E3251"),sQuery(id+"F0.wireOp",EDGE,"E3252"),sQuery(id+"F0.wireOp",EDGE,"E3253"),sQuery(id+"F0.wireOp",EDGE,"E3254"),sQuery(id+"F0.wireOp",EDGE,"E3255"),sQuery(id+"F0.wireOp",EDGE,"E3256"),sQuery(id+"F0.wireOp",EDGE,"E3257"),sQuery(id+"F0.wireOp",EDGE,"E3258"),sQuery(id+"F0.wireOp",EDGE,"E3259"),sQuery(id+"F0.wireOp",EDGE,"E3260"),sQuery(id+"F0.wireOp",EDGE,"E3261"),sQuery(id+"F0.wireOp",EDGE,"E3262"),sQuery(id+"F0.wireOp",EDGE,"E3263"),sQuery(id+"F0.wireOp",EDGE,"E3264"),sQuery(id+"F0.wireOp",EDGE,"E3265"),sQuery(id+"F0.wireOp",EDGE,"E3266"),sQuery(id+"F0.wireOp",EDGE,"E3267"),sQuery(id+"F0.wireOp",EDGE,"E3268"),sQuery(id+"F0.wireOp",EDGE,"E3269"),sQuery(id+"F0.wireOp",EDGE,"E3270"),sQuery(id+"F0.wireOp",EDGE,"E3271"),sQuery(id+"F0.wireOp",EDGE,"E3272"),sQuery(id+"F0.wireOp",EDGE,"E3273"),sQuery(id+"F0.wireOp",EDGE,"E3274"),sQuery(id+"F0.wireOp",EDGE,"E3275"),sQuery(id+"F0.wireOp",EDGE,"E3276"),sQuery(id+"F0.wireOp",EDGE,"E3277"),sQuery(id+"F0.wireOp",EDGE,"E3278"),sQuery(id+"F0.wireOp",EDGE,"E3279"),sQuery(id+"F0.wireOp",EDGE,"E3280"),sQuery(id+"F0.wireOp",EDGE,"E3281"),sQuery(id+"F0.wireOp",EDGE,"E3282"),sQuery(id+"F0.wireOp",EDGE,"E3283"),sQuery(id+"F0.wireOp",EDGE,"E3284"),sQuery(id+"F0.wireOp",EDGE,"E3285"),sQuery(id+"F0.wireOp",EDGE,"E3286"),sQuery(id+"F0.wireOp",EDGE,"E3287"),sQuery(id+"F0.wireOp",EDGE,"E3288"),sQuery(id+"F0.wireOp",EDGE,"E3289"),sQuery(id+"F0.wireOp",EDGE,"E3290"),sQuery(id+"F0.wireOp",EDGE,"E3291"),sQuery(id+"F0.wireOp",EDGE,"E3292"),sQuery(id+"F0.wireOp",EDGE,"E3293"),sQuery(id+"F0.wireOp",EDGE,"E3294"),sQuery(id+"F0.wireOp",EDGE,"E3295"),sQuery(id+"F0.wireOp",EDGE,"E3296"),sQuery(id+"F0.wireOp",EDGE,"E3297"),sQuery(id+"F0.wireOp",EDGE,"E3298"),sQuery(id+"F0.wireOp",EDGE,"E3299"),sQuery(id+"F0.wireOp",EDGE,"E3300"),sQuery(id+"F0.wireOp",EDGE,"E3301"),sQuery(id+"F0.wireOp",EDGE,"E3302"),sQuery(id+"F0.wireOp",EDGE,"E3303"),sQuery(id+"F0.wireOp",EDGE,"E3304"),sQuery(id+"F0.wireOp",EDGE,"E3305"),sQuery(id+"F0.wireOp",EDGE,"E3306"),sQuery(id+"F0.wireOp",EDGE,"E3307"),sQuery(id+"F0.wireOp",EDGE,"E3308"),sQuery(id+"F0.wireOp",EDGE,"E3309"),sQuery(id+"F0.wireOp",EDGE,"E3310"),sQuery(id+"F0.wireOp",EDGE,"E3311"),sQuery(id+"F0.wireOp",EDGE,"E3312"),sQuery(id+"F0.wireOp",EDGE,"E3313"),sQuery(id+"F0.wireOp",EDGE,"E3314"),sQuery(id+"F0.wireOp",EDGE,"E3315"),sQuery(id+"F0.wireOp",EDGE,"E3316"),sQuery(id+"F0.wireOp",EDGE,"E3317"),sQuery(id+"F0.wireOp",EDGE,"E3318"),sQuery(id+"F0.wireOp",EDGE,"E3319"),sQuery(id+"F0.wireOp",EDGE,"E3320"),sQuery(id+"F0.wireOp",EDGE,"E3321"),sQuery(id+"F0.wireOp",EDGE,"E3322"),sQuery(id+"F0.wireOp",EDGE,"E3323"),sQuery(id+"F0.wireOp",EDGE,"E3324"),sQuery(id+"F0.wireOp",EDGE,"E3325"),sQuery(id+"F0.wireOp",EDGE,"E3326"),sQuery(id+"F0.wireOp",EDGE,"E3327"),sQuery(id+"F0.wireOp",EDGE,"E3328"),sQuery(id+"F0.wireOp",EDGE,"E3329"),sQuery(id+"F0.wireOp",EDGE,"E3330"),sQuery(id+"F0.wireOp",EDGE,"E3331"),sQuery(id+"F0.wireOp",EDGE,"E3332"),sQuery(id+"F0.wireOp",EDGE,"E3333"),sQuery(id+"F0.wireOp",EDGE,"E3334"),sQuery(id+"F0.wireOp",EDGE,"E3335"),sQuery(id+"F0.wireOp",EDGE,"E3336"),sQuery(id+"F0.wireOp",EDGE,"E3337"),sQuery(id+"F0.wireOp",EDGE,"E3338"),sQuery(id+"F0.wireOp",EDGE,"E3339"),sQuery(id+"F0.wireOp",EDGE,"E3340"),sQuery(id+"F0.wireOp",EDGE,"E3341"),sQuery(id+"F0.wireOp",EDGE,"E3342"),sQuery(id+"F0.wireOp",EDGE,"E3343"),sQuery(id+"F0.wireOp",EDGE,"E3344"),sQuery(id+"F0.wireOp",EDGE,"E3345"),sQuery(id+"F0.wireOp",EDGE,"E3346"),sQuery(id+"F0.wireOp",EDGE,"E3347"),sQuery(id+"F0.wireOp",EDGE,"E3348"),sQuery(id+"F0.wireOp",EDGE,"E3349"),sQuery(id+"F0.wireOp",EDGE,"E3350"),sQuery(id+"F0.wireOp",EDGE,"E3351"),sQuery(id+"F0.wireOp",EDGE,"E3352"),sQuery(id+"F0.wireOp",EDGE,"E3353"),sQuery(id+"F0.wireOp",EDGE,"E3354"),sQuery(id+"F0.wireOp",EDGE,"E3355"),sQuery(id+"F0.wireOp",EDGE,"E3356"),sQuery(id+"F0.wireOp",EDGE,"E3357"),sQuery(id+"F0.wireOp",EDGE,"E3358"),sQuery(id+"F0.wireOp",EDGE,"E3359"),sQuery(id+"F0.wireOp",EDGE,"E3360"),sQuery(id+"F0.wireOp",EDGE,"E3361"),sQuery(id+"F0.wireOp",EDGE,"E3362"),sQuery(id+"F0.wireOp",EDGE,"E3363"),sQuery(id+"F0.wireOp",EDGE,"E3364"),sQuery(id+"F0.wireOp",EDGE,"E3365"),sQuery(id+"F0.wireOp",EDGE,"E3366"),sQuery(id+"F0.wireOp",EDGE,"E3367"),sQuery(id+"F0.wireOp",EDGE,"E3368"),sQuery(id+"F0.wireOp",EDGE,"E3369"),sQuery(id+"F0.wireOp",EDGE,"E3370"),sQuery(id+"F0.wireOp",EDGE,"E3371"),sQuery(id+"F0.wireOp",EDGE,"E3372"),sQuery(id+"F0.wireOp",EDGE,"E3373"),sQuery(id+"F0.wireOp",EDGE,"E3374"),sQuery(id+"F0.wireOp",EDGE,"E3375"),sQuery(id+"F0.wireOp",EDGE,"E3376"),sQuery(id+"F0.wireOp",EDGE,"E3377"),sQuery(id+"F0.wireOp",EDGE,"E3378"),sQuery(id+"F0.wireOp",EDGE,"E3379"),sQuery(id+"F0.wireOp",EDGE,"E3380"),sQuery(id+"F0.wireOp",EDGE,"E3381"),sQuery(id+"F0.wireOp",EDGE,"E3382"),sQuery(id+"F0.wireOp",EDGE,"E3383"),sQuery(id+"F0.wireOp",EDGE,"E3384"),sQuery(id+"F0.wireOp",EDGE,"E3385"),sQuery(id+"F0.wireOp",EDGE,"E3386"),sQuery(id+"F0.wireOp",EDGE,"E3387"),sQuery(id+"F0.wireOp",EDGE,"E3388"),sQuery(id+"F0.wireOp",EDGE,"E3389"),sQuery(id+"F0.wireOp",EDGE,"E3390"),sQuery(id+"F0.wireOp",EDGE,"E3391"),sQuery(id+"F0.wireOp",EDGE,"E3392"),sQuery(id+"F0.wireOp",EDGE,"E3393"),sQuery(id+"F0.wireOp",EDGE,"E3394"),sQuery(id+"F0.wireOp",EDGE,"E3395"),sQuery(id+"F0.wireOp",EDGE,"E3396"),sQuery(id+"F0.wireOp",EDGE,"E3397"),sQuery(id+"F0.wireOp",EDGE,"E3398"),sQuery(id+"F0.wireOp",EDGE,"E3399"),sQuery(id+"F0.wireOp",EDGE,"E3400"),sQuery(id+"F0.wireOp",EDGE,"E3401"),sQuery(id+"F0.wireOp",EDGE,"E3402"),sQuery(id+"F0.wireOp",EDGE,"E3403"),sQuery(id+"F0.wireOp",EDGE,"E3404"),sQuery(id+"F0.wireOp",EDGE,"E3405"),sQuery(id+"F0.wireOp",EDGE,"E3406"),sQuery(id+"F0.wireOp",EDGE,"E3407"),sQuery(id+"F0.wireOp",EDGE,"E3408"),sQuery(id+"F0.wireOp",EDGE,"E3409"),sQuery(id+"F0.wireOp",EDGE,"E3410"),sQuery(id+"F0.wireOp",EDGE,"E3411"),sQuery(id+"F0.wireOp",EDGE,"E3412"),sQuery(id+"F0.wireOp",EDGE,"E3413"),sQuery(id+"F0.wireOp",EDGE,"E3414"),sQuery(id+"F0.wireOp",EDGE,"E3415"),sQuery(id+"F0.wireOp",EDGE,"E3416"),sQuery(id+"F0.wireOp",EDGE,"E3417"),sQuery(id+"F0.wireOp",EDGE,"E3418"),sQuery(id+"F0.wireOp",EDGE,"E3419"),sQuery(id+"F0.wireOp",EDGE,"E3420"),sQuery(id+"F0.wireOp",EDGE,"E3421"),sQuery(id+"F0.wireOp",EDGE,"E3422"),sQuery(id+"F0.wireOp",EDGE,"E3423"),sQuery(id+"F0.wireOp",EDGE,"E3424"),sQuery(id+"F0.wireOp",EDGE,"E3425"),sQuery(id+"F0.wireOp",EDGE,"E3426"),sQuery(id+"F0.wireOp",EDGE,"E3427"),sQuery(id+"F0.wireOp",EDGE,"E3428"),sQuery(id+"F0.wireOp",EDGE,"E3429"),sQuery(id+"F0.wireOp",EDGE,"E3430"),sQuery(id+"F0.wireOp",EDGE,"E3431"),sQuery(id+"F0.wireOp",EDGE,"E3432"),sQuery(id+"F0.wireOp",EDGE,"E3433"),sQuery(id+"F0.wireOp",EDGE,"E3434"),sQuery(id+"F0.wireOp",EDGE,"E3435"),sQuery(id+"F0.wireOp",EDGE,"E3436"),sQuery(id+"F0.wireOp",EDGE,"E3437"),sQuery(id+"F0.wireOp",EDGE,"E3438"),sQuery(id+"F0.wireOp",EDGE,"E3439"),sQuery(id+"F0.wireOp",EDGE,"E3440"),sQuery(id+"F0.wireOp",EDGE,"E3441"),sQuery(id+"F0.wireOp",EDGE,"E3442"),sQuery(id+"F0.wireOp",EDGE,"E3443"),sQuery(id+"F0.wireOp",EDGE,"E3444"),sQuery(id+"F0.wireOp",EDGE,"E3445"),sQuery(id+"F0.wireOp",EDGE,"E3446"),sQuery(id+"F0.wireOp",EDGE,"E3447"),sQuery(id+"F0.wireOp",EDGE,"E3448"),sQuery(id+"F0.wireOp",EDGE,"E3449"),sQuery(id+"F0.wireOp",EDGE,"E3450"),sQuery(id+"F0.wireOp",EDGE,"E3451"),sQuery(id+"F0.wireOp",EDGE,"E3452"),sQuery(id+"F0.wireOp",EDGE,"E3453"),sQuery(id+"F0.wireOp",EDGE,"E3454"),sQuery(id+"F0.wireOp",EDGE,"E3455")])],"isStart":false});
            var sketch = newSketch(context, id + "F2", { "sketchPlane" : qUnion([Q0])});
            skCircle(sketch, "E3456", {"center": v(0, 0) * mm, "radius": 1.5 * mm});
            skSolve(sketch);
        }
        {
            var Q0;
            Q0 = qSketchRegion(id + "F2", true);
            extrude(context, id + "F3", {"entities" : qUnion([Q0]), "operationType" : NewBodyOperationType.REMOVE, "oppositeDirection" : true, "depth" : 25 * mm, "offsetDistance" : 25 * mm});
        }
    });
